FCSTD DOCUMENT  (FreeCAD 0.19R21858 (Git))
Label: printer_assembly
License: All rights reserved
LicenseURL: http://en.wikipedia.org/wiki/All_rights_reserved
objects: TechDraw::DrawViewDimension×171, Part::Feature×140, Sketcher::SketchObject×82, App::Part×58, TechDraw::DrawProjGroupItem×34, App::LinkElement×33, PartDesign::Body×30, PartDesign::Pad×29, PartDesign::Pocket×27, App::Link×26, PartDesign::Hole×16, TechDraw::DrawViewDimExtent×15, Part::FeaturePython×12, TechDraw::DrawProjGroup×12, TechDraw::DrawSVGTemplate×11, TechDraw::DrawPage×11, TechDraw::DrawViewAnnotation×10, TechDraw::DrawLeaderLine×10, TechDraw::DrawViewPart×9, App::DocumentObjectGroup×8, +10 more types
note: 449 computed .brp shape members not serialized (recipe doc carries the construction recipe); baked Part::Feature solids carry a one-line shape summary decoded from their .brp

FEATURE [Part::Feature] Part__Feature  label="KLF08"
  Placement = pos=(25.4,6e-15,50.8) rot=(0.57735,-0.57735,-0.57735;2.0944rad)
  shape: bbox 28.15 x 47.92 x 11.37 mm, 341 faces, 4 solids (baked)
FEATURE [Part::Cylinder] Cylinder  label="T8_leadscrew"
  Angle = 360
  AttacherType = Attacher::AttachEngine3D
  Height = 433
  Placement = pos=(25.4,0,43) rot=(0,0,1;0rad)
  Radius = 4
FEATURE [Sketcher::SketchObject] Sketch010
  AttachmentOffset = pos=(0,0,50.8) rot=(0,0,1;0rad)
  MapMode = 5
  Placement = pos=(0,0,50.8) rot=(0,0,1;0rad)
  Support = -> [XY_Plane010]
  expr: Constraints[9] = (2 * 31 ^ 2) ^ 0.5
  sketch-geometry (4):
    g0: Circle CenterX=25.4 CenterY=0 CenterZ=0 NormalX=0 NormalY=0 NormalZ=1 AngleXU=0 Radius=11
    g1: Circle CenterX=25.4 CenterY=21.9203 CenterZ=0 NormalX=0 NormalY=0 NormalZ=1 AngleXU=0 Radius=1.55
    g2: Circle CenterX=25.4 CenterY=-21.9203 CenterZ=0 NormalX=0 NormalY=0 NormalZ=1 AngleXU=0 Radius=1.55
    g3: LineSegment [constr] StartX=25.4 StartY=21.9203 StartZ=0 EndX=25.4 EndY=-21.9203 EndZ=0
  constraints (10):
    c: PointOnObject(g0,g-1)
    c: Coincident(g3,g1)
    c: Coincident(g3,g2)
    c: DistanceX(g-1,g0) = 25.4
    c: PointOnObject(g0,g3)
    c: Symmetric(g1,g2,g-1)
    c: Equal(g1,g2)
    c: Diameter(g1) = 3.1
    c: Diameter(g0) = 22
    c: DistanceY(g2,g1) = 43.8406
FEATURE [Sketcher::SketchObject] Sketch011
  MapMode = 5
  Placement = pos=(0,0,0) rot=(0.57735,0.57735,0.57735;2.0944rad)
  Support = -> [YZ_Plane008]
  sketch-geometry (4):
    g0: LineSegment StartX=-20 StartY=20 StartZ=0 EndX=20 EndY=20 EndZ=0
    g1: LineSegment StartX=20 StartY=20 StartZ=0 EndX=20 EndY=-5 EndZ=0
    g2: LineSegment StartX=20 StartY=-5 StartZ=0 EndX=-20 EndY=-5 EndZ=0
    g3: LineSegment StartX=-20 StartY=-5 StartZ=0 EndX=-20 EndY=20 EndZ=0
  constraints (12):
    c: Coincident(g0,g1)
    c: Coincident(g1,g2)
    c: Coincident(g2,g3)
    c: Coincident(g3,g0)
    c: Horizontal(g0)
    c: Horizontal(g2)
    c: Vertical(g1)
    c: Vertical(g3)
    c: DistanceX(g0,g0) = 40
    c: DistanceY(g1,g0) = 25
    c: DistanceY(g-1,g0) = 20
    c: DistanceX(g-1,g0) = 20
FEATURE [Sketcher::SketchObject] Sketch006
  AttachmentOffset = pos=(0,0,50.8) rot=(0,0,1;0rad)
  MapMode = 5
  Placement = pos=(50.8,-1.13e-14,1.13e-14) rot=(0.57735,0.57735,0.57735;2.0944rad)
  Support = -> [YZ_Plane011]
  sketch-geometry (8):
    g0: ArcOfCircle CenterX=-131 CenterY=25.4 CenterZ=0 NormalX=0 NormalY=0 NormalZ=1 AngleXU=0 Radius=5 StartAngle=1.5708 EndAngle=4.71239
    g1: ArcOfCircle CenterX=-95 CenterY=25.4 CenterZ=0 NormalX=0 NormalY=0 NormalZ=1 AngleXU=0 Radius=5 StartAngle=4.71239 EndAngle=7.85398
    g2: LineSegment StartX=-131 StartY=20.4 StartZ=0 EndX=-95 EndY=20.4 EndZ=0
    g3: LineSegment StartX=-131 StartY=30.4 StartZ=0 EndX=-95 EndY=30.4 EndZ=0
    g4: ArcOfCircle CenterX=95 CenterY=25.4 CenterZ=0 NormalX=0 NormalY=0 NormalZ=1 AngleXU=0 Radius=5 StartAngle=1.5708 EndAngle=4.71239
    g5: ArcOfCircle CenterX=131 CenterY=25.4 CenterZ=0 NormalX=0 NormalY=0 NormalZ=1 AngleXU=0 Radius=5 StartAngle=4.71239 EndAngle=7.85398
    g6: LineSegment StartX=95 StartY=20.4 StartZ=0 EndX=131 EndY=20.4 EndZ=0
    g7: LineSegment StartX=95 StartY=30.4 StartZ=0 EndX=131 EndY=30.4 EndZ=0
  constraints (18):
    c: Tangent(g0,g3) = 1.5708
    c: Tangent(g0,g2) = -1.5708
    c: Tangent(g2,g1) = -1.5708
    c: Tangent(g3,g1) = 1.5708
    c: Horizontal(g2)
    c: Equal(g0,g1)
    c: Tangent(g4,g7) = 1.5708
    c: Tangent(g4,g6) = -1.5708
    c: Tangent(g6,g5) = -1.5708
    c: Tangent(g7,g5) = 1.5708
    c: Horizontal(g6)
    c: Diameter(g4) = 10
    c: Equal(g4,g1)
    c: Symmetric(g4,g1,g-2)
    c: Symmetric(g0,g5,g-2)
    c: DistanceY(g-1,g4) = 25.4
    c: DistanceX(g1,g4) = 190
    c: DistanceX(g0,g5) = 262
FEATURE [Sketcher::SketchObject] Sketch012
  AttachmentOffset = pos=(0,0,50.8) rot=(0,0,1;0rad)
  MapMode = 5
  Placement = pos=(0,0,50.8) rot=(0,0,1;0rad)
  Support = -> [XY_Plane011]
  sketch-geometry (4):
    g0: Circle CenterX=25.4 CenterY=0 CenterZ=0 NormalX=0 NormalY=0 NormalZ=1 AngleXU=0 Radius=9
    g1: Circle CenterX=25.4 CenterY=18.5 CenterZ=0 NormalX=0 NormalY=0 NormalZ=1 AngleXU=0 Radius=2.25
    g2: Circle CenterX=25.4 CenterY=-18.5 CenterZ=0 NormalX=0 NormalY=0 NormalZ=1 AngleXU=0 Radius=2.25
    g3: LineSegment [constr] StartX=25.4 StartY=18.5 StartZ=0 EndX=25.4 EndY=-18.5 EndZ=0
  constraints (10):
    c: PointOnObject(g0,g-1)
    c: Coincident(g3,g1)
    c: Coincident(g3,g2)
    c: PointOnObject(g0,g3)
    c: Symmetric(g1,g2,g-1)
    c: Equal(g1,g2)
    c: DistanceY(g2,g1) = 37
    c: DistanceX(g-1,g0) = 25.4
    c: Diameter(g1) = 4.5
    c: Diameter(g0) = 18
FEATURE [Part::Cylinder] Cylinder001  label="12x500mm_shaft"
  Angle = 360
  AttacherType = Attacher::AttachEngine3D
  Height = 500
  Placement = pos=(38.74,95.03,0) rot=(0,0,1;0rad)
  Radius = 6
FEATURE [App::Link] Link  label="12x500mm_shaft001"
  LinkPlacement = pos=(38.74,-95.03,0) rot=(0,0,1;0rad)
  LinkedObject = -> Cylinder001
  Placement = pos=(38.74,-95.03,0) rot=(0,0,1;0rad)
FEATURE [App::Link] Link010  label="adj_assy001"
  LinkPlacement = pos=(-153,158,0) rot=(0,0,1;3.92699rad)
  LinkedObject = -> Part011
  Placement = pos=(-153,158,0) rot=(0,0,1;3.92699rad)
FEATURE [App::Link] Link001  label="adj_assy002"
  LinkPlacement = pos=(-153,-158,0) rot=(0,0,-1;0.785398rad)
  LinkedObject = -> Part011
  Placement = pos=(-153,-158,0) rot=(0,0,-1;0.785398rad)
FEATURE [Part::Cylinder] Cylinder002  label="0.25in_threaded_rod"
  Angle = 360
  AttacherType = Attacher::AttachEngine3D
  Height = 40
  Placement = pos=(0,0,-33.65) rot=(0,0,1;0rad)
  Radius = 3.175
FEATURE [Sketcher::SketchObject] Sketch013
  MapMode = 5
  Support = -> [XY_Plane016]
  sketch-geometry (7):
    g0: LineSegment StartX=-160 StartY=165 StartZ=0 EndX=160 EndY=165 EndZ=0
    g1: LineSegment StartX=160 StartY=165 StartZ=0 EndX=160 EndY=-165 EndZ=0
    g2: LineSegment StartX=160 StartY=-165 StartZ=0 EndX=-160 EndY=-165 EndZ=0
    g3: LineSegment StartX=-160 StartY=-165 StartZ=0 EndX=-160 EndY=165 EndZ=0
    g4: Circle CenterX=-153 CenterY=158 CenterZ=0 NormalX=0 NormalY=0 NormalZ=1 AngleXU=0 Radius=3.175
    g5: Circle CenterX=-153 CenterY=-158 CenterZ=0 NormalX=0 NormalY=0 NormalZ=1 AngleXU=0 Radius=3.175
    g6: Circle CenterX=153 CenterY=0 CenterZ=0 NormalX=0 NormalY=0 NormalZ=1 AngleXU=0 Radius=3.175
  constraints (20):
    c: Coincident(g0,g1)
    c: Coincident(g1,g2)
    c: Coincident(g2,g3)
    c: Coincident(g3,g0)
    c: Horizontal(g0)
    c: Horizontal(g2)
    c: Vertical(g1)
    c: Vertical(g3)
    c: DistanceX(g0,g0) = 320  'bed_w'
    c: DistanceY(g1,g1) = 330  'bed_d'
    c: DistanceY(g-1,g0) = 165
    c: DistanceX(g-1,g0) = 160
    c: DistanceX(g4,g-1) = 153
    c: DistanceY(g-1,g4) = 158
    c: Symmetric(g4,g5,g-1)
    c: PointOnObject(g6,g-1)
    c: DistanceX(g-1,g6) = 153
    c: Equal(g4,g5)
    c: Equal(g5,g6)
    c: Diameter(g4) = 6.35  'adj_screw_dia'
FEATURE [PartDesign::Pad] Pad006
  AllowMultiFace = false
  Length = 6.35
  Length2 = 100
  Profile = -> Sketch013
  Type = 0
FEATURE [PartDesign::Body] Body006
  Group = -> [Sketch013,Pad006]
  Origin = -> Origin016
  Tip = -> Pad006
FEATURE [App::Part] Part001  label="bed_plate"
  Group = -> [Body006]
  Origin = -> Origin013
FEATURE [Sketcher::SketchObject] Sketch014
  MapMode = 5
  Placement = pos=(0,0,0) rot=(1,0,0;1.5708rad)
  Support = -> [XZ_Plane001]
  expr: Constraints[15] = 1.25 * 25.4
  expr: Constraints[17] = 0.5 * 25.4
  expr: Constraints[14] = 0.2 * 25.4
  expr: Constraints[13] = 0.2 * 25.4
  expr: Constraints[12] = 1 / 8 * 25.4
  sketch-geometry (6):
    g0: LineSegment StartX=0 StartY=3.175 StartZ=0 EndX=10.16 EndY=3.175 EndZ=0
    g1: LineSegment StartX=10.16 StartY=3.175 StartZ=0 EndX=10.16 EndY=7.62 EndZ=0
    g2: LineSegment StartX=10.16 StartY=7.62 StartZ=0 EndX=5.08 EndY=12.7 EndZ=0
    g3: LineSegment StartX=5.08 StartY=12.7 StartZ=0 EndX=5.08 EndY=31.75 EndZ=0
    g4: LineSegment StartX=5.08 StartY=31.75 StartZ=0 EndX=0 EndY=31.75 EndZ=0
    g5: LineSegment StartX=0 StartY=31.75 StartZ=0 EndX=0 EndY=3.175 EndZ=0
  constraints (18):
    c: Coincident(g0,g1)
    c: Coincident(g1,g2)
    c: Coincident(g2,g3)
    c: Vertical(g3)
    c: Coincident(g3,g4)
    c: Horizontal(g4)
    c: Coincident(g4,g5)
    c: Coincident(g5,g0)
    c: Vertical(g5)
    c: Horizontal(g0)
    c: Vertical(g1)
    c: Angle(g2,g0) = 0.785398
    c: DistanceY(g-1,g0) = 3.175
    c: DistanceX(g4,g4) = 5.08
    c: DistanceX(g2,g1) = 5.08
    c: DistanceY(g-1,g4) = 31.75
    c: PointOnObject(g0,g-2)
    c: DistanceY(g-1,g2) = 12.7
FEATURE [PartDesign::Revolution] Revolution
  AllowMultiFace = false
  Angle = 360
  Axis = (1,0,0)
  Base = (0,0,0)
  Placement = pos=(0,0,0) rot=(1,0,0;1.5708rad)
  Profile = -> Sketch014
  ReferenceAxis = -> X_Axis001
FEATURE [PartDesign::Body] Body007
  Group = -> [Sketch014,Revolution]
  Origin = -> Origin001
  Tip = -> Revolution
FEATURE [App::Part] Part012  label="adj_knob"
  Group = -> [Body007]
  Origin = -> Origin017
  Placement = pos=(1.4e-15,0,-6.35) rot=(0,1,0;1.5708rad)
FEATURE [Sketcher::SketchObject] Sketch015
  MapMode = 5
  Placement = pos=(0,0,0) rot=(0.57735,0.57735,0.57735;2.0944rad)
  Support = -> [YZ_Plane019]
  sketch-geometry (5):
    g0: LineSegment StartX=0 StartY=0 StartZ=0 EndX=61.979 EndY=0 EndZ=0
    g1: LineSegment StartX=113.021 StartY=-30 StartZ=0 EndX=175 EndY=-30 EndZ=0
    g2: LineSegment StartX=79.9395 StartY=-7.43949 StartZ=0 EndX=95.0605 EndY=-22.5605 EndZ=0
    g3: ArcOfCircle CenterX=61.979 CenterY=-25.4 CenterZ=0 NormalX=0 NormalY=0 NormalZ=1 AngleXU=0 Radius=25.4 StartAngle=0.785398 EndAngle=1.5708
    g4: ArcOfCircle CenterX=113.021 CenterY=-4.6 CenterZ=0 NormalX=0 NormalY=0 NormalZ=1 AngleXU=0 Radius=25.4 StartAngle=3.92699 EndAngle=4.71239
  constraints (13):
    c: Coincident(g0,g-1)
    c: Horizontal(g1)
    c: Tangent(g0,g3) = 1.5708
    c: Tangent(g2,g3) = 1.5708
    c: Tangent(g2,g4) = -1.5708
    c: Tangent(g1,g4) = -1.5708
    c: Equal(g3,g4)
    c: Horizontal(g0)
    c: Equal(g0,g1)
    c: DistanceY(g1,g0) = 30
    c: DistanceX(g0,g1) = 175
    c: Radius(g3) = 25.4
    c: Angle(g0,g2) = 2.35619
FEATURE [Sketcher::SketchObject] Sketch016
  MapMode = 5
  Support = -> [XY_Plane019]
  sketch-geometry (4):
    g0: ArcOfCircle CenterX=0 CenterY=0 CenterZ=0 NormalX=0 NormalY=0 NormalZ=1 AngleXU=0 Radius=8 StartAngle=3.14159 EndAngle=6.28319
    g1: ArcOfCircle CenterX=-2e-16 CenterY=25 CenterZ=0 NormalX=0 NormalY=0 NormalZ=1 AngleXU=0 Radius=8 StartAngle=0 EndAngle=3.14159
    g2: LineSegment StartX=8 StartY=-2e-15 StartZ=0 EndX=8 EndY=25 EndZ=0
    g3: LineSegment StartX=-8 StartY=-2.6e-15 StartZ=0 EndX=-8 EndY=25 EndZ=0
  constraints (9):
    c: Tangent(g0,g3) = 1.5708
    c: Tangent(g0,g2) = -1.5708
    c: Tangent(g2,g1) = -1.5708
    c: Tangent(g3,g1) = 1.5708
    c: Vertical(g2)
    c: Equal(g0,g1)
    c: Coincident(g0,g-1)
    c: Diameter(g1) = 16
    c: DistanceY(g0,g1) = 25
FEATURE [Sketcher::SketchObject] Sketch017
  MapMode = 5
  Support = -> [XY_Plane019]
  sketch-geometry (4):
    g0: ArcOfCircle CenterX=0 CenterY=125 CenterZ=0 NormalX=0 NormalY=0 NormalZ=1 AngleXU=0 Radius=3.5 StartAngle=3.14159 EndAngle=6.28319
    g1: ArcOfCircle CenterX=-6.15e-14 CenterY=165 CenterZ=0 NormalX=0 NormalY=0 NormalZ=1 AngleXU=0 Radius=3.5 StartAngle=-3.73e-14 EndAngle=3.14159
    g2: LineSegment StartX=3.5 StartY=125 StartZ=0 EndX=3.5 EndY=165 EndZ=0
    g3: LineSegment StartX=-3.5 StartY=125 StartZ=0 EndX=-3.5 EndY=165 EndZ=0
  constraints (10):
    c: Tangent(g0,g3) = 1.5708
    c: Tangent(g0,g2) = -1.5708
    c: Tangent(g2,g1) = -1.5708
    c: Tangent(g3,g1) = 1.5708
    c: Vertical(g2)
    c: Equal(g0,g1)
    c: PointOnObject(g0,g-2)
    c: DistanceY(g-1,g0) = 125
    c: DistanceY(g-1,g1) = 165
    c: Diameter(g1) = 7
FEATURE [Sketcher::SketchObject] Sketch018
  MapMode = 5
  Support = -> [XY_Plane021]
  sketch-geometry (4):
    g0: LineSegment StartX=-63.5 StartY=177.8 StartZ=0 EndX=393.7 EndY=177.8 EndZ=0
    g1: LineSegment StartX=393.7 StartY=177.8 StartZ=0 EndX=393.7 EndY=-177.8 EndZ=0
    g2: LineSegment StartX=393.7 StartY=-177.8 StartZ=0 EndX=-63.5 EndY=-177.8 EndZ=0
    g3: LineSegment StartX=-63.5 StartY=-177.8 StartZ=0 EndX=-63.5 EndY=177.8 EndZ=0
  constraints (11):
    c: Coincident(g0,g1)
    c: Coincident(g1,g2)
    c: Coincident(g2,g3)
    c: Coincident(g3,g0)
    c: Horizontal(g0)
    c: Horizontal(g2)
    c: Vertical(g1)
    c: DistanceY(g-1,g0) = 177.8
    c: DistanceX(g0,g0) = 457.2
    c: DistanceX(g0,g-1) = 63.5
    c: Symmetric(g0,g2,g-1)
FEATURE [PartDesign::Pad] Pad008
  AllowMultiFace = false
  Length = 19.05
  Length2 = 100
  Profile = -> Sketch018
  Reversed = true
  Type = 0
FEATURE [Sketcher::SketchObject] Sketch019
  MapMode = 5
  Support = -> [XY_Plane021]
  sketch-geometry (12):
    g0: LineSegment StartX=0 StartY=-127 StartZ=0 EndX=0 EndY=-177.8 EndZ=0
    g1: LineSegment StartX=0 StartY=-177.8 StartZ=0 EndX=-12.7 EndY=-177.8 EndZ=0
    g2: LineSegment StartX=-12.7 StartY=-177.8 StartZ=0 EndX=-12.7 EndY=-136.525 EndZ=0
    g3: LineSegment StartX=-63.5 StartY=-127 StartZ=0 EndX=-63.5 EndY=-136.525 EndZ=0
    g4: LineSegment StartX=-63.5 StartY=-136.525 StartZ=0 EndX=-12.7 EndY=-136.525 EndZ=0
    g5: LineSegment StartX=-63.5 StartY=-127 StartZ=0 EndX=0 EndY=-127 EndZ=0
    g6: LineSegment StartX=-12.7 StartY=136.525 StartZ=0 EndX=-63.5 EndY=136.525 EndZ=0
    g7: LineSegment StartX=-63.5 StartY=136.525 StartZ=0 EndX=-63.5 EndY=127 EndZ=0
    g8: LineSegment StartX=-63.5 StartY=127 StartZ=0 EndX=0 EndY=127 EndZ=0
    g9: LineSegment StartX=0 StartY=127 StartZ=0 EndX=0 EndY=177.8 EndZ=0
    g10: LineSegment StartX=0 StartY=177.8 StartZ=0 EndX=-12.7 EndY=177.8 EndZ=0
    g11: LineSegment StartX=-12.7 StartY=177.8 StartZ=0 EndX=-12.7 EndY=136.525 EndZ=0
  constraints (36):
    c: Coincident(g0,g1)
    c: Coincident(g1,g2)
    c: Horizontal(g1)
    c: Vertical(g0)
    c: Vertical(g2)
    c: Coincident(g3,g4)
    c: Horizontal(g4)
    c: Vertical(g3)
    c: Coincident(g2,g4)
    c: Coincident(g5,g3)
    c: Coincident(g5,g0)
    c: Horizontal(g5)
    c: DistanceY(g0,g-1) = 177.8
    c: DistanceX(g5,g5) = 63.5
    c: DistanceY(g3,g3) = 9.525
    c: PointOnObject(g0,g-2)
    c: DistanceY(g0,g0) = 50.8
    c: DistanceX(g1,g1) = 12.7
    c: Horizontal(g6)
    c: Coincident(g6,g7)
    c: Coincident(g7,g8)
    c: Coincident(g8,g9)
    c: Coincident(g9,g10)
    c: Coincident(g10,g11)
    c: Coincident(g11,g6)
    c: Vertical(g11)
    c: Vertical(g9)
    c: Vertical(g7)
    c: Horizontal(g10)
    c: Horizontal(g8)
    c: PointOnObject(g8,g-2)
    c: DistanceX(g10,g10) = 12.7
    c: DistanceX(g8,g8) = 63.5
    c: DistanceY(g9,g9) = 50.8
    c: DistanceY(g7,g7) = 9.525
    c: DistanceY(g-1,g9) = 177.8
FEATURE [PartDesign::Pad] Pad009
  AllowMultiFace = false
  BaseFeature = -> Pad008
  Length = 127
  Length2 = 100
  Profile = -> Sketch019
  Type = 0
FEATURE [Sketcher::SketchObject] Sketch020
  MapMode = 5
  Placement = pos=(0,0,0) rot=(1,0,0;1.5708rad)
  Support = -> [XZ_Plane021]
  sketch-geometry (3):
    g0: LineSegment StartX=-63.5 StartY=0 StartZ=0 EndX=-12.7 EndY=127 EndZ=0
    g1: LineSegment StartX=-12.7 StartY=127 StartZ=0 EndX=-63.5 EndY=127 EndZ=0
    g2: LineSegment StartX=-63.5 StartY=127 StartZ=0 EndX=-63.5 EndY=0 EndZ=0
  constraints (9):
    c: Coincident(g0,g1)
    c: Horizontal(g1)
    c: Coincident(g1,g2)
    c: Coincident(g2,g0)
    c: Vertical(g2)
    c: PointOnObject(g0,g-1)
    c: DistanceY(g2,g2) = 127
    c: DistanceX(g0,g-1) = 12.7
    c: DistanceX(g0,g-1) = 63.5
FEATURE [PartDesign::Pocket] Pocket010
  AllowMultiFace = false
  BaseFeature = -> Pad009
  Length = 5
  Length2 = 100
  Midplane = true
  Profile = -> Sketch020
  Type = 1
FEATURE [Sketcher::SketchObject] Sketch021
  MapMode = 5
  Placement = pos=(0,0,0) rot=(0.57735,0.57735,0.57735;2.0944rad)
  Support = -> [YZ_Plane021]
  sketch-geometry (4):
    g0: Circle CenterX=-152.4 CenterY=101.6 CenterZ=0 NormalX=0 NormalY=0 NormalZ=1 AngleXU=0 Radius=6.35
    g1: Circle CenterX=-152.4 CenterY=25.4 CenterZ=0 NormalX=0 NormalY=0 NormalZ=1 AngleXU=0 Radius=6.35
    g2: Circle CenterX=152.4 CenterY=101.6 CenterZ=0 NormalX=0 NormalY=0 NormalZ=1 AngleXU=0 Radius=6.35
    g3: Circle CenterX=152.4 CenterY=25.4 CenterZ=0 NormalX=0 NormalY=0 NormalZ=1 AngleXU=0 Radius=6.35
  constraints (10):
    c: Symmetric(g1,g3,g-2)
    c: Symmetric(g0,g2,g-2)
    c: DistanceX(g0,g-1) = 152.4
    c: Vertical(g0,g1)
    c: Diameter(g0) = 12.7
    c: Equal(g0,g1)
    c: Equal(g1,g3)
    c: Equal(g3,g2)
    c: DistanceY(g-1,g0) = 101.6
    c: DistanceY(g-1,g1) = 25.4
FEATURE [PartDesign::Pocket] Pocket009
  AllowMultiFace = false
  BaseFeature = -> Pocket010
  Length = 5
  Length2 = 100
  Profile = -> Sketch021
  Type = 1
FEATURE [Part::Feature] Part__Feature001  label="V-Slot 20x80x500 Linear Rail"
  Placement = pos=(250,0,16.35) rot=(0,-1,0;1.5708rad)
  shape: bbox 500 x 80 x 20 mm, 204 faces (baked)
FEATURE [App::LinkElement] Link007_i0
  LinkPlacement = pos=(-95,21,8.34465e-06) rot=(1,0,0;1.5708rad)
  LinkedObject = -> Part__Feature002
  Placement = pos=(-95,21,8.34465e-06) rot=(1,0,0;1.5708rad)
FEATURE [App::LinkElement] Link007_i1
  LinkPlacement = pos=(95,-21,-1.62125e-05) rot=(1,0,0;1.5708rad)
  LinkedObject = -> Part__Feature002
  Placement = pos=(95,-21,-1.62125e-05) rot=(1,0,0;1.5708rad)
FEATURE [Part::Feature] Part__Feature002  label="SC12UU"
  Placement = pos=(-95,-21,5e-15) rot=(1,0,0;1.5708rad)
  shape: bbox 42 x 36 x 28 mm, 110 faces (baked)
FEATURE [App::LinkElement] Link007_i2
  LinkPlacement = pos=(95,21,-6.07967e-06) rot=(1,0,0;1.5708rad)
  LinkedObject = -> Part__Feature002
  Placement = pos=(95,21,-6.07967e-06) rot=(1,0,0;1.5708rad)
FEATURE [App::Link] Link007  label="SC12UU001"
  ElementCount = 3
  ElementList = -> [Link007_i0,Link007_i1,Link007_i2]
  LinkedObject = -> Part__Feature002
FEATURE [App::DocumentObjectGroup] Group002  label="SCS12UU"
  Group = -> [Part__Feature002,Link007]
FEATURE [Part::Feature] Part__Feature034  label="8mm Acme Anti Backlash Nut Block"
  Placement = pos=(-4e-15,-16.5,-28) rot=(0,0.707107,0.707107;3.14159rad)
  shape: bbox 34 x 33 x 12 mm, 45 faces (baked)
FEATURE [Part::Cylinder] Cylinder003  label="5mm_shaft"
  Angle = 360
  AttacherType = Attacher::AttachEngine3D
  Height = 22
  Placement = pos=(-1,-5.9,-11) rot=(0,0,1;0rad)
  Radius = 2.5
FEATURE [Part::Feature] Part__Feature033  label="plastic_washer"
  Placement = pos=(-1,-5.9,5) rot=(1,0,0;1.5708rad)
  shape: bbox 11 x 11 x 1.1 mm, 6 faces (baked)
FEATURE [App::Link] Link008  label="plastic_washer_2"
  LinkPlacement = pos=(-1,-5.90002,-5.99999) rot=(1,0,0;1.5708rad)
  LinkedObject = -> Part__Feature033
  Placement = pos=(-1,-5.90002,-5.99999) rot=(1,0,0;1.5708rad)
FEATURE [Sketcher::SketchObject] Sketch022
  MapMode = 5
  Placement = pos=(0,0,0) rot=(1,0,0;1.5708rad)
  Support = -> [XZ_Plane028]
  sketch-geometry (8):
    g0: ArcOfCircle CenterX=-271.33 CenterY=27.34 CenterZ=0 NormalX=0 NormalY=0 NormalZ=1 AngleXU=0 Radius=6.163 StartAngle=1.57072 EndAngle=4.71231
    g1: ArcOfCircle CenterX=267 CenterY=27.3 CenterZ=0 NormalX=0 NormalY=0 NormalZ=1 AngleXU=0 Radius=6.163 StartAngle=4.71231 EndAngle=7.85391
    g2: LineSegment StartX=-271.33 StartY=21.177 StartZ=0 EndX=267 EndY=21.137 EndZ=0
    g3: LineSegment StartX=-271.33 StartY=33.503 StartZ=0 EndX=267 EndY=33.463 EndZ=0
    g4: ArcOfCircle CenterX=-271.33 CenterY=27.34 CenterZ=0 NormalX=0 NormalY=0 NormalZ=1 AngleXU=0 Radius=7.163 StartAngle=1.57072 EndAngle=4.71231
    g5: ArcOfCircle CenterX=267 CenterY=27.3 CenterZ=0 NormalX=0 NormalY=0 NormalZ=1 AngleXU=0 Radius=7.163 StartAngle=4.71231 EndAngle=7.85391
    g6: LineSegment StartX=-271.331 StartY=20.177 StartZ=0 EndX=266.999 EndY=20.137 EndZ=0
    g7: LineSegment StartX=-271.329 StartY=34.503 StartZ=0 EndX=267.001 EndY=34.463 EndZ=0
  constraints (18):
    c: Tangent(g0,g3) = 1.5708
    c: Tangent(g0,g2) = -1.5708
    c: Tangent(g2,g1) = -1.5708
    c: Tangent(g3,g1) = 1.5708
    c: Equal(g0,g1)
    c: Tangent(g4,g7) = 1.5708
    c: Tangent(g4,g6) = -1.5708
    c: Tangent(g6,g5) = -1.5708
    c: Tangent(g7,g5) = 1.5708
    c: Equal(g4,g5)
    c: Coincident(g4,g0)
    c: Coincident(g5,g1)
    c: Distance(g5,g1) = 1
    c: DistanceX(g-1,g1) = 267
    c: DistanceY(g-1,g1) = 27.3
    c: DistanceX(g0,g-1) = 271.33
    c: DistanceY(g-1,g0) = 27.34
    c: Radius(g4) = 7.163
FEATURE [PartDesign::Pad] Pad010
  AllowMultiFace = false
  Length = 6
  Length2 = 100
  Midplane = true
  Placement = pos=(0,0,0) rot=(1,0,0;1.5708rad)
  Profile = -> Sketch022
  Type = 0
FEATURE [PartDesign::Body] Body009  label="y_belt"
  Group = -> [Sketch022,Pad010]
  Origin = -> Origin028
  Tip = -> Pad010
FEATURE [Sketcher::SketchObject] Sketch023
  MapMode = 5
  Support = -> [XY_Plane029]
  sketch-geometry (6):
    g0: LineSegment StartX=-116.25 StartY=40 StartZ=0 EndX=116.25 EndY=40 EndZ=0
    g1: LineSegment StartX=116.25 StartY=40 StartZ=0 EndX=116.25 EndY=-40 EndZ=0
    g2: LineSegment StartX=116.25 StartY=-40 StartZ=0 EndX=-116.25 EndY=-40 EndZ=0
    g3: LineSegment StartX=-116.25 StartY=-40 StartZ=0 EndX=-116.25 EndY=40 EndZ=0
    g4: LineSegment [constr] StartX=-116.25 StartY=40 StartZ=0 EndX=116.25 EndY=-40 EndZ=0
    g5: LineSegment [constr] StartX=116.25 StartY=40 StartZ=0 EndX=-116.25 EndY=-40 EndZ=0
  constraints (16):
    c: Coincident(g0,g1)
    c: Coincident(g1,g2)
    c: Coincident(g2,g3)
    c: Coincident(g3,g0)
    c: Horizontal(g0)
    c: Horizontal(g2)
    c: Vertical(g1)
    c: Vertical(g3)
    c: DistanceX(g0,g0) = 232.5  'plate_width'
    c: DistanceY(g3,g3) = 80  'plate_height'
    c: Coincident(g4,g0)
    c: Coincident(g4,g1)
    c: Coincident(g5,g0)
    c: Coincident(g5,g2)
    c: PointOnObject(g-1,g5)
    c: PointOnObject(g-1,g4)
FEATURE [PartDesign::Pad] Pad011
  AllowMultiFace = false
  Length = 6.35
  Length2 = 100
  Profile = -> Sketch023
  Type = 0
FEATURE [Sketcher::SketchObject] Sketch024
  AttachmentOffset = pos=(0,0,6.35) rot=(0,0,1;0rad)
  MapMode = 5
  Placement = pos=(0,0,6.35) rot=(0,0,1;0rad)
  Support = -> [XY_Plane029]
  sketch-geometry (55):
    g0: Circle CenterX=-110.5 CenterY=34 CenterZ=0 NormalX=0 NormalY=0 NormalZ=1 AngleXU=0 Radius=2.55
    g1: Circle CenterX=-110.5 CenterY=8 CenterZ=0 NormalX=0 NormalY=0 NormalZ=1 AngleXU=0 Radius=2.55
    g2: Circle CenterX=-80 CenterY=34 CenterZ=0 NormalX=0 NormalY=0 NormalZ=1 AngleXU=0 Radius=2.55
    g3: Circle CenterX=-80 CenterY=8 CenterZ=0 NormalX=0 NormalY=0 NormalZ=1 AngleXU=0 Radius=2.55
    g4: LineSegment [constr] StartX=-110.5 StartY=34 StartZ=0 EndX=-80 EndY=34 EndZ=0
    g5: LineSegment [constr] StartX=-80 StartY=34 StartZ=0 EndX=-80 EndY=8 EndZ=0
    g6: LineSegment [constr] StartX=-80 StartY=8 StartZ=0 EndX=-110.5 EndY=8 EndZ=0
    g7: LineSegment [constr] StartX=-110.5 StartY=8 StartZ=0 EndX=-110.5 EndY=34 EndZ=0
    g8: GeomPoint X=-95.25 Y=21 Z=0
    g9: LineSegment [constr] StartX=-110.5 StartY=34 StartZ=0 EndX=-80 EndY=8 EndZ=0
    g10: LineSegment [constr] StartX=-80 StartY=34 StartZ=0 EndX=-110.5 EndY=8 EndZ=0
    g11: Circle CenterX=80 CenterY=34 CenterZ=0 NormalX=0 NormalY=0 NormalZ=1 AngleXU=0 Radius=2.55
    g12: Circle CenterX=80 CenterY=8 CenterZ=0 NormalX=0 NormalY=0 NormalZ=1 AngleXU=0 Radius=2.55
    g13: Circle CenterX=110.5 CenterY=34 CenterZ=0 NormalX=0 NormalY=0 NormalZ=1 AngleXU=0 Radius=2.55
    g14: Circle CenterX=110.5 CenterY=8 CenterZ=0 NormalX=0 NormalY=0 NormalZ=1 AngleXU=0 Radius=2.55
    g15: LineSegment [constr] StartX=80 StartY=34 StartZ=0 EndX=110.5 EndY=34 EndZ=0
    g16: LineSegment [constr] StartX=110.5 StartY=34 StartZ=0 EndX=110.5 EndY=8 EndZ=0
    g17: LineSegment [constr] StartX=110.5 StartY=8 StartZ=0 EndX=80 EndY=8 EndZ=0
    g18: LineSegment [constr] StartX=80 StartY=8 StartZ=0 EndX=80 EndY=34 EndZ=0
    g19: GeomPoint X=95.25 Y=21 Z=0
    g20: LineSegment [constr] StartX=80 StartY=34 StartZ=0 EndX=110.5 EndY=8 EndZ=0
    g21: LineSegment [constr] StartX=110.5 StartY=34 StartZ=0 EndX=80 EndY=8 EndZ=0
    g22: LineSegment [constr] StartX=-110.5 StartY=34 StartZ=0 EndX=80 EndY=34 EndZ=0
    g23: Circle CenterX=-110.5 CenterY=-8 CenterZ=0 NormalX=0 NormalY=0 NormalZ=1 AngleXU=0 Radius=2.55
    g24: Circle CenterX=-110.5 CenterY=-34 CenterZ=0 NormalX=0 NormalY=0 NormalZ=1 AngleXU=0 Radius=2.55
    g25: Circle CenterX=-80 CenterY=-8 CenterZ=0 NormalX=0 NormalY=0 NormalZ=1 AngleXU=0 Radius=2.55
    g26: Circle CenterX=-80 CenterY=-34 CenterZ=0 NormalX=0 NormalY=0 NormalZ=1 AngleXU=0 Radius=2.55
    g27: LineSegment [constr] StartX=-110.5 StartY=-8 StartZ=0 EndX=-80 EndY=-8 EndZ=0
    g28: LineSegment [constr] StartX=-80 StartY=-8 StartZ=0 EndX=-80 EndY=-34 EndZ=0
    g29: LineSegment [constr] StartX=-80 StartY=-34 StartZ=0 EndX=-110.5 EndY=-34 EndZ=0
    g30: LineSegment [constr] StartX=-110.5 StartY=-34 StartZ=0 EndX=-110.5 EndY=-8 EndZ=0
    g31: GeomPoint X=-95.25 Y=-21 Z=0
    g32: LineSegment [constr] StartX=-110.5 StartY=-8 StartZ=0 EndX=-80 EndY=-34 EndZ=0
    g33: LineSegment [constr] StartX=-80 StartY=-8 StartZ=0 EndX=-110.5 EndY=-34 EndZ=0
    g34: LineSegment [constr] StartX=-110.5 StartY=34 StartZ=0 EndX=-110.5 EndY=-8 EndZ=0
    g35: Circle CenterX=80 CenterY=-8 CenterZ=0 NormalX=0 NormalY=0 NormalZ=1 AngleXU=0 Radius=2.55
    g36: Circle CenterX=80 CenterY=-34 CenterZ=0 NormalX=0 NormalY=0 NormalZ=1 AngleXU=0 Radius=2.55
    g37: Circle CenterX=110.5 CenterY=-8 CenterZ=0 NormalX=0 NormalY=0 NormalZ=1 AngleXU=0 Radius=2.55
    g38: Circle CenterX=110.5 CenterY=-34 CenterZ=0 NormalX=0 NormalY=0 NormalZ=1 AngleXU=0 Radius=2.55
    g39: LineSegment [constr] StartX=80 StartY=-8 StartZ=0 EndX=110.5 EndY=-8 EndZ=0
    g40: LineSegment [constr] StartX=110.5 StartY=-8 StartZ=0 EndX=110.5 EndY=-34 EndZ=0
    g41: LineSegment [constr] StartX=110.5 StartY=-34 StartZ=0 EndX=80 EndY=-34 EndZ=0
    g42: LineSegment [constr] StartX=80 StartY=-34 StartZ=0 EndX=80 EndY=-8 EndZ=0
    g43: GeomPoint X=95.25 Y=-21 Z=0
    g44: LineSegment [constr] StartX=80 StartY=-8 StartZ=0 EndX=110.5 EndY=-34 EndZ=0
    g45: LineSegment [constr] StartX=110.5 StartY=-8 StartZ=0 EndX=80 EndY=-34 EndZ=0
    g46: LineSegment [constr] StartX=-110.5 StartY=-8 StartZ=0 EndX=80 EndY=-8 EndZ=0
    g47: Circle CenterX=-10 CenterY=24 CenterZ=0 NormalX=0 NormalY=0 NormalZ=1 AngleXU=0 Radius=2.55
    g48: Circle CenterX=10 CenterY=24 CenterZ=0 NormalX=0 NormalY=0 NormalZ=1 AngleXU=0 Radius=2.55
    g49: Circle CenterX=10 CenterY=-24 CenterZ=0 NormalX=0 NormalY=0 NormalZ=1 AngleXU=0 Radius=2.55
    g50: Circle CenterX=-10 CenterY=-24 CenterZ=0 NormalX=0 NormalY=0 NormalZ=1 AngleXU=0 Radius=2.55
    g51: LineSegment [constr] StartX=-10 StartY=24 StartZ=0 EndX=10 EndY=24 EndZ=0
    g52: LineSegment [constr] StartX=10 StartY=24 StartZ=0 EndX=10 EndY=-24 EndZ=0
    g53: LineSegment [constr] StartX=10 StartY=-24 StartZ=0 EndX=-10 EndY=-24 EndZ=0
    g54: LineSegment [constr] StartX=-10 StartY=-24 StartZ=0 EndX=-10 EndY=24 EndZ=0
  constraints (130):
    c: Coincident(g4,g5)
    c: Coincident(g5,g6)
    c: Coincident(g6,g7)
    c: Coincident(g7,g4)
    c: Horizontal(g4)
    c: Horizontal(g6)
    c: Vertical(g5)
    c: Vertical(g7)
    c: Coincident(g4,g0)
    c: Coincident(g3,g5)
    c: Coincident(g2,g4)
    c: Coincident(g6,g1)
    c: Diameter(g0) = 5.1
    c: Equal(g0,g2)
    c: Equal(g2,g3)
    c: Equal(g3,g1)
    c: Coincident(g9,g0)
    c: Coincident(g9,g3)
    c: Coincident(g10,g2)
    c: Coincident(g10,g1)
    c: PointOnObject(g8,g10)
    c: PointOnObject(g8,g9)
    c: DistanceX(g6,g6) = 30.5
    c: DistanceY(g5,g5) = 26
    c: DistanceY(g-1,g8) = 21
    c: DistanceX(g8,g-1) = 95.25
    c: Coincident(g15,g16)
    c: Coincident(g16,g17)
    c: Coincident(g17,g18)
    c: Coincident(g18,g15)
    c: Horizontal(g15)
    c: Horizontal(g17)
    c: Vertical(g16)
    c: Vertical(g18)
    c: Coincident(g15,g11)
    c: Coincident(g14,g16)
    c: Coincident(g13,g15)
    c: Coincident(g17,g12)
    c: Diameter(g11) = 5.1
    c: Equal(g11,g13)
    c: Equal(g13,g14)
    c: Equal(g14,g12)
    c: Coincident(g20,g11)
    c: Coincident(g20,g14)
    c: Coincident(g21,g13)
    c: Coincident(g21,g12)
    c: PointOnObject(g19,g21)
    c: PointOnObject(g19,g20)
    c: DistanceX(g17,g17) = 30.5
    c: DistanceY(g16,g16) = 26
    c: Coincident(g0,g22)
    c: Coincident(g11,g22)
    c: Distance(g22) = 190.5
    c: Coincident(g27,g28)
    c: Coincident(g28,g29)
    c: Coincident(g29,g30)
    c: Coincident(g30,g27)
    c: Horizontal(g27)
    c: Horizontal(g29)
    c: Vertical(g28)
    c: Vertical(g30)
    c: Coincident(g27,g23)
    c: Coincident(g26,g28)
    c: Coincident(g25,g27)
    c: Coincident(g29,g24)
    c: Diameter(g23) = 5.1
    c: Equal(g23,g25)
    c: Equal(g25,g26)
    c: Equal(g26,g24)
    c: Coincident(g32,g23)
    c: Coincident(g32,g26)
    c: Coincident(g33,g25)
    c: Coincident(g33,g24)
    c: PointOnObject(g31,g33)
    c: PointOnObject(g31,g32)
    c: DistanceX(g29,g29) = 30.5
    c: DistanceY(g28,g28) = 26
    c: Coincident(g0,g34)
    c: Coincident(g23,g34)
    c: Distance(g34) = 42
    c: Perpendicular(g34,g22)
    c: Coincident(g39,g40)
    c: Coincident(g40,g41)
    c: Coincident(g41,g42)
    c: Coincident(g42,g39)
    c: Horizontal(g39)
    c: Horizontal(g41)
    c: Vertical(g40)
    c: Vertical(g42)
    c: Coincident(g39,g35)
    c: Coincident(g38,g40)
    c: Coincident(g37,g39)
    c: Coincident(g41,g36)
    c: Diameter(g35) = 5.1
    c: Equal(g35,g37)
    c: Equal(g37,g38)
    c: Equal(g38,g36)
    c: Coincident(g44,g35)
    c: Coincident(g44,g38)
    c: Coincident(g45,g37)
    c: Coincident(g45,g36)
    c: PointOnObject(g43,g45)
    c: PointOnObject(g43,g44)
    c: DistanceX(g41,g41) = 30.5
    c: DistanceY(g40,g40) = 26
    c: Coincident(g23,g46)
    c: Coincident(g35,g46)
    c: Equal(g22,g46)
    c: Parallel(g46,g22)
    c: Horizontal(g22)
    c: Coincident(g51,g52)
    c: Coincident(g52,g53)
    c: Coincident(g53,g54)
    c: Coincident(g54,g51)
    c: Horizontal(g51)
    c: Horizontal(g53)
    c: Vertical(g52)
    c: Vertical(g54)
    c: Coincident(g51,g47)
    c: Coincident(g52,g49)
    c: Diameter(g48) = 5.1
    c: Equal(g48,g47)
    c: Equal(g47,g50)
    c: Equal(g50,g49)
    c: Coincident(g48,g51)
    c: Coincident(g53,g50)
    c: DistanceX(g51,g51) = 20
    c: DistanceY(g52,g52) = 48
    c: DistanceY(g-1,g48) = 24
    c: DistanceX(g-1,g48) = 10
FEATURE [PartDesign::Hole] Hole
  AllowMultiFace = false
  BaseFeature = -> Pad011
  Depth = 25
  DepthType = 1
  Diameter = 5.1
  DrillPoint = 0
  DrillPointAngle = 118
  HoleCutCountersinkAngle = 90
  HoleCutDepth = 3
  HoleCutDiameter = 10
  HoleCutType = 1
  ModelActualThread = false
  Profile = -> Sketch024
  Tapered = false
  TaperedAngle = 90
  ThreadAngle = 0
  ThreadClass = 0
  ThreadCutOffInner = 0
  ThreadCutOffOuter = 0
  ThreadDirection = 0
  ThreadFit = 0
  ThreadPitch = 0
  ThreadSize = 0
  ThreadType = 0
  Threaded = false
FEATURE [Sketcher::SketchObject] Sketch025
  AttachmentOffset = pos=(0,0,6.35) rot=(0,0,1;0rad)
  MapMode = 5
  Placement = pos=(0,0,6.35) rot=(0,0,1;0rad)
  Support = -> [XY_Plane029]
  sketch-geometry (2):
    g0: Circle CenterX=-47 CenterY=0 CenterZ=0 NormalX=0 NormalY=0 NormalZ=1 AngleXU=0 Radius=12.5
    g1: Circle CenterX=47 CenterY=0 CenterZ=0 NormalX=0 NormalY=0 NormalZ=1 AngleXU=0 Radius=12.5
  constraints (5):
    c: Diameter(g0) = 25
    c: PointOnObject(g0,g-1)
    c: DistanceX(g0,g-1) = 47
    c: Symmetric(g0,g1,g-2)
    c: Equal(g0,g1)
FEATURE [PartDesign::Pocket] Pocket011
  AllowMultiFace = false
  BaseFeature = -> Hole
  Length = 5
  Length2 = 100
  Profile = -> Sketch025
  Type = 1
FEATURE [PartDesign::Body] Body010
  Group = -> [Sketch023,Pad011,Sketch024,Hole,Sketch025,Pocket011]
  Origin = -> Origin029
  Tip = -> Pocket011
FEATURE [App::Part] Part017  label="bearing_plate"
  Group = -> [Body010]
  Origin = -> Origin024
FEATURE [Sketcher::SketchObject] Sketch026
  MapMode = 5
  Placement = pos=(0,0,0) rot=(0.57735,0.57735,0.57735;2.0944rad)
  Support = -> [YZ_Plane030]
  sketch-geometry (10):
    g0: LineSegment StartX=-30 StartY=0 StartZ=0 EndX=-30 EndY=2 EndZ=0
    g1: LineSegment StartX=-30 StartY=2 StartZ=0 EndX=-16.5 EndY=22.4 EndZ=0
    g2: LineSegment StartX=-16.5 StartY=22.4 StartZ=0 EndX=16.5 EndY=22.4 EndZ=0
    g3: LineSegment StartX=16.5 StartY=22.4 StartZ=0 EndX=30 EndY=2 EndZ=0
    g4: LineSegment StartX=30 StartY=2 StartZ=0 EndX=30 EndY=0 EndZ=0
    g5: LineSegment StartX=30 StartY=0 StartZ=0 EndX=-30 EndY=0 EndZ=0
    g6: ArcOfCircle CenterX=-11 CenterY=11.2 CenterZ=0 NormalX=0 NormalY=0 NormalZ=1 AngleXU=0 Radius=6.5 StartAngle=1.5708 EndAngle=4.71239
    g7: ArcOfCircle CenterX=11 CenterY=11.2 CenterZ=0 NormalX=0 NormalY=0 NormalZ=1 AngleXU=0 Radius=6.5 StartAngle=4.71239 EndAngle=7.85398
    g8: LineSegment StartX=-11 StartY=4.7 StartZ=0 EndX=11 EndY=4.7 EndZ=0
    g9: LineSegment StartX=-11 StartY=17.7 StartZ=0 EndX=11 EndY=17.7 EndZ=0
  constraints (25):
    c: Coincident(g0,g5)
    c: Coincident(g0,g1)
    c: Coincident(g1,g2)
    c: Coincident(g2,g3)
    c: Coincident(g3,g4)
    c: Coincident(g4,g5)
    c: Vertical(g0)
    c: Vertical(g4)
    c: PointOnObject(g-1,g5)
    c: DistanceX(g5,g5) = 60
    c: DistanceX(g2,g2) = 33
    c: DistanceY(g0,g0) = 2
    c: Equal(g0,g4)
    c: DistanceY(g4,g2) = 22.4
    c: Symmetric(g1,g2,g-2)
    c: Symmetric(g0,g4,g-2)
    c: Tangent(g6,g9) = 1.5708
    c: Tangent(g6,g8) = -1.5708
    c: Tangent(g8,g7) = -1.5708
    c: Tangent(g9,g7) = 1.5708
    c: Horizontal(g8)
    c: Symmetric(g6,g7,g-2)
    c: Distance(g6,g6) = 13
    c: DistanceY(g-1,g6) = 11.2
    c: DistanceX(g6,g7) = 22
FEATURE [PartDesign::Pad] Pad002
  AllowMultiFace = false
  Length = 34
  Length2 = 100
  Midplane = true
  Placement = pos=(0,0,0) rot=(0.57735,0.57735,0.57735;2.0944rad)
  Profile = -> Sketch026
  Type = 0
FEATURE [Sketcher::SketchObject] Sketch027
  MapMode = 5
  Placement = pos=(0,0,0) rot=(0,1,0;3.14159rad)
  Support = -> [XY_Plane030]
  sketch-geometry (11):
    g0: Circle CenterX=-10 CenterY=24 CenterZ=0 NormalX=0 NormalY=0 NormalZ=1 AngleXU=0 Radius=2.5
    g1: Circle CenterX=-10 CenterY=-24 CenterZ=0 NormalX=0 NormalY=0 NormalZ=1 AngleXU=0 Radius=2.5
    g2: Circle CenterX=10 CenterY=-24 CenterZ=0 NormalX=0 NormalY=0 NormalZ=1 AngleXU=0 Radius=2.5
    g3: Circle CenterX=10 CenterY=24 CenterZ=0 NormalX=0 NormalY=0 NormalZ=1 AngleXU=0 Radius=2.5
    g4: LineSegment [constr] StartX=-10 StartY=24 StartZ=0 EndX=10 EndY=24 EndZ=0
    g5: LineSegment [constr] StartX=10 StartY=24 StartZ=0 EndX=10 EndY=-24 EndZ=0
    g6: LineSegment [constr] StartX=10 StartY=-24 StartZ=0 EndX=-10 EndY=-24 EndZ=0
    g7: LineSegment [constr] StartX=-10 StartY=-24 StartZ=0 EndX=-10 EndY=24 EndZ=0
    g8: LineSegment [constr] StartX=-10 StartY=24 StartZ=0 EndX=10 EndY=-24 EndZ=0
    g9: LineSegment [constr] StartX=-10 StartY=-24 StartZ=0 EndX=10 EndY=24 EndZ=0
    g10: GeomPoint X=0 Y=0 Z=0
  constraints (25):
    c: Coincident(g4,g5)
    c: Coincident(g5,g6)
    c: Coincident(g6,g7)
    c: Coincident(g7,g4)
    c: Horizontal(g4)
    c: Horizontal(g6)
    c: Vertical(g5)
    c: Vertical(g7)
    c: Coincident(g4,g0)
    c: Coincident(g5,g2)
    c: Coincident(g3,g4)
    c: Coincident(g1,g6)
    c: Diameter(g0) = 5
    c: Equal(g0,g3)
    c: Equal(g3,g1)
    c: Equal(g1,g2)
    c: Coincident(g8,g2)
    c: Coincident(g9,g1)
    c: Coincident(g9,g3)
    c: PointOnObject(g10,g8)
    c: PointOnObject(g10,g9)
    c: Coincident(g10,g-1)
    c: DistanceX(g6,g6) = 20
    c: Coincident(g8,g0)
    c: DistanceY(g5,g5) = 48
FEATURE [PartDesign::Hole] Hole002
  AllowMultiFace = false
  BaseFeature = -> Pad002
  Depth = 25
  DepthType = 1
  Diameter = 4.2
  DrillPoint = 0
  DrillPointAngle = 118
  HoleCutCountersinkAngle = 90
  HoleCutDepth = 0
  HoleCutDiameter = 5
  HoleCutType = 0
  ModelActualThread = false
  Placement = pos=(0,0,0) rot=(0.57735,0.57735,0.57735;2.0944rad)
  Profile = -> Sketch027
  Tapered = false
  TaperedAngle = 90
  ThreadAngle = 60
  ThreadClass = 0
  ThreadCutOffInner = 0.0866025
  ThreadCutOffOuter = 0.173205
  ThreadDirection = 1
  ThreadFit = 0
  ThreadPitch = 0.8
  ThreadSize = 6
  ThreadType = 1
  Threaded = true
FEATURE [Sketcher::SketchObject] Sketch028
  AttachmentOffset = pos=(0,0,22.4) rot=(0,0,1;0rad)
  MapMode = 5
  Placement = pos=(0,0,22.4) rot=(0,0,1;0rad)
  Support = -> [XY_Plane030]
  sketch-geometry (2):
    g0: Circle CenterX=-10 CenterY=6.5 CenterZ=0 NormalX=0 NormalY=0 NormalZ=1 AngleXU=0 Radius=2.5
    g1: Circle CenterX=10 CenterY=6.5 CenterZ=0 NormalX=0 NormalY=0 NormalZ=1 AngleXU=0 Radius=2.5
  constraints (5):
    c: Symmetric(g0,g1,g-2)
    c: Diameter(g0) = 5
    c: Equal(g0,g1)
    c: DistanceX(g0,g-1) = 10
    c: DistanceY(g-1,g0) = 6.5
FEATURE [PartDesign::Hole] Hole001
  AllowMultiFace = false
  BaseFeature = -> Hole002
  Depth = 5
  DepthType = 0
  Diameter = 4.2
  DrillPoint = 0
  DrillPointAngle = 118
  HoleCutCountersinkAngle = 90
  HoleCutDepth = 0
  HoleCutDiameter = 5
  HoleCutType = 0
  ModelActualThread = false
  Placement = pos=(0,0,0) rot=(0.57735,0.57735,0.57735;2.0944rad)
  Profile = -> Sketch028
  Tapered = false
  TaperedAngle = 90
  ThreadAngle = 60
  ThreadClass = 0
  ThreadCutOffInner = 0.0866025
  ThreadCutOffOuter = 0.173205
  ThreadDirection = 1
  ThreadFit = 0
  ThreadPitch = 0.8
  ThreadSize = 6
  ThreadType = 1
  Threaded = true
FEATURE [PartDesign::Body] Body011
  Group = -> [Sketch026,Pad002,Sketch027,Hole002,Sketch028,Hole001]
  Origin = -> Origin030
  Tip = -> Hole001
FEATURE [App::Part] Part018  label="nut_block_standoff"
  Group = -> [Body011]
  Origin = -> Origin025
FEATURE [Part::Feature] Part__Feature035  label="Nema 17  Stepper Motor length 60mm"
  shape: bbox 42.3 x 83.6 x 61.3 mm, 2290 faces, 53 solids (baked)
FEATURE [Part::Feature] Part__Feature003  label="GT2 Timing Pulley 20 Tooth"
  Placement = pos=(1.9e-14,83.5,0) rot=(0,0,-1;1.5708rad)
  shape: bbox 15 x 14 x 15 mm, 16 faces (baked)
FEATURE [App::Part] Part021  label="Motor with pulley"
  Group = -> [Part__Feature035,Part__Feature003]
  Origin = -> Origin031
  Placement = pos=(24,-22,63.2) rot=(-0.57735,-0.57735,0.57735;2.0944rad)
FEATURE [Sketcher::SketchObject] Sketch029
  MapMode = 5
  Placement = pos=(0,0,0) rot=(0.57735,0.57735,0.57735;2.0944rad)
  Support = -> [YZ_Plane035]
  sketch-geometry (10):
    g0: LineSegment StartX=0 StartY=4 StartZ=0 EndX=25 EndY=4 EndZ=0
    g1: LineSegment StartX=25 StartY=4 StartZ=0 EndX=25 EndY=-51 EndZ=0
    g2: LineSegment StartX=25 StartY=-51 StartZ=0 EndX=0 EndY=-51 EndZ=0
    g3: ArcOfCircle CenterX=12.5 CenterY=-5 CenterZ=0 NormalX=0 NormalY=0 NormalZ=1 AngleXU=0 Radius=2.55 StartAngle=2.224e-13 EndAngle=3.14159
    g4: ArcOfCircle CenterX=12.5 CenterY=-42 CenterZ=0 NormalX=0 NormalY=0 NormalZ=1 AngleXU=0 Radius=2.55 StartAngle=3.14159 EndAngle=6.28319
    g5: LineSegment StartX=9.95 StartY=-5 StartZ=0 EndX=9.95 EndY=-42 EndZ=0
    g6: LineSegment StartX=15.05 StartY=-5 StartZ=0 EndX=15.05 EndY=-42 EndZ=0
    g7: LineSegment StartX=0 StartY=-51 StartZ=0 EndX=-44 EndY=0 EndZ=0
    g8: LineSegment StartX=-44 StartY=0 StartZ=0 EndX=0 EndY=0 EndZ=0
    g9: LineSegment StartX=0 StartY=4 StartZ=0 EndX=0 EndY=0 EndZ=0
  constraints (27):
    c: Horizontal(g0)
    c: Horizontal(g2)
    c: Vertical(g1)
    c: Tangent(g3,g6) = 1.5708
    c: Tangent(g3,g5) = -1.5708
    c: Tangent(g5,g4) = -1.5708
    c: Tangent(g6,g4) = 1.5708
    c: Vertical(g5)
    c: Equal(g3,g4)
    c: DistanceX(g0,g4) = 12.5
    c: Diameter(g3) = 5.1
    c: DistanceY(g4,g0) = 46
    c: Coincident(g0,g1)
    c: DistanceX(g2,g2) = 25
    c: Coincident(g2,g1)
    c: PointOnObject(g0,g-2)
    c: DistanceY(g-1,g0) = 4
    c: DistanceY(g3,g-1) = 5
    c: DistanceY(g2,g-1) = 51
    c: Coincident(g7,g2)
    c: PointOnObject(g7,g-1)
    c: Coincident(g8,g7)
    c: Coincident(g8,g-1)
    c: Coincident(g9,g0)
    c: Coincident(g9,g8)
    c: DistanceX(g7,g8) = 44
    c: PointOnObject(g2,g-2)
FEATURE [PartDesign::Pad] Pad012
  AllowMultiFace = false
  Length = 4
  Length2 = 100
  Placement = pos=(0,0,0) rot=(0.57735,0.57735,0.57735;2.0944rad)
  Profile = -> Sketch029
  Type = 0
FEATURE [Sketcher::SketchObject] Sketch030
  MapMode = 5
  Placement = pos=(0,0,0) rot=(0.57735,0.57735,0.57735;2.0944rad)
  Support = -> [YZ_Plane035]
  sketch-geometry (4):
    g0: LineSegment StartX=0 StartY=0 StartZ=0 EndX=-44 EndY=0 EndZ=0
    g1: LineSegment StartX=-44 StartY=0 StartZ=0 EndX=-44 EndY=4 EndZ=0
    g2: LineSegment StartX=-44 StartY=4 StartZ=0 EndX=0 EndY=4 EndZ=0
    g3: LineSegment StartX=0 StartY=4 StartZ=0 EndX=0 EndY=0 EndZ=0
  constraints (11):
    c: Coincident(g0,g1)
    c: Coincident(g1,g2)
    c: Coincident(g2,g3)
    c: Coincident(g3,g0)
    c: Horizontal(g0)
    c: Horizontal(g2)
    c: Vertical(g1)
    c: Vertical(g3)
    c: Coincident(g0,g-1)
    c: DistanceY(g1,g1) = 4
    c: DistanceX(g0,g0) = 44
FEATURE [PartDesign::Pad] Pad013
  AllowMultiFace = false
  BaseFeature = -> Pad012
  Length = 46
  Length2 = 100
  Placement = pos=(0,0,0) rot=(0.57735,0.57735,0.57735;2.0944rad)
  Profile = -> Sketch030
  Type = 0
FEATURE [Sketcher::SketchObject] Sketch031
  MapMode = 5
  Support = -> [XY_Plane035]
  sketch-geometry (11):
    g0: Circle CenterX=8.5 CenterY=-6.5 CenterZ=0 NormalX=0 NormalY=0 NormalZ=1 AngleXU=0 Radius=1.55
    g1: Circle CenterX=39.5 CenterY=-6.5 CenterZ=0 NormalX=0 NormalY=0 NormalZ=1 AngleXU=0 Radius=1.55
    g2: Circle CenterX=39.5 CenterY=-37.5 CenterZ=0 NormalX=0 NormalY=0 NormalZ=1 AngleXU=0 Radius=1.55
    g3: Circle CenterX=8.5 CenterY=-37.5 CenterZ=0 NormalX=0 NormalY=0 NormalZ=1 AngleXU=0 Radius=1.55
    g4: Circle CenterX=24 CenterY=-22 CenterZ=0 NormalX=0 NormalY=0 NormalZ=1 AngleXU=0 Radius=11
    g5: LineSegment [constr] StartX=8.5 StartY=-6.5 StartZ=0 EndX=39.5 EndY=-6.5 EndZ=0
    g6: LineSegment [constr] StartX=39.5 StartY=-6.5 StartZ=0 EndX=39.5 EndY=-37.5 EndZ=0
    g7: LineSegment [constr] StartX=39.5 StartY=-37.5 StartZ=0 EndX=8.5 EndY=-37.5 EndZ=0
    g8: LineSegment [constr] StartX=8.5 StartY=-37.5 StartZ=0 EndX=8.5 EndY=-6.5 EndZ=0
    g9: LineSegment [constr] StartX=8.5 StartY=-6.5 StartZ=0 EndX=39.5 EndY=-37.5 EndZ=0
    g10: LineSegment [constr] StartX=39.5 StartY=-6.5 StartZ=0 EndX=8.5 EndY=-37.5 EndZ=0
  constraints (27):
    c: Coincident(g5,g6)
    c: Coincident(g6,g7)
    c: Coincident(g7,g8)
    c: Coincident(g8,g5)
    c: Horizontal(g5)
    c: Horizontal(g7)
    c: Vertical(g6)
    c: Vertical(g8)
    c: Coincident(g5,g0)
    c: Coincident(g6,g2)
    c: Coincident(g3,g7)
    c: Coincident(g1,g5)
    c: DistanceY(g6,g6) = 31
    c: DistanceX(g5,g5) = 31
    c: DistanceX(g-1,g0) = 8.5
    c: DistanceY(g0,g-1) = 6.5
    c: Coincident(g9,g0)
    c: Coincident(g9,g2)
    c: Coincident(g10,g1)
    c: Coincident(g10,g3)
    c: PointOnObject(g4,g10)
    c: PointOnObject(g4,g9)
    c: Equal(g0,g1)
    c: Equal(g1,g2)
    c: Equal(g2,g3)
    c: Diameter(g1) = 3.1
    c: Diameter(g4) = 22
FEATURE [PartDesign::Pocket] Pocket012
  AllowMultiFace = false
  BaseFeature = -> Pad013
  Length = 5
  Length2 = 100
  Placement = pos=(0,0,0) rot=(0.57735,0.57735,0.57735;2.0944rad)
  Profile = -> Sketch031
  Reversed = true
  Type = 1
FEATURE [Sketcher::SketchObject] Sketch032
  MapMode = 5
  Placement = pos=(0,0,0) rot=(-0.57735,0.57735,0.57735;4.18879rad)
  Support = -> [YZ_Plane035]
  sketch-geometry (4):
    g0: LineSegment StartX=21 StartY=4 StartZ=0 EndX=25 EndY=4 EndZ=0
    g1: LineSegment StartX=25 StartY=4 StartZ=0 EndX=25 EndY=-21 EndZ=0
    g2: LineSegment StartX=25 StartY=-21 StartZ=0 EndX=21 EndY=-21 EndZ=0
    g3: LineSegment StartX=21 StartY=-21 StartZ=0 EndX=21 EndY=4 EndZ=0
  constraints (12):
    c: Coincident(g0,g1)
    c: Coincident(g1,g2)
    c: Coincident(g2,g3)
    c: Coincident(g3,g0)
    c: Horizontal(g0)
    c: Horizontal(g2)
    c: Vertical(g1)
    c: Vertical(g3)
    c: DistanceY(g1,g1) = 25
    c: DistanceX(g0,g0) = 4
    c: DistanceY(g-1,g0) = 4
    c: DistanceX(g-1,g0) = 21
FEATURE [PartDesign::Pad] Pad003
  AllowMultiFace = false
  BaseFeature = -> Pocket012
  Length = 45
  Length2 = 100
  Placement = pos=(0,0,0) rot=(0.57735,0.57735,0.57735;2.0944rad)
  Profile = -> Sketch032
  Type = 0
FEATURE [PartDesign::Body] Body012
  Group = -> [Sketch029,Pad012,Sketch030,Pad013,Sketch031,Pocket012,Sketch032,Pad003]
  Origin = -> Origin035
  Tip = -> Pad003
FEATURE [App::Part] Part022  label="machined_bracket"
  Group = -> [Body012]
  Origin = -> Origin032
FEATURE [Sketcher::SketchObject] Sketch033
  MapMode = 5
  Support = -> [XY_Plane036]
  sketch-geometry (8):
    g0: LineSegment StartX=-3.5 StartY=7.5 StartZ=0 EndX=-3.5 EndY=6.11 EndZ=0
    g1: LineSegment StartX=-3.5 StartY=6.11 StartZ=0 EndX=3.5 EndY=6.11 EndZ=0
    g2: LineSegment StartX=3.5 StartY=6.11 StartZ=0 EndX=3.5 EndY=7.5 EndZ=0
    g3: LineSegment StartX=3.5 StartY=7.5 StartZ=0 EndX=5 EndY=7.5 EndZ=0
    g4: LineSegment StartX=5 StartY=7.5 StartZ=0 EndX=5 EndY=2.5 EndZ=0
    g5: LineSegment StartX=5 StartY=2.5 StartZ=0 EndX=-5 EndY=2.5 EndZ=0
    g6: LineSegment StartX=-5 StartY=2.5 StartZ=0 EndX=-5 EndY=7.5 EndZ=0
    g7: LineSegment StartX=-5 StartY=7.5 StartZ=0 EndX=-3.5 EndY=7.5 EndZ=0
  constraints (20):
    c: Coincident(g0,g1)
    c: Coincident(g1,g2)
    c: Coincident(g2,g3)
    c: Horizontal(g3)
    c: Coincident(g3,g4)
    c: Coincident(g4,g5)
    c: Coincident(g5,g6)
    c: Coincident(g6,g7)
    c: Coincident(g0,g7)
    c: Vertical(g6)
    c: Vertical(g0)
    c: Symmetric(g0,g1,g-2)
    c: Symmetric(g0,g2,g-2)
    c: Symmetric(g6,g3,g-2)
    c: Symmetric(g5,g4,g-2)
    c: DistanceX(g1,g1) = 7
    c: DistanceX(g5,g5) = 10
    c: DistanceY(g-1,g4) = 2.5
    c: DistanceY(g-1,g1) = 6.11
    c: DistanceY(g-1,g3) = 7.5
FEATURE [PartDesign::Revolution] Revolution001
  AllowMultiFace = false
  Angle = 360
  Axis = (1,0,0)
  Base = (0,0,0)
  Profile = -> Sketch033
  ReferenceAxis = -> X_Axis036
FEATURE [PartDesign::Body] Body013
  Group = -> [Sketch033,Revolution001]
  Origin = -> Origin036
  Tip = -> Revolution001
FEATURE [App::Part] Part023  label="e3d_2gt_idler"
  Group = -> [Body013]
  Origin = -> Origin033
  Placement = pos=(-1,-5.9,-2e-16) rot=(0,1,0;4.71239rad)
FEATURE [Part::Feature] Part__Feature005  label="gt2_belt_clamp"
  Placement = pos=(12,32,-1.3e-14) rot=(0.57735,0.57735,-0.57735;4.18879rad)
  shape: bbox 5 x 40 x 9 mm, 60 faces (baked)
FEATURE [Part::Feature] Part__Feature036  label="GT2 Timing Pulley 20 Tooth001"
  Placement = pos=(36.5,-13,-24.5) rot=(0,-1,0;1.5708rad)
  shape: bbox 15 x 15 x 14 mm, 16 faces (baked)
FEATURE [Part::Feature] Part__Feature037  label="NEMA17MotorMount"
  Placement = pos=(9.5,-13,-51) rot=(0.57735,0.57735,0.57735;4.18879rad)
  shape: bbox 50.98 x 50 x 52.98 mm, 96 faces (baked)
FEATURE [Part::Feature] Part__Feature038  label="Nema 17  Stepper Motor length 60mm001"
  Placement = pos=(36.5,-13,58.5) rot=(-1,0,0;1.5708rad)
  shape: bbox 42.3 x 61.3 x 83.6 mm, 2290 faces, 53 solids (baked)
FEATURE [App::Part] Part027  label="motor_and_mount"
  Group = -> [Part__Feature036,Part__Feature037,Part__Feature038]
  Origin = -> Origin041
  Placement = pos=(0,-10,15) rot=(0,0,1;0rad)
FEATURE [Part::FeaturePython] Screw001  label="M5x10-Screw008"  # Fasteners workbench fastener (typed FeaturePython)
  Placement = pos=(5,0,1.1e-15) rot=(0,1,0;1.5708rad)
  diameter = 3
  invert = false
  length = 1
  lengthCustom = 8
  matchOuter = false
  offset = 0
  thread = false
  type = 20
FEATURE [Part::Feature] Part__Feature039  label="washer1"
  Placement = pos=(11,-14,6.1) rot=(-1,0,0;1.5708rad)
  shape: bbox 11 x 11 x 1.1 mm, 6 faces (baked)
FEATURE [Part::Feature] Part__Feature040  label="washer2"
  Placement = pos=(11,-14,-5) rot=(-1,0,0;1.5708rad)
  shape: bbox 11 x 11 x 1.1 mm, 6 faces (baked)
FEATURE [Part::Cylinder] Cylinder004
  Angle = 360
  AttacherType = Attacher::AttachEngine3D
  Height = 20
  Placement = pos=(11,-14,-10) rot=(0,0,1;0rad)
  Radius = 2.5
FEATURE [Sketcher::SketchObject] Sketch037
  MapMode = 5
  Support = -> [XY_Plane046]
  sketch-geometry (4):
    g0: LineSegment StartX=0 StartY=50 StartZ=0 EndX=6.35 EndY=50 EndZ=0
    g1: LineSegment StartX=6.35 StartY=50 StartZ=0 EndX=6.35 EndY=-50 EndZ=0
    g2: LineSegment StartX=6.35 StartY=-50 StartZ=0 EndX=0 EndY=-50 EndZ=0
    g3: LineSegment StartX=0 StartY=-50 StartZ=0 EndX=0 EndY=50 EndZ=0
  constraints (11):
    c: Coincident(g0,g1)
    c: Coincident(g1,g2)
    c: Coincident(g2,g3)
    c: Coincident(g3,g0)
    c: Horizontal(g0)
    c: Horizontal(g2)
    c: Vertical(g1)
    c: PointOnObject(g0,g-2)
    c: Symmetric(g2,g0,g-1)
    c: DistanceY(g2,g0) = 100
    c: DistanceX(g0,g0) = 6.35
FEATURE [PartDesign::Pad] Pad016
  AllowMultiFace = false
  Length = 120
  Length2 = 100
  Midplane = true
  Profile = -> Sketch037
  Type = 0
FEATURE [Sketcher::SketchObject] Sketch038
  AttachmentOffset = pos=(0,0,6.35) rot=(0,0,1;0rad)
  MapMode = 5
  Placement = pos=(6.35,-1.4e-15,1.4e-15) rot=(0.57735,0.57735,0.57735;2.0944rad)
  Support = -> [YZ_Plane046]
  sketch-geometry (20):
    g0: LineSegment StartX=4 StartY=60 StartZ=0 EndX=4 EndY=10 EndZ=0
    g1: LineSegment StartX=4 StartY=10 StartZ=0 EndX=0 EndY=10 EndZ=0
    g2: LineSegment StartX=0 StartY=10 StartZ=0 EndX=0 EndY=4.5 EndZ=0
    g3: LineSegment StartX=0 StartY=4.5 StartZ=0 EndX=-1 EndY=3.5 EndZ=0
    g4: LineSegment StartX=-1 StartY=3.5 StartZ=0 EndX=-1 EndY=3 EndZ=0
    g5: LineSegment StartX=-1 StartY=3 StartZ=0 EndX=0 EndY=3 EndZ=0
    g6: LineSegment StartX=0 StartY=3 StartZ=0 EndX=0 EndY=-3 EndZ=0
    g7: LineSegment StartX=0 StartY=-3 StartZ=0 EndX=-1 EndY=-3 EndZ=0
    g8: LineSegment StartX=-1 StartY=-3 StartZ=0 EndX=-1 EndY=-3.5 EndZ=0
    g9: LineSegment StartX=-1 StartY=-3.5 StartZ=0 EndX=0 EndY=-4.5 EndZ=0
    g10: LineSegment StartX=0 StartY=-4.5 StartZ=0 EndX=0 EndY=-10 EndZ=0
    g11: LineSegment StartX=0 StartY=-10 StartZ=0 EndX=4 EndY=-10 EndZ=0
    g12: LineSegment StartX=4 StartY=-10 StartZ=0 EndX=4 EndY=-60 EndZ=0
    g13: LineSegment StartX=4 StartY=-60 StartZ=0 EndX=8 EndY=-60 EndZ=0
    g14: LineSegment StartX=8 StartY=-60 StartZ=0 EndX=8 EndY=-10 EndZ=0
    g15: LineSegment StartX=8 StartY=-10 StartZ=0 EndX=50 EndY=-10 EndZ=0
    g16: LineSegment StartX=50 StartY=-10 StartZ=0 EndX=50 EndY=-6 EndZ=0
    g17: LineSegment StartX=50 StartY=-6 StartZ=0 EndX=8 EndY=-6 EndZ=0
    g18: LineSegment StartX=8 StartY=-6 StartZ=0 EndX=8 EndY=60 EndZ=0
    g19: LineSegment StartX=8 StartY=60 StartZ=0 EndX=4 EndY=60 EndZ=0
  constraints (56):
    c: Vertical(g0)
    c: Coincident(g0,g1)
    c: Horizontal(g1)
    c: Coincident(g1,g2)
    c: Vertical(g2)
    c: Coincident(g2,g3)
    c: Coincident(g3,g4)
    c: Coincident(g4,g5)
    c: Horizontal(g5)
    c: Coincident(g5,g6)
    c: Coincident(g6,g7)
    c: Coincident(g7,g8)
    c: Coincident(g8,g9)
    c: Coincident(g9,g10)
    c: Vertical(g10)
    c: Coincident(g10,g11)
    c: Coincident(g11,g12)
    c: Vertical(g12)
    c: Coincident(g12,g13)
    c: Horizontal(g13)
    c: Coincident(g13,g14)
    c: Vertical(g14)
    c: Coincident(g14,g15)
    c: Horizontal(g15)
    c: Coincident(g15,g16)
    c: Coincident(g16,g17)
    c: Horizontal(g17)
    c: Coincident(g17,g18)
    c: Vertical(g18)
    c: Coincident(g18,g19)
    c: Coincident(g19,g0)
    c: Vertical(g4)
    c: Vertical(g6)
    c: Vertical(g16)
    c: Horizontal(g19)
    c: Horizontal(g7)
    c: Horizontal(g11)
    c: Vertical(g17,g14)
    c: Angle(g5,g3) = 0.785398
    c: Angle(g9,g7) = 0.785398
    c: DistanceY(g8,g8) = 0.5
    c: DistanceY(g6,g6) = 6
    c: Symmetric(g10,g1,g-1)
    c: Vertical(g9,g6)
    c: Symmetric(g7,g4,g-1)
    c: PointOnObject(g-1,g6)
    c: Symmetric(g3,g8,g-1)
    c: DistanceY(g-1,g2) = 4.5
    c: DistanceX(g1,g1) = 4
    c: Symmetric(g12,g0,g-1)
    c: DistanceY(g-1,g18) = 60
    c: DistanceX(g19,g19) = 4
    c: DistanceX(g-1,g15) = 50
    c: DistanceY(g-1,g0) = 10
    c: DistanceY(g16,g16) = 4
    c: Horizontal(g14,g11)
FEATURE [PartDesign::Pad] Pad017
  AllowMultiFace = false
  BaseFeature = -> Pad016
  Length = 120
  Length2 = 100
  Profile = -> Sketch038
  Type = 0
FEATURE [Sketcher::SketchObject] Sketch039
  MapMode = 5
  Placement = pos=(0,0,0) rot=(1,0,0;1.5708rad)
  Support = -> [XZ_Plane046]
  sketch-geometry (6):
    g0: LineSegment StartX=16.35 StartY=60 StartZ=0 EndX=126.35 EndY=10 EndZ=0
    g1: LineSegment StartX=126.35 StartY=10 StartZ=0 EndX=126.35 EndY=60 EndZ=0
    g2: LineSegment StartX=126.35 StartY=60 StartZ=0 EndX=16.35 EndY=60 EndZ=0
    g3: LineSegment StartX=16.35 StartY=-60 StartZ=0 EndX=126.35 EndY=-10 EndZ=0
    g4: LineSegment StartX=126.35 StartY=-10 StartZ=0 EndX=126.35 EndY=-60 EndZ=0
    g5: LineSegment StartX=126.35 StartY=-60 StartZ=0 EndX=16.35 EndY=-60 EndZ=0
  constraints (15):
    c: Coincident(g0,g1)
    c: Coincident(g1,g2)
    c: Coincident(g2,g0)
    c: Horizontal(g2)
    c: Coincident(g3,g4)
    c: Coincident(g4,g5)
    c: Coincident(g5,g3)
    c: Symmetric(g3,g0,g-1)
    c: Symmetric(g3,g0,g-1)
    c: Symmetric(g1,g4,g-1)
    c: Vertical(g1)
    c: DistanceY(g-1,g0) = 60
    c: DistanceX(g-1,g1) = 126.35
    c: DistanceX(g-1,g0) = 16.35
    c: DistanceY(g-1,g0) = 10
FEATURE [PartDesign::Pocket] Pocket013
  AllowMultiFace = false
  BaseFeature = -> Pad017
  Length = 5
  Length2 = 100
  Midplane = true
  Profile = -> Sketch039
  Type = 1
FEATURE [Sketcher::SketchObject] Sketch040
  MapMode = 5
  Support = -> [XY_Plane046]
  sketch-geometry (3):
    g0: LineSegment StartX=16.35 StartY=50 StartZ=0 EndX=126.35 EndY=10 EndZ=0
    g1: LineSegment StartX=126.35 StartY=50 StartZ=0 EndX=126.35 EndY=10 EndZ=0
    g2: LineSegment StartX=126.35 StartY=50 StartZ=0 EndX=16.35 EndY=50 EndZ=0
  constraints (9):
    c: Coincident(g1,g0)
    c: Vertical(g1)
    c: Coincident(g2,g1)
    c: Coincident(g2,g0)
    c: Horizontal(g2)
    c: DistanceX(g-1,g0) = 16.35
    c: DistanceY(g-1,g0) = 10
    c: DistanceY(g-1,g0) = 50
    c: DistanceX(g-1,g1) = 126.35
FEATURE [PartDesign::Pocket] Pocket014
  AllowMultiFace = false
  BaseFeature = -> Pocket013
  Length = 5
  Length2 = 100
  Midplane = true
  Profile = -> Sketch040
  Type = 1
FEATURE [PartDesign::Fillet] Fillet002
  Base = -> Pocket014 [Edge17,Edge11]
  BaseFeature = -> Pocket014
  Radius = 9.525
  SupportTransform = true
  expr: Radius = 3 / 8 * 25.4
FEATURE [Sketcher::SketchObject] Sketch041
  MapMode = 5
  Placement = pos=(0,0,0) rot=(-0.57735,0.57735,0.57735;4.18879rad)
  Support = -> [YZ_Plane046]
  expr: Constraints[12] = 3 / 8 * 25.4
  sketch-geometry (8):
    g0: LineSegment StartX=-15.2375 StartY=15 StartZ=0 EndX=5.2375 EndY=15 EndZ=0
    g1: LineSegment StartX=10 StartY=10.2375 StartZ=0 EndX=10 EndY=-10.2375 EndZ=0
    g2: LineSegment StartX=5.2375 StartY=-15 StartZ=0 EndX=-15.2375 EndY=-15 EndZ=0
    g3: LineSegment StartX=-20 StartY=-10.2375 StartZ=0 EndX=-20 EndY=10.2375 EndZ=0
    g4: ArcOfCircle CenterX=5.2375 CenterY=10.2375 CenterZ=0 NormalX=0 NormalY=0 NormalZ=1 AngleXU=0 Radius=4.7625 StartAngle=0 EndAngle=1.5708
    g5: ArcOfCircle CenterX=-15.2375 CenterY=10.2375 CenterZ=0 NormalX=0 NormalY=0 NormalZ=1 AngleXU=0 Radius=4.7625 StartAngle=1.5708 EndAngle=3.14159
    g6: ArcOfCircle CenterX=-15.2375 CenterY=-10.2375 CenterZ=0 NormalX=0 NormalY=0 NormalZ=1 AngleXU=0 Radius=4.7625 StartAngle=3.14159 EndAngle=4.71239
    g7: ArcOfCircle CenterX=5.2375 CenterY=-10.2375 CenterZ=0 NormalX=0 NormalY=0 NormalZ=1 AngleXU=0 Radius=4.7625 StartAngle=4.71239 EndAngle=6.28319
  constraints (19):
    c: Horizontal(g0)
    c: Horizontal(g2)
    c: Vertical(g1)
    c: Vertical(g3)
    c: Tangent(g0,g4) = 1.5708
    c: Tangent(g1,g4) = 1.5708
    c: Tangent(g0,g5) = 1.5708
    c: Tangent(g3,g5) = 1.5708
    c: Tangent(g3,g6) = 1.5708
    c: Tangent(g2,g6) = 1.5708
    c: Tangent(g1,g7) = 1.5708
    c: Tangent(g2,g7) = 1.5708
    c: Diameter(g4) = 9.525
    c: Equal(g6,g7)
    c: DistanceY(g-1,g0) = 15
    c: DistanceX(g-1,g1) = 10
    c: Symmetric(g0,g2,g-1)
    c: Equal(g4,g7)
    c: DistanceX(g3,g-1) = 20
FEATURE [PartDesign::Pocket] Pocket015
  AllowMultiFace = false
  BaseFeature = -> Fillet002
  Length = 19
  Length2 = 100
  Profile = -> Sketch041
  Type = 0
FEATURE [Sketcher::SketchObject] Sketch042
  AttachmentOffset = pos=(0,0,6.35) rot=(0,0,1;0rad)
  MapMode = 5
  Placement = pos=(6.35,-1.4e-15,1.4e-15) rot=(0.57735,0.57735,0.57735;2.0944rad)
  Support = -> [YZ_Plane046]
  sketch-geometry (2):
    g0: Circle CenterX=-40 CenterY=49.85 CenterZ=0 NormalX=0 NormalY=0 NormalZ=1 AngleXU=0 Radius=2.505
    g1: Circle CenterX=40 CenterY=49.85 CenterZ=0 NormalX=0 NormalY=0 NormalZ=1 AngleXU=0 Radius=2.505
  constraints (5):
    c: DistanceX(g0,g-1) = 40
    c: Equal(g0,g1)
    c: Diameter(g1) = 5.01
    c: DistanceY(g-1,g1) = 49.85
    c: Symmetric(g1,g0,g-2)
FEATURE [PartDesign::Hole] Hole004
  AllowMultiFace = false
  BaseFeature = -> Pocket015
  Depth = 25
  DepthType = 1
  Diameter = 5.02
  DrillPoint = 1
  DrillPointAngle = 118
  HoleCutCountersinkAngle = 90
  HoleCutDepth = 2.18
  HoleCutDiameter = 10.1
  HoleCutType = 1
  ModelActualThread = false
  Profile = -> Sketch042
  Tapered = false
  TaperedAngle = 90
  ThreadAngle = 0
  ThreadClass = 0
  ThreadCutOffInner = 0
  ThreadCutOffOuter = 0
  ThreadDirection = 0
  ThreadFit = 0
  ThreadPitch = 0
  ThreadSize = 0
  ThreadType = 0
  Threaded = false
FEATURE [Sketcher::SketchObject] Sketch043
  AttachmentOffset = pos=(0,0,6.35) rot=(0,0,1;0rad)
  MapMode = 5
  Placement = pos=(6.35,-1.4e-15,1.4e-15) rot=(0.57735,0.57735,0.57735;2.0944rad)
  Support = -> [YZ_Plane046]
  sketch-geometry (2):
    g0: Circle CenterX=-40 CenterY=-49.85 CenterZ=0 NormalX=0 NormalY=0 NormalZ=1 AngleXU=0 Radius=3.57
    g1: Circle CenterX=40 CenterY=-49.85 CenterZ=0 NormalX=0 NormalY=0 NormalZ=1 AngleXU=0 Radius=3.57
  constraints (5):
    c: DistanceX(g0,g-1) = 40
    c: Equal(g0,g1)
    c: Diameter(g1) = 7.14
    c: Symmetric(g1,g0,g-2)
    c: DistanceY(g0,g-1) = 49.85
FEATURE [PartDesign::Hole] Hole005
  AllowMultiFace = false
  BaseFeature = -> Hole004
  Depth = 25
  DepthType = 1
  Diameter = 7.14
  DrillPoint = 1
  DrillPointAngle = 118
  HoleCutCountersinkAngle = 90
  HoleCutDepth = 2.18
  HoleCutDiameter = 12
  HoleCutType = 1
  ModelActualThread = false
  Profile = -> Sketch043
  Tapered = false
  TaperedAngle = 90
  ThreadAngle = 0
  ThreadClass = 0
  ThreadCutOffInner = 0
  ThreadCutOffOuter = 0
  ThreadDirection = 0
  ThreadFit = 0
  ThreadPitch = 0
  ThreadSize = 0
  ThreadType = 0
  Threaded = false
FEATURE [Sketcher::SketchObject] Sketch044
  Placement = pos=(0,0,0) rot=(0,1,0;3.14159rad)
  sketch-geometry (70):
    g0: LineSegment StartX=-3.69 StartY=1.29e-14 StartZ=0 EndX=-3.9 EndY=0.21 EndZ=0
    g1: LineSegment StartX=-3.69 StartY=1.29e-14 StartZ=0 EndX=-3.9 EndY=-0.21 EndZ=0
    g2: LineSegment StartX=-3.9 StartY=-0.21 StartZ=0 EndX=-3.9 EndY=-2.83934 EndZ=0
    g3: LineSegment StartX=-3.9 StartY=-2.83934 StartZ=0 EndX=-6.56066 EndY=-5.5 EndZ=0
    g4: LineSegment StartX=-6.56066 StartY=-5.5 StartZ=0 EndX=-8.2 EndY=-5.5 EndZ=0
    g5: LineSegment StartX=-8.2 StartY=-5.5 StartZ=0 EndX=-8.2 EndY=-3.125 EndZ=0
    g6: LineSegment StartX=-8.2 StartY=-3.125 StartZ=0 EndX=-8.545 EndY=-3.125 EndZ=0
    g7: LineSegment StartX=-8.545 StartY=-3.125 StartZ=0 EndX=-10 EndY=-4.58 EndZ=0
    g8: LineSegment StartX=-10 StartY=-4.58 StartZ=0 EndX=-10 EndY=-9.5 EndZ=0
    g9: ArcOfCircle CenterX=-9.5 CenterY=-9.5 CenterZ=0 NormalX=0 NormalY=0 NormalZ=1 AngleXU=-1e-16 Radius=0.5 StartAngle=3.14159 EndAngle=4.71239
    g10: LineSegment StartX=-9.5 StartY=-10 StartZ=0 EndX=-4.58 EndY=-10 EndZ=0
    g11: LineSegment StartX=-3.125 StartY=-8.545 StartZ=0 EndX=-4.58 EndY=-10 EndZ=0
    g12: LineSegment StartX=-3.125 StartY=-8.2 StartZ=0 EndX=-3.125 EndY=-8.545 EndZ=0
    g13: LineSegment StartX=-5.5 StartY=-8.2 StartZ=0 EndX=-3.125 EndY=-8.2 EndZ=0
    g14: LineSegment StartX=-5.5 StartY=-6.56066 StartZ=0 EndX=-5.5 EndY=-8.2 EndZ=0
    g15: LineSegment StartX=-2.83934 StartY=-3.9 StartZ=0 EndX=-5.5 EndY=-6.56066 EndZ=0
    g16: LineSegment StartX=-0.21 StartY=-3.9 StartZ=0 EndX=-2.83934 EndY=-3.9 EndZ=0
    g17: LineSegment StartX=-4e-16 StartY=-3.69 StartZ=0 EndX=-0.21 EndY=-3.9 EndZ=0
    g18: LineSegment StartX=-4e-16 StartY=-3.69 StartZ=0 EndX=0.21 EndY=-3.9 EndZ=0
    g19: LineSegment StartX=0.21 StartY=-3.9 StartZ=0 EndX=2.83934 EndY=-3.9 EndZ=0
    g20: LineSegment StartX=2.83934 StartY=-3.9 StartZ=0 EndX=5.5 EndY=-6.56066 EndZ=0
    g21: LineSegment StartX=5.5 StartY=-6.56066 StartZ=0 EndX=5.5 EndY=-8.2 EndZ=0
    g22: LineSegment StartX=5.5 StartY=-8.2 StartZ=0 EndX=3.125 EndY=-8.2 EndZ=0
    g23: LineSegment StartX=3.125 StartY=-8.2 StartZ=0 EndX=3.125 EndY=-8.545 EndZ=0
    g24: LineSegment StartX=3.125 StartY=-8.545 StartZ=0 EndX=4.58 EndY=-10 EndZ=0
    g25: LineSegment StartX=4.58 StartY=-10 StartZ=0 EndX=9.5 EndY=-10 EndZ=0
    g26: ArcOfCircle CenterX=9.5 CenterY=-9.5 CenterZ=0 NormalX=0 NormalY=0 NormalZ=1 AngleXU=-1e-16 Radius=0.5 StartAngle=4.71239 EndAngle=6.28319
    g27: LineSegment StartX=10 StartY=-4.58 StartZ=0 EndX=10 EndY=-9.5 EndZ=0
    g28: LineSegment StartX=8.545 StartY=-3.125 StartZ=0 EndX=10 EndY=-4.58 EndZ=0
    g29: LineSegment StartX=8.2 StartY=-3.125 StartZ=0 EndX=8.545 EndY=-3.125 EndZ=0
    g30: LineSegment StartX=8.2 StartY=-5.5 StartZ=0 EndX=8.2 EndY=-3.125 EndZ=0
    g31: LineSegment StartX=6.56066 StartY=-5.5 StartZ=0 EndX=8.2 EndY=-5.5 EndZ=0
    g32: LineSegment StartX=3.9 StartY=-2.83934 StartZ=0 EndX=6.56066 EndY=-5.5 EndZ=0
    g33: LineSegment StartX=3.9 StartY=-0.21 StartZ=0 EndX=3.9 EndY=-2.83934 EndZ=0
    g34: LineSegment StartX=3.69 StartY=1.18e-14 StartZ=0 EndX=3.9 EndY=-0.21 EndZ=0
    g35: LineSegment StartX=3.69 StartY=1.18e-14 StartZ=0 EndX=3.9 EndY=0.21 EndZ=0
    g36: LineSegment StartX=3.9 StartY=0.21 StartZ=0 EndX=3.9 EndY=2.83934 EndZ=0
    g37: LineSegment StartX=3.9 StartY=2.83934 StartZ=0 EndX=6.56066 EndY=5.5 EndZ=0
    g38: LineSegment StartX=6.56066 StartY=5.5 StartZ=0 EndX=8.2 EndY=5.5 EndZ=0
    g39: LineSegment StartX=8.2 StartY=5.5 StartZ=0 EndX=8.2 EndY=3.125 EndZ=0
    g40: LineSegment StartX=8.2 StartY=3.125 StartZ=0 EndX=8.545 EndY=3.125 EndZ=0
    g41: LineSegment StartX=8.545 StartY=3.125 StartZ=0 EndX=10 EndY=4.58 EndZ=0
    g42: LineSegment StartX=10 StartY=9.5 StartZ=0 EndX=10 EndY=4.58 EndZ=0
    g43: ArcOfCircle CenterX=9.5 CenterY=9.5 CenterZ=0 NormalX=0 NormalY=0 NormalZ=1 AngleXU=-1e-16 Radius=0.5 StartAngle=0 EndAngle=1.5708
    g44: LineSegment StartX=4.58 StartY=10 StartZ=0 EndX=9.5 EndY=10 EndZ=0
    g45: LineSegment StartX=3.125 StartY=8.545 StartZ=0 EndX=4.58 EndY=10 EndZ=0
    g46: LineSegment StartX=3.125 StartY=8.2 StartZ=0 EndX=3.125 EndY=8.545 EndZ=0
    g47: LineSegment StartX=5.5 StartY=8.2 StartZ=0 EndX=3.125 EndY=8.2 EndZ=0
    g48: LineSegment StartX=5.5 StartY=6.56066 StartZ=0 EndX=5.5 EndY=8.2 EndZ=0
    g49: LineSegment StartX=2.83934 StartY=3.9 StartZ=0 EndX=5.5 EndY=6.56066 EndZ=0
    g50: LineSegment StartX=0.21 StartY=3.9 StartZ=0 EndX=2.83934 EndY=3.9 EndZ=0
    g51: LineSegment StartX=-2.51e-14 StartY=3.69 StartZ=0 EndX=0.21 EndY=3.9 EndZ=0
    g52: LineSegment StartX=-2.51e-14 StartY=3.69 StartZ=0 EndX=-0.21 EndY=3.9 EndZ=0
    g53: LineSegment StartX=-0.21 StartY=3.9 StartZ=0 EndX=-2.83934 EndY=3.9 EndZ=0
    g54: LineSegment StartX=-2.83934 StartY=3.9 StartZ=0 EndX=-5.5 EndY=6.56066 EndZ=0
    g55: LineSegment StartX=-5.5 StartY=6.56066 StartZ=0 EndX=-5.5 EndY=8.2 EndZ=0
    g56: LineSegment StartX=-5.5 StartY=8.2 StartZ=0 EndX=-3.125 EndY=8.2 EndZ=0
    g57: LineSegment StartX=-3.125 StartY=8.2 StartZ=0 EndX=-3.125 EndY=8.545 EndZ=0
    g58: LineSegment StartX=-3.125 StartY=8.545 StartZ=0 EndX=-4.58 EndY=10 EndZ=0
    g59: LineSegment StartX=-9.5 StartY=10 StartZ=0 EndX=-4.58 EndY=10 EndZ=0
    g60: ArcOfCircle CenterX=-9.5 CenterY=9.5 CenterZ=0 NormalX=0 NormalY=0 NormalZ=1 AngleXU=-1e-16 Radius=0.5 StartAngle=1.5708 EndAngle=3.14159
    g61: LineSegment StartX=-10 StartY=9.5 StartZ=0 EndX=-10 EndY=4.58 EndZ=0
    g62: LineSegment StartX=-8.545 StartY=3.125 StartZ=0 EndX=-10 EndY=4.58 EndZ=0
    g63: LineSegment StartX=-8.2 StartY=3.125 StartZ=0 EndX=-8.545 EndY=3.125 EndZ=0
    g64: LineSegment StartX=-8.2 StartY=5.5 StartZ=0 EndX=-8.2 EndY=3.125 EndZ=0
    g65: LineSegment StartX=-6.56066 StartY=5.5 StartZ=0 EndX=-8.2 EndY=5.5 EndZ=0
    g66: LineSegment StartX=-3.9 StartY=2.83934 StartZ=0 EndX=-6.56066 EndY=5.5 EndZ=0
    g67: LineSegment StartX=-3.9 StartY=0.21 StartZ=0 EndX=-3.9 EndY=2.83934 EndZ=0
    g68: ArcOfCircle CenterX=0 CenterY=0 CenterZ=0 NormalX=0 NormalY=0 NormalZ=1 AngleXU=-1e-16 Radius=2.1 StartAngle=3.14159 EndAngle=6.28319
    g69: ArcOfCircle CenterX=0 CenterY=0 CenterZ=0 NormalX=0 NormalY=0 NormalZ=1 AngleXU=-1e-16 Radius=2.1 StartAngle=0 EndAngle=3.14159
  constraints (149):
    c: Coincident(g0,g1)
    c: Coincident(g1,g2)
    c: Coincident(g2,g3)
    c: Coincident(g3,g4)
    c: Coincident(g4,g5)
    c: Coincident(g5,g6)
    c: Coincident(g6,g7)
    c: Coincident(g7,g8)
    c: Coincident(g8,g9)
    c: Coincident(g9,g10)
    c: Coincident(g10,g11)
    c: Coincident(g11,g12)
    c: Vertical(g12)
    c: Coincident(g12,g13)
    c: Horizontal(g13)
    c: Coincident(g13,g14)
    c: Vertical(g14)
    c: Coincident(g14,g15)
    c: Coincident(g15,g16)
    c: Coincident(g16,g17)
    c: Coincident(g17,g18)
    c: Coincident(g18,g19)
    c: Horizontal(g19)
    c: Coincident(g19,g20)
    c: Coincident(g20,g21)
    c: Vertical(g21)
    c: Coincident(g21,g22)
    c: Horizontal(g22)
    c: Coincident(g22,g23)
    c: Vertical(g23)
    c: Coincident(g23,g24)
    c: Coincident(g24,g25)
    c: Coincident(g25,g26)
    c: Coincident(g26,g27)
    c: Coincident(g27,g28)
    c: Coincident(g28,g29)
    c: Coincident(g29,g30)
    c: Coincident(g30,g31)
    c: Coincident(g31,g32)
    c: Coincident(g32,g33)
    c: Coincident(g33,g34)
    c: Coincident(g34,g35)
    c: Coincident(g35,g36)
    c: Coincident(g36,g37)
    c: Coincident(g37,g38)
    c: Coincident(g38,g39)
    c: Coincident(g39,g40)
    c: Coincident(g40,g41)
    c: Coincident(g41,g42)
    c: Coincident(g42,g43)
    c: Coincident(g43,g44)
    c: Horizontal(g44)
    c: Coincident(g44,g45)
    c: Coincident(g45,g46)
    c: Coincident(g46,g47)
    c: Coincident(g47,g48)
    c: Coincident(g48,g49)
    c: Coincident(g49,g50)
    c: Coincident(g50,g51)
    c: Coincident(g51,g52)
    c: Coincident(g52,g53)
    c: Coincident(g53,g54)
    c: Coincident(g54,g55)
    c: Coincident(g55,g56)
    c: Coincident(g56,g57)
    c: Coincident(g57,g58)
    c: Coincident(g58,g59)
    c: Horizontal(g59)
    c: Coincident(g59,g60)
    c: Coincident(g60,g61)
    c: Coincident(g61,g62)
    c: Coincident(g62,g63)
    c: Coincident(g63,g64)
    c: Coincident(g64,g65)
    c: Coincident(g65,g66)
    c: Coincident(g66,g67)
    c: Coincident(g67,g0)
    c: Coincident(g68,g69)
    c: Coincident(g69,g68)
    c: Block(g30)
    c: Block(g29)
    c: Block(g28)
    c: Block(g27)
    c: Block(g31)
    c: Block(g32)
    c: Block(g33)
    c: Block(g34)
    c: Block(g35)
    c: Block(g36)
    c: Block(g69)
    c: Block(g68)
    c: Block(g37)
    c: Block(g38)
    c: Block(g39)
    c: Block(g40)
    c: Block(g41)
    c: Block(g42)
    c: Block(g43)
    c: Block(g44)
    c: Block(g45)
    c: Block(g46)
    c: Block(g47)
    c: Block(g48)
    c: Block(g49)
    c: Block(g50)
    c: Block(g53)
    c: Block(g52)
    c: Block(g51)
    c: Block(g54)
    c: Block(g55)
    c: Block(g56)
    c: Block(g57)
    c: Block(g58)
    c: Block(g59)
    c: Block(g60)
    c: Block(g61)
    c: Block(g62)
    c: Block(g63)
    c: Block(g64)
    c: Block(g65)
    c: Block(g66)
    c: Block(g67)
    c: Block(g0)
    c: Block(g1)
    c: Block(g2)
    c: Block(g3)
    c: Block(g4)
    c: Block(g5)
    c: Block(g6)
    c: Block(g7)
    c: Block(g8)
    c: Block(g9)
    c: Block(g10)
    c: Block(g11)
    c: Block(g12)
    c: Block(g13)
    c: Block(g14)
    c: Block(g15)
    c: Block(g16)
    c: Block(g17)
    c: Block(g18)
    c: Block(g19)
    c: Block(g20)
    c: Block(g21)
    c: Block(g22)
    c: Block(g23)
    c: Block(g24)
    c: Block(g25)
    c: Block(g26)
FEATURE [PartDesign::Pad] Pad018
  AllowMultiFace = false
  Length = 380
  Length2 = 100
  Placement = pos=(0,0,0) rot=(0,1,0;3.14159rad)
  Profile = -> Sketch044
  Reversed = true
  Type = 0
FEATURE [PartDesign::Body] Body017
  Group = -> [Sketch044,Pad018]
  Origin = -> Origin047
  Tip = -> Pad018
FEATURE [App::Part] Part028  label="2020_vslot_rail"
  Group = -> [Body017]
  Origin = -> Origin042
  Placement = pos=(54,-10,1.2e-14) rot=(0,1,0;1.5708rad)
FEATURE [App::Link] Link016  label="wheel_asm_a001"
  LinkPlacement = pos=(-34.25,-15.75,41) rot=(0,0,1;0rad)
  LinkedObject = -> Part035
  Placement = pos=(-34.25,-15.75,41) rot=(0,0,1;0rad)
FEATURE [Sketcher::SketchObject] Sketch045
  MapMode = 5
  Support = -> [XY_Plane049]
  sketch-geometry (8):
    g0: ArcOfCircle CenterX=36.5 CenterY=-23 CenterZ=0 NormalX=0 NormalY=0 NormalZ=1 AngleXU=0 Radius=6.1 StartAngle=1.56847 EndAngle=4.70982
    g1: ArcOfCircle CenterX=445 CenterY=-24 CenterZ=0 NormalX=0 NormalY=0 NormalZ=1 AngleXU=0 Radius=6.15 StartAngle=4.70982 EndAngle=7.85166
    g2: ArcOfCircle CenterX=445 CenterY=-24 CenterZ=0 NormalX=0 NormalY=0 NormalZ=1 AngleXU=0 Radius=7.15 StartAngle=4.70982 EndAngle=7.85166
    g3: ArcOfCircle CenterX=36.5 CenterY=-23 CenterZ=0 NormalX=0 NormalY=0 NormalZ=1 AngleXU=0 Radius=7.1 StartAngle=1.56847 EndAngle=4.70982
    g4: LineSegment StartX=36.5165 StartY=-15.9 StartZ=0 EndX=445.017 EndY=-16.85 EndZ=0
    g5: LineSegment StartX=445.014 StartY=-17.85 StartZ=0 EndX=36.5142 EndY=-16.9 EndZ=0
    g6: LineSegment StartX=36.4843 StartY=-29.1 StartZ=0 EndX=444.984 EndY=-30.15 EndZ=0
    g7: LineSegment StartX=444.982 StartY=-31.15 StartZ=0 EndX=36.4818 EndY=-30.1 EndZ=0
  constraints (18):
    c: Diameter(g1) = 12.3
    c: Coincident(g2,g1)
    c: Diameter(g2) = 14.3
    c: Diameter(g0) = 12.2
    c: Coincident(g3,g0)
    c: Diameter(g3) = 14.2
    c: DistanceY(g0,g-1) = 23
    c: DistanceX(g-1,g0) = 36.5
    c: DistanceX(g-1,g1) = 445
    c: DistanceY(g1,g-1) = 24
    c: Tangent(g2,g7) = 1.5708
    c: Tangent(g1,g5) = -1.5708
    c: Tangent(g3,g7) = 1.5708
    c: Tangent(g3,g4) = 1.5708
    c: Tangent(g0,g6) = -1.5708
    c: Tangent(g0,g5) = -1.5708
    c: Tangent(g4,g2) = 1.5708
    c: Tangent(g1,g6) = -1.5708
FEATURE [PartDesign::Pad] Pad019
  AllowMultiFace = false
  Length = 6
  Length2 = 100
  Midplane = true
  Profile = -> Sketch045
  Type = 0
FEATURE [PartDesign::Body] Body018
  Group = -> [Sketch045,Pad019]
  Origin = -> Origin049
  Tip = -> Pad019
FEATURE [App::Part] Part029  label="belt"
  Group = -> [Body018]
  Origin = -> Origin043
FEATURE [Part::Feature] Part__Feature043  label="Volcano_Heater_Block"
  Placement = pos=(7,-15.5,2.25) rot=(0.57735,0.57735,-0.57735;4.18879rad)
  shape: bbox 11.5 x 24 x 20 mm, 69 faces (baked)
FEATURE [Part::Feature] Part__Feature044  label="Nozzle_(1)"
  Placement = pos=(-2e-15,3e-14,8.495) rot=(1,0,0;3.14159rad)
  shape: bbox 7.783 x 8.006 x 21 mm, 44 faces (baked)
FEATURE [Part::Feature] Part__Feature045  label="Heat_Break_(1)"
  Placement = pos=(-4e-15,-50,-12.5) rot=(1,0,0;3.14159rad)
  shape: bbox 6 x 6 x 26.1 mm, 21 faces (baked)
FEATURE [Part::Feature] Part__Feature004  label="M3_Button_Head_Screw_(1)"
  Placement = pos=(264.5,-231.851,240.44) rot=(0.707107,0.707107,0;3.14159rad)
  shape: bbox 11.5 x 6.17 x 6.17 mm, 14 faces (baked)
FEATURE [Part::Feature] Part__Feature046  label="M3_Button_Head_Screw_(1)001"
  Placement = pos=(264.5,-231.851,249.94) rot=(0.707107,0.707107,0;3.14159rad)
  shape: bbox 11.5 x 6.17 x 6.17 mm, 14 faces (baked)
FEATURE [Part::Feature] Part__Feature047  label="M3_Grub_Screw_(1)"
  Placement = pos=(9.5,18.4229,3.45) rot=(0.57735,0.57735,0.57735;2.0944rad)
  shape: bbox 4 x 2.6 x 2.6 mm, 12 faces (baked)
FEATURE [Part::Feature] Part__Feature009  label="eccentric_spacer"
  Placement = pos=(15.9,0.78,6e-15) rot=(0,-1,0;1.5708rad)
  shape: bbox 8.5 x 9.721 x 10.02 mm, 22 faces (baked)
FEATURE [Part::Feature] Part__Feature010  label="M5-Nut002"
  Placement = pos=(0,0,0) rot=(0,-1,0;1.5708rad)
  shape: bbox 5 x 8.9 x 8.9 mm, 23 faces (baked)
FEATURE [Part::Feature] Part__Feature016  label="precision_spacer"
  Placement = pos=(8.9,0,2e-15) rot=(0,1,0;1.5708rad)
  shape: bbox 1 x 8 x 8 mm, 4 faces (baked)
FEATURE [Part::Feature] Part__Feature017  label="lp_screw"
  Placement = pos=(20.2,0,4e-15) rot=(0,1,0;1.5708rad)
  shape: bbox 26.5 x 9 x 9 mm, 21 faces (baked)
FEATURE [Part::Feature] Part__Feature018  label="Chamfer004"
  Placement = pos=(-1,0,2e-16) rot=(0,-1,0;1.5708rad)
  shape: bbox 6 x 10 x 10 mm, 8 faces (baked)
FEATURE [Part::Feature] Part__Feature019  label="Pad020"
  Placement = pos=(0,0,0) rot=(0,-1,0;1.5708rad)
  shape: bbox 1 x 8 x 8 mm, 4 faces (baked)
FEATURE [Part::FeaturePython] Screw002  label="M5x20-Screw"  # Fasteners workbench fastener (typed FeaturePython)
  Placement = pos=(8.95,0,2e-15) rot=(0,1,0;1.5708rad)
  diameter = 3
  invert = false
  length = 5
  lengthCustom = 8
  matchOuter = false
  offset = 0
  thread = true
  type = 20
FEATURE [Sketcher::SketchObject] Sketch047
  MapMode = 5
  Support = -> [XY_Plane060]
  sketch-geometry (6):
    g0: ArcOfCircle CenterX=11 CenterY=-14 CenterZ=0 NormalX=0 NormalY=0 NormalZ=1 AngleXU=0 Radius=6.5 StartAngle=3.57338 EndAngle=6.89834
    g1: LineSegment StartX=0 StartY=-10 StartZ=0 EndX=0 EndY=10 EndZ=0
    g2: LineSegment StartX=0 StartY=10 StartZ=0 EndX=2 EndY=10 EndZ=0
    g3: LineSegment StartX=2 StartY=10 StartZ=0 EndX=16.3084 EndY=-10.2489 EndZ=0
    g4: LineSegment StartX=0 StartY=-10 StartZ=0 EndX=2 EndY=-10 EndZ=0
    g5: LineSegment StartX=2 StartY=-10 StartZ=0 EndX=5.09658 EndY=-16.7202 EndZ=0
  constraints (18):
    c: Vertical(g1)
    c: Coincident(g1,g2)
    c: Horizontal(g2)
    c: Coincident(g2,g3)
    c: Diameter(g0) = 13
    c: PointOnObject(g-1,g1)
    c: DistanceY(g-1,g1) = 10
    c: DistanceY(g1,g-1) = 10
    c: DistanceX(g2,g2) = 2
    c: DistanceX(g-1,g0) = 11
    c: DistanceY(g0,g-1) = 14
    c: Coincident(g1,g4)
    c: Coincident(g4,g5)
    c: Tangent(g5,g0)
    c: DistanceX(g4,g4) = 2
    c: Coincident(g5,g0)
    c: Horizontal(g4)
    c: Tangent(g3,g0) = 1.5708
FEATURE [PartDesign::Pad] Pad020  label="Pad021"
  AllowMultiFace = false
  Length = 20
  Length2 = 100
  Midplane = true
  Profile = -> Sketch047
  Type = 0
FEATURE [Sketcher::SketchObject] Sketch048
  MapMode = 5
  Placement = pos=(0,0,0) rot=(0.57735,0.57735,0.57735;2.0944rad)
  Support = -> [YZ_Plane060]
  sketch-geometry (5):
    g0: LineSegment StartX=-24 StartY=6.1 StartZ=0 EndX=-4 EndY=6.1 EndZ=0
    g1: LineSegment StartX=-4 StartY=6.1 StartZ=0 EndX=-4 EndY=-6.1 EndZ=0
    g2: LineSegment StartX=-4 StartY=-6.1 StartZ=0 EndX=-24 EndY=-6.1 EndZ=0
    g3: LineSegment StartX=-24 StartY=-6.1 StartZ=0 EndX=-24 EndY=6.1 EndZ=0
    g4: Circle CenterX=0 CenterY=0 CenterZ=0 NormalX=0 NormalY=0 NormalZ=1 AngleXU=0 Radius=2.55
  constraints (12):
    c: Coincident(g0,g1)
    c: Coincident(g1,g2)
    c: Coincident(g2,g3)
    c: Coincident(g3,g0)
    c: Horizontal(g0)
    c: Symmetric(g2,g0,g-1)
    c: Symmetric(g0,g1,g-1)
    c: DistanceX(g0,g0) = 20
    c: DistanceY(g3,g3) = 12.2
    c: Coincident(g4,g-1)
    c: Diameter(g4) = 5.1
    c: DistanceX(g0,g4) = 4
FEATURE [Sketcher::SketchObject] Sketch049
  AttachmentOffset = pos=(0,0,4) rot=(0,0,1;0rad)
  MapMode = 5
  Placement = pos=(4,-9e-16,9e-16) rot=(0.57735,0.57735,0.57735;2.0944rad)
  Support = -> [YZ_Plane060]
  sketch-geometry (4):
    g0: LineSegment StartX=-25 StartY=6.1 StartZ=0 EndX=25 EndY=6.1 EndZ=0
    g1: LineSegment StartX=25 StartY=6.1 StartZ=0 EndX=25 EndY=-6.1 EndZ=0
    g2: LineSegment StartX=25 StartY=-6.1 StartZ=0 EndX=-25 EndY=-6.1 EndZ=0
    g3: LineSegment StartX=-25 StartY=-6.1 StartZ=0 EndX=-25 EndY=6.1 EndZ=0
  constraints (12):
    c: Coincident(g0,g1)
    c: Coincident(g1,g2)
    c: Coincident(g2,g3)
    c: Coincident(g3,g0)
    c: Horizontal(g0)
    c: Horizontal(g2)
    c: Vertical(g1)
    c: Vertical(g3)
    c: DistanceX(g0,g0) = 50
    c: DistanceX(g-1,g0) = 25
    c: DistanceY(g-1,g0) = 6.1
    c: DistanceY(g1,g1) = 12.2
FEATURE [PartDesign::Pocket] Pocket016
  AllowMultiFace = false
  BaseFeature = -> Pad020
  Length = 5
  Length2 = 100
  Midplane = true
  Profile = -> Sketch048
  Type = 1
FEATURE [PartDesign::Pocket] Pocket017
  AllowMultiFace = false
  BaseFeature = -> Pocket016
  Length = 5
  Length2 = 100
  Profile = -> Sketch049
  Reversed = true
  Type = 1
FEATURE [Sketcher::SketchObject] Sketch050
  MapMode = 5
  Support = -> [XY_Plane060]
  sketch-geometry (1):
    g0: Circle CenterX=11 CenterY=-14 CenterZ=0 NormalX=0 NormalY=0 NormalZ=1 AngleXU=0 Radius=2.5
  constraints (3):
    c: DistanceY(g0,g-1) = 14
    c: DistanceX(g-1,g0) = 11
    c: Diameter(g0) = 5
FEATURE [PartDesign::Pocket] Pocket018
  AllowMultiFace = false
  BaseFeature = -> Pocket017
  Length = 5
  Length2 = 100
  Midplane = true
  Profile = -> Sketch050
  Type = 1
FEATURE [PartDesign::Body] Body020
  Group = -> [Sketch047,Pad020,Sketch048,Sketch049,Pocket016,Pocket017,Sketch050,Pocket018]
  Origin = -> Origin060
  Tip = -> Pocket018
FEATURE [Sketcher::SketchObject] Sketch051
  MapMode = 5
  Placement = pos=(0,0,0) rot=(1,0,0;1.5708rad)
  Support = -> [XZ_Plane061]
  sketch-geometry (10):
    g0: LineSegment StartX=18 StartY=0 StartZ=0 EndX=18 EndY=11 EndZ=0
    g1: LineSegment StartX=18 StartY=11 StartZ=0 EndX=-12 EndY=11 EndZ=0
    g2: LineSegment StartX=-18.35 StartY=0 StartZ=0 EndX=-18.35 EndY=50 EndZ=0
    g3: LineSegment StartX=-18.35 StartY=50 StartZ=0 EndX=-12 EndY=50 EndZ=0
    g4: LineSegment StartX=-12 StartY=50 StartZ=0 EndX=-12 EndY=28.75 EndZ=0
    g5: LineSegment StartX=-18.35 StartY=0 StartZ=0 EndX=18 EndY=0 EndZ=0
    g6: LineSegment StartX=-12 StartY=28.75 StartZ=0 EndX=-14 EndY=28.75 EndZ=0
    g7: LineSegment StartX=-14 StartY=28.75 StartZ=0 EndX=-14 EndY=21.25 EndZ=0
    g8: LineSegment StartX=-14 StartY=21.25 StartZ=0 EndX=-12 EndY=21.25 EndZ=0
    g9: LineSegment StartX=-12 StartY=21.25 StartZ=0 EndX=-12 EndY=11 EndZ=0
  constraints (29):
    c: Coincident(g0,g1)
    c: Horizontal(g1)
    c: Vertical(g0)
    c: Coincident(g2,g3)
    c: Coincident(g3,g4)
    c: Horizontal(g3)
    c: Vertical(g2)
    c: Vertical(g4)
    c: DistanceX(g3,g3) = 6.35
    c: DistanceX(g1,g-1) = 12
    c: Coincident(g1,g9)
    c: DistanceY(g0,g0) = 11
    c: DistanceY(g2,g2) = 50
    c: DistanceX(g-1,g0) = 18
    c: Coincident(g5,g2)
    c: Coincident(g5,g0)
    c: Horizontal(g5)
    c: PointOnObject(g-1,g5)
    c: Horizontal(g6)
    c: Coincident(g7,g6)
    c: Vertical(g7)
    c: Coincident(g8,g7)
    c: Horizontal(g8)
    c: Coincident(g4,g6)
    c: Coincident(g9,g8)
    c: Tangent(g4,g9)
    c: DistanceY(g7,g7) = 7.5
    c: DistanceY(g-1,g8) = 21.25
    c: DistanceX(g6,g6) = 2
FEATURE [PartDesign::Pad] Pad021  label="Pad022"
  AllowMultiFace = false
  Length = 50
  Length2 = 100
  Midplane = true
  Placement = pos=(0,0,0) rot=(1,0,0;1.5708rad)
  Profile = -> Sketch051
  Type = 0
FEATURE [Sketcher::SketchObject] Sketch052
  AttachmentOffset = pos=(0,0,12) rot=(0,0,1;0rad)
  MapMode = 5
  Placement = pos=(0,12,2.7e-15) rot=(0,0.707107,0.707107;3.14159rad)
  Support = -> [XZ_Plane061]
  sketch-geometry (3):
    g0: Circle CenterX=-6.35 CenterY=5.5 CenterZ=0 NormalX=0 NormalY=0 NormalZ=1 AngleXU=0 Radius=3.175
    g1: Circle CenterX=6.35 CenterY=5.5 CenterZ=0 NormalX=0 NormalY=0 NormalZ=1 AngleXU=0 Radius=3.175
    g2: LineSegment [constr] StartX=-6.35 StartY=5.5 StartZ=0 EndX=6.35 EndY=5.5 EndZ=0
  constraints (8):
    c: Diameter(g0) = 6.35
    c: Diameter(g1) = 6.35
    c: DistanceY(g-1,g0) = 5.5
    c: Coincident(g2,g0)
    c: Coincident(g2,g1)
    c: Horizontal(g2)
    c: DistanceX(g2,g2) = 12.7
    c: DistanceX(g0,g-1) = 6.35
FEATURE [Sketcher::SketchObject] Sketch053
  AttachmentOffset = pos=(0,0,18.35) rot=(0,0,1;0rad)
  MapMode = 5
  Placement = pos=(-18.35,4.1e-15,-4.1e-15) rot=(-0.57735,0.57735,0.57735;4.18879rad)
  Support = -> [YZ_Plane061]
  sketch-geometry (1):
    g0: Circle CenterX=16 CenterY=5.5 CenterZ=0 NormalX=0 NormalY=0 NormalZ=1 AngleXU=0 Radius=2.5
  constraints (3):
    c: Diameter(g0) = 5
    c: DistanceY(g-1,g0) = 5.5
    c: DistanceX(g-1,g0) = 16
FEATURE [PartDesign::Hole] Hole006
  AllowMultiFace = false
  BaseFeature = -> Pad021
  Depth = 27
  DepthType = 0
  Diameter = 4.763
  DrillPoint = 1
  DrillPointAngle = 118
  HoleCutCountersinkAngle = 90
  HoleCutDepth = 11
  HoleCutDiameter = 6
  HoleCutType = 1
  ModelActualThread = false
  Placement = pos=(0,0,0) rot=(1,0,0;1.5708rad)
  Profile = -> Sketch053
  Tapered = false
  TaperedAngle = 90
  ThreadAngle = 0
  ThreadClass = 0
  ThreadCutOffInner = 0
  ThreadCutOffOuter = 0
  ThreadDirection = 0
  ThreadFit = 0
  ThreadPitch = 0
  ThreadSize = 0
  ThreadType = 0
  Threaded = false
FEATURE [Sketcher::SketchObject] Sketch054
  MapMode = 5
  Placement = pos=(0,0,0) rot=(0,1,0;3.14159rad)
  Support = -> [XY_Plane061]
  sketch-geometry (1):
    g0: Circle CenterX=0 CenterY=-6 CenterZ=0 NormalX=0 NormalY=0 NormalZ=1 AngleXU=0 Radius=2
  constraints (3):
    c: Diameter(g0) = 4
    c: PointOnObject(g0,g-2)
    c: DistanceY(g0,g-1) = 6
FEATURE [PartDesign::Hole] Hole007
  AllowMultiFace = false
  BaseFeature = -> Hole006
  Depth = 25
  DepthType = 1
  Diameter = 4
  DrillPoint = 1
  DrillPointAngle = 118
  HoleCutCountersinkAngle = 90
  HoleCutDepth = 0
  HoleCutDiameter = 0
  HoleCutType = 0
  ModelActualThread = false
  Placement = pos=(0,0,0) rot=(1,0,0;1.5708rad)
  Profile = -> Sketch054
  Tapered = false
  TaperedAngle = 90
  ThreadAngle = 0
  ThreadClass = 0
  ThreadCutOffInner = 0
  ThreadCutOffOuter = 0
  ThreadDirection = 0
  ThreadFit = 0
  ThreadPitch = 0
  ThreadSize = 0
  ThreadType = 0
  Threaded = false
FEATURE [Sketcher::SketchObject] Sketch055
  AttachmentOffset = pos=(0,0,-12) rot=(0,0,1;0rad)
  MapMode = 5
  Placement = pos=(-12,2.7e-15,-2.7e-15) rot=(0.57735,0.57735,0.57735;2.0944rad)
  Support = -> [YZ_Plane061]
  expr: Constraints[3] = 25 + 31.9 / 2
  sketch-geometry (2):
    g0: Circle CenterX=-15 CenterY=40.95 CenterZ=0 NormalX=0 NormalY=0 NormalZ=1 AngleXU=0 Radius=2.55
    g1: Circle CenterX=15 CenterY=40.95 CenterZ=0 NormalX=0 NormalY=0 NormalZ=1 AngleXU=0 Radius=2.55
  constraints (5):
    c: Diameter(g1) = 5.1
    c: Equal(g1,g0)
    c: DistanceX(g0,g1) = 30
    c: DistanceY(g-1,g0) = 40.95
    c: Symmetric(g0,g1,g-2)
FEATURE [PartDesign::Hole] Hole008
  AllowMultiFace = false
  BaseFeature = -> Hole007
  Depth = 25
  DepthType = 1
  Diameter = 7.14
  DrillPoint = 1
  DrillPointAngle = 118
  HoleCutCountersinkAngle = 90
  HoleCutDepth = 2.17
  HoleCutDiameter = 12
  HoleCutType = 1
  ModelActualThread = false
  Placement = pos=(0,0,0) rot=(1,0,0;1.5708rad)
  Profile = -> Sketch055
  Tapered = false
  TaperedAngle = 90
  ThreadAngle = 0
  ThreadClass = 0
  ThreadCutOffInner = 0
  ThreadCutOffOuter = 0
  ThreadDirection = 0
  ThreadFit = 0
  ThreadPitch = 0
  ThreadSize = 0
  ThreadType = 0
  Threaded = false
  expr: HoleCutDepth = 6.35 - 4.18
FEATURE [Sketcher::SketchObject] Sketch056
  AttachmentOffset = pos=(0,0,18.35) rot=(0,0,1;0rad)
  MapMode = 5
  Placement = pos=(-18.35,4.1e-15,-4.1e-15) rot=(-0.57735,0.57735,0.57735;4.18879rad)
  Support = -> [YZ_Plane061]
  expr: Constraints[2] = 25 - 31.9 / 2
  sketch-geometry (1):
    g0: Circle CenterX=0 CenterY=9.05 CenterZ=0 NormalX=0 NormalY=0 NormalZ=1 AngleXU=0 Radius=2.5
  constraints (3):
    c: PointOnObject(g0,g-2)
    c: Diameter(g0) = 5
    c: DistanceY(g-1,g0) = 9.05
FEATURE [Sketcher::SketchObject] Sketch057
  AttachmentOffset = pos=(0,0,11) rot=(0,0,1;0rad)
  MapMode = 5
  Placement = pos=(0,0,11) rot=(0,0,1;0rad)
  Support = -> [XY_Plane061]
  sketch-geometry (4):
    g0: LineSegment StartX=23 StartY=32 StartZ=0 EndX=-12 EndY=32 EndZ=0
    g1: LineSegment StartX=-12 StartY=32 StartZ=0 EndX=-12 EndY=12 EndZ=0
    g2: LineSegment StartX=-12 StartY=12 StartZ=0 EndX=23 EndY=12 EndZ=0
    g3: LineSegment StartX=23 StartY=12 StartZ=0 EndX=23 EndY=32 EndZ=0
  constraints (12):
    c: Coincident(g0,g1)
    c: Coincident(g1,g2)
    c: Coincident(g2,g3)
    c: Coincident(g3,g0)
    c: Horizontal(g0)
    c: Horizontal(g2)
    c: Vertical(g1)
    c: Vertical(g3)
    c: DistanceX(g1,g-1) = 12
    c: DistanceX(g2,g2) = 35
    c: DistanceY(g3,g3) = 20
    c: DistanceY(g-1,g2) = 12
FEATURE [PartDesign::Pocket] Pocket019
  AllowMultiFace = false
  BaseFeature = -> Hole008
  Length = 5
  Length2 = 100
  Placement = pos=(0,0,0) rot=(1,0,0;1.5708rad)
  Profile = -> Sketch057
  Type = 1
FEATURE [PartDesign::Hole] Hole009
  AllowMultiFace = false
  BaseFeature = -> Pocket019
  Depth = 32
  DepthType = 0
  Diameter = 4.7625
  DrillPoint = 1
  DrillPointAngle = 118
  HoleCutCountersinkAngle = 90
  HoleCutDepth = 7.3
  HoleCutDiameter = 6
  HoleCutType = 1
  ModelActualThread = false
  Placement = pos=(0,0,0) rot=(1,0,0;1.5708rad)
  Profile = -> Sketch052
  Tapered = false
  TaperedAngle = 90
  ThreadAngle = 0
  ThreadClass = 0
  ThreadCutOffInner = 0
  ThreadCutOffOuter = 0
  ThreadDirection = 0
  ThreadFit = 0
  ThreadPitch = 0
  ThreadSize = 0
  ThreadType = 0
  Threaded = false
  expr: Diameter = 3 / 16 * 25.4
FEATURE [Sketcher::SketchObject] Sketch058
  AttachmentOffset = pos=(0,0,11) rot=(0,0,1;0rad)
  MapMode = 5
  Placement = pos=(0,0,11) rot=(0,0,1;0rad)
  Support = -> [XY_Plane061]
  sketch-geometry (12):
    g0: LineSegment StartX=13 StartY=-14.75 StartZ=0 EndX=13 EndY=3.25 EndZ=0
    g1: LineSegment StartX=10.75 StartY=5.5 StartZ=0 EndX=-3.75 EndY=5.5 EndZ=0
    g2: LineSegment StartX=-6 StartY=3.25 StartZ=0 EndX=-6 EndY=-14.75 EndZ=0
    g3: LineSegment StartX=-3.75 StartY=-17 StartZ=0 EndX=10.75 EndY=-17 EndZ=0
    g4: LineSegment StartX=18 StartY=-25 StartZ=0 EndX=-12 EndY=-25 EndZ=0
    g5: LineSegment StartX=-12 StartY=-25 StartZ=0 EndX=-12 EndY=12 EndZ=0
    g6: LineSegment StartX=-12 StartY=12 StartZ=0 EndX=18 EndY=12 EndZ=0
    g7: LineSegment StartX=18 StartY=12 StartZ=0 EndX=18 EndY=-25 EndZ=0
    g8: ArcOfCircle CenterX=10.75 CenterY=3.25 CenterZ=0 NormalX=0 NormalY=0 NormalZ=1 AngleXU=0 Radius=2.25 StartAngle=3.758e-13 EndAngle=1.5708
    g9: ArcOfCircle CenterX=-3.75 CenterY=3.25 CenterZ=0 NormalX=0 NormalY=0 NormalZ=1 AngleXU=0 Radius=2.25 StartAngle=1.5708 EndAngle=3.14159
    g10: ArcOfCircle CenterX=-3.75 CenterY=-14.75 CenterZ=0 NormalX=0 NormalY=0 NormalZ=1 AngleXU=0 Radius=2.25 StartAngle=3.14159 EndAngle=4.71239
    g11: ArcOfCircle CenterX=10.75 CenterY=-14.75 CenterZ=0 NormalX=0 NormalY=0 NormalZ=1 AngleXU=0 Radius=2.25 StartAngle=4.71239 EndAngle=6.28319
  constraints (32):
    c: Vertical(g0)
    c: Horizontal(g1)
    c: Vertical(g2)
    c: Horizontal(g3)
    c: Horizontal(g4)
    c: Coincident(g4,g5)
    c: Vertical(g5)
    c: Coincident(g5,g6)
    c: Horizontal(g6)
    c: Coincident(g6,g7)
    c: Vertical(g7)
    c: Tangent(g1,g8) = -1.5708
    c: Tangent(g0,g8) = -1.5708
    c: Tangent(g1,g9) = -1.5708
    c: Tangent(g2,g9) = -1.5708
    c: Tangent(g3,g10) = -1.5708
    c: Tangent(g2,g10) = -1.5708
    c: DistanceY(g-1,g6) = 12
    c: DistanceY(g4,g-1) = 25
    c: DistanceY(g-1,g1) = 5.5
    c: DistanceX(g2,g-1) = 6
    c: DistanceX(g-1,g0) = 13
    c: DistanceX(g-1,g6) = 18
    c: Equal(g9,g8)
    c: Diameter(g10) = 4.5
    c: DistanceX(g5,g-1) = 12
    c: Coincident(g7,g4)
    c: Tangent(g0,g11) = -1.5708
    c: Tangent(g3,g11) = -1.5708
    c: Equal(g10,g11)
    c: DistanceY(g3,g-1) = 17
    c: Equal(g10,g9)
FEATURE [PartDesign::Pad] Pad022  label="Pad023"
  AllowMultiFace = false
  BaseFeature = -> Hole009
  Length = 4
  Length2 = 100
  Placement = pos=(0,0,0) rot=(1,0,0;1.5708rad)
  Profile = -> Sketch058
  Type = 0
FEATURE [Sketcher::SketchObject] Sketch059
  AttachmentOffset = pos=(0,0,15) rot=(0,0,1;0rad)
  MapMode = 5
  Placement = pos=(0,0,15) rot=(0,0,1;0rad)
  Support = -> [XY_Plane061]
  sketch-geometry (3):
    g0: Circle CenterX=15.5 CenterY=-3.95 CenterZ=0 NormalX=0 NormalY=0 NormalZ=1 AngleXU=0 Radius=1.5
    g1: Circle CenterX=5.25 CenterY=7.85 CenterZ=0 NormalX=0 NormalY=0 NormalZ=1 AngleXU=0 Radius=1.5
    g2: Circle CenterX=-4.75 CenterY=-20.25 CenterZ=0 NormalX=0 NormalY=0 NormalZ=1 AngleXU=0 Radius=1.5
  constraints (9):
    c: DistanceY(g2,g-1) = 20.25
    c: DistanceX(g2,g-1) = 4.75
    c: DistanceX(g-1,g0) = 15.5
    c: DistanceX(g-1,g1) = 5.25
    c: DistanceY(g-1,g1) = 7.85
    c: DistanceY(g0,g-1) = 3.95
    c: Equal(g1,g0)
    c: Equal(g0,g2)
    c: Diameter(g1) = 3
FEATURE [PartDesign::Hole] Hole010
  AllowMultiFace = false
  BaseFeature = -> Pad022
  Depth = 6
  DepthType = 0
  Diameter = 2.75
  DrillPoint = 1
  DrillPointAngle = 118
  HoleCutCountersinkAngle = 90
  HoleCutDepth = 0
  HoleCutDiameter = 2.5
  HoleCutType = 0
  ModelActualThread = false
  Placement = pos=(0,0,0) rot=(1,0,0;1.5708rad)
  Profile = -> Sketch059
  Tapered = false
  TaperedAngle = 90
  ThreadAngle = 0
  ThreadClass = 0
  ThreadCutOffInner = 0
  ThreadCutOffOuter = 0
  ThreadDirection = 0
  ThreadFit = 0
  ThreadPitch = 0
  ThreadSize = 2
  ThreadType = 1
  Threaded = false
FEATURE [PartDesign::Hole] Hole011
  AllowMultiFace = false
  BaseFeature = -> Hole010
  Depth = 10
  DepthType = 0
  Diameter = 4.2
  DrillPoint = 1
  DrillPointAngle = 118
  HoleCutCountersinkAngle = 90
  HoleCutDepth = 0
  HoleCutDiameter = 5
  HoleCutType = 0
  ModelActualThread = false
  Placement = pos=(0,0,0) rot=(1,0,0;1.5708rad)
  Profile = -> Sketch056
  Tapered = false
  TaperedAngle = 90
  ThreadAngle = 60
  ThreadClass = 0
  ThreadCutOffInner = 0.0866025
  ThreadCutOffOuter = 0.173205
  ThreadDirection = 1
  ThreadFit = 0
  ThreadPitch = 0.8
  ThreadSize = 6
  ThreadType = 1
  Threaded = true
FEATURE [Sketcher::SketchObject] Sketch060
  MapMode = 5
  Placement = pos=(0,0,0) rot=(0.57735,0.57735,0.57735;2.0944rad)
  Support = -> [YZ_Plane061]
  sketch-geometry (1):
    g0: Circle CenterX=0 CenterY=25 CenterZ=0 NormalX=0 NormalY=0 NormalZ=1 AngleXU=0 Radius=1.5
  constraints (3):
    c: PointOnObject(g0,g-2)
    c: DistanceY(g-1,g0) = 25
    c: Diameter(g0) = 3
FEATURE [PartDesign::Hole] Hole012
  AllowMultiFace = false
  BaseFeature = -> Hole011
  Depth = 25
  DepthType = 1
  Diameter = 3.3
  DrillPoint = 1
  DrillPointAngle = 118
  HoleCutCountersinkAngle = 90
  HoleCutDepth = 0
  HoleCutDiameter = 3
  HoleCutType = 0
  ModelActualThread = false
  Placement = pos=(0,0,0) rot=(1,0,0;1.5708rad)
  Profile = -> Sketch060
  Tapered = false
  TaperedAngle = 90
  ThreadAngle = 0
  ThreadClass = 0
  ThreadCutOffInner = 0
  ThreadCutOffOuter = 0
  ThreadDirection = 0
  ThreadFit = 0
  ThreadPitch = 0
  ThreadSize = 3
  ThreadType = 1
  Threaded = false
FEATURE [PartDesign::Fillet] Fillet004
  Base = -> Hole012 [Edge9,Edge31,Edge57,Edge23,Edge19,Edge51,Edge1]
  BaseFeature = -> Hole012
  Placement = pos=(0,0,0) rot=(1,0,0;1.5708rad)
  Radius = 6.35
  SupportTransform = true
FEATURE [Part::Feature] Part__Feature062  label="Body023"
  shape: bbox 8.8 x 15.22 x 15.22 mm, 12 faces (baked)
FEATURE [App::Part] delrin_wheel
  Group = -> [Part__Feature062]
  Origin = -> Origin065
FEATURE [Part::Feature] Part__Feature063  label="Body024"
  shape: bbox 4 x 10 x 10 mm, 12 faces (baked)
FEATURE [App::Part] _05zz_ball_bearing  label="105zz_ball_bearing"
  Group = -> [Part__Feature063]
  Origin = -> Origin066
  Placement = pos=(4.9,0,0) rot=(0,0,1;0rad)
FEATURE [Part::Feature] Part__Feature064  label="Body025"
  shape: bbox 4 x 10 x 10 mm, 12 faces (baked)
FEATURE [App::Part] _05zz_ball_bearing001  label="105zz_ball_bearing001"
  Group = -> [Part__Feature064]
  Origin = -> Origin067
  Placement = pos=(-0.1,0,0) rot=(0,0,1;0rad)
FEATURE [App::Part] mini_v_wheel
  Group = -> [delrin_wheel,_05zz_ball_bearing,_05zz_ball_bearing001]
  Origin = -> Origin062
FEATURE [App::Part] Part035  label="wheel_asm_a"
  Group = -> [Part__Feature009,Part__Feature010,mini_v_wheel,Part__Feature016,Part__Feature017]
  Origin = -> Origin055
  Placement = pos=(-34.25,14.2,40.95) rot=(0,0,1;0rad)
FEATURE [Part::Feature] Part__Feature065  label="Body026"
  shape: bbox 8.8 x 15.22 x 15.22 mm, 12 faces (baked)
FEATURE [App::Part] delrin_wheel001
  Group = -> [Part__Feature065]
  Origin = -> Origin068
FEATURE [Part::Feature] Part__Feature066  label="Body027"
  shape: bbox 4 x 10 x 10 mm, 12 faces (baked)
FEATURE [App::Part] _05zz_ball_bearing002  label="105zz_ball_bearing002"
  Group = -> [Part__Feature066]
  Origin = -> Origin069
  Placement = pos=(4.9,0,0) rot=(0,0,1;0rad)
FEATURE [Part::Feature] Part__Feature067  label="Body028"
  shape: bbox 4 x 10 x 10 mm, 12 faces (baked)
FEATURE [App::Part] _05zz_ball_bearing003  label="105zz_ball_bearing003"
  Group = -> [Part__Feature067]
  Origin = -> Origin070
  Placement = pos=(-0.1,0,0) rot=(0,0,1;0rad)
FEATURE [App::Part] mini_v_wheel001
  Group = -> [delrin_wheel001,_05zz_ball_bearing002,_05zz_ball_bearing003]
  Origin = -> Origin063
FEATURE [App::Part] Part036  label="wheel_asm_b"
  Group = -> [Part__Feature018,Part__Feature019,mini_v_wheel001,Screw002]
  Origin = -> Origin056
  Placement = pos=(-25.2,0,9) rot=(0,1,0;3.14159rad)
FEATURE [Part::Feature] Part__Feature068  label="G5_BASE"
  Placement = pos=(120,0,0) rot=(0,0,1;0rad)
  shape: bbox 27.36 x 33.62 x 16.3 mm, 130 faces (baked)
FEATURE [Part::Feature] Part__Feature069  label="G5_CAP"
  Placement = pos=(120,0,0) rot=(0,0,1;0rad)
  shape: bbox 24.76 x 33.81 x 19.29 mm, 50 faces (baked)
FEATURE [Part::Feature] Part__Feature071  label="G5_TOP"
  Placement = pos=(120,0,0) rot=(0,0,1;0rad)
  shape: bbox 27.48 x 34.44 x 12.54 mm, 87 faces (baked)
FEATURE [Part::Feature] Part__Feature072  label="G5_TENSIONER"
  Placement = pos=(12,-34.3,61.7) rot=(0.57735,0.57735,-0.57735;4.18879rad)
  shape: bbox 6 x 15.47 x 20.39 mm, 31 faces (baked)
FEATURE [Part::FeaturePython] Screw004  label="M2.5x30-Screw"  # Fasteners workbench fastener (typed FeaturePython)
  Placement = pos=(15.51,2.07,25.9) rot=(0,0,1;0rad)
  diameter = 3
  invert = false
  length = 10
  lengthCustom = 30
  matchOuter = false
  offset = 0
  thread = false
  type = 16
FEATURE [App::Link] Link017  label="M2.5x30-Screw001"
  LinkPlacement = pos=(-4.75,-14.25,25.9) rot=(0,0,1;0rad)
  LinkedObject = -> Screw004
  Placement = pos=(-4.75,-14.25,25.9) rot=(0,0,1;0rad)
FEATURE [App::Link] Link018  label="M2.5x30-Screw002"
  LinkPlacement = pos=(5.25,13.85,25.9) rot=(0,0,1;0rad)
  LinkedObject = -> Screw004
  Placement = pos=(5.25,13.85,25.9) rot=(0,0,1;0rad)
FEATURE [App::Part] Part038  label="G5_EXTRUDER"
  Group = -> [Part__Feature072,Part__Feature068,Part__Feature069,Part__Feature071,Screw004,Link017,Link018]
  Origin = -> Origin071
  Placement = pos=(0,-6,15) rot=(0,0,1;0rad)
FEATURE [Part::Feature] Part__Feature073  label="Nema 17  Stepper Motor length 60mm002"
  Placement = pos=(25.4,3e-15,565.85) rot=(0,-0.707107,0.707107;3.14159rad)
  shape: bbox 42.3 x 61.3 x 83.6 mm, 2290 faces, 53 solids (baked)
  expr: .Placement.Base.z = 559.5mm + 6.35mm
FEATURE [TechDraw::DrawRichAnno] RichTextAnnotation
  AnnoText = <!DOCTYPE HTML PUBLIC "-//W3C//DTD HTML 4.0//EN" "http://www.w3.org/TR/REC-html40/strict.dtd">\n<html><head><meta name="qrichtext" content="1" /><style type="text/css">\np, li { white-space: pre-wrap; }\n</style></head><body style=" font-family:'Sans Serif'; font-size:9pt; font-weight:400; font-style:normal;">\n<p style=" margin-top:0px; margin-bottom:0px; margin-left:0px; margin-right:0px; -qt-block-indent:0; text-indent:0px;"><span style=" font-size:6pt;">Notes:</span></p>\n<p style=" margin-top:0px; margin-bottom:0px; margin-left:0px; margin-right:0px; -qt-block-indent:0; text-indent:0px;"><span style=" font-size:6pt;">Material:3/16x1-1/2&quot; CRS Flat-Bar</span></p>\n<p style=" margin-top:0px; margin-bottom:0px; margin-left:0px; margin-right:0px; -qt-block-indent:0; text-indent:0px;"><span style=" font-size:6pt;">Match bent profile to printed drawing</span></p>\n<p style=" margin-top:0px; margin-bottom:0px; margin-left:0px; margin-right:0px; -qt-block-indent:0; text-indent:0px;"><span style=" font-size:6pt;">All linear dimensions ± 1mm unless otherwise specified</span></p>\n<p style=" margin-top:0px; margin-bottom:0px; margin-left:0px; margin-right:0px; -qt-block-indent:0; text-indent:0px;"><span style=" font-size:6pt;">All dimensions in mm unless otherwise specified</span></p>\n<p style=" margin-top:0px; margin-bottom:0px; margin-left:0px; margin-right:0px; -qt-block-indent:0; text-indent:0px;"><span style=" font-size:6pt;">All angular dimensions ± 1° unless otherwise specified</span></p>\n<p style=" margin-top:0px; margin-bottom:0px; margin-left:0px; margin-right:0px; -qt-block-indent:0; text-indent:0px;"><img src="data:image/638422090.;base64," width="0" height="0" /></p></body></html>
  LockPosition = true
  MaxWidth = -1
  Rotation = 0
  ScaleType = 0
  ShowFrame = false
  X = 57.2613
  Y = 29.6332
FEATURE [TechDraw::DrawViewPart] View
  CoarseView = false
  Direction = (0.577,-0.577,0.577)
  Focus = 100
  HardHidden = false
  IsoCount = 0
  IsoHidden = false
  IsoVisible = false
  LockPosition = true
  Perspective = false
  Rotation = 0
  Scale = 0.5
  ScaleType = 0
  SeamHidden = false
  SeamVisible = true
  SmoothHidden = false
  SmoothVisible = true
  X = 52.1571
  XDirection = (0.707,0.707,0)
  Y = 183.642
FEATURE [TechDraw::DrawProjGroupItem] ProjItem  label="Front"
  CoarseView = false
  Direction = (2e-16,0,1)
  Focus = 100
  HardHidden = false
  IsoCount = 0
  IsoHidden = false
  IsoVisible = false
  LockPosition = true
  Perspective = false
  Rotation = 0
  RotationVector = (1,0,0)
  ScaleType = 2
  SeamHidden = false
  SeamVisible = true
  SmoothHidden = false
  SmoothVisible = true
  Type = 0
  X = 0
  XDirection = (-1e-16,-1,0)
  Y = 0
FEATURE [TechDraw::DrawViewDimension] Dimension007
  Arbitrary = false
  FormatSpec = %.0f
  Inverted = false
  LockPosition = false
  MeasureType = 1
  OverTolerance = 0
  References2D = -> [ProjItem]
  Rotation = 0
  ScaleType = 0
  TheoreticalExact = false
  Type = 4
  UnderTolerance = 0
  X = -95.9346
  Y = -23.1442
FEATURE [TechDraw::DrawViewDimension] Dimension008
  Arbitrary = false
  FormatSpec = %.1f
  Inverted = false
  LockPosition = false
  MeasureType = 1
  OverTolerance = 0
  References2D = -> [ProjItem]
  Rotation = 0
  ScaleType = 0
  TheoreticalExact = false
  Type = 5
  UnderTolerance = 0
  X = -43.5309
  Y = 13.2034
FEATURE [TechDraw::DrawViewDimension] Dimension009
  Arbitrary = false
  FormatSpec = %.0f
  Inverted = false
  LockPosition = false
  MeasureType = 1
  OverTolerance = 0
  References2D = -> [ProjItem]
  Rotation = 0
  ScaleType = 0
  TheoreticalExact = false
  Type = 1
  UnderTolerance = 0
  X = 75.1356
  Y = -23.7605
FEATURE [TechDraw::DrawViewDimension] Dimension001
  Arbitrary = false
  FormatSpec = %.0f
  Inverted = false
  LockPosition = false
  MeasureType = 1
  OverTolerance = 0
  References2D = -> [ProjItem]
  Rotation = 0
  ScaleType = 0
  TheoreticalExact = false
  Type = 1
  UnderTolerance = 0
  X = -58.5266
  Y = -8.63314
FEATURE [TechDraw::DrawViewDimension] Dimension005
  Arbitrary = false
  FormatSpec = %.0f
  Inverted = false
  LockPosition = false
  MeasureType = 1
  OverTolerance = 0
  References2D = -> [ProjItem]
  Rotation = 0
  ScaleType = 0
  TheoreticalExact = false
  Type = 2
  UnderTolerance = 0
  X = 39.6648
  Y = 2.1477
FEATURE [TechDraw::DrawSVGTemplate] Template001
  EditableTexts = Author=Alex Neufeld; DWG_num=2020-101; Date=20/04/2020; Revision=1; Scale=1:1; Subtitle=3X Required; Title=Heated Bed Support Bracket
  Height = 215.9
  Orientation = 1
  Width = 279.4
FEATURE [TechDraw::DrawViewDimension] Dimension002
  Arbitrary = false
  FormatSpec = %.0f
  Inverted = false
  LockPosition = false
  MeasureType = 1
  OverTolerance = 0
  References2D = -> [ProjItem]
  Rotation = 0
  ScaleType = 0
  TheoreticalExact = false
  Type = 1
  UnderTolerance = 0
  X = -92.4136
  Y = 11.2022
FEATURE [TechDraw::DrawProjGroupItem] ProjItem002  label="Bottom"
  CoarseView = false
  Direction = (-1,1e-16,2e-16)
  Focus = 100
  HardHidden = false
  IsoCount = 0
  IsoHidden = false
  IsoVisible = false
  LockPosition = true
  Perspective = false
  Rotation = 0
  RotationVector = (1,0,0)
  ScaleType = 2
  SeamHidden = false
  SeamVisible = true
  SmoothHidden = false
  SmoothVisible = true
  Type = 5
  X = 0
  XDirection = (-1e-16,-1,0)
  Y = 57.1654
FEATURE [TechDraw::DrawViewDimension] Dimension
  Arbitrary = false
  FormatSpec = %.0f
  Inverted = false
  LockPosition = false
  MeasureType = 1
  OverTolerance = 0
  References2D = -> [ProjItem002]
  Rotation = 0
  ScaleType = 0
  TheoreticalExact = false
  Type = 1
  UnderTolerance = 0
  X = -2.67351
  Y = -30.7205
FEATURE [TechDraw::DrawViewDimension] Dimension004
  Arbitrary = false
  FormatSpec = %.0f
  Inverted = false
  LockPosition = false
  MeasureType = 1
  OverTolerance = 0
  References2D = -> [ProjItem002]
  Rotation = 0
  ScaleType = 0
  TheoreticalExact = false
  Type = 4
  UnderTolerance = 0
  X = 27.4125
  Y = -0.702885
FEATURE [TechDraw::DrawViewDimension] Dimension003
  Arbitrary = false
  FormatSpec = %.0f
  Inverted = false
  LockPosition = false
  MeasureType = 1
  OverTolerance = 0
  References2D = -> [ProjItem002]
  Rotation = 0
  ScaleType = 0
  TheoreticalExact = false
  Type = 2
  UnderTolerance = 0
  X = -18.9779
  Y = 0
FEATURE [TechDraw::DrawProjGroupItem] ProjItem003  label="Right"
  CoarseView = false
  Direction = (-1e-16,-1,1e-16)
  Focus = 100
  HardHidden = false
  IsoCount = 0
  IsoHidden = false
  IsoVisible = false
  LockPosition = true
  Perspective = false
  Rotation = 0
  RotationVector = (1,0,0)
  ScaleType = 2
  SeamHidden = false
  SeamVisible = true
  SmoothHidden = false
  SmoothVisible = true
  Type = 2
  X = -121.983
  XDirection = (-2e-16,-1e-16,-1)
  Y = 0
FEATURE [TechDraw::DrawProjGroup] ProjGroup
  Anchor = -> ProjItem
  AutoDistribute = true
  LockPosition = true
  ProjectionType = 0
  Rotation = 0
  ScaleType = 0
  Views = -> [ProjItem,ProjItem002,ProjItem003]
  X = 167.689
  Y = 93.6987
  spacingX = 15
  spacingY = 15
FEATURE [TechDraw::DrawViewDimension] Dimension006
  Arbitrary = false
  FormatSpec = %.0f
  Inverted = false
  LockPosition = false
  MeasureType = 1
  OverTolerance = 0
  References2D = -> [ProjItem003]
  Rotation = 0
  ScaleType = 0
  TheoreticalExact = false
  Type = 2
  UnderTolerance = 0
  X = 0.377489
  Y = 0.412579
FEATURE [TechDraw::DrawViewDimension] Dimension010
  Arbitrary = false
  FormatSpec = %.0f
  Inverted = false
  LockPosition = false
  MeasureType = 1
  OverTolerance = 0
  References2D = -> [ProjItem003]
  Rotation = 0
  ScaleType = 0
  TheoreticalExact = false
  Type = 6
  UnderTolerance = 0
  X = -31.0721
  Y = 0.225979
FEATURE [TechDraw::DrawPage] Page001  label="support_bracket_dwg"
  KeepUpdated = true
  NextBalloonIndex = 1
  ProjectionType = 0
  Template = -> Template001
  Views = -> [ProjGroup,View,Dimension,Dimension001,Dimension002,Dimension003,Dimension004,Dimension005,Dimension006,Dimension007,Dimension008,Dimension009,Dimension010,RichTextAnnotation]
FEATURE [Part::Feature] Part__Feature074  label="Nylon Insert Lock Nut M006"
  Placement = pos=(0,-5.5,0) rot=(-0.627621,0,0.778519;3.14159rad)
  shape: bbox 9.239 x 5.001 x 9.239 mm, 32 faces (baked)
FEATURE [Part::Feature] Part__Feature075  label="Ball Bearing 5 x 16 x 008"
  Placement = pos=(0,3,0) rot=(0.649651,0.649651,-0.39485;3.89371rad)
  shape: bbox 16 x 5 x 16 mm, 18 faces (baked)
FEATURE [Part::Feature] Part__Feature076  label="Low Profile Screw M5_M5 x 012"
  Placement = pos=(2.2e-15,-10,0) rot=(0,0,-1;1.5708rad)
  shape: bbox 9.743 x 26.75 x 9.743 mm, 18 faces (baked)
FEATURE [Part::Feature] Part__Feature077  label="Solid V Wheel"
  Placement = pos=(0,0,0) rot=(0,0,-1;1.5708rad)
  shape: bbox 23.9 x 10.2 x 23.9 mm, 16 faces (baked)
FEATURE [Part::Feature] Part__Feature078  label="Ball Bearing 5 x 16 x 007"
  Placement = pos=(0,-3,0) rot=(-0.548771,0.548771,-0.630634;2.01631rad)
  shape: bbox 16 x 5 x 16 mm, 18 faces (baked)
FEATURE [Part::Feature] Part__Feature079  label="Precision Shim 10 x 5 x 1"
  Placement = pos=(0,-0.5,0) rot=(0,1,0;0.214596rad)
  shape: bbox 10 x 1 x 10 mm, 6 faces (baked)
FEATURE [Part::Feature] Part__Feature080  label="Precision Shim 10 x 5 x 002"
  Placement = pos=(0,5.5,0) rot=(0,1,0;0.885313rad)
  shape: bbox 10 x 1 x 10 mm, 6 faces (baked)
FEATURE [Part::Feature] Part__Feature081  label="Aluminum Spacer 6mm002"
  Placement = pos=(0,12.5,0) rot=(-0.287209,0.677315,-0.677315;3.70095rad)
  shape: bbox 10 x 6 x 10 mm, 14 faces (baked)
FEATURE [App::Part] Solid_V_Wheel_Straight  label="Solid V Wheel_Straight"
  Group = -> [Part__Feature077,Part__Feature078,Part__Feature075,Part__Feature079,Part__Feature080,Part__Feature074,Part__Feature081,Part__Feature076]
  Origin = -> Origin076
  Placement = pos=(-12.5,40,49.88) rot=(0,0,1;4.71239rad)
FEATURE [App::Link] Link020  label="Solid V Wheel_Straight001"
  LinkPlacement = pos=(-12.5,-40,49.88) rot=(0,0,-1;1.5708rad)
  LinkedObject = -> Solid_V_Wheel_Straight
  Placement = pos=(-12.5,-40,49.88) rot=(0,0,-1;1.5708rad)
FEATURE [Part::Feature] Part__Feature082  label="Eccentric Spacer 6mm"
  Placement = pos=(-0.79,12.5,0) rot=(0.707107,0,0.707107;3.14159rad)
  shape: bbox 11.16 x 8.501 x 11.55 mm, 28 faces (baked)
FEATURE [Part::Feature] Part__Feature083  label="Low Profile Screw M5_M5 x 015"
  Placement = pos=(2.2e-15,-10,0) rot=(0,0,-1;1.5708rad)
  shape: bbox 9.743 x 26.75 x 9.743 mm, 18 faces (baked)
FEATURE [Part::Feature] Part__Feature084  label="Solid V Wheel002"
  Placement = pos=(0,0,0) rot=(0,0,-1;1.5708rad)
  shape: bbox 23.9 x 10.2 x 23.9 mm, 16 faces (baked)
FEATURE [Part::Feature] Part__Feature085  label="Nylon Insert Lock Nut M008"
  Placement = pos=(0,-5.5,0) rot=(-0.627621,0,0.778519;3.14159rad)
  shape: bbox 9.239 x 5.001 x 9.239 mm, 32 faces (baked)
FEATURE [Part::Feature] Part__Feature086  label="Precision Shim 10 x 5 x 005"
  Placement = pos=(0,-0.5,0) rot=(0,1,0;0.214596rad)
  shape: bbox 10 x 1 x 10 mm, 6 faces (baked)
FEATURE [Part::Feature] Part__Feature087  label="Ball Bearing 5 x 16 x 011"
  Placement = pos=(0,-3,0) rot=(-0.548771,0.548771,-0.630634;2.01631rad)
  shape: bbox 16 x 5 x 16 mm, 18 faces (baked)
FEATURE [Part::Feature] Part__Feature088  label="Ball Bearing 5 x 16 x 012"
  Placement = pos=(0,3,0) rot=(0.649651,0.649651,-0.39485;3.89371rad)
  shape: bbox 16 x 5 x 16 mm, 18 faces (baked)
FEATURE [Part::Feature] Part__Feature089  label="Precision Shim 10 x 5 x 006"
  Placement = pos=(0,5.5,0) rot=(0,1,0;0.885313rad)
  shape: bbox 10 x 1 x 10 mm, 6 faces (baked)
FEATURE [App::Part] Solid_V_Wheel_Eccentric  label="Solid V Wheel_Eccentric"
  Group = -> [Part__Feature084,Part__Feature087,Part__Feature088,Part__Feature086,Part__Feature089,Part__Feature085,Part__Feature082,Part__Feature083]
  Origin = -> Origin077
  Placement = pos=(-12.5,40.01,-49.06) rot=(0.57735,0.57735,0.57735;4.18879rad)
FEATURE [App::Link] Link021  label="Solid V Wheel_Eccentric001"
  LinkPlacement = pos=(-12.5,-40.01,-49.06) rot=(0,0,-1;1.5708rad)
  LinkedObject = -> Solid_V_Wheel_Eccentric
  Placement = pos=(-12.5,-40.01,-49.06) rot=(0,0,-1;1.5708rad)
FEATURE [App::DocumentObjectGroup] Group003  label="v-wheels"
  Group = -> [Solid_V_Wheel_Straight,Link020,Solid_V_Wheel_Eccentric,Link021]
FEATURE [TechDraw::DrawSVGTemplate] Template
  EditableTexts = Author=Alex Neufeld; DWG_num=2020-102; Date=27/04/2020; Revision=1; Scale=2:1; Subtitle=For use with 20T 2GT pulley; Title=X-Axis Idler Bracket
  Height = 215.9
  Orientation = 1
  Width = 279.4
FEATURE [TechDraw::DrawProjGroupItem] ProjItem004  label="Front001"
  CoarseView = false
  Direction = (1,0,0)
  Focus = 100
  HardHidden = false
  IsoCount = 0
  IsoHidden = false
  IsoVisible = false
  LockPosition = true
  Perspective = false
  Rotation = 0
  RotationVector = (0,-1,0)
  Scale = 2
  ScaleType = 2
  SeamHidden = false
  SeamVisible = true
  SmoothHidden = false
  SmoothVisible = true
  Source = -> [Pocket018]
  Type = 0
  X = 0
  XDirection = (0,-1,0)
  Y = 0
FEATURE [TechDraw::DrawProjGroupItem] ProjItem005  label="Bottom001"
  CoarseView = false
  Direction = (0,0,1)
  Focus = 100
  HardHidden = false
  IsoCount = 0
  IsoHidden = false
  IsoVisible = false
  LockPosition = false
  Perspective = false
  Rotation = 0
  RotationVector = (1,0,0)
  Scale = 2
  ScaleType = 2
  SeamHidden = false
  SeamVisible = true
  SmoothHidden = false
  SmoothVisible = true
  Source = -> [Pocket018]
  Type = 5
  X = 0
  XDirection = (0,-1,0)
  Y = 55
FEATURE [TechDraw::DrawProjGroupItem] ProjItem006  label="Left"
  CoarseView = false
  Direction = (1e-16,1,0)
  Focus = 100
  HardHidden = false
  IsoCount = 0
  IsoHidden = false
  IsoVisible = false
  LockPosition = false
  Perspective = false
  Rotation = 0
  RotationVector = (1,0,0)
  Scale = 2
  ScaleType = 2
  SeamHidden = false
  SeamVisible = true
  SmoothHidden = false
  SmoothVisible = true
  Source = -> [Pocket018]
  Type = 1
  X = 76
  XDirection = (1,-1e-16,0)
  Y = 0
FEATURE [TechDraw::DrawProjGroup] ProjGroup001
  Anchor = -> ProjItem004
  AutoDistribute = true
  LockPosition = false
  ProjectionType = 0
  Rotation = 0
  Scale = 2
  ScaleType = 2
  Source = -> [Pocket018]
  Views = -> [ProjItem004,ProjItem005,ProjItem006]
  X = 115.856
  Y = 93.9676
  spacingX = 15
  spacingY = 15
FEATURE [TechDraw::DrawViewDimension] Dimension011
  Arbitrary = false
  FormatSpec = %.2f
  Inverted = false
  LockPosition = false
  MeasureType = 1
  OverTolerance = 0
  References2D = -> [ProjItem005]
  Rotation = 0
  ScaleType = 0
  TheoreticalExact = false
  Type = 2
  UnderTolerance = 0
  X = -1.22864
  Y = -5.61509
FEATURE [TechDraw::DrawViewDimension] Dimension012
  Arbitrary = false
  FormatSpec = %.2f
  Inverted = false
  LockPosition = false
  MeasureType = 1
  OverTolerance = 0
  References2D = -> [ProjItem005]
  Rotation = 0
  ScaleType = 0
  TheoreticalExact = false
  Type = 1
  UnderTolerance = 0
  X = -9.62757
  Y = 32.5088
FEATURE [TechDraw::DrawViewDimension] Dimension013
  Arbitrary = false
  FormatSpec = %.2f
  Inverted = false
  LockPosition = false
  MeasureType = 1
  OverTolerance = 0
  References2D = -> [ProjItem005]
  Rotation = 0
  ScaleType = 0
  TheoreticalExact = false
  Type = 5
  UnderTolerance = 0
  X = 36.6543
  Y = -10.6594
FEATURE [TechDraw::DrawViewDimension] Dimension014
  Arbitrary = false
  FormatSpec = R%.2f
  Inverted = false
  LockPosition = false
  MeasureType = 1
  OverTolerance = 0
  References2D = -> [ProjItem005]
  Rotation = 0
  ScaleType = 0
  TheoreticalExact = false
  Type = 4
  UnderTolerance = 0
  X = 36.5861
  Y = 24.2841
FEATURE [TechDraw::DrawViewDimension] Dimension015
  Arbitrary = false
  FormatSpec = %.2f
  Inverted = false
  LockPosition = false
  MeasureType = 1
  OverTolerance = 0
  References2D = -> [ProjItem004]
  Rotation = 0
  ScaleType = 0
  TheoreticalExact = false
  Type = 1
  UnderTolerance = 0
  X = -1.23796
  Y = -30.11
FEATURE [TechDraw::DrawViewDimension] Dimension016
  Arbitrary = false
  FormatSpec = %.2f
  Inverted = false
  LockPosition = false
  MeasureType = 1
  OverTolerance = 0
  References2D = -> [ProjItem004]
  Rotation = 0
  ScaleType = 0
  TheoreticalExact = false
  Type = 2
  UnderTolerance = 0
  X = -39.1657
  Y = 1.44429
FEATURE [TechDraw::DrawViewDimension] Dimension017
  Arbitrary = false
  FormatSpec = %.2f
  Inverted = false
  LockPosition = false
  MeasureType = 1
  OverTolerance = 0
  References2D = -> [ProjItem004]
  Rotation = 0
  ScaleType = 0
  TheoreticalExact = false
  Type = 1
  UnderTolerance = 0
  X = 14.4127
  Y = 1.51531
FEATURE [TechDraw::DrawViewDimension] Dimension019
  Arbitrary = false
  FormatSpec = %.2f
  Inverted = false
  LockPosition = false
  MeasureType = 1
  OverTolerance = 0
  References2D = -> [ProjItem006]
  Rotation = 0
  ScaleType = 0
  TheoreticalExact = false
  Type = 1
  UnderTolerance = 0
  X = -14.3253
  Y = 30.6682
FEATURE [TechDraw::DrawViewDimension] Dimension020
  Arbitrary = false
  FormatSpec = %.2f
  Inverted = false
  LockPosition = false
  MeasureType = 1
  OverTolerance = 0
  References2D = -> [ProjItem005]
  Rotation = 0
  ScaleType = 0
  TheoreticalExact = false
  Type = 2
  UnderTolerance = 0
  X = -44.8152
  Y = -15.9643
FEATURE [TechDraw::DrawViewDimension] Dimension021
  Arbitrary = false
  FormatSpec = %.2f
  Inverted = false
  LockPosition = false
  MeasureType = 1
  OverTolerance = 0
  References2D = -> [ProjItem006]
  Rotation = 0
  ScaleType = 0
  TheoreticalExact = false
  Type = 2
  UnderTolerance = 0
  X = 26.4675
  Y = -1.52638
FEATURE [TechDraw::DrawViewDimension] Dimension022
  Arbitrary = false
  FormatSpec = %.2f
  Inverted = false
  LockPosition = false
  MeasureType = 1
  OverTolerance = 0
  References2D = -> [ProjItem006]
  Rotation = 0
  ScaleType = 0
  TheoreticalExact = false
  Type = 2
  UnderTolerance = 0
  X = 20.103
  Y = 30.7348
FEATURE [TechDraw::DrawViewDimension] Dimension023
  Arbitrary = false
  FormatSpec = ⌀%.2f
  Inverted = false
  LockPosition = false
  MeasureType = 1
  OverTolerance = 0
  References2D = -> [ProjItem004]
  Rotation = 0
  ScaleType = 0
  TheoreticalExact = false
  Type = 5
  UnderTolerance = 0
  X = -42.9114
  Y = -28.9505
FEATURE [TechDraw::DrawViewPart] View001
  CoarseView = false
  Direction = (0.577,-0.577,0.577)
  Focus = 100
  HardHidden = false
  IsoCount = 0
  IsoHidden = false
  IsoVisible = false
  LockPosition = false
  Perspective = false
  Rotation = 0
  ScaleType = 0
  SeamHidden = false
  SeamVisible = true
  SmoothHidden = false
  SmoothVisible = true
  Source = -> [Pocket018]
  X = 30.3213
  XDirection = (0.707,0.707,0)
  Y = 184.536
FEATURE [TechDraw::DrawPage] Page  label="x_idler_bracket_dwg"
  KeepUpdated = true
  NextBalloonIndex = 1
  ProjectionType = 0
  Template = -> Template
  Views = -> [ProjGroup001,Dimension011,Dimension012,Dimension013,Dimension014,Dimension015,Dimension016,Dimension017,Dimension019,Dimension020,Dimension021,Dimension022,Dimension023,View001]
FEATURE [App::Part] Part033  label="machined_idler_bracket"
  Group = -> [Body020,Page]
  Origin = -> Origin051
FEATURE [Sketcher::SketchObject] Sketch069
  MapMode = 5
  Support = -> [XY_Plane079]
  sketch-geometry (8):
    g0: LineSegment StartX=-3.5 StartY=7.5 StartZ=0 EndX=-3.5 EndY=6.11 EndZ=0
    g1: LineSegment StartX=-3.5 StartY=6.11 StartZ=0 EndX=3.5 EndY=6.11 EndZ=0
    g2: LineSegment StartX=3.5 StartY=6.11 StartZ=0 EndX=3.5 EndY=7.5 EndZ=0
    g3: LineSegment StartX=3.5 StartY=7.5 StartZ=0 EndX=5 EndY=7.5 EndZ=0
    g4: LineSegment StartX=5 StartY=7.5 StartZ=0 EndX=5 EndY=2.5 EndZ=0
    g5: LineSegment StartX=5 StartY=2.5 StartZ=0 EndX=-5 EndY=2.5 EndZ=0
    g6: LineSegment StartX=-5 StartY=2.5 StartZ=0 EndX=-5 EndY=7.5 EndZ=0
    g7: LineSegment StartX=-5 StartY=7.5 StartZ=0 EndX=-3.5 EndY=7.5 EndZ=0
  constraints (20):
    c: Coincident(g0,g1)
    c: Coincident(g1,g2)
    c: Coincident(g2,g3)
    c: Horizontal(g3)
    c: Coincident(g3,g4)
    c: Coincident(g4,g5)
    c: Coincident(g5,g6)
    c: Coincident(g6,g7)
    c: Coincident(g0,g7)
    c: Vertical(g6)
    c: Vertical(g0)
    c: Symmetric(g0,g1,g-2)
    c: Symmetric(g0,g2,g-2)
    c: Symmetric(g6,g3,g-2)
    c: Symmetric(g5,g4,g-2)
    c: DistanceX(g1,g1) = 7
    c: DistanceX(g5,g5) = 10
    c: DistanceY(g-1,g4) = 2.5
    c: DistanceY(g-1,g1) = 6.11
    c: DistanceY(g-1,g3) = 7.5
FEATURE [PartDesign::Revolution] Revolution002
  AllowMultiFace = false
  Angle = 360
  Axis = (1,0,0)
  Base = (0,0,0)
  Profile = -> Sketch069
  ReferenceAxis = -> X_Axis079
FEATURE [PartDesign::Body] Body025  label="Body029"
  Group = -> [Sketch069,Revolution002]
  Origin = -> Origin079
  Tip = -> Revolution002
FEATURE [App::Part] Part042  label="e3d_2gt_idler001"
  Group = -> [Body025]
  Origin = -> Origin078
  Placement = pos=(11,-14,2.5e-15) rot=(0,1,0;4.71239rad)
FEATURE [App::Part] Part030  label="x_idler_assy"
  Group = -> [Screw001,Part033,Part__Feature039,Part__Feature040,Cylinder004,Part042]
  Origin = -> Origin044
  Placement = pos=(434,-10,0) rot=(0,0,1;0rad)
FEATURE [Part::Feature] Part__Feature090  label="DIN SIN_WEIDMULLER_(500mm)"
  shape: bbox 500 x 7.5 x 35 mm, 78 faces (baked)
FEATURE [Part::Box] Box  label="Cube"
  AttacherType = Attacher::AttachEngine3D
  Height = 100
  Length = 200
  Placement = pos=(380,-50,-50) rot=(0,0,1;0rad)
  Width = 100
FEATURE [Part::Cut] Cut
  Base = -> Part__Feature090
  Tool = -> Box
FEATURE [App::Part] Part043  label="15"_DIN_rail"
  Group = -> [Box,Part__Feature090,Cut]
  Origin = -> Origin080
  Placement = pos=(538,-228,465) rot=(0,0,1;3.14159rad)
FEATURE [Part::Feature] Part__Feature1347  label="Smoothieboard_X5"
  Placement = pos=(230,-238,468) rot=(0,0,1;3.14159rad)
  shape: bbox 135.9 x 20.1 x 111.2 mm, 1256 faces, 13 solids (baked)
FEATURE [Part::Feature] Part__Feature1348  label="PCB, RPi4ModelB"
  shape: bbox 85 x 1.6 x 56 mm, 136 faces (baked)
FEATURE [Part::Feature] Part__Feature1349  label="Broadcom BCM2711B0 CPU, RPi4ModelB"
  Placement = pos=(-13.25,0.8,-4.5) rot=(0,0,1;0rad)
  shape: bbox 15 x 2.3 x 15 mm, 29 faces, 2 solids (baked)
FEATURE [Part::Feature] Part__Feature1350  label="2.54 mm DUPONT MALE PIN HEADER, POE, 2X2, RPi4ModelB"
  Placement = pos=(19,0.8,-18.36) rot=(0,0,1;0rad)
  shape: bbox 5.08 x 11.3 x 5.08 mm, 102 faces, 5 solids (baked)
FEATURE [Part::Feature] Part__Feature1351  label="2.54 mm DUPONT MALE PIN HEADER, IO, 2X20, RPi4ModelB"
  Placement = pos=(-10,0.8,-24.5) rot=(0,0,1;0rad)
  shape: bbox 50.8 x 11.3 x 5.08 mm, 858 faces, 41 solids (baked)
FEATURE [Part::Feature] Part__Feature1352  label="Camera Connector, RPi4ModelB"
  Placement = pos=(4,0.8,16.5) rot=(0,1,0;1.5708rad)
  shape: bbox 5.072 x 5.68 x 22.4 mm, 995 faces, 17 solids (baked)
FEATURE [Part::Feature] Part__Feature1353  label="Microphone Plug, RPi4ModelB"
  Placement = pos=(11.5,0.8,21.65) rot=(0,0,1;0rad)
  shape: bbox 7.229 x 7.798 x 15 mm, 323 faces, 5 solids (baked)
FEATURE [Part::Feature] Part__Feature1354  label="Display Connector, RPi4ModelB"
  Placement = pos=(-38.5,0.8,0) rot=(0,-1,0;1.5708rad)
  shape: bbox 5.072 x 5.68 x 22.4 mm, 995 faces, 17 solids (baked)
FEATURE [Part::Feature] Part__Feature1355  label="Gigabit Ethernet Port, RPi4ModelB"
  Placement = pos=(45.5,7.55,-17.75) rot=(0,1,0;1.5708rad)
  shape: bbox 21.6 x 17.23 x 16.33 mm, 403 faces (baked)
FEATURE [Part::Feature] Part__Feature1356  label="Female Micro HDMI Connector, RPi4ModelB"
  Placement = pos=(-3,0.8,27.3875) rot=(0,0,1;0rad)
  shape: bbox 6.501 x 3.516 x 7.501 mm, 1058 faces (baked)
FEATURE [Part::Feature] Part__Feature1357  label="Female Micro HDMI Connector, RPi4ModelB001"
  Placement = pos=(-16.5,0.8,27.3875) rot=(0,0,1;0rad)
  shape: bbox 6.501 x 3.516 x 7.501 mm, 1058 faces (baked)
FEATURE [Part::Feature] Part__Feature1358  label="Female USB Type C Connector, RPi4ModelB"
  Placement = pos=(-31.3,0.8,26.5419) rot=(0,0,1;0rad)
  shape: bbox 8.94 x 3.96 x 7.9 mm, 403 faces (baked)
FEATURE [Part::Feature] Part__Feature1359  label="2X USB3.0 PORTS, RPi4ModelB"
  Placement = pos=(37.07,0.8,1) rot=(0,0,1;0rad)
  shape: bbox 17.47 x 19.41 x 15.83 mm, 1044 faces (baked)
FEATURE [Part::Feature] Part__Feature1360  label="91D77 D9WHV 778K, 4 GB LPDDR4 SDRAM, RPi4ModelB"
  Placement = pos=(2.25,0.8,-4.5) rot=(0,0,1;0rad)
  shape: bbox 10 x 0.8 x 14.5 mm, 180 faces (baked)
FEATURE [Part::Feature] Part__Feature1361  label="Cypress CYW43455 Wireless Module Cover, RPi4ModelB"
  Placement = pos=(-30.5,0.8,-14.5) rot=(0,0,1;0rad)
  shape: bbox 11 x 1.6 x 13 mm, 70 faces (baked)
FEATURE [Part::Feature] Part__Feature1362  label="SD Card Slot, RPi4ModelB"
  Placement = pos=(-35.3,-0.8,-1e-14) rot=(0.707107,0,-0.707107;3.14159rad)
  shape: bbox 11.4 x 1.45 x 11.95 mm, 479 faces, 10 solids (baked)
FEATURE [Part::Feature] Part__Feature1363  label="VIA VL805 PCIe USB 3.0 controller, RPi4ModelB"
  Placement = pos=(17.5,0.8,4) rot=(0,0,1;0rad)
  shape: bbox 8.8 x 0.8 x 8.8 mm, 398 faces (baked)
FEATURE [Part::Feature] Part__Feature1364  label="2X USB2.0 PORTS, RPi4ModelB"
  Placement = pos=(37.065,0.65,19) rot=(0,0,1;0rad)
  shape: bbox 17.86 x 19.16 x 15.45 mm, 1086 faces (baked)
FEATURE [Part::Feature] Part__Feature1365  label="Broadcom BCM54213PE Gigabit Ethernet Transceiver, RPi4ModelB"
  Placement = pos=(16.5,0.8,-10) rot=(0,0,1;0rad)
  shape: bbox 6.802 x 1.002 x 6.802 mm, 559 faces (baked)
FEATURE [Part::Feature] Part__Feature1366  label="MxL7704 Universal PMIC, RPi4ModelB"
  Placement = pos=(-32.5,0.8,16) rot=(0,0,1;0rad)
  shape: bbox 5.4 x 0.8 x 5.4 mm, 311 faces (baked)
FEATURE [App::Part] Raspberry_Pi_4_Model_B  label="Raspberry Pi 4 Model B"
  Group = -> [Part__Feature1348,Part__Feature1349,Part__Feature1350,Part__Feature1351,Part__Feature1352,Part__Feature1353,Part__Feature1354,Part__Feature1355,Part__Feature1356,Part__Feature1357,Part__Feature1358,Part__Feature1359,Part__Feature1360,Part__Feature1361,Part__Feature1362,Part__Feature1363,Part__Feature1364,Part__Feature1365,Part__Feature1366]
  Origin = -> Origin081
  Placement = pos=(405,-239,465) rot=(0,0,1;3.14159rad)
FEATURE [Sketcher::SketchObject] Sketch072
  MapMode = 5
  Support = -> [XY_Plane084]
  sketch-geometry (14):
    g0: LineSegment [constr] StartX=0 StartY=0 StartZ=0 EndX=0 EndY=-9.5892e-11 EndZ=0
    g1: LineSegment [constr] StartX=0 StartY=0 StartZ=0 EndX=-18 EndY=0 EndZ=0
    g2: LineSegment [constr] StartX=-18 StartY=0 StartZ=0 EndX=-18 EndY=20 EndZ=0
    g3: LineSegment [constr] StartX=-18 StartY=20 StartZ=0 EndX=0 EndY=20 EndZ=0
    g4: Circle [constr] CenterX=-12 CenterY=14 CenterZ=0 NormalX=0 NormalY=0 NormalZ=1 AngleXU=0 Radius=6
    g5: LineSegment StartX=7 StartY=12 StartZ=0 EndX=-5.51472 EndY=12 EndZ=0
    g6: LineSegment StartX=-5.51472 StartY=12 StartZ=0 EndX=-10 EndY=7.51472 EndZ=0
    g7: LineSegment StartX=-10 StartY=7.51472 StartZ=0 EndX=-10 EndY=-3.8 EndZ=0
    g8: LineSegment StartX=-10 StartY=-3.8 StartZ=0 EndX=2 EndY=-3.8 EndZ=0
    g9: LineSegment StartX=2 StartY=-3.8 StartZ=0 EndX=2 EndY=-20 EndZ=0
    g10: LineSegment StartX=2 StartY=-20 StartZ=0 EndX=0 EndY=-20 EndZ=0
    g11: LineSegment StartX=0 StartY=-20 StartZ=0 EndX=0 EndY=-40 EndZ=0
    g12: LineSegment StartX=0 StartY=-40 StartZ=0 EndX=7 EndY=-40 EndZ=0
    g13: LineSegment StartX=7 StartY=-40 StartZ=0 EndX=7 EndY=12 EndZ=0
  constraints (41):
    c: Coincident(g0,g-1)
    c: Coincident(g1,g-1)
    c: PointOnObject(g1,g-1)
    c: Coincident(g2,g1)
    c: Vertical(g2)
    c: Coincident(g3,g2)
    c: PointOnObject(g3,g-2)
    c: Horizontal(g3)
    c: Tangent(g4,g3)
    c: Tangent(g4,g2)
    c: Diameter(g4) = 12
    c: DistanceX(g3,g3) = 18
    c: DistanceY(g2,g2) = 20
    c: Horizontal(g5)
    c: Coincident(g5,g6)
    c: Tangent(g6,g4)
    c: Coincident(g6,g7)
    c: Vertical(g7)
    c: Coincident(g7,g8)
    c: Horizontal(g8)
    c: Coincident(g8,g9)
    c: Vertical(g9)
    c: Coincident(g9,g10)
    c: Horizontal(g10)
    c: Coincident(g10,g11)
    c: Coincident(g11,g12)
    c: Horizontal(g12)
    c: Coincident(g12,g13)
    c: Coincident(g13,g5)
    c: Vertical(g13)
    c: Angle(g8,g6) = 0.785398
    c: DistanceY(g-1,g5) = 12
    c: DistanceX(g10,g10) = 2
    c: DistanceX(g12,g12) = 7
    c: DistanceY(g9,g9) = 16.2
    c: DistanceY(g11,g11) = 20
    c: Coincident(g0,g-1)
    c: Vertical(g11)
    c: PointOnObject(g10,g-2)
    c: DistanceX(g7,g-1) = 10
    c: DistanceY(g7,g2) = 23.8
FEATURE [PartDesign::Pad] Pad026  label="Pad027"
  Length = 100
  Length2 = 100
  Midplane = true
  Profile = -> Sketch072
  Type = 0
FEATURE [Sketcher::SketchObject] Sketch070
  MapMode = 5
  Placement = pos=(0,0,0) rot=(0.57735,0.57735,0.57735;2.0944rad)
  Support = -> [YZ_Plane083]
  sketch-geometry (13):
    g0: LineSegment StartX=12 StartY=18.65 StartZ=0 EndX=12 EndY=-18.65 EndZ=0
    g1: LineSegment StartX=5.65 StartY=-25 StartZ=0 EndX=-12 EndY=-25 EndZ=0
    g2: LineSegment StartX=-16.4901 StartY=-23.1401 StartZ=0 EndX=-24.092 EndY=-15.5382 EndZ=0
    g3: LineSegment StartX=-24.092 StartY=15.5382 StartZ=0 EndX=-16.4901 EndY=23.1401 EndZ=0
    g4: LineSegment StartX=-12 StartY=25 StartZ=0 EndX=5.65 EndY=25 EndZ=0
    g5: ArcOfCircle CenterX=5.65 CenterY=18.65 CenterZ=0 NormalX=0 NormalY=0 NormalZ=1 AngleXU=0 Radius=6.35 StartAngle=0 EndAngle=1.5708
    g6: ArcOfCircle CenterX=-12 CenterY=18.65 CenterZ=0 NormalX=0 NormalY=0 NormalZ=1 AngleXU=0 Radius=6.35 StartAngle=1.5708 EndAngle=2.35619
    g7: ArcOfCircle CenterX=-12 CenterY=-18.65 CenterZ=0 NormalX=0 NormalY=0 NormalZ=1 AngleXU=0 Radius=6.35 StartAngle=3.92699 EndAngle=4.71239
    g8: ArcOfCircle CenterX=5.65 CenterY=-18.65 CenterZ=0 NormalX=0 NormalY=0 NormalZ=1 AngleXU=0 Radius=6.35 StartAngle=4.71239 EndAngle=6.28319
    g9: Circle CenterX=-12 CenterY=0 CenterZ=0 NormalX=0 NormalY=0 NormalZ=1 AngleXU=0 Radius=4.125
    g10: LineSegment StartX=-25 StartY=13.3462 StartZ=0 EndX=-25 EndY=-13.3462 EndZ=0
    g11: ArcOfCircle CenterX=-21.9 CenterY=13.3462 CenterZ=0 NormalX=0 NormalY=0 NormalZ=1 AngleXU=0 Radius=3.1 StartAngle=2.35619 EndAngle=3.14159
    g12: ArcOfCircle CenterX=-21.9 CenterY=-13.3462 CenterZ=0 NormalX=0 NormalY=0 NormalZ=1 AngleXU=0 Radius=3.1 StartAngle=3.14159 EndAngle=3.92699
  constraints (30):
    c: Vertical(g0)
    c: Horizontal(g1)
    c: Tangent(g4,g5) = 1.5708
    c: Tangent(g0,g5) = 1.5708
    c: Tangent(g4,g6) = 1.5708
    c: Tangent(g3,g6) = 1.5708
    c: Tangent(g2,g7) = 1.5708
    c: Tangent(g1,g7) = 1.5708
    c: Tangent(g0,g8) = 1.5708
    c: Tangent(g1,g8) = 1.5708
    c: Horizontal(g4)
    c: Equal(g7,g8)
    c: Symmetric(g4,g1,g-1)
    c: Symmetric(g6,g7,g-1)
    c: PointOnObject(g9,g-1)
    c: DistanceY(g1,g4) = 50
    c: Radius(g5) = 6.35
    c: Diameter(g9) = 8.25
    c: DistanceX(g-1,g0) = 12
    c: Angle(g2,g3) = 1.5708
    c: Vertical(g10)
    c: Tangent(g3,g11) = 1.5708
    c: Tangent(g10,g11) = -1.5708
    c: Tangent(g10,g12) = -1.5708
    c: Tangent(g2,g12) = 1.5708
    c: Radius(g11) = 3.1
    c: Symmetric(g11,g12,g-1)
    c: DistanceX(g10,g-1) = 25
    c: Vertical(g7,g9)
    c: DistanceX(g9,g-1) = 12
FEATURE [PartDesign::Pad] Pad025  label="Pad026"
  Length = 50
  Length2 = 100
  Midplane = true
  Placement = pos=(0,0,0) rot=(0.57735,0.57735,0.57735;2.0944rad)
  Profile = -> Sketch070
  Type = 0
FEATURE [PartDesign::Body] Body026  label="Body030"
  Group = -> [Sketch070,Pad025]
  Origin = -> Origin083
  Tip = -> Pad025
FEATURE [PartDesign::Boolean] Boolean001
  BaseFeature = -> Pad026
  Group = -> [Body026]
  Type = 2
FEATURE [PartDesign::Chamfer] Chamfer001
  Angle = 45
  Base = -> Boolean001 [Edge14]
  BaseFeature = -> Boolean001
  ChamferType = 0
  FlipDirection = false
  Size = 1
  Size2 = 1
  SupportTransform = true
FEATURE [PartDesign::Body] Body027  label="Body031"
  Group = -> [Sketch072,Pad026,Boolean001,Chamfer001]
  Origin = -> Origin084
  Tip = -> Chamfer001
FEATURE [Part::FeaturePython] Screw005  label="M8x20-Screw"  # Fasteners workbench fastener (typed FeaturePython)
  Placement = pos=(7,-12,2e-15) rot=(0,1,0;1.5708rad)
  diameter = 8
  invert = false
  length = 4
  lengthCustom = 20
  matchOuter = false
  offset = 0
  thread = false
  type = 16
FEATURE [Part::Feature] Part__Feature1367  label="Coupler_B"
  Placement = pos=(0,30,0) rot=(0.707107,0,0.707107;3.14159rad)
  shape: bbox 24.99 x 19.8 x 25 mm, 127 faces (baked)
FEATURE [Part::Feature] Part__Feature1368  label="Coupler_A001"
  shape: bbox 27.06 x 19.8 x 27.04 mm, 105 faces (baked)
FEATURE [Part::Feature] Part__Feature1369  label="Dampener001"
  Placement = pos=(2.8e-14,15,2.8e-14) rot=(0,1,0;0.785398rad)
  shape: bbox 23.57 x 11.4 x 23.57 mm, 123 faces (baked)
FEATURE [Part::Feature] Part__Feature1370  label="M3x12_Screw002"
  Placement = pos=(8,26,-6.75) rot=(0.187521,-0.694563,0.694563;3.51233rad)
  shape: bbox 5.756 x 5.756 x 15.2 mm, 67 faces (baked)
FEATURE [Part::Feature] Part__Feature1371  label="M3x12_Screw003"
  Placement = pos=(-6.75,4,8) rot=(-0.640748,0.640748,-0.422947;3.94185rad)
  shape: bbox 15.2 x 5.526 x 5.526 mm, 67 faces (baked)
FEATURE [App::Part] CouplerASM
  Group = -> [Part__Feature1367,Part__Feature1368,Part__Feature1369,Part__Feature1370,Part__Feature1371]
  Origin = -> Origin085
  Placement = pos=(25.4,1.086e-13,489) rot=(1,0,0;4.71239rad)
FEATURE [Part::Feature] Part__Feature1372  label="LC-0640-M6"
  Placement = pos=(6.5,8,5.5) rot=(-1,0,0;1.5708rad)
  shape: bbox 9.24 x 14 x 9.24 mm, 41 faces (baked)
FEATURE [App::Link] Link022  label="LC-0640-M007"
  LinkPlacement = pos=(-6.49998,8.00002,5.5) rot=(-1,0,0;1.5708rad)
  LinkedObject = -> Part__Feature1372
  Placement = pos=(-6.49998,8.00002,5.5) rot=(-1,0,0;1.5708rad)
FEATURE [Part::Feature] Part__Feature1373  label="_MSWZ6"
  Placement = pos=(-14.5,-16,5.5) rot=(0,0,1;0rad)
  shape: bbox 8 x 9 x 9 mm, 21 faces (baked)
FEATURE [PartDesign::Chamfer] Chamfer002
  Angle = 45
  Base = -> Fillet004 [Edge25]
  BaseFeature = -> Fillet004
  ChamferType = 0
  FlipDirection = false
  Placement = pos=(0,0,0) rot=(1,0,0;1.5708rad)
  Size = 1.7
  Size2 = 1
  SupportTransform = true
FEATURE [Sketcher::SketchObject] Sketch073
  AttachmentOffset = pos=(0,0,18) rot=(0,0,1;0rad)
  MapMode = 5
  Placement = pos=(18,-4e-15,4e-15) rot=(0.57735,0.57735,0.57735;2.0944rad)
  Support = -> [YZ_Plane061]
  sketch-geometry (2):
    g0: Circle CenterX=-0.5 CenterY=7 CenterZ=0 NormalX=0 NormalY=0 NormalZ=1 AngleXU=0 Radius=1.5
    g1: Circle CenterX=-12.5 CenterY=7 CenterZ=0 NormalX=0 NormalY=0 NormalZ=1 AngleXU=0 Radius=1.5
  constraints (6):
    c: Horizontal(g1,g0)
    c: Equal(g1,g0)
    c: Diameter(g0) = 3
    c: DistanceY(g-1,g0) = 7
    c: DistanceX(g1,g0) = 12
    c: DistanceX(g0,g-1) = 0.5
FEATURE [PartDesign::Hole] Hole014
  BaseFeature = -> Chamfer002
  Depth = 7
  DepthType = 0
  Diameter = 3.3
  DrillPoint = 1
  DrillPointAngle = 118
  HoleCutCountersinkAngle = 90
  HoleCutDepth = 0
  HoleCutDiameter = 3
  HoleCutType = 0
  ModelActualThread = false
  Placement = pos=(0,0,0) rot=(1,0,0;1.5708rad)
  Profile = -> Sketch073
  Tapered = false
  TaperedAngle = 90
  ThreadAngle = 0
  ThreadClass = 0
  ThreadCutOffInner = 0
  ThreadCutOffOuter = 0
  ThreadDirection = 0
  ThreadFit = 0
  ThreadPitch = 0
  ThreadSize = 3
  ThreadType = 1
  Threaded = false
FEATURE [PartDesign::Body] Body021  label="block"
  Group = -> [Sketch051,Pad021,Sketch052,Sketch053,Hole006,Sketch054,Hole007,Sketch055,Hole008,Sketch056,Sketch057,Pocket019,Hole009,Sketch058,Pad022,Sketch059,Hole010,Hole011,Sketch060,Hole012,Fillet004,Chamfer002,Sketch073,Hole014]
  Origin = -> Origin061
  Tip = -> Hole014
FEATURE [TechDraw::DrawSVGTemplate] Template002
  EditableTexts = Author=Alex Neufeld; DWG_num=2020-105; Date=09/05/2020; Revision=1; Scale=NTS; Subtitle=For 20mm V-Slot Rail; Title=Watercooled Print Head
  Height = 215.9
  Orientation = 1
  Width = 279.4
FEATURE [TechDraw::DrawViewPart] View002
  CoarseView = false
  Direction = (0.577,-0.577,0.577)
  Focus = 100
  HardHidden = false
  IsoCount = 0
  IsoHidden = false
  IsoVisible = false
  LockPosition = false
  Perspective = false
  Rotation = 0
  Scale = 0.5
  ScaleType = 0
  SeamHidden = false
  SeamVisible = true
  SmoothHidden = false
  SmoothVisible = true
  X = 30.583
  XDirection = (0.707,0.707,0)
  Y = 183.107
FEATURE [TechDraw::DrawProjGroupItem] ProjItem007  label="Front002"
  CoarseView = false
  Direction = (1,-1e-16,0)
  Focus = 100
  HardHidden = false
  IsoCount = 0
  IsoHidden = false
  IsoVisible = false
  LockPosition = true
  Perspective = false
  Rotation = 0
  RotationVector = (1,0,0)
  ScaleType = 2
  SeamHidden = false
  SeamVisible = true
  SmoothHidden = false
  SmoothVisible = true
  Type = 0
  X = 0
  XDirection = (1e-16,1,0)
  Y = 0
FEATURE [TechDraw::DrawProjGroupItem] ProjItem008  label="Left001"
  CoarseView = false
  Direction = (0,-1,0)
  Focus = 100
  HardHidden = false
  IsoCount = 0
  IsoHidden = false
  IsoVisible = false
  LockPosition = true
  Perspective = false
  Rotation = 0
  RotationVector = (1,0,0)
  ScaleType = 2
  SeamHidden = false
  SeamVisible = true
  SmoothHidden = false
  SmoothVisible = true
  Type = 1
  X = 65
  XDirection = (1,0,0)
  Y = 0
FEATURE [TechDraw::DrawProjGroupItem] ProjItem009  label="Rear"
  CoarseView = false
  Direction = (-1,1e-16,0)
  Focus = 100
  HardHidden = false
  IsoCount = 0
  IsoHidden = false
  IsoVisible = false
  LockPosition = true
  Perspective = false
  Rotation = 0
  RotationVector = (1,0,0)
  ScaleType = 2
  SeamHidden = false
  SeamVisible = true
  SmoothHidden = false
  SmoothVisible = true
  Type = 3
  X = 130
  XDirection = (-1e-16,-1,0)
  Y = 0
FEATURE [TechDraw::DrawProjGroupItem] ProjItem010  label="Right001"
  CoarseView = false
  Direction = (2e-16,1,0)
  Focus = 100
  HardHidden = false
  IsoCount = 0
  IsoHidden = false
  IsoVisible = false
  LockPosition = true
  Perspective = false
  Rotation = 0
  RotationVector = (1,0,0)
  ScaleType = 2
  SeamHidden = false
  SeamVisible = true
  SmoothHidden = false
  SmoothVisible = true
  Type = 2
  X = -65
  XDirection = (-1,2e-16,0)
  Y = 0
FEATURE [TechDraw::DrawProjGroupItem] ProjItem012  label="Top"
  CoarseView = false
  Direction = (0,0,1)
  Focus = 100
  HardHidden = false
  IsoCount = 0
  IsoHidden = false
  IsoVisible = false
  LockPosition = true
  Perspective = false
  Rotation = 0
  RotationVector = (1,0,0)
  ScaleType = 2
  SeamHidden = false
  SeamVisible = true
  SmoothHidden = false
  SmoothVisible = true
  Type = 4
  X = 0
  XDirection = (1e-16,1,0)
  Y = -70.3637
FEATURE [TechDraw::DrawProjGroupItem] ProjItem013  label="Bottom002"
  CoarseView = false
  Direction = (0,0,-1)
  Focus = 100
  HardHidden = false
  IsoCount = 0
  IsoHidden = false
  IsoVisible = false
  LockPosition = false
  Perspective = false
  Rotation = 0
  RotationVector = (1,0,0)
  ScaleType = 2
  SeamHidden = false
  SeamVisible = true
  SmoothHidden = false
  SmoothVisible = true
  Type = 5
  X = 0
  XDirection = (1e-16,1,0)
  Y = 15
FEATURE [TechDraw::DrawProjGroup] ProjGroup002
  Anchor = -> ProjItem007
  AutoDistribute = true
  LockPosition = false
  ProjectionType = 0
  Rotation = 0
  ScaleType = 0
  Views = -> [ProjItem007,ProjItem008,ProjItem009,ProjItem010,ProjItem012,ProjItem013]
  X = 103.639
  Y = 118.803
  spacingX = 15
  spacingY = 15
FEATURE [TechDraw::DrawViewDimension] Dimension024
  Arbitrary = false
  FormatSpec = R%.2f
  Inverted = false
  LockPosition = false
  MeasureType = 1
  OverTolerance = 0
  References2D = -> [ProjItem013]
  Rotation = 0
  ScaleType = 0
  TheoreticalExact = false
  Type = 4
  UnderTolerance = 0
  X = 19.1509
  Y = 14.0701
FEATURE [TechDraw::DrawViewDimension] Dimension025
  Arbitrary = false
  FormatSpec = %.2f
  Inverted = false
  LockPosition = false
  MeasureType = 1
  OverTolerance = 0
  References2D = -> [ProjItem013]
  Rotation = 0
  ScaleType = 0
  TheoreticalExact = false
  Type = 2
  UnderTolerance = 0
  X = -34.234
  Y = -0.195417
FEATURE [TechDraw::DrawViewDimension] Dimension026
  Arbitrary = false
  FormatSpec = %.2f
  Inverted = false
  LockPosition = false
  MeasureType = 1
  OverTolerance = 0
  References2D = -> [ProjItem013]
  Rotation = 0
  ScaleType = 0
  TheoreticalExact = false
  Type = 1
  UnderTolerance = 0
  X = -0.586252
  Y = -21.9856
FEATURE [TechDraw::DrawViewDimension] Dimension028
  Arbitrary = false
  FormatSpec = %.2f
  Inverted = false
  LockPosition = false
  MeasureType = 1
  OverTolerance = 0
  References2D = -> [ProjItem013]
  Rotation = 0
  ScaleType = 0
  TheoreticalExact = false
  Type = 1
  UnderTolerance = 0
  X = -16.2817
  Y = 7.29445
FEATURE [TechDraw::DrawViewDimension] Dimension029
  Arbitrary = false
  FormatSpec = %.2f
  Inverted = false
  LockPosition = false
  MeasureType = 1
  OverTolerance = 0
  References2D = -> [ProjItem013]
  Rotation = 0
  ScaleType = 0
  TheoreticalExact = false
  Type = 2
  UnderTolerance = 0
  X = 28.5566
  Y = -6.20621
FEATURE [TechDraw::DrawViewDimension] Dimension030
  Arbitrary = false
  FormatSpec = %.2f
  Inverted = false
  LockPosition = false
  MeasureType = 1
  OverTolerance = 0
  References2D = -> [ProjItem013]
  Rotation = 0
  ScaleType = 0
  TheoreticalExact = false
  Type = 1
  UnderTolerance = 0
  X = 37.3578
  Y = 3.61298
FEATURE [TechDraw::DrawViewDimension] Dimension031
  Arbitrary = false
  FormatSpec = %.2f
  Inverted = false
  LockPosition = false
  MeasureType = 1
  OverTolerance = 0
  References2D = -> [ProjItem008]
  Rotation = 0
  ScaleType = 0
  TheoreticalExact = false
  Type = 1
  UnderTolerance = 0
  X = -5.76623
  Y = 0.287702
FEATURE [TechDraw::DrawViewDimension] Dimension032
  Arbitrary = false
  FormatSpec = %.2f
  Inverted = false
  LockPosition = false
  MeasureType = 1
  OverTolerance = 0
  References2D = -> [ProjItem008]
  Rotation = 0
  ScaleType = 0
  TheoreticalExact = false
  Type = 2
  UnderTolerance = 0
  X = -0.901396
  Y = 15.1348
FEATURE [TechDraw::DrawViewDimension] Dimension033
  Arbitrary = false
  FormatSpec = %.2f
  Inverted = false
  LockPosition = false
  MeasureType = 1
  OverTolerance = 0
  References2D = -> [ProjItem008]
  Rotation = 0
  ScaleType = 0
  TheoreticalExact = false
  Type = 2
  UnderTolerance = 0
  X = 21.8895
  Y = -17.5
FEATURE [TechDraw::DrawViewDimension] Dimension035
  Arbitrary = false
  FormatSpec = %.2f
  Inverted = false
  LockPosition = false
  MeasureType = 1
  OverTolerance = 0
  References2D = -> [ProjItem009]
  Rotation = 0
  ScaleType = 0
  TheoreticalExact = false
  Type = 2
  UnderTolerance = 0
  X = 28.1125
  Y = -31.9901
FEATURE [TechDraw::DrawViewDimension] Dimension036
  Arbitrary = false
  FormatSpec = %.2f
  Inverted = false
  LockPosition = false
  MeasureType = 1
  OverTolerance = 0
  References2D = -> [ProjItem009]
  Rotation = 0
  ScaleType = 0
  TheoreticalExact = false
  Type = 1
  UnderTolerance = 0
  X = 12.1513
  Y = -8.7684
FEATURE [TechDraw::DrawViewDimension] Dimension037
  Arbitrary = false
  FormatSpec = %.2f
  Inverted = false
  LockPosition = false
  MeasureType = 1
  OverTolerance = 0
  References2D = -> [ProjItem009]
  Rotation = 0
  ScaleType = 0
  TheoreticalExact = false
  Type = 2
  UnderTolerance = 0
  X = 1.14094
  Y = -29.3403
FEATURE [TechDraw::DrawViewDimension] Dimension038
  Arbitrary = false
  FormatSpec = %.2f
  Inverted = false
  LockPosition = false
  MeasureType = 1
  OverTolerance = 0
  References2D = -> [ProjItem009]
  Rotation = 0
  ScaleType = 0
  TheoreticalExact = false
  Type = 2
  UnderTolerance = 0
  X = -34.6499
  Y = -0.866784
FEATURE [TechDraw::DrawViewDimension] Dimension039
  Arbitrary = false
  FormatSpec = %.2f
  Inverted = false
  LockPosition = false
  MeasureType = 1
  OverTolerance = 0
  References2D = -> [ProjItem009]
  Rotation = 0
  ScaleType = 0
  TheoreticalExact = false
  Type = 1
  UnderTolerance = 0
  X = 18.4523
  Y = 34.8435
FEATURE [TechDraw::DrawViewDimension] Dimension040
  Arbitrary = false
  FormatSpec = %.2f
  Inverted = false
  LockPosition = false
  MeasureType = 1
  OverTolerance = 0
  References2D = -> [ProjItem009]
  Rotation = 0
  ScaleType = 0
  TheoreticalExact = false
  Type = 1
  UnderTolerance = 0
  X = -5.41184
  Y = 32.4516
FEATURE [TechDraw::DrawViewDimension] Dimension042
  Arbitrary = false
  FormatSpec = %.2f
  Inverted = false
  LockPosition = false
  MeasureType = 1
  OverTolerance = 0
  References2D = -> [ProjItem012]
  Rotation = 0
  ScaleType = 0
  TheoreticalExact = false
  Type = 2
  UnderTolerance = 0
  X = -29.4955
  Y = 11.4157
FEATURE [TechDraw::DrawViewDimension] Dimension043
  Arbitrary = false
  FormatSpec = %.2f
  Inverted = false
  LockPosition = false
  MeasureType = 1
  OverTolerance = 0
  References2D = -> [ProjItem012]
  Rotation = 0
  ScaleType = 0
  TheoreticalExact = false
  Type = 2
  UnderTolerance = 0
  X = -36.1103
  Y = 7.53454
FEATURE [TechDraw::DrawViewDimension] Dimension044
  Arbitrary = false
  FormatSpec = %.2f
  Inverted = false
  LockPosition = false
  MeasureType = 1
  OverTolerance = 0
  References2D = -> [ProjItem012]
  Rotation = 0
  ScaleType = 0
  TheoreticalExact = false
  Type = 2
  UnderTolerance = 0
  X = -42.6347
  Y = 2.67713
FEATURE [TechDraw::DrawViewDimension] Dimension045
  Arbitrary = false
  FormatSpec = %.2f
  Inverted = false
  LockPosition = false
  MeasureType = 1
  OverTolerance = 0
  References2D = -> [ProjItem012]
  Rotation = 0
  ScaleType = 0
  TheoreticalExact = false
  Type = 1
  UnderTolerance = 0
  X = -14.7458
  Y = 24.3035
FEATURE [TechDraw::DrawViewDimension] Dimension046
  Arbitrary = false
  FormatSpec = %.2f
  Inverted = false
  LockPosition = false
  MeasureType = 1
  OverTolerance = 0
  References2D = -> [ProjItem012]
  Rotation = 0
  ScaleType = 0
  TheoreticalExact = false
  Type = 1
  UnderTolerance = 0
  X = -15.4599
  Y = -23.8107
FEATURE [TechDraw::DrawViewDimension] Dimension047
  Arbitrary = false
  FormatSpec = %.2f
  Inverted = false
  LockPosition = false
  MeasureType = 1
  OverTolerance = 0
  References2D = -> [ProjItem012]
  Rotation = 0
  ScaleType = 0
  TheoreticalExact = false
  Type = 1
  UnderTolerance = 0
  X = -8.2936
  Y = -30.4726
FEATURE [TechDraw::DrawViewDimension] Dimension048
  Arbitrary = false
  FormatSpec = %.2f
  Inverted = false
  LockPosition = false
  MeasureType = 1
  OverTolerance = 0
  References2D = -> [ProjItem007]
  Rotation = 0
  ScaleType = 0
  TheoreticalExact = false
  Type = 2
  UnderTolerance = 0
  X = -34.5365
  Y = -11.6191
FEATURE [TechDraw::DrawViewDimension] Dimension049
  Arbitrary = false
  FormatSpec = %.2f
  Inverted = false
  LockPosition = false
  MeasureType = 1
  OverTolerance = 0
  References2D = -> [ProjItem008]
  Rotation = 0
  ScaleType = 0
  TheoreticalExact = false
  Type = 2
  UnderTolerance = 0
  X = -24.7797
  Y = -13.3181
FEATURE [TechDraw::DrawViewDimension] Dimension050
  Arbitrary = false
  FormatSpec = %.2f
  Inverted = false
  LockPosition = false
  MeasureType = 1
  OverTolerance = 0
  References2D = -> [ProjItem007]
  Rotation = 0
  ScaleType = 0
  TheoreticalExact = false
  Type = 2
  UnderTolerance = 0
  X = -41.5171
  Y = -22.3563
FEATURE [TechDraw::DrawViewDimension] Dimension051
  Arbitrary = false
  FormatSpec = %.2f
  Inverted = false
  LockPosition = false
  MeasureType = 1
  OverTolerance = 0
  References2D = -> [ProjItem007]
  Rotation = 0
  ScaleType = 0
  TheoreticalExact = false
  Type = 1
  UnderTolerance = 0
  X = 6.60144
  Y = -35.5375
FEATURE [TechDraw::DrawViewDimension] Dimension052
  Arbitrary = false
  FormatSpec = %.2f
  Inverted = false
  LockPosition = false
  MeasureType = 1
  OverTolerance = 0
  References2D = -> [ProjItem007]
  Rotation = 0
  ScaleType = 0
  TheoreticalExact = false
  Type = 1
  UnderTolerance = 0
  X = 6.19512
  Y = -28.64
FEATURE [TechDraw::DrawViewAnnotation] Annotation
  Font = Sans Serif
  LineSpace = 80
  LockPosition = false
  MaxWidth = -1
  Rotation = 0
  ScaleType = 0
  Text = Drill 3/16" - Depth 27.0 mm | Drill 5mm - Depth 11.0 mm | Tap M6x1.0 | Countersink to match M6 plug
  TextSize = 2.5
  TextStyle = 0
  X = 243.063
  Y = 71.5534
FEATURE [TechDraw::DrawViewDimension] Dimension053
  Arbitrary = false
  FormatSpec = %.2f
  Inverted = false
  LockPosition = false
  MeasureType = 1
  OverTolerance = 0
  References2D = -> [ProjItem010]
  Rotation = 0
  ScaleType = 0
  TheoreticalExact = false
  Type = 2
  UnderTolerance = 0
  X = -25.1679
  Y = -21.1101
FEATURE [TechDraw::DrawViewDimension] Dimension054
  Arbitrary = false
  FormatSpec = %.2f
  Inverted = false
  LockPosition = false
  MeasureType = 1
  OverTolerance = 0
  References2D = -> [ProjItem010]
  Rotation = 0
  ScaleType = 0
  TheoreticalExact = false
  Type = 1
  UnderTolerance = 0
  X = 2.56697
  Y = -35.7193
FEATURE [TechDraw::DrawViewDimension] Dimension055
  Arbitrary = false
  FormatSpec = %.2f
  Inverted = false
  LockPosition = false
  MeasureType = 1
  OverTolerance = 0
  References2D = -> [ProjItem010]
  Rotation = 0
  ScaleType = 0
  TheoreticalExact = false
  Type = 1
  UnderTolerance = 0
  X = -15.1824
  Y = -41.0119
FEATURE [TechDraw::DrawViewAnnotation] Annotation001
  Font = Sans Serif
  LineSpace = 80
  LockPosition = false
  MaxWidth = -1
  Rotation = 0
  ScaleType = 0
  Text = Drill 3/16" - Depth 32.0mm | Drill 5.0mm - Depth 7.3mm | Tap M6x1.0
  TextSize = 2.5
  TextStyle = 0
  X = 31.0661
  Y = 115.642
FEATURE [TechDraw::DrawViewAnnotation] Annotation002
  Font = Sans Serif
  LineSpace = 80
  LockPosition = false
  MaxWidth = -1
  Rotation = 0
  ScaleType = 0
  Text = Through Drill 1/8" & tap M4x0.7
  TextSize = 2.5
  TextStyle = 0
  X = 153.114
  Y = 56.3806
FEATURE [TechDraw::DrawViewAnnotation] Annotation003
  Font = Sans Serif
  LineSpace = 80
  LockPosition = false
  MaxWidth = -1
  Rotation = 0
  ScaleType = 0
  Text = Drill 5/64" - Depth 6.0mm | Tap M2.5x0.45
  TextSize = 2.5
  TextStyle = 0
  X = 151.717
  Y = 30.2802
FEATURE [TechDraw::DrawViewAnnotation] Annotation004
  Font = Sans Serif
  LineSpace = 80
  LockPosition = false
  MaxWidth = -1
  Rotation = 0
  ScaleType = 0
  Text = Drill 7.20mm | Counterbore 12.0mm | Depth 2.18mm
  TextSize = 2.5
  TextStyle = 0
  X = 106.454
  Y = 149.635
FEATURE [TechDraw::DrawViewDimension] Dimension056
  Arbitrary = false
  FormatSpec = %.2f
  Inverted = false
  LockPosition = false
  MeasureType = 1
  OverTolerance = 0
  References2D = -> [ProjItem007]
  Rotation = 0
  ScaleType = 0
  TheoreticalExact = false
  Type = 2
  UnderTolerance = 0
  X = 28.3752
  Y = 1.21565
FEATURE [TechDraw::DrawViewAnnotation] Annotation005
  Font = Sans Serif
  LineSpace = 80
  LockPosition = false
  MaxWidth = -1
  Rotation = 0
  ScaleType = 0
  Text = Through-drill 3/32" & tap M3x0.5
  TextSize = 2.5
  TextStyle = 0
  X = 236.033
  Y = 126.03
FEATURE [TechDraw::DrawViewAnnotation] Annotation006
  Font = Sans Serif
  LineSpace = 80
  LockPosition = false
  MaxWidth = -1
  Rotation = 0
  ScaleType = 0
  Text = Drill 5/32" - Depth 10.0mm | Tap M5x0.8
  TextSize = 2.5
  TextStyle = 0
  X = 204.142
  Y = 82.1491
FEATURE [TechDraw::DrawViewDimension] Dimension057
  Arbitrary = false
  FormatSpec = %.2f
  Inverted = false
  LockPosition = false
  MeasureType = 1
  OverTolerance = 0
  References2D = -> [ProjItem007]
  Rotation = 0
  ScaleType = 0
  TheoreticalExact = false
  Type = 1
  UnderTolerance = 0
  X = -14.2126
  Y = 0.579442
FEATURE [TechDraw::DrawViewDimension] Dimension058
  Arbitrary = false
  FormatSpec = %.2f
  Inverted = false
  LockPosition = false
  MeasureType = 1
  OverTolerance = 0
  References2D = -> [ProjItem007]
  Rotation = 0
  ScaleType = 0
  TheoreticalExact = false
  Type = 2
  UnderTolerance = 0
  X = 16.8932
  Y = -8.86083
FEATURE [TechDraw::DrawViewDimension] Dimension059
  Arbitrary = false
  FormatSpec = %.2f
  Inverted = false
  LockPosition = false
  MeasureType = 1
  OverTolerance = 0
  References2D = -> [ProjItem009]
  Rotation = 0
  ScaleType = 0
  TheoreticalExact = false
  Type = 1
  UnderTolerance = 0
  X = 12.9638
  Y = -1.97335
FEATURE [TechDraw::DrawLeaderLine] LeaderLine
  AutoHorizontal = true
  EndSymbol = 7
  LeaderParent = -> ProjItem009
  LockPosition = true
  Rotation = 0
  Scalable = false
  ScaleType = 0
  StartSymbol = 0
  WayPoints = (3) [(0,0,0),(-224.773,-77.6001,0),(-166.796,-77.6001,0)]
  X = -1.79941
  Y = 0.349869
FEATURE [TechDraw::DrawLeaderLine] LeaderLine001
  AutoHorizontal = true
  EndSymbol = 7
  LeaderParent = -> ProjItem009
  LockPosition = true
  Rotation = 0
  Scalable = false
  ScaleType = 0
  StartSymbol = 0
  WayPoints = (3) [(0,0,0),(-68.577,183.451,0),(-97.1196,183.451,0)]
  X = -2.70674
  Y = -16.5506
FEATURE [TechDraw::DrawLeaderLine] LeaderLine002
  AutoHorizontal = true
  EndSymbol = 7
  LeaderParent = -> ProjItem009
  LockPosition = true
  Rotation = 0
  Scalable = false
  ScaleType = 0
  StartSymbol = 0
  WayPoints = (3) [(0,0,0),(80.2759,208.717,0),(72.2586,208.717,0)]
  X = 18.4429
  Y = -22.4083
FEATURE [TechDraw::DrawLeaderLine] LeaderLine003
  AutoHorizontal = true
  EndSymbol = 7
  LeaderParent = -> ProjItem007
  LockPosition = true
  Rotation = 0
  Scalable = false
  ScaleType = 0
  StartSymbol = 0
  WayPoints = (3) [(0,0,0),(130.582,-100.612,0),(28.8993,-100.612,0)]
  X = 15.0953
  Y = 21.8222
FEATURE [TechDraw::DrawLeaderLine] LeaderLine004
  AutoHorizontal = true
  EndSymbol = 7
  LeaderParent = -> ProjItem010
  LockPosition = true
  Rotation = 0
  Scalable = false
  ScaleType = 0
  StartSymbol = 0
  WayPoints = (3) [(0,0,0),(160.242,-169.036,0),(48.8544,-169.036,0)]
  X = 6.30669
  Y = -17.0626
FEATURE [TechDraw::DrawLeaderLine] LeaderLine005
  AutoHorizontal = true
  EndSymbol = 7
  LeaderParent = -> ProjItem012
  LockPosition = true
  Rotation = 0
  Scalable = false
  ScaleType = 0
  StartSymbol = 0
  WayPoints = (3) [(0,0,0),(55.2298,-68.074,0),(346.792,-68.074,0)]
  X = -5.81726
  Y = 1.79244
FEATURE [TechDraw::DrawLeaderLine] LeaderLine006
  AutoHorizontal = true
  EndSymbol = 7
  LeaderParent = -> ProjItem012
  LockPosition = true
  Rotation = 0
  Scalable = false
  ScaleType = 0
  StartSymbol = 0
  WayPoints = (3) [(0,0,0),(83.487,113.029,0),(211.928,113.029,0)]
  X = 9.21039
  Y = -5.91405
FEATURE [TechDraw::DrawViewDimension] Dimension060
  Arbitrary = false
  FormatSpec = %.2f
  Inverted = false
  LockPosition = false
  MeasureType = 1
  OverTolerance = 0
  References2D = -> [ProjItem013]
  Rotation = 0
  ScaleType = 0
  TheoreticalExact = false
  Type = 2
  UnderTolerance = 0
  X = -15.7965
  Y = -8.8593
FEATURE [TechDraw::DrawLeaderLine] LeaderLine007
  AutoHorizontal = true
  EndSymbol = 7
  LeaderParent = -> ProjItem012
  LockPosition = true
  Rotation = 0
  Scalable = false
  ScaleType = 0
  StartSymbol = 0
  WayPoints = (3) [(0,0,0),(-136.48,122.41,0),(-289.843,122.41,0)]
  X = -16.9452
  Y = -11.0576
FEATURE [TechDraw::DrawViewAnnotation] Annotation007
  Font = Sans Serif
  LineSpace = 80
  LockPosition = false
  MaxWidth = -1
  Rotation = 0
  ScaleType = 0
  Text = Pocket to provide clearance |  for Hemera Heatbreak | Depth 4.0mm
  TextSize = 2.5
  TextStyle = 0
  X = 45.3136
  Y = 24.4432
FEATURE [TechDraw::DrawViewDimension] Dimension061
  Arbitrary = false
  FormatSpec = %.2f
  Inverted = false
  LockPosition = false
  MeasureType = 1
  OverTolerance = 0
  References2D = -> [ProjItem012]
  Rotation = 0
  ScaleType = 0
  TheoreticalExact = false
  Type = 2
  UnderTolerance = 0
  X = 24.7033
  Y = 25.7597
FEATURE [TechDraw::DrawViewDimension] Dimension062
  Arbitrary = false
  FormatSpec = %.2f
  Inverted = false
  LockPosition = false
  MeasureType = 1
  OverTolerance = 0
  References2D = -> [ProjItem012]
  Rotation = 0
  ScaleType = 0
  TheoreticalExact = false
  Type = 2
  UnderTolerance = 0
  X = 18.2398
  Y = 26.1674
FEATURE [TechDraw::DrawViewDimension] Dimension063
  Arbitrary = false
  FormatSpec = %.2f
  Inverted = false
  LockPosition = false
  MeasureType = 1
  OverTolerance = 0
  References2D = -> [ProjItem012]
  Rotation = 0
  ScaleType = 0
  TheoreticalExact = false
  Type = 1
  UnderTolerance = 0
  X = -21.2141
  Y = -1.32694
FEATURE [TechDraw::DrawViewDimension] Dimension064
  Arbitrary = false
  FormatSpec = %.2f
  Inverted = false
  LockPosition = false
  MeasureType = 1
  OverTolerance = 0
  References2D = -> [ProjItem012]
  Rotation = 0
  ScaleType = 0
  TheoreticalExact = false
  Type = 1
  UnderTolerance = 0
  X = -8.89372
  Y = -7.61363
FEATURE [TechDraw::DrawLeaderLine] LeaderLine008
  AutoHorizontal = true
  EndSymbol = 7
  LeaderParent = -> ProjItem007
  LockPosition = true
  Rotation = 0
  Scalable = false
  ScaleType = 0
  StartSymbol = 0
  WayPoints = (3) [(0,0,0),(299.692,157.585,0),(353.158,157.585,0)]
  X = 1.42174
  Y = -17.8935
FEATURE [TechDraw::DrawViewAnnotation] Annotation008
  Font = Sans Serif
  LineSpace = 80
  LockPosition = false
  MaxWidth = -1
  Rotation = 0
  ScaleType = 0
  Text = Drill 3/32" - Depth 7.0mm | Tap M3x0.5
  TextSize = 2.5
  TextStyle = 0
  X = 156.865
  Y = 84.0309
FEATURE [TechDraw::DrawPage] Page002  label="watercooled_printhead_dwg"
  KeepUpdated = true
  NextBalloonIndex = 1
  ProjectionType = 0
  Template = -> Template002
  Views = -> [View002,ProjGroup002,Dimension024,Dimension025,Dimension026,Dimension028,Dimension029,Dimension030,Dimension031,Dimension032,Dimension033,Dimension035,Dimension036,Dimension037,Dimension038,Dimension039,Dimension040,Dimension042,Dimension043,Dimension044,Dimension045,Dimension046,Dimension047,Dimension048,Dimension049,Dimension050,Dimension051,Dimension052,Annotation,Dimension053,Dimension054,+27 more]
FEATURE [Part::Feature] Part__Feature1374  label="Bloc 03"
  Placement = pos=(-2e-15,245.1,0.01) rot=(0,0,1;3.14159rad)
  shape: bbox 27.84 x 39.9 x 15.31 mm, 44 faces (baked)
FEATURE [Part::Feature] Part__Feature1375  label="Bloc 01"
  Placement = pos=(0,224.675,15.31) rot=(1,0,0;3.14159rad)
  shape: bbox 29.27 x 37.82 x 15.31 mm, 48 faces (baked)
FEATURE [Part::Feature] Part__Feature1376  label="Bloc 004"
  Placement = pos=(0,204.25,15.31) rot=(1,0,0;3.14159rad)
  shape: bbox 29.27 x 37.82 x 15.31 mm, 48 faces (baked)
FEATURE [Part::Feature] Part__Feature1377  label="Bloc 005"
  Placement = pos=(0,183.825,15.31) rot=(1,0,0;3.14159rad)
  shape: bbox 29.27 x 37.82 x 15.31 mm, 48 faces (baked)
FEATURE [Part::Feature] Part__Feature1378  label="Bloc 006"
  Placement = pos=(0,163.4,15.31) rot=(1,0,0;3.14159rad)
  shape: bbox 29.27 x 37.82 x 15.31 mm, 48 faces (baked)
FEATURE [Part::Feature] Part__Feature1379  label="Bloc 007"
  Placement = pos=(0,142.975,15.31) rot=(1,0,0;3.14159rad)
  shape: bbox 29.27 x 37.82 x 15.31 mm, 48 faces (baked)
FEATURE [Part::Feature] Part__Feature1380  label="Bloc 008"
  Placement = pos=(0,122.55,15.31) rot=(1,0,0;3.14159rad)
  shape: bbox 29.27 x 37.82 x 15.31 mm, 48 faces (baked)
FEATURE [Part::Feature] Part__Feature1381  label="Bloc 009"
  Placement = pos=(0,102.125,15.31) rot=(1,0,0;3.14159rad)
  shape: bbox 29.27 x 37.82 x 15.31 mm, 48 faces (baked)
FEATURE [Part::Feature] Part__Feature1382  label="Bloc 010"
  Placement = pos=(0,81.7,15.31) rot=(1,0,0;3.14159rad)
  shape: bbox 29.27 x 37.82 x 15.31 mm, 48 faces (baked)
FEATURE [Part::Feature] Part__Feature1383  label="Bloc 011"
  Placement = pos=(0,61.275,15.31) rot=(1,0,0;3.14159rad)
  shape: bbox 29.27 x 37.82 x 15.31 mm, 48 faces (baked)
FEATURE [Part::Feature] Part__Feature1384  label="Bloc 012"
  Placement = pos=(0,40.85,15.31) rot=(1,0,0;3.14159rad)
  shape: bbox 29.27 x 37.82 x 15.31 mm, 48 faces (baked)
FEATURE [Part::Feature] Part__Feature1385  label="Bloc 013"
  Placement = pos=(0,20.425,15.31) rot=(1,0,0;3.14159rad)
  shape: bbox 29.27 x 37.82 x 15.31 mm, 48 faces (baked)
FEATURE [Part::Feature] Part__Feature1386  label="Bloc 014"
  Placement = pos=(0,0,76.2271) rot=(0,0,1;0rad)
  shape: bbox 29.27 x 37.82 x 15.31 mm, 48 faces (baked)
FEATURE [Part::Feature] Part__Feature1387  label="Bloc 02"
  Placement = pos=(1e-15,20.425,91.5271) rot=(0,1,0;3.14159rad)
  shape: bbox 29.27 x 37.82 x 15.31 mm, 30 faces (baked)
FEATURE [Part::Feature] Part__Feature1388  label="Bloc 015"
  Placement = pos=(0,-26.3779,60.9979) rot=(1,0,0;1.0472rad)
  shape: bbox 29.27 x 30.48 x 38.61 mm, 48 faces (baked)
FEATURE [Part::Feature] Part__Feature1389  label="Bloc 016"
  Placement = pos=(0,-26.3779,30.5393) rot=(1,0,0;2.0944rad)
  shape: bbox 29.27 x 31.13 x 39.43 mm, 48 faces (baked)
FEATURE [Part::Feature] Part__Feature1390  label="Bloc 017"
  Placement = pos=(0,-30.4586,45.7686) rot=(1,0,0;1.5708rad)
  shape: bbox 29.27 x 15.31 x 37.82 mm, 48 faces (baked)
FEATURE [Part::Feature] Part__Feature1391  label="Bloc 018"
  Placement = pos=(0,-15.2293,72.1465) rot=(1,0,0;0.523599rad)
  shape: bbox 29.27 x 39.43 x 31.13 mm, 48 faces (baked)
FEATURE [Part::Feature] Part__Feature1392  label="Bloc 019"
  Placement = pos=(0,-15.2293,19.3907) rot=(1,0,0;2.61799rad)
  shape: bbox 29.27 x 38.61 x 30.48 mm, 48 faces (baked)
FEATURE [Part::Feature] Part__Feature1393  label="Bloc 020"
  Placement = pos=(0,-9.2e-14,15.31) rot=(1,0,0;3.14159rad)
  shape: bbox 29.27 x 37.82 x 15.31 mm, 48 faces (baked)
FEATURE [Part::Feature] Part__Feature1394  label="COMPOUND"
  shape: bbox 1.85 x 7.655 x 15.31 mm, 0 faces, 0 solids (baked)
FEATURE [App::Part] Part045  label="rounded_part"
  Group = -> [Part__Feature1394,Part__Feature1392,Part__Feature1391,Part__Feature1390,Part__Feature1389,Part__Feature1388,Part__Feature1387,Part__Feature1386]
  Origin = -> Origin087
  Placement = pos=(0,-61.2,0) rot=(0,0,1;0rad)
FEATURE [Part::Feature] Part__Feature1395  label="Bloc 021"
  Placement = pos=(0,-20.4,15.31) rot=(1,0,0;3.14159rad)
  shape: bbox 29.27 x 37.82 x 15.31 mm, 48 faces (baked)
FEATURE [Part::Feature] Part__Feature1396  label="Bloc 022"
  Placement = pos=(0,-40.8,15.31) rot=(1,0,0;3.14159rad)
  shape: bbox 29.27 x 37.82 x 15.31 mm, 48 faces (baked)
FEATURE [Part::Feature] Part__Feature1397  label="Bloc 023"
  Placement = pos=(0,-61.2,15.31) rot=(1,0,0;3.14159rad)
  shape: bbox 29.27 x 37.82 x 15.31 mm, 48 faces (baked)
FEATURE [App::Part] Document  label="z_cable_chain"
  Group = -> [Part__Feature1374,Part__Feature1375,Part__Feature1376,Part__Feature1377,Part__Feature1378,Part__Feature1379,Part__Feature1380,Part__Feature1381,Part__Feature1382,Part__Feature1383,Part__Feature1384,Part__Feature1385,Part__Feature1393,Part045,Part__Feature1395,Part__Feature1396,Part__Feature1397]
  Origin = -> Origin086
  Placement = pos=(25,-179,167) rot=(1,0,0;1.5708rad)
FEATURE [Part::Feature] Part__Feature1398  label="Bloc 024"
  Placement = pos=(0,355.162,83.0043) rot=(1,0,0;0.05236rad)
  shape: bbox 27.84 x 40.03 x 17.27 mm, 44 faces (baked)
FEATURE [Part::Feature] Part__Feature1399  label="Bloc 025"
  Placement = pos=(0,224.675,15.31) rot=(1,0,0;3.14159rad)
  shape: bbox 29.27 x 37.82 x 15.31 mm, 48 faces (baked)
FEATURE [Part::Feature] Part__Feature1400  label="Bloc 026"
  Placement = pos=(0,204.25,15.31) rot=(1,0,0;3.14159rad)
  shape: bbox 29.27 x 37.82 x 15.31 mm, 48 faces (baked)
FEATURE [Part::Feature] Part__Feature1401  label="Bloc 027"
  Placement = pos=(0,183.825,15.31) rot=(1,0,0;3.14159rad)
  shape: bbox 29.27 x 37.82 x 15.31 mm, 48 faces (baked)
FEATURE [Part::Feature] Part__Feature1402  label="Bloc 028"
  Placement = pos=(0,163.4,15.31) rot=(1,0,0;3.14159rad)
  shape: bbox 29.27 x 37.82 x 15.31 mm, 48 faces (baked)
FEATURE [Part::Feature] Part__Feature1403  label="Bloc 029"
  Placement = pos=(0,142.975,15.31) rot=(1,0,0;3.14159rad)
  shape: bbox 29.27 x 37.82 x 15.31 mm, 48 faces (baked)
FEATURE [Part::Feature] Part__Feature1404  label="Bloc 030"
  Placement = pos=(0,122.55,15.31) rot=(1,0,0;3.14159rad)
  shape: bbox 29.27 x 37.82 x 15.31 mm, 48 faces (baked)
FEATURE [Part::Feature] Part__Feature1405  label="Bloc 031"
  Placement = pos=(0,102.125,15.31) rot=(1,0,0;3.14159rad)
  shape: bbox 29.27 x 37.82 x 15.31 mm, 48 faces (baked)
FEATURE [Part::Feature] Part__Feature1406  label="Bloc 032"
  Placement = pos=(0,81.7,15.31) rot=(1,0,0;3.14159rad)
  shape: bbox 29.27 x 37.82 x 15.31 mm, 48 faces (baked)
FEATURE [Part::Feature] Part__Feature1407  label="Bloc 033"
  Placement = pos=(0,61.275,15.31) rot=(1,0,0;3.14159rad)
  shape: bbox 29.27 x 37.82 x 15.31 mm, 48 faces (baked)
FEATURE [Part::Feature] Part__Feature1408  label="Bloc 034"
  Placement = pos=(0,40.85,15.31) rot=(1,0,0;3.14159rad)
  shape: bbox 29.27 x 37.82 x 15.31 mm, 48 faces (baked)
FEATURE [Part::Feature] Part__Feature1409  label="Bloc 035"
  Placement = pos=(0,20.425,15.31) rot=(1,0,0;3.14159rad)
  shape: bbox 29.27 x 37.82 x 15.31 mm, 48 faces (baked)
FEATURE [Part::Feature] Part__Feature1411  label="Bloc 037"
  Placement = pos=(0,-71.3722,30.4377) rot=(1,0,0;2.42601rad)
  shape: bbox 29.27 x 32.23 x 36.36 mm, 30 faces (baked)
FEATURE [Part::Feature] Part__Feature1413  label="Bloc 039"
  Placement = pos=(0,-67.1486,30.5562) rot=(1,0,0;2.0944rad)
  shape: bbox 29.27 x 31.13 x 39.43 mm, 48 faces (baked)
FEATURE [Part::Feature] Part__Feature1416  label="Bloc 042"
  Placement = pos=(0,-56,19.3738) rot=(1,0,0;2.61799rad)
  shape: bbox 29.27 x 38.61 x 30.48 mm, 48 faces (baked)
FEATURE [Part::Feature] Part__Feature1417  label="Bloc 043"
  Placement = pos=(0,-9.2e-14,15.31) rot=(1,0,0;3.14159rad)
  shape: bbox 29.27 x 37.82 x 15.31 mm, 48 faces (baked)
FEATURE [Part::Feature] Part__Feature1418  label="Bloc 044"
  Placement = pos=(0,245.075,15.31) rot=(1,0,0;3.14159rad)
  shape: bbox 29.27 x 37.82 x 15.31 mm, 48 faces (baked)
FEATURE [Part::Feature] Part__Feature1419  label="Bloc 045"
  Placement = pos=(0,265.575,15.31) rot=(1,0,0;3.14159rad)
  shape: bbox 29.27 x 37.82 x 15.31 mm, 48 faces (baked)
FEATURE [Part::Feature] Part__Feature1420  label="Bloc 046"
  Placement = pos=(0,285.975,15.31) rot=(1,0,0;3.14159rad)
  shape: bbox 29.27 x 37.82 x 15.31 mm, 48 faces (baked)
FEATURE [Part::Feature] Part__Feature1421  label="Bloc 047"
  Placement = pos=(0,306.375,15.31) rot=(1,0,0;3.14159rad)
  shape: bbox 29.27 x 37.82 x 15.31 mm, 48 faces (baked)
FEATURE [Sketcher::SketchObject] Sketch
  MapMode = 5
  Placement = pos=(0,0,0) rot=(1,0,0;1.5708rad)
  Support = -> [XZ_Plane011]
  sketch-geometry (16):
    g0: LineSegment StartX=10 StartY=0 StartZ=0 EndX=40.8 EndY=0 EndZ=0
    g1: LineSegment StartX=50.8 StartY=10 StartZ=0 EndX=50.8 EndY=40.8 EndZ=0
    g2: LineSegment StartX=40.8 StartY=50.8 StartZ=0 EndX=10 EndY=50.8 EndZ=0
    g3: LineSegment StartX=0 StartY=40.8 StartZ=0 EndX=0 EndY=10 EndZ=0
    g4: ArcOfCircle CenterX=10 CenterY=40.8 CenterZ=0 NormalX=0 NormalY=0 NormalZ=1 AngleXU=0 Radius=10 StartAngle=1.5708 EndAngle=3.14159
    g5: ArcOfCircle CenterX=10 CenterY=10 CenterZ=0 NormalX=0 NormalY=0 NormalZ=1 AngleXU=0 Radius=10 StartAngle=3.14159 EndAngle=4.71239
    g6: ArcOfCircle CenterX=40.8 CenterY=10 CenterZ=0 NormalX=0 NormalY=0 NormalZ=1 AngleXU=0 Radius=10 StartAngle=4.71239 EndAngle=6.28319
    g7: ArcOfCircle CenterX=40.8 CenterY=40.8 CenterZ=0 NormalX=0 NormalY=0 NormalZ=1 AngleXU=0 Radius=10 StartAngle=3e-16 EndAngle=1.5708
    g8: LineSegment StartX=10 StartY=46.0375 StartZ=0 EndX=40.8 EndY=46.0375 EndZ=0
    g9: LineSegment StartX=46.0375 StartY=40.8 StartZ=0 EndX=46.0375 EndY=10 EndZ=0
    g10: LineSegment StartX=40.8 StartY=4.7625 StartZ=0 EndX=10 EndY=4.7625 EndZ=0
    g11: LineSegment StartX=4.7625 StartY=10 StartZ=0 EndX=4.7625 EndY=40.8 EndZ=0
    g12: ArcOfCircle CenterX=10 CenterY=40.8 CenterZ=0 NormalX=0 NormalY=0 NormalZ=1 AngleXU=0 Radius=5.2375 StartAngle=1.5708 EndAngle=3.14159
    g13: ArcOfCircle CenterX=10 CenterY=10 CenterZ=0 NormalX=0 NormalY=0 NormalZ=1 AngleXU=0 Radius=5.2375 StartAngle=3.14159 EndAngle=4.71239
    g14: ArcOfCircle CenterX=40.8 CenterY=10 CenterZ=0 NormalX=0 NormalY=0 NormalZ=1 AngleXU=0 Radius=5.2375 StartAngle=4.71239 EndAngle=6.28319
    g15: ArcOfCircle CenterX=40.8 CenterY=40.8 CenterZ=0 NormalX=0 NormalY=0 NormalZ=1 AngleXU=0 Radius=5.2375 StartAngle=0 EndAngle=1.5708
  constraints (36):
    c: Horizontal(g0)
    c: Horizontal(g2)
    c: Vertical(g1)
    c: Vertical(g3)
    c: Tangent(g2,g4) = -1.5708
    c: Tangent(g3,g4) = -1.5708
    c: Tangent(g3,g5) = -1.5708
    c: Tangent(g0,g5) = -1.5708
    c: Tangent(g0,g6) = -1.5708
    c: Tangent(g1,g6) = -1.5708
    c: Tangent(g2,g7) = -1.5708
    c: Tangent(g1,g7) = -1.5708
    c: Horizontal(g8)
    c: Horizontal(g10)
    c: Vertical(g9)
    c: Tangent(g8,g12) = 1.5708
    c: Tangent(g11,g12) = 1.5708
    c: Tangent(g11,g13) = 1.5708
    c: Tangent(g10,g13) = 1.5708
    c: Tangent(g9,g14) = 1.5708
    c: Tangent(g10,g14) = 1.5708
    c: Tangent(g8,g15) = 1.5708
    c: Tangent(g9,g15) = 1.5708
    c: PointOnObject(g3,g-2)
    c: PointOnObject(g0,g-1)
    c: DistanceX(g3,g1) = 50.8
    c: DistanceY(g0,g2) = 50.8
    c: Coincident(g13,g5)
    c: Coincident(g12,g4)
    c: Coincident(g7,g15)
    c: Coincident(g14,g6)
    c: Equal(g5,g4)
    c: Equal(g4,g7)
    c: Equal(g7,g6)
    c: DistanceX(g3,g11) = 4.7625
    c: DistanceX(g3,g0) = 10
FEATURE [PartDesign::Pad] Pad
  AllowMultiFace = false
  Length = 355.6
  Length2 = 100
  Midplane = true
  Placement = pos=(0,0,0) rot=(1,0,0;1.5708rad)
  Profile = -> Sketch
  Type = 0
FEATURE [Sketcher::SketchObject] Sketch001
  MapMode = 5
  sketch-geometry (16):
    g0: LineSegment StartX=10 StartY=0 StartZ=0 EndX=40.8 EndY=0 EndZ=0
    g1: LineSegment StartX=50.8 StartY=10 StartZ=0 EndX=50.8 EndY=40.8 EndZ=0
    g2: LineSegment StartX=40.8 StartY=50.8 StartZ=0 EndX=10 EndY=50.8 EndZ=0
    g3: LineSegment StartX=0 StartY=40.8 StartZ=0 EndX=0 EndY=10 EndZ=0
    g4: ArcOfCircle CenterX=10 CenterY=40.8 CenterZ=0 NormalX=0 NormalY=0 NormalZ=1 AngleXU=0 Radius=10 StartAngle=1.5708 EndAngle=3.14159
    g5: ArcOfCircle CenterX=10 CenterY=10 CenterZ=0 NormalX=0 NormalY=0 NormalZ=1 AngleXU=0 Radius=10 StartAngle=3.14159 EndAngle=4.71239
    g6: ArcOfCircle CenterX=40.8 CenterY=10 CenterZ=0 NormalX=0 NormalY=0 NormalZ=1 AngleXU=0 Radius=10 StartAngle=4.71239 EndAngle=6.28319
    g7: ArcOfCircle CenterX=40.8 CenterY=40.8 CenterZ=0 NormalX=0 NormalY=0 NormalZ=1 AngleXU=0 Radius=10 StartAngle=0 EndAngle=1.5708
    g8: LineSegment StartX=10 StartY=46.0375 StartZ=0 EndX=40.8 EndY=46.0375 EndZ=0
    g9: LineSegment StartX=46.0375 StartY=40.8 StartZ=0 EndX=46.0375 EndY=10 EndZ=0
    g10: LineSegment StartX=40.8 StartY=4.7625 StartZ=0 EndX=10 EndY=4.7625 EndZ=0
    g11: LineSegment StartX=4.7625 StartY=10 StartZ=0 EndX=4.7625 EndY=40.8 EndZ=0
    g12: ArcOfCircle CenterX=10 CenterY=40.8 CenterZ=0 NormalX=0 NormalY=0 NormalZ=1 AngleXU=0 Radius=5.2375 StartAngle=1.5708 EndAngle=3.14159
    g13: ArcOfCircle CenterX=10 CenterY=10 CenterZ=0 NormalX=0 NormalY=0 NormalZ=1 AngleXU=0 Radius=5.2375 StartAngle=3.14159 EndAngle=4.71239
    g14: ArcOfCircle CenterX=40.8 CenterY=10 CenterZ=0 NormalX=0 NormalY=0 NormalZ=1 AngleXU=0 Radius=5.2375 StartAngle=4.71239 EndAngle=6.28319
    g15: ArcOfCircle CenterX=40.8 CenterY=40.8 CenterZ=0 NormalX=0 NormalY=0 NormalZ=1 AngleXU=0 Radius=5.2375 StartAngle=4e-16 EndAngle=1.5708
  constraints (36):
    c: Horizontal(g0)
    c: Horizontal(g2)
    c: Vertical(g1)
    c: Vertical(g3)
    c: Tangent(g2,g4) = -1.5708
    c: Tangent(g3,g4) = -1.5708
    c: Tangent(g3,g5) = -1.5708
    c: Tangent(g0,g5) = -1.5708
    c: Tangent(g0,g6) = -1.5708
    c: Tangent(g1,g6) = -1.5708
    c: Tangent(g2,g7) = -1.5708
    c: Tangent(g1,g7) = -1.5708
    c: Horizontal(g8)
    c: Horizontal(g10)
    c: Vertical(g9)
    c: Tangent(g8,g12) = 1.5708
    c: Tangent(g11,g12) = 1.5708
    c: Tangent(g11,g13) = 1.5708
    c: Tangent(g10,g13) = 1.5708
    c: Tangent(g9,g14) = 1.5708
    c: Tangent(g10,g14) = 1.5708
    c: Tangent(g8,g15) = 1.5708
    c: Tangent(g9,g15) = 1.5708
    c: PointOnObject(g3,g-2)
    c: PointOnObject(g0,g-1)
    c: DistanceX(g3,g1) = 50.8
    c: DistanceY(g0,g2) = 50.8
    c: Coincident(g13,g5)
    c: Coincident(g12,g4)
    c: Coincident(g7,g15)
    c: Coincident(g14,g6)
    c: Equal(g5,g4)
    c: Equal(g4,g7)
    c: Equal(g7,g6)
    c: DistanceX(g3,g0) = 10
    c: DistanceX(g9,g1) = 4.7625
FEATURE [PartDesign::Pad] Pad001
  AllowMultiFace = false
  Length = 398.4
  Length2 = 100
  Profile = -> Sketch001
  Type = 0
FEATURE [PartDesign::Body] Body001
  Group = -> [Sketch001,Pad001]
  Tip = -> Pad001
FEATURE [App::Part] Part005  label="right_member"
  Group = -> [Body001]
  Origin = -> Origin006
  Placement = pos=(0,127,50.8) rot=(0,0,1;0rad)
FEATURE [Sketcher::SketchObject] Sketch002
  MapMode = 5
  Support = -> [XY_Plane005]
  sketch-geometry (4):
    g0: LineSegment StartX=-150 StartY=150 StartZ=0 EndX=150 EndY=150 EndZ=0
    g1: LineSegment StartX=150 StartY=150 StartZ=0 EndX=150 EndY=-150 EndZ=0
    g2: LineSegment StartX=150 StartY=-150 StartZ=0 EndX=-150 EndY=-150 EndZ=0
    g3: LineSegment StartX=-150 StartY=-150 StartZ=0 EndX=-150 EndY=150 EndZ=0
  constraints (12):
    c: Coincident(g0,g1)
    c: Coincident(g1,g2)
    c: Coincident(g2,g3)
    c: Coincident(g3,g0)
    c: Horizontal(g0)
    c: Horizontal(g2)
    c: Vertical(g1)
    c: Vertical(g3)
    c: DistanceX(g0,g0) = 300
    c: DistanceY(g3,g3) = 300
    c: DistanceY(g-1,g0) = 150
    c: DistanceX(g-1,g0) = 150
FEATURE [PartDesign::Pad] Pad007
  AllowMultiFace = false
  Length = 3
  Length2 = 100
  Profile = -> Sketch002
  Type = 0
  expr: Length = 3mm
FEATURE [PartDesign::Body] Body002
  Group = -> [Sketch002,Pad007]
  Origin = -> Origin005
  Tip = -> Pad007
FEATURE [App::Part] Part010  label="mirror_plate"
  Group = -> [Body002]
  Origin = -> Origin014
  Placement = pos=(0,0,6.35) rot=(0,0,1;0rad)
FEATURE [Sketcher::SketchObject] Sketch003
  MapMode = 5
  Placement = pos=(0,0,0) rot=(1,0,0;1.5708rad)
  Support = -> [XZ_Plane019]
  sketch-geometry (4):
    g0: LineSegment StartX=-19.05 StartY=0 StartZ=0 EndX=19.05 EndY=0 EndZ=0
    g1: LineSegment StartX=19.05 StartY=0 StartZ=0 EndX=19.05 EndY=-4.7625 EndZ=0
    g2: LineSegment StartX=19.05 StartY=-4.7625 StartZ=0 EndX=-19.05 EndY=-4.7625 EndZ=0
    g3: LineSegment StartX=-19.05 StartY=-4.7625 StartZ=0 EndX=-19.05 EndY=0 EndZ=0
  constraints (12):
    c: Coincident(g0,g1)
    c: Coincident(g1,g2)
    c: Coincident(g2,g3)
    c: Coincident(g3,g0)
    c: Horizontal(g0)
    c: Horizontal(g2)
    c: Vertical(g1)
    c: Vertical(g3)
    c: PointOnObject(g0,g-1)
    c: DistanceX(g0,g0) = 38.1
    c: DistanceX(g-1,g0) = 19.05
    c: DistanceY(g1,g1) = 4.7625
FEATURE [PartDesign::AdditivePipe] AdditivePipe
  AllowMultiFace = false
  AuxilleryCurvelinear = true
  AuxillerySpineTangent = false
  Binormal = (0,0,0)
  Mode = 2
  Placement = pos=(0,0,0) rot=(1,0,0;1.5708rad)
  Profile = -> Sketch003
  Spine = -> Sketch015 [Edge1,Edge2,Edge3,Edge4,Edge5]
  SpineTangent = false
  Transformation = 0
  Transition = 0
FEATURE [PartDesign::Pocket] Pocket007
  AllowMultiFace = false
  BaseFeature = -> AdditivePipe
  Length = 5
  Length2 = 100
  Placement = pos=(0,0,0) rot=(1,0,0;1.5708rad)
  Profile = -> Sketch016
  Type = 1
FEATURE [PartDesign::Chamfer] Chamfer
  Angle = 45
  Base = -> Pocket007 [Edge14,Edge20,Edge19]
  BaseFeature = -> Pocket007
  ChamferType = 0
  FlipDirection = false
  Placement = pos=(0,0,0) rot=(1,0,0;1.5708rad)
  Size = 4.1
  Size2 = 1
  SupportTransform = true
FEATURE [PartDesign::Pocket] Pocket008
  BaseFeature = -> Chamfer
  Length = 5
  Length2 = 100
  Placement = pos=(0,0,0) rot=(1,0,0;1.5708rad)
  Profile = -> Sketch017
  Type = 1
FEATURE [PartDesign::Fillet] Fillet
  Base = -> Pocket008 [Edge5,Edge27,Edge70,Edge71]
  BaseFeature = -> Pocket008
  Placement = pos=(0,0,0) rot=(1,0,0;1.5708rad)
  Radius = 4
  SupportTransform = true
FEATURE [PartDesign::Body] Body003
  Group = -> [Sketch003,Sketch015,AdditivePipe,Sketch016,Pocket007,Chamfer,Sketch017,Pocket008,Fillet]
  Origin = -> Origin019
  Tip = -> Fillet
FEATURE [App::Part] Part013  label="bed_holder_bracket"
  Group = -> [Body003]
  Origin = -> Origin018
  Placement = pos=(0,-17,-12) rot=(0,0,1;0rad)
FEATURE [App::Part] Part011  label="adj_assy"
  Group = -> [Part012,Cylinder002,Part013]
  Origin = -> Origin015
  Placement = pos=(153,0,0) rot=(0,0,1;1.5708rad)
FEATURE [Sketcher::SketchObject] Sketch004
  MapMode = 5
  sketch-geometry (16):
    g0: LineSegment StartX=10 StartY=0 StartZ=0 EndX=40.8 EndY=0 EndZ=0
    g1: LineSegment StartX=50.8 StartY=10 StartZ=0 EndX=50.8 EndY=40.8 EndZ=0
    g2: LineSegment StartX=40.8 StartY=50.8 StartZ=0 EndX=10 EndY=50.8 EndZ=0
    g3: LineSegment StartX=0 StartY=40.8 StartZ=0 EndX=0 EndY=10 EndZ=0
    g4: ArcOfCircle CenterX=10 CenterY=40.8 CenterZ=0 NormalX=0 NormalY=0 NormalZ=1 AngleXU=0 Radius=10 StartAngle=1.5708 EndAngle=3.14159
    g5: ArcOfCircle CenterX=10 CenterY=10 CenterZ=0 NormalX=0 NormalY=0 NormalZ=1 AngleXU=0 Radius=10 StartAngle=3.14159 EndAngle=4.71239
    g6: ArcOfCircle CenterX=40.8 CenterY=10 CenterZ=0 NormalX=0 NormalY=0 NormalZ=1 AngleXU=0 Radius=10 StartAngle=4.71239 EndAngle=6.28319
    g7: ArcOfCircle CenterX=40.8 CenterY=40.8 CenterZ=0 NormalX=0 NormalY=0 NormalZ=1 AngleXU=0 Radius=10 StartAngle=0 EndAngle=1.5708
    g8: LineSegment StartX=10 StartY=46.0375 StartZ=0 EndX=40.8 EndY=46.0375 EndZ=0
    g9: LineSegment StartX=46.0375 StartY=40.8 StartZ=0 EndX=46.0375 EndY=10 EndZ=0
    g10: LineSegment StartX=40.8 StartY=4.7625 StartZ=0 EndX=10 EndY=4.7625 EndZ=0
    g11: LineSegment StartX=4.7625 StartY=10 StartZ=0 EndX=4.7625 EndY=40.8 EndZ=0
    g12: ArcOfCircle CenterX=10 CenterY=40.8 CenterZ=0 NormalX=0 NormalY=0 NormalZ=1 AngleXU=0 Radius=5.2375 StartAngle=1.5708 EndAngle=3.14159
    g13: ArcOfCircle CenterX=10 CenterY=10 CenterZ=0 NormalX=0 NormalY=0 NormalZ=1 AngleXU=0 Radius=5.2375 StartAngle=3.14159 EndAngle=4.71239
    g14: ArcOfCircle CenterX=40.8 CenterY=10 CenterZ=0 NormalX=0 NormalY=0 NormalZ=1 AngleXU=0 Radius=5.2375 StartAngle=4.71239 EndAngle=6.28319
    g15: ArcOfCircle CenterX=40.8 CenterY=40.8 CenterZ=0 NormalX=0 NormalY=0 NormalZ=1 AngleXU=0 Radius=5.2375 StartAngle=4e-16 EndAngle=1.5708
  constraints (36):
    c: Horizontal(g0)
    c: Horizontal(g2)
    c: Vertical(g1)
    c: Vertical(g3)
    c: Tangent(g2,g4) = -1.5708
    c: Tangent(g3,g4) = -1.5708
    c: Tangent(g3,g5) = -1.5708
    c: Tangent(g0,g5) = -1.5708
    c: Tangent(g0,g6) = -1.5708
    c: Tangent(g1,g6) = -1.5708
    c: Tangent(g2,g7) = -1.5708
    c: Tangent(g1,g7) = -1.5708
    c: Horizontal(g8)
    c: Horizontal(g10)
    c: Vertical(g9)
    c: Tangent(g8,g12) = 1.5708
    c: Tangent(g11,g12) = 1.5708
    c: Tangent(g11,g13) = 1.5708
    c: Tangent(g10,g13) = 1.5708
    c: Tangent(g9,g14) = 1.5708
    c: Tangent(g10,g14) = 1.5708
    c: Tangent(g8,g15) = 1.5708
    c: Tangent(g9,g15) = 1.5708
    c: PointOnObject(g3,g-2)
    c: PointOnObject(g0,g-1)
    c: DistanceX(g3,g1) = 50.8
    c: DistanceY(g0,g2) = 50.8
    c: Coincident(g13,g5)
    c: Coincident(g12,g4)
    c: Coincident(g7,g15)
    c: Coincident(g14,g6)
    c: Equal(g5,g4)
    c: Equal(g4,g7)
    c: Equal(g7,g6)
    c: DistanceX(g3,g0) = 10
    c: DistanceX(g9,g1) = 4.7625
FEATURE [PartDesign::Pad] Pad004
  AllowMultiFace = false
  Length = 398.4
  Length2 = 100
  Profile = -> Sketch004
  Type = 0
FEATURE [PartDesign::Body] Body004
  Group = -> [Sketch004,Pad004]
  Tip = -> Pad004
FEATURE [App::Part] Part006  label="left_member"
  Group = -> [Body004]
  Origin = -> Origin007
  Placement = pos=(0,-177.8,50.8) rot=(0,0,1;0rad)
FEATURE [App::DocumentObjectGroup] Group  label="vertical_members"
  Group = -> [Part005,Part006]
FEATURE [Sketcher::SketchObject] Sketch005
  AttachmentOffset = pos=(0,0,50.8) rot=(0,0,1;0rad)
  MapMode = 5
  Placement = pos=(0,0,50.8) rot=(0,0,1;0rad)
  Support = -> [XY_Plane011]
  sketch-geometry (8):
    g0: LineSegment StartX=32.8 StartY=89.25 StartZ=0 EndX=57.8 EndY=89.25 EndZ=0
    g1: LineSegment StartX=57.8 StartY=89.25 StartZ=0 EndX=57.8 EndY=109.25 EndZ=0
    g2: LineSegment StartX=57.8 StartY=109.25 StartZ=0 EndX=32.8 EndY=109.25 EndZ=0
    g3: LineSegment StartX=32.8 StartY=109.25 StartZ=0 EndX=32.8 EndY=89.25 EndZ=0
    g4: LineSegment StartX=32.8 StartY=-89.25 StartZ=0 EndX=57.8 EndY=-89.25 EndZ=0
    g5: LineSegment StartX=57.8 StartY=-89.25 StartZ=0 EndX=57.8 EndY=-109.25 EndZ=0
    g6: LineSegment StartX=57.8 StartY=-109.25 StartZ=0 EndX=32.8 EndY=-109.25 EndZ=0
    g7: LineSegment StartX=32.8 StartY=-109.25 StartZ=0 EndX=32.8 EndY=-89.25 EndZ=0
  constraints (22):
    c: Coincident(g0,g1)
    c: Coincident(g1,g2)
    c: Coincident(g2,g3)
    c: Coincident(g3,g0)
    c: Horizontal(g0)
    c: Horizontal(g2)
    c: Vertical(g1)
    c: Vertical(g3)
    c: Coincident(g4,g5)
    c: Coincident(g5,g6)
    c: Coincident(g6,g7)
    c: Coincident(g7,g4)
    c: Horizontal(g4)
    c: Horizontal(g6)
    c: Vertical(g5)
    c: Vertical(g7)
    c: Symmetric(g0,g4,g-1)
    c: Symmetric(g1,g5,g-1)
    c: DistanceY(g1,g1) = 20
    c: DistanceX(g-1,g0) = 32.8
    c: DistanceX(g0,g0) = 25
    c: DistanceY(g4,g0) = 178.5
FEATURE [PartDesign::Pocket] Pocket
  AllowMultiFace = false
  BaseFeature = -> Pad
  Length = 5
  Length2 = 100
  Placement = pos=(0,0,0) rot=(1,0,0;1.5708rad)
  Profile = -> Sketch005
  Type = 1
FEATURE [PartDesign::Pocket] Pocket001
  AllowMultiFace = false
  BaseFeature = -> Pocket
  Length = 5
  Length2 = 100
  Placement = pos=(0,0,0) rot=(1,0,0;1.5708rad)
  Profile = -> Sketch006
  Type = 2
FEATURE [PartDesign::Pocket] Pocket006
  AllowMultiFace = false
  BaseFeature = -> Pocket001
  Length = 5
  Length2 = 100
  Placement = pos=(0,0,0) rot=(1,0,0;1.5708rad)
  Profile = -> Sketch012
  Type = 0
FEATURE [PartDesign::Body] Body
  Group = -> [Sketch,Pad,Sketch005,Pocket,Sketch006,Pocket001,Sketch012,Pocket006]
  Origin = -> Origin011
  Tip = -> Pocket006
FEATURE [App::Part] Part008  label="bottom_member"
  Group = -> [Body]
  Origin = -> Origin009
FEATURE [Sketcher::SketchObject] Sketch007
  AttachmentOffset = pos=(0,0,50.8) rot=(0,0,1;0rad)
  MapMode = 5
  Placement = pos=(0,0,50.8) rot=(0,0,1;0rad)
  Support = -> [XY_Plane010]
  sketch-geometry (8):
    g0: LineSegment StartX=32.8 StartY=89.25 StartZ=0 EndX=57.8 EndY=89.25 EndZ=0
    g1: LineSegment StartX=57.8 StartY=89.25 StartZ=0 EndX=57.8 EndY=113.05 EndZ=0
    g2: LineSegment StartX=57.8 StartY=113.05 StartZ=0 EndX=32.8 EndY=113.05 EndZ=0
    g3: LineSegment StartX=32.8 StartY=113.05 StartZ=0 EndX=32.8 EndY=89.25 EndZ=0
    g4: LineSegment StartX=32.8 StartY=-89.25 StartZ=0 EndX=57.8 EndY=-89.25 EndZ=0
    g5: LineSegment StartX=57.8 StartY=-89.25 StartZ=0 EndX=57.8 EndY=-113.05 EndZ=0
    g6: LineSegment StartX=57.8 StartY=-113.05 StartZ=0 EndX=32.8 EndY=-113.05 EndZ=0
    g7: LineSegment StartX=32.8 StartY=-113.05 StartZ=0 EndX=32.8 EndY=-89.25 EndZ=0
  constraints (22):
    c: Coincident(g0,g1)
    c: Coincident(g1,g2)
    c: Coincident(g2,g3)
    c: Coincident(g3,g0)
    c: Horizontal(g0)
    c: Horizontal(g2)
    c: Vertical(g1)
    c: Vertical(g3)
    c: Coincident(g4,g5)
    c: Coincident(g5,g6)
    c: Coincident(g6,g7)
    c: Coincident(g7,g4)
    c: Horizontal(g4)
    c: Horizontal(g6)
    c: Vertical(g5)
    c: Vertical(g7)
    c: Symmetric(g0,g4,g-1)
    c: Symmetric(g1,g5,g-1)
    c: DistanceY(g1,g1) = 23.8
    c: DistanceX(g-1,g0) = 32.8
    c: DistanceX(g0,g0) = 25
    c: DistanceY(g4,g0) = 178.5
FEATURE [Sketcher::SketchObject] Sketch008
  MapMode = 5
  Placement = pos=(0,0,0) rot=(1,0,0;1.5708rad)
  Support = -> [XZ_Plane008]
  sketch-geometry (16):
    g0: LineSegment StartX=10 StartY=1.8e-15 StartZ=0 EndX=40.8 EndY=1.8e-15 EndZ=0
    g1: LineSegment StartX=50.8 StartY=10 StartZ=0 EndX=50.8 EndY=40.8 EndZ=0
    g2: LineSegment StartX=40.8 StartY=50.8 StartZ=0 EndX=10 EndY=50.8 EndZ=0
    g3: LineSegment StartX=0 StartY=40.8 StartZ=0 EndX=0 EndY=10 EndZ=0
    g4: ArcOfCircle CenterX=10 CenterY=40.8 CenterZ=0 NormalX=0 NormalY=0 NormalZ=1 AngleXU=0 Radius=10 StartAngle=1.5708 EndAngle=3.14159
    g5: ArcOfCircle CenterX=10 CenterY=10 CenterZ=0 NormalX=0 NormalY=0 NormalZ=1 AngleXU=0 Radius=10 StartAngle=3.14159 EndAngle=4.71239
    g6: ArcOfCircle CenterX=40.8 CenterY=10 CenterZ=0 NormalX=0 NormalY=0 NormalZ=1 AngleXU=0 Radius=10 StartAngle=4.71239 EndAngle=6.28319
    g7: ArcOfCircle CenterX=40.8 CenterY=40.8 CenterZ=0 NormalX=0 NormalY=0 NormalZ=1 AngleXU=0 Radius=10 StartAngle=3e-16 EndAngle=1.5708
    g8: LineSegment StartX=10 StartY=46.0375 StartZ=0 EndX=40.8 EndY=46.0375 EndZ=0
    g9: LineSegment StartX=46.0375 StartY=40.8 StartZ=0 EndX=46.0375 EndY=10 EndZ=0
    g10: LineSegment StartX=40.8 StartY=4.7625 StartZ=0 EndX=10 EndY=4.7625 EndZ=0
    g11: LineSegment StartX=4.7625 StartY=10 StartZ=0 EndX=4.7625 EndY=40.8 EndZ=0
    g12: ArcOfCircle CenterX=10 CenterY=40.8 CenterZ=0 NormalX=0 NormalY=0 NormalZ=1 AngleXU=0 Radius=5.2375 StartAngle=1.5708 EndAngle=3.14159
    g13: ArcOfCircle CenterX=10 CenterY=10 CenterZ=0 NormalX=0 NormalY=0 NormalZ=1 AngleXU=0 Radius=5.2375 StartAngle=3.14159 EndAngle=4.71239
    g14: ArcOfCircle CenterX=40.8 CenterY=10 CenterZ=0 NormalX=0 NormalY=0 NormalZ=1 AngleXU=0 Radius=5.2375 StartAngle=4.71239 EndAngle=6.28319
    g15: ArcOfCircle CenterX=40.8 CenterY=40.8 CenterZ=0 NormalX=0 NormalY=0 NormalZ=1 AngleXU=0 Radius=5.2375 StartAngle=0 EndAngle=1.5708
  constraints (36):
    c: Horizontal(g0)
    c: Horizontal(g2)
    c: Vertical(g1)
    c: Vertical(g3)
    c: Tangent(g2,g4) = -1.5708
    c: Tangent(g3,g4) = -1.5708
    c: Tangent(g3,g5) = -1.5708
    c: Tangent(g0,g5) = -1.5708
    c: Tangent(g0,g6) = -1.5708
    c: Tangent(g1,g6) = -1.5708
    c: Tangent(g2,g7) = -1.5708
    c: Tangent(g1,g7) = -1.5708
    c: Horizontal(g8)
    c: Horizontal(g10)
    c: Vertical(g9)
    c: Tangent(g8,g12) = 1.5708
    c: Tangent(g11,g12) = 1.5708
    c: Tangent(g11,g13) = 1.5708
    c: Tangent(g10,g13) = 1.5708
    c: Tangent(g9,g14) = 1.5708
    c: Tangent(g10,g14) = 1.5708
    c: Tangent(g8,g15) = 1.5708
    c: Tangent(g9,g15) = 1.5708
    c: PointOnObject(g3,g-2)
    c: PointOnObject(g0,g-1)
    c: DistanceX(g3,g1) = 50.8
    c: DistanceY(g0,g2) = 50.8
    c: Coincident(g13,g5)
    c: Coincident(g12,g4)
    c: Coincident(g7,g15)
    c: Coincident(g14,g6)
    c: Equal(g5,g4)
    c: Equal(g4,g7)
    c: Equal(g7,g6)
    c: DistanceX(g3,g11) = 4.7625
    c: DistanceX(g3,g0) = 10
FEATURE [PartDesign::Pad] Pad005
  AllowMultiFace = false
  Length = 355.6
  Length2 = 100
  Midplane = true
  Placement = pos=(0,0,0) rot=(1,0,0;1.5708rad)
  Profile = -> Sketch008
  Type = 0
FEATURE [PartDesign::Pocket] Pocket002
  AllowMultiFace = false
  BaseFeature = -> Pad005
  Length = 5
  Length2 = 100
  Placement = pos=(0,0,0) rot=(1,0,0;1.5708rad)
  Profile = -> Sketch007
  Type = 1
FEATURE [Sketcher::SketchObject] Sketch009
  AttachmentOffset = pos=(0,0,50.8) rot=(0,0,1;0rad)
  MapMode = 5
  Placement = pos=(50.8,-1.13e-14,1.13e-14) rot=(0.57735,0.57735,0.57735;2.0944rad)
  Support = -> [YZ_Plane008]
  sketch-geometry (8):
    g0: ArcOfCircle CenterX=-131 CenterY=25.4 CenterZ=0 NormalX=0 NormalY=0 NormalZ=1 AngleXU=0 Radius=5 StartAngle=1.5708 EndAngle=4.71239
    g1: ArcOfCircle CenterX=-95 CenterY=25.4 CenterZ=0 NormalX=0 NormalY=0 NormalZ=1 AngleXU=0 Radius=5 StartAngle=4.71239 EndAngle=7.85398
    g2: LineSegment StartX=-131 StartY=20.4 StartZ=0 EndX=-95 EndY=20.4 EndZ=0
    g3: LineSegment StartX=-131 StartY=30.4 StartZ=0 EndX=-95 EndY=30.4 EndZ=0
    g4: ArcOfCircle CenterX=95 CenterY=25.4 CenterZ=0 NormalX=0 NormalY=0 NormalZ=1 AngleXU=0 Radius=5 StartAngle=1.5708 EndAngle=4.71239
    g5: ArcOfCircle CenterX=131 CenterY=25.4 CenterZ=0 NormalX=0 NormalY=0 NormalZ=1 AngleXU=0 Radius=5 StartAngle=4.71239 EndAngle=7.85398
    g6: LineSegment StartX=95 StartY=20.4 StartZ=0 EndX=131 EndY=20.4 EndZ=0
    g7: LineSegment StartX=95 StartY=30.4 StartZ=0 EndX=131 EndY=30.4 EndZ=0
  constraints (18):
    c: Tangent(g0,g3) = 1.5708
    c: Tangent(g0,g2) = -1.5708
    c: Tangent(g2,g1) = -1.5708
    c: Tangent(g3,g1) = 1.5708
    c: Horizontal(g2)
    c: Equal(g0,g1)
    c: Tangent(g4,g7) = 1.5708
    c: Tangent(g4,g6) = -1.5708
    c: Tangent(g6,g5) = -1.5708
    c: Tangent(g7,g5) = 1.5708
    c: Horizontal(g6)
    c: Symmetric(g4,g1,g-2)
    c: Equal(g4,g1)
    c: Symmetric(g5,g0,g-2)
    c: Diameter(g1) = 10
    c: DistanceY(g-1,g4) = 25.4
    c: DistanceX(g0,g5) = 262
    c: DistanceX(g1,g4) = 190
FEATURE [PartDesign::Pocket] Pocket003
  AllowMultiFace = false
  BaseFeature = -> Pocket002
  Length = 5
  Length2 = 100
  Placement = pos=(0,0,0) rot=(1,0,0;1.5708rad)
  Profile = -> Sketch009
  Type = 2
FEATURE [PartDesign::Pocket] Pocket004
  AllowMultiFace = false
  BaseFeature = -> Pocket003
  Length = 5
  Length2 = 100
  Placement = pos=(0,0,0) rot=(1,0,0;1.5708rad)
  Profile = -> Sketch010
  Type = 2
FEATURE [PartDesign::Pocket] Pocket005
  AllowMultiFace = false
  BaseFeature = -> Pocket004
  Length = 35
  Length2 = 100
  Placement = pos=(0,0,0) rot=(1,0,0;1.5708rad)
  Profile = -> Sketch011
  Reversed = true
  Type = 0
FEATURE [PartDesign::Body] Body005
  Group = -> [Sketch008,Pad005,Sketch007,Pocket002,Sketch009,Pocket003,Sketch010,Pocket004,Sketch011,Pocket005]
  Origin = -> Origin010
  Tip = -> Pocket005
FEATURE [App::Part] Part007  label="top_member"
  Group = -> [Body005]
  Origin = -> Origin008
  Placement = pos=(0,0,449.2) rot=(0,0,1;0rad)
FEATURE [App::DocumentObjectGroup] Group001  label="horizontal_members"
  Group = -> [Part007,Part008]
FEATURE [App::Part] Part004  label="fabricated_tubular_frame"
  Group = -> [Group,Part005,Part006,Group001,Part007,Part008]
  Origin = -> Origin004
FEATURE [Part::Feature] Part__Feature1422  label="PCB Geometry"
  shape: bbox 22.38 x 4.47 x 1 mm, 24 faces, 4 solids (baked)
FEATURE [Part::Feature] Part__Feature1423  label="PCB^Endstop"
  Placement = pos=(0,0,0) rot=(1,0,0;3.14159rad)
  shape: bbox 39.5 x 16 x 1 mm, 14 faces (baked)
FEATURE [App::Part] PCB
  Group = -> [Part__Feature1422,Part__Feature1423]
  Origin = -> Origin089
FEATURE [Part::Feature] Part__Feature1424  label="Microswitch_1A_125vAC(seul)"
  Placement = pos=(-5.94334,8,-4) rot=(0.707107,0.707107,0;3.14159rad)
  shape: bbox 16.44 x 11.12 x 8 mm, 100 faces, 5 solids (baked)
FEATURE [Part::Feature] Part__Feature1425  label="JST 4Pin"
  Placement = pos=(10.68,0.36,-3.97) rot=(0.707107,0.707107,0;3.14159rad)
  shape: bbox 8.748 x 12.4 x 6.1 mm, 158 faces, 5 solids (baked)
FEATURE [App::Part] Endstop
  Group = -> [PCB,Part__Feature1424,Part__Feature1425]
  Origin = -> Origin090
FEATURE [App::Part] Endstop2  label="makerbot_endstop"
  Group = -> [Endstop]
  Origin = -> Origin091
  Placement = pos=(-215,24.8,28) rot=(-0.707107,-0.707107,0;3.14159rad)
FEATURE [App::Link] Link023  label="makerbot_endstop001"
  LinkPlacement = pos=(226.2,-27.7,28.9) rot=(-0.707107,0.707107,0;3.14159rad)
  LinkedObject = -> Endstop2
  Placement = pos=(226.2,-27.7,28.9) rot=(-0.707107,0.707107,0;3.14159rad)
FEATURE [Part::Feature] Part__Feature1426  label="Bloc 048"
  Placement = pos=(0,325.958,21.7429) rot=(1,0,0;3.1765rad)
  shape: bbox 29.27 x 38.26 x 16.55 mm, 48 faces (baked)
FEATURE [Part::Feature] Part__Feature1427  label="Bloc 049"
  Placement = pos=(0,345.753,23.104) rot=(1,0,0;3.24631rad)
  shape: bbox 29.27 x 39 x 18.96 mm, 48 faces (baked)
FEATURE [Part::Feature] Part__Feature1428  label="Bloc 050"
  Placement = pos=(0,363.478,27.336) rot=(1,0,0;3.50811rad)
  shape: bbox 29.27 x 40.09 x 27.1 mm, 48 faces (baked)
FEATURE [Part::Feature] Part__Feature1429  label="Bloc 051"
  Placement = pos=(0,375.716,36.5883) rot=(1,0,0;4.06662rad)
  shape: bbox 29.27 x 33.43 x 37.76 mm, 48 faces (baked)
FEATURE [Part::Feature] Part__Feature1430  label="Bloc 052"
  Placement = pos=(0,381.03,50.8811) rot=(-1,0,0;1.64061rad)
  shape: bbox 29.27 x 17.3 x 38.14 mm, 48 faces (baked)
FEATURE [Part::Feature] Part__Feature1431  label="Bloc 053"
  Placement = pos=(0,378.423,67.1087) rot=(-1,0,0;1.18682rad)
  shape: bbox 29.27 x 27.58 x 40.07 mm, 48 faces (baked)
FEATURE [Part::Feature] Part__Feature1432  label="Bloc 054"
  Placement = pos=(0,368.979,79.0772) rot=(-1,0,0;0.610865rad)
  shape: bbox 29.27 x 38.06 x 32.63 mm, 48 faces (baked)
FEATURE [App::Link] Link024  label="makerbot_endstop002"
  LinkPlacement = pos=(26.9,180.4,64) rot=(1,0,0;1.5708rad)
  LinkedObject = -> Endstop2
  Placement = pos=(26.9,180.4,64) rot=(1,0,0;1.5708rad)
FEATURE [App::Link] Link025  label="makerbot_endstop003"
  LinkPlacement = pos=(27.9,179.3,432.9) rot=(0,0.707107,-0.707107;3.14159rad)
  LinkedObject = -> Endstop2
  Placement = pos=(27.9,179.3,432.9) rot=(0,0.707107,-0.707107;3.14159rad)
FEATURE [Part::Feature] Part__Feature1433  label="Bloc 055"
  Placement = pos=(0,-20.4,15.31) rot=(1,0,0;3.14159rad)
  shape: bbox 29.27 x 37.82 x 15.31 mm, 48 faces (baked)
FEATURE [Part::Feature] Part__Feature1434  label="Bloc 056"
  Placement = pos=(0,-40.8,15.31) rot=(1,0,0;3.14159rad)
  shape: bbox 29.27 x 37.82 x 15.31 mm, 48 faces (baked)
FEATURE [Part::Feature] M5x25_Screw_Copy
  Placement = pos=(10,11,10) rot=(1,0,0;1.5708rad)
  shape: bbox 10 x 39.25 x 10 mm, 25 faces (baked)
FEATURE [App::Link] Link026  label="M5x25_Screw_Copy001"
  LinkPlacement = pos=(9.99999,11,-10) rot=(1,0,0;1.5708rad)
  LinkedObject = -> M5x25_Screw_Copy
  Placement = pos=(9.99999,11,-10) rot=(1,0,0;1.5708rad)
FEATURE [Part::FeaturePython] Screw  label="M5x10-Screw"  # Fasteners workbench fastener (typed FeaturePython)
  Placement = pos=(10,24,3.4) rot=(0,0,1;0rad)
  diameter = 3
  invert = false
  length = 1
  lengthCustom = 10
  matchOuter = false
  offset = 0
  thread = false
  type = 22
FEATURE [App::LinkElement] Link028_i0
  LinkPlacement = pos=(-10,24,3.4) rot=(0,0,1;0rad)
  LinkedObject = -> Screw
  Placement = pos=(-10,24,3.4) rot=(0,0,1;0rad)
FEATURE [App::LinkElement] Link028_i1
  LinkPlacement = pos=(-10,-24,3.4) rot=(0,0,1;0rad)
  LinkedObject = -> Screw
  Placement = pos=(-10,-24,3.4) rot=(0,0,1;0rad)
FEATURE [App::LinkElement] Link028_i2
  LinkPlacement = pos=(10,-24,3.4) rot=(0,0,1;0rad)
  LinkedObject = -> Screw
  Placement = pos=(10,-24,3.4) rot=(0,0,1;0rad)
FEATURE [App::LinkElement] Link028_i3
  LinkPlacement = pos=(110.5,34,3.4) rot=(0,0,1;0rad)
  LinkedObject = -> Screw
  Placement = pos=(110.5,34,3.4) rot=(0,0,1;0rad)
FEATURE [App::LinkElement] Link028_i4
  LinkPlacement = pos=(110.5,7.99995,3.4) rot=(0,0,1;0rad)
  LinkedObject = -> Screw
  Placement = pos=(110.5,7.99995,3.4) rot=(0,0,1;0rad)
FEATURE [App::LinkElement] Link028_i5
  LinkPlacement = pos=(110.5,-8,3.4) rot=(0,0,1;0rad)
  LinkedObject = -> Screw
  Placement = pos=(110.5,-8,3.4) rot=(0,0,1;0rad)
FEATURE [App::LinkElement] Link028_i6
  LinkPlacement = pos=(110.5,-34,3.4) rot=(0,0,1;0rad)
  LinkedObject = -> Screw
  Placement = pos=(110.5,-34,3.4) rot=(0,0,1;0rad)
FEATURE [App::LinkElement] Link028_i7
  LinkPlacement = pos=(80,34,3.4) rot=(0,0,1;0rad)
  LinkedObject = -> Screw
  Placement = pos=(80,34,3.4) rot=(0,0,1;0rad)
FEATURE [App::LinkElement] Link028_i8
  LinkPlacement = pos=(80,7.99995,3.4) rot=(0,0,1;0rad)
  LinkedObject = -> Screw
  Placement = pos=(80,7.99995,3.4) rot=(0,0,1;0rad)
FEATURE [App::LinkElement] Link028_i9
  LinkPlacement = pos=(80,-7.99999,3.4) rot=(0,0,1;0rad)
  LinkedObject = -> Screw
  Placement = pos=(80,-7.99999,3.4) rot=(0,0,1;0rad)
FEATURE [App::LinkElement] Link028_i10
  LinkPlacement = pos=(80,-34,3.4) rot=(0,0,1;0rad)
  LinkedObject = -> Screw
  Placement = pos=(80,-34,3.4) rot=(0,0,1;0rad)
FEATURE [App::LinkElement] Link028_i11
  LinkPlacement = pos=(-80,34,3.4) rot=(0,0,1;0rad)
  LinkedObject = -> Screw
  Placement = pos=(-80,34,3.4) rot=(0,0,1;0rad)
FEATURE [App::LinkElement] Link028_i12
  LinkPlacement = pos=(-80,7.99997,3.4) rot=(0,0,1;0rad)
  LinkedObject = -> Screw
  Placement = pos=(-80,7.99997,3.4) rot=(0,0,1;0rad)
FEATURE [App::LinkElement] Link028_i13
  LinkPlacement = pos=(-80,-7.99995,3.4) rot=(0,0,1;0rad)
  LinkedObject = -> Screw
  Placement = pos=(-80,-7.99995,3.4) rot=(0,0,1;0rad)
FEATURE [App::LinkElement] Link028_i14
  LinkPlacement = pos=(-80,-34,3.4) rot=(0,0,1;0rad)
  LinkedObject = -> Screw
  Placement = pos=(-80,-34,3.4) rot=(0,0,1;0rad)
FEATURE [App::LinkElement] Link028_i15
  LinkPlacement = pos=(-110.5,34,3.4) rot=(0,0,1;0rad)
  LinkedObject = -> Screw
  Placement = pos=(-110.5,34,3.4) rot=(0,0,1;0rad)
FEATURE [App::LinkElement] Link028_i16
  LinkPlacement = pos=(-110.5,8,3.4) rot=(0,0,1;0rad)
  LinkedObject = -> Screw
  Placement = pos=(-110.5,8,3.4) rot=(0,0,1;0rad)
FEATURE [App::LinkElement] Link028_i17
  LinkPlacement = pos=(-110.5,-7.99996,3.4) rot=(0,0,1;0rad)
  LinkedObject = -> Screw
  Placement = pos=(-110.5,-7.99996,3.4) rot=(0,0,1;0rad)
FEATURE [App::LinkElement] Link028_i18
  LinkPlacement = pos=(-110.5,-34,3.4) rot=(0,0,1;0rad)
  LinkedObject = -> Screw
  Placement = pos=(-110.5,-34,3.4) rot=(0,0,1;0rad)
FEATURE [App::Link] Link028  label="M5x10-Screw003"
  ElementCount = 19
  ElementList = -> [Link028_i0,Link028_i1,Link028_i2,Link028_i3,Link028_i4,Link028_i5,Link028_i6,Link028_i7,Link028_i8,Link028_i9,Link028_i10,Link028_i11,Link028_i12,Link028_i13,Link028_i14,Link028_i15,Link028_i16,Link028_i17,Link028_i18]
  LinkedObject = -> Screw
FEATURE [App::DocumentObjectGroup] Group006  label="carriage_fasteners"
  Group = -> [Screw,Link028]
FEATURE [Sketcher::SketchObject] Sketch075
  MapMode = 5
  Placement = pos=(0,0,0) rot=(1,0,0;1.5708rad)
  Support = -> [XZ_Plane094]
  sketch-geometry (8):
    g0: LineSegment StartX=-4.9 StartY=-3 StartZ=0 EndX=-4.9 EndY=0 EndZ=0
    g1: LineSegment StartX=-4.9 StartY=0 StartZ=0 EndX=4.9 EndY=0 EndZ=0
    g2: LineSegment StartX=4.9 StartY=0 StartZ=0 EndX=4.9 EndY=-3 EndZ=0
    g3: LineSegment StartX=4.9 StartY=-3 StartZ=0 EndX=8.5 EndY=-3 EndZ=0
    g4: LineSegment StartX=8.5 StartY=-3 StartZ=0 EndX=2.5 EndY=-9 EndZ=0
    g5: LineSegment StartX=2.5 StartY=-9 StartZ=0 EndX=-2.5 EndY=-9 EndZ=0
    g6: LineSegment StartX=-2.5 StartY=-9 StartZ=0 EndX=-8.5 EndY=-3 EndZ=0
    g7: LineSegment StartX=-8.5 StartY=-3 StartZ=0 EndX=-4.9 EndY=-3 EndZ=0
  constraints (20):
    c: Coincident(g0,g1)
    c: Coincident(g1,g2)
    c: Vertical(g2)
    c: Coincident(g2,g3)
    c: Coincident(g4,g5)
    c: Coincident(g5,g6)
    c: Symmetric(g0,g2,g-2)
    c: Coincident(g7,g0)
    c: Symmetric(g0,g1,g-2)
    c: PointOnObject(g-1,g1)
    c: Symmetric(g5,g4,g-2)
    c: Horizontal(g3)
    c: Symmetric(g7,g3,g-2)
    c: Perpendicular(g6,g4)
    c: DistanceY(g4,g1) = 9
    c: DistanceX(g1,g1) = 9.8
    c: DistanceY(g2,g2) = 3
    c: Coincident(g6,g7)
    c: Coincident(g4,g3)
    c: DistanceX(g6,g3) = 17
FEATURE [PartDesign::Pad] Pad027  label="Pad028"
  Length = 17
  Length2 = 100
  Midplane = true
  Placement = pos=(0,0,0) rot=(1,0,0;1.5708rad)
  Profile = -> Sketch075
  Type = 0
FEATURE [Sketcher::SketchObject] Sketch076
  MapMode = 5
  Support = -> [XY_Plane094]
  sketch-geometry (1):
    g0: Circle CenterX=0 CenterY=0 CenterZ=0 NormalX=0 NormalY=0 NormalZ=1 AngleXU=0 Radius=4
  constraints (2):
    c: Coincident(g0,g-1)
    c: Diameter(g0) = 8
FEATURE [PartDesign::Hole] Hole015
  BaseFeature = -> Pad027
  Depth = 25
  DepthType = 1
  Diameter = 6.75
  DrillPoint = 1
  DrillPointAngle = 118
  HoleCutCountersinkAngle = 90
  HoleCutDepth = 0
  HoleCutDiameter = 8
  HoleCutType = 0
  ModelActualThread = false
  Placement = pos=(0,0,0) rot=(1,0,0;1.5708rad)
  Profile = -> Sketch076
  Tapered = false
  TaperedAngle = 90
  ThreadAngle = 60
  ThreadClass = 0
  ThreadCutOffInner = 0.135316
  ThreadCutOffOuter = 0.270633
  ThreadDirection = 0
  ThreadFit = 0
  ThreadPitch = 1.25
  ThreadSize = 8
  ThreadType = 1
  Threaded = true
FEATURE [PartDesign::Fillet] Fillet005
  Base = -> Hole015 [Edge31,Edge5]
  BaseFeature = -> Hole015
  Placement = pos=(0,0,0) rot=(1,0,0;1.5708rad)
  Radius = 0.25
  SupportTransform = true
FEATURE [PartDesign::Body] Body029  label="t-nut_m8"
  Group = -> [Sketch075,Pad027,Sketch076,Hole015,Fillet005]
  Origin = -> Origin094
  Placement = pos=(-2,-12,0) rot=(0,1,0;1.5708rad)
  Tip = -> Fillet005
FEATURE [App::Part] Part044  label="rail_clamp"
  Group = -> [Body027,Screw005,Body029]
  Origin = -> Origin082
  Placement = pos=(51,-106,25.4) rot=(0,0,1;0rad)
FEATURE [App::LinkElement] Link029_i0
  LinkPlacement = pos=(51,106,25.4) rot=(1,0,0;3.14159rad)
  LinkedObject = -> Part044
  Placement = pos=(51,106,25.4) rot=(1,0,0;3.14159rad)
FEATURE [App::LinkElement] Link029_i1
  LinkPlacement = pos=(51,106,474.6) rot=(1,0,0;3.14159rad)
  LinkedObject = -> Part044
  Placement = pos=(51,106,474.6) rot=(1,0,0;3.14159rad)
FEATURE [App::LinkElement] Link029_i2
  LinkPlacement = pos=(51,-109,474.6) rot=(0,0,1;0rad)
  LinkedObject = -> Part044
  Placement = pos=(51,-109,474.6) rot=(0,0,1;0rad)
FEATURE [App::Link] Link029  label="rail_clamp001"
  ElementCount = 3
  ElementList = -> [Link029_i0,Link029_i1,Link029_i2]
  LinkedObject = -> Part044
FEATURE [App::Part] Part009  label="heated _bed_assy"
  Group = -> [Part001,Part010,Part011,Link010,Link001,Page001,Link029,Link029_i1,Link029_i2,Link029_i0]
  Origin = -> Origin012
  Placement = pos=(309,-24,47) rot=(0,0,1;0rad)
FEATURE [Part::FeaturePython] Screw006  label="M12x20-Screw"  # Fasteners workbench fastener (typed FeaturePython)
  Placement = pos=(-12.7,152.4,25.4) rot=(0,-1,0;1.5708rad)
  diameter = 10
  invert = false
  length = 0
  lengthCustom = 20
  matchOuter = false
  offset = 0
  thread = false
  type = 16
FEATURE [App::LinkElement] Link030_i0
  LinkPlacement = pos=(-12.7,-152.4,25.4) rot=(0,-1,0;1.5708rad)
  LinkedObject = -> Screw006
  Placement = pos=(-12.7,-152.4,25.4) rot=(0,-1,0;1.5708rad)
FEATURE [App::LinkElement] Link030_i1
  LinkPlacement = pos=(-12.7,152.4,101.6) rot=(0,-1,0;1.5708rad)
  LinkedObject = -> Screw006
  Placement = pos=(-12.7,152.4,101.6) rot=(0,-1,0;1.5708rad)
FEATURE [App::LinkElement] Link030_i2
  LinkPlacement = pos=(-12.7,-152.4,101.6) rot=(0,-1,0;1.5708rad)
  LinkedObject = -> Screw006
  Placement = pos=(-12.7,-152.4,101.6) rot=(0,-1,0;1.5708rad)
FEATURE [App::Link] Link030  label="M12x20-Screw001"
  ElementCount = 3
  ElementList = -> [Link030_i0,Link030_i1,Link030_i2]
  LinkedObject = -> Screw006
FEATURE [App::DocumentObjectGroup] Group007  label="frame_fasteners"
  Group = -> [Screw006,Link030]
FEATURE [Sketcher::SketchObject] Sketch077
  MapMode = 5
  Placement = pos=(0,0,0) rot=(0.57735,0.57735,0.57735;2.0944rad)
  Support = -> [YZ_Plane096]
  sketch-geometry (8):
    g0: LineSegment StartX=0 StartY=0 StartZ=0 EndX=0 EndY=6.35 EndZ=0
    g1: LineSegment StartX=0 StartY=6.35 StartZ=0 EndX=23.65 EndY=6.35 EndZ=0
    g2: LineSegment StartX=23.65 StartY=6.35 StartZ=0 EndX=23.65 EndY=25 EndZ=0
    g3: LineSegment StartX=23.65 StartY=25 StartZ=0 EndX=4.29667 EndY=44.3533 EndZ=0
    g4: LineSegment StartX=4.29667 StartY=44.3533 StartZ=0 EndX=8.7868 EndY=48.8435 EndZ=0
    g5: LineSegment StartX=8.7868 StartY=48.8435 StartZ=0 EndX=30 EndY=27.6303 EndZ=0
    g6: LineSegment StartX=30 StartY=27.6303 StartZ=0 EndX=30 EndY=0 EndZ=0
    g7: LineSegment StartX=30 StartY=0 StartZ=0 EndX=0 EndY=0 EndZ=0
  constraints (23):
    c: Coincident(g-1,g0)
    c: Vertical(g0)
    c: Coincident(g0,g1)
    c: Horizontal(g1)
    c: Coincident(g1,g2)
    c: Vertical(g2)
    c: Coincident(g2,g3)
    c: Coincident(g3,g4)
    c: Coincident(g4,g5)
    c: Coincident(g5,g6)
    c: PointOnObject(g6,g-1)
    c: Vertical(g6)
    c: Coincident(g6,g7)
    c: DistanceY(g0,g0) = 6.35
    c: DistanceX(g1,g6) = 6.35
    c: Parallel(g5,g3)
    c: Perpendicular(g3,g4)
    c: Angle(g3,g2) = 2.35619
    c: Distance(g4) = 6.35
    c: Distance(g7) = 30
    c: Coincident(g7,g0)
    c: DistanceY(g0,g2) = 25
    c: Distance(g5) = 30
FEATURE [PartDesign::Pad] Pad028  label="Pad029"
  Length = 57
  Length2 = 100
  Placement = pos=(0,0,0) rot=(0.57735,0.57735,0.57735;2.0944rad)
  Profile = -> Sketch077
  Reversed = true
  Type = 0
FEATURE [Sketcher::SketchObject] Sketch078
  MapMode = 5
  Placement = pos=(0,0,0) rot=(1,0,0;1.5708rad)
  Support = -> [XZ_Plane096]
  sketch-geometry (4):
    g0: LineSegment StartX=-70 StartY=0 StartZ=0 EndX=-20 EndY=0 EndZ=0
    g1: LineSegment StartX=-20 StartY=0 StartZ=0 EndX=-20 EndY=25 EndZ=0
    g2: LineSegment StartX=-20 StartY=25 StartZ=0 EndX=-70 EndY=25 EndZ=0
    g3: LineSegment StartX=-70 StartY=25 StartZ=0 EndX=-70 EndY=0 EndZ=0
  constraints (12):
    c: Coincident(g0,g1)
    c: Coincident(g1,g2)
    c: Coincident(g2,g3)
    c: Coincident(g3,g0)
    c: Horizontal(g0)
    c: Horizontal(g2)
    c: Vertical(g1)
    c: Vertical(g3)
    c: DistanceY(g3,g3) = 25
    c: Distance(g2) = 50
    c: PointOnObject(g0,g-1)
    c: DistanceX(g0,g-1) = 20
FEATURE [PartDesign::Pocket] Pocket021
  BaseFeature = -> Pad028
  Length = 5
  Length2 = 100
  Midplane = true
  Placement = pos=(0,0,0) rot=(0.57735,0.57735,0.57735;2.0944rad)
  Profile = -> Sketch078
  Type = 1
FEATURE [PartDesign::Chamfer] Chamfer003
  Angle = 45
  Base = -> Pocket021 [Edge8]
  BaseFeature = -> Pocket021
  ChamferType = 0
  FlipDirection = false
  Placement = pos=(0,0,0) rot=(0.57735,0.57735,0.57735;2.0944rad)
  Size = 27
  Size2 = 1
  SupportTransform = true
FEATURE [Sketcher::SketchObject] Sketch079
  AttachmentOffset = pos=(0,0,6.35) rot=(0,0,1;0rad)
  MapMode = 5
  Placement = pos=(0,0,6.35) rot=(0,0,1;0rad)
  Support = -> [XY_Plane096]
  sketch-geometry (1):
    g0: Circle CenterX=-10 CenterY=10 CenterZ=0 NormalX=0 NormalY=0 NormalZ=1 AngleXU=0 Radius=2.5
  constraints (3):
    c: Diameter(g0) = 5
    c: DistanceY(g-1,g0) = 10
    c: DistanceX(g0,g-1) = 10
FEATURE [PartDesign::Hole] Hole016
  BaseFeature = -> Chamfer003
  Depth = 25
  DepthType = 1
  Diameter = 5.1
  DrillPoint = 1
  DrillPointAngle = 118
  HoleCutCountersinkAngle = 90
  HoleCutDepth = 50
  HoleCutDiameter = 10
  HoleCutType = 0
  ModelActualThread = false
  Placement = pos=(0,0,0) rot=(0.57735,0.57735,0.57735;2.0944rad)
  Profile = -> Sketch079
  Tapered = false
  TaperedAngle = 90
  ThreadAngle = 0
  ThreadClass = 0
  ThreadCutOffInner = 0
  ThreadCutOffOuter = 0
  ThreadDirection = 0
  ThreadFit = 0
  ThreadPitch = 0
  ThreadSize = 0
  ThreadType = 0
  Threaded = false
FEATURE [PartDesign::Body] Body030  label="Body033"
  Group = -> [Sketch077,Pad028,Sketch078,Pocket021,Chamfer003,Sketch079,Hole016]
  Origin = -> Origin096
  Tip = -> Hole016
FEATURE [Part::FeaturePython] Screw007  label="M5x10-Screw009"  # Fasteners workbench fastener (typed FeaturePython)
  Placement = pos=(-9.95,9.9,6.35) rot=(0,0,1;0rad)
  diameter = 3
  invert = false
  length = 1
  lengthCustom = 10
  matchOuter = false
  offset = 0
  thread = false
  type = 22
FEATURE [Sketcher::SketchObject] Sketch080
  MapMode = 5
  Support = -> [XY_Plane097]
  sketch-geometry (1):
    g0: Circle CenterX=0 CenterY=0 CenterZ=0 NormalX=0 NormalY=0 NormalZ=1 AngleXU=0 Radius=4
  constraints (2):
    c: Coincident(g0,g-1)
    c: Diameter(g0) = 8
FEATURE [Sketcher::SketchObject] Sketch081
  MapMode = 5
  Placement = pos=(0,0,0) rot=(1,0,0;1.5708rad)
  Support = -> [XZ_Plane097]
  sketch-geometry (8):
    g0: LineSegment StartX=-3 StartY=-1 StartZ=0 EndX=-3 EndY=0 EndZ=0
    g1: LineSegment StartX=-3 StartY=0 StartZ=0 EndX=3 EndY=0 EndZ=0
    g2: LineSegment StartX=3 StartY=0 StartZ=0 EndX=3 EndY=-1 EndZ=0
    g3: LineSegment StartX=3 StartY=-1 StartZ=0 EndX=5 EndY=-1 EndZ=0
    g4: LineSegment StartX=5 StartY=-1 StartZ=0 EndX=2 EndY=-4 EndZ=0
    g5: LineSegment StartX=2 StartY=-4 StartZ=0 EndX=-2 EndY=-4 EndZ=0
    g6: LineSegment StartX=-2 StartY=-4 StartZ=0 EndX=-5 EndY=-1 EndZ=0
    g7: LineSegment StartX=-5 StartY=-1 StartZ=0 EndX=-3 EndY=-1 EndZ=0
  constraints (20):
    c: Coincident(g0,g1)
    c: Coincident(g1,g2)
    c: Vertical(g2)
    c: Coincident(g2,g3)
    c: Coincident(g4,g5)
    c: Coincident(g5,g6)
    c: Symmetric(g0,g2,g-2)
    c: Coincident(g7,g0)
    c: Symmetric(g0,g1,g-2)
    c: PointOnObject(g-1,g1)
    c: Symmetric(g5,g4,g-2)
    c: Horizontal(g3)
    c: Symmetric(g7,g3,g-2)
    c: Perpendicular(g6,g4)
    c: DistanceY(g4,g1) = 4
    c: DistanceX(g1,g1) = 6
    c: DistanceY(g2,g2) = 1
    c: Coincident(g6,g7)
    c: Coincident(g4,g3)
    c: DistanceX(g6,g3) = 10
FEATURE [PartDesign::Pad] Pad029  label="Pad030"
  Length = 10
  Length2 = 100
  Midplane = true
  Placement = pos=(0,0,0) rot=(1,0,0;1.5708rad)
  Profile = -> Sketch081
  Type = 0
FEATURE [PartDesign::Hole] Hole017
  BaseFeature = -> Pad029
  Depth = 25
  DepthType = 1
  Diameter = 4.2
  DrillPoint = 1
  DrillPointAngle = 118
  HoleCutCountersinkAngle = 90
  HoleCutDepth = 0
  HoleCutDiameter = 5
  HoleCutType = 0
  ModelActualThread = false
  Placement = pos=(0,0,0) rot=(1,0,0;1.5708rad)
  Profile = -> Sketch080
  Tapered = false
  TaperedAngle = 90
  ThreadAngle = 60
  ThreadClass = 0
  ThreadCutOffInner = 0.0866025
  ThreadCutOffOuter = 0.173205
  ThreadDirection = 0
  ThreadFit = 0
  ThreadPitch = 0.8
  ThreadSize = 6
  ThreadType = 1
  Threaded = true
FEATURE [PartDesign::Fillet] Fillet006
  Base = -> Hole017 [Edge5,Edge31]
  BaseFeature = -> Hole017
  Placement = pos=(0,0,0) rot=(1,0,0;1.5708rad)
  Radius = 0.2
  SupportTransform = true
FEATURE [PartDesign::Body] Body031  label="t-nut_m5"
  Group = -> [Sketch081,Pad029,Sketch080,Hole017,Fillet006]
  Origin = -> Origin097
  Placement = pos=(-9.95,9.9,-0.85) rot=(0,0,1;0rad)
  Tip = -> Fillet006
FEATURE [App::Part] Part047  label="cable_chain_mount_1"
  Group = -> [Body030,Screw007,Body031]
  Origin = -> Origin095
  Placement = pos=(-211.7,40,6.4) rot=(0.57735,-0.57735,-0.57735;4.18879rad)
FEATURE [App::Part] Part048  label="curved_part_for_drag_chain"
  Group = -> [Part__Feature1426,Part__Feature1427,Part__Feature1428,Part__Feature1429,Part__Feature1430,Part__Feature1431,Part__Feature1432,Part__Feature1398]
  Origin = -> Origin098
  Placement = pos=(0,0.6,-6.1) rot=(0,0,1;0rad)
FEATURE [App::Part] Document001  label="carriage_cable_chain"
  Group = -> [Part__Feature1399,Part__Feature1400,Part__Feature1401,Part__Feature1402,Part__Feature1403,Part__Feature1404,Part__Feature1405,Part__Feature1406,Part__Feature1407,Part__Feature1408,Part__Feature1409,Part__Feature1411,Part__Feature1413,Part__Feature1416,Part__Feature1417,Part__Feature1418,Part__Feature1419,Part__Feature1420,Part__Feature1421,Part__Feature1433,Part__Feature1434,Part048]
  Origin = -> Origin088
  Placement = pos=(-158.735,117.319,49.3) rot=(0.567007,0.5975,-0.567007;2.06443rad)
FEATURE [App::Link] Link031  label="15"_DIN_rail001"
  LinkPlacement = pos=(538,-228,315) rot=(0,0,1;3.14159rad)
  LinkedObject = -> Part043
  Placement = pos=(538,-228,315) rot=(0,0,1;3.14159rad)
FEATURE [Part::Feature] Part__Feature1435  label="Meanwell S-400-48 Power Supply v23"
  Placement = pos=(531,-238,375) rot=(0,0.707107,-0.707107;3.14159rad)
  shape: bbox 215 x 50 x 115 mm, 331 faces (baked)
FEATURE [App::DocumentObjectGroup] Group005  label="electronics"
  Group = -> [Part043,Part__Feature1347,Raspberry_Pi_4_Model_B,Link031,Part__Feature1435,Part__Feature034]
FEATURE [Part::FeaturePython] Screw008  label="M3x8-Screw"  # Fasteners workbench fastener (typed FeaturePython)
  Placement = pos=(8.5,-6.5,1e-15) rot=(1,0,0;3.14159rad)
  diameter = 1
  invert = false
  length = 1
  lengthCustom = 8
  matchOuter = false
  offset = 0
  thread = false
  type = 22
FEATURE [App::LinkElement] Link032_i0
  LinkPlacement = pos=(39.5,-6.49997,-1.5974e-05) rot=(1,0,0;3.14159rad)
  LinkedObject = -> Screw008
  Placement = pos=(39.5,-6.49997,-1.5974e-05) rot=(1,0,0;3.14159rad)
FEATURE [App::LinkElement] Link032_i1
  LinkPlacement = pos=(8.49998,-37.5001,-1.52588e-05) rot=(1,0,0;3.14159rad)
  LinkedObject = -> Screw008
  Placement = pos=(8.49998,-37.5001,-1.52588e-05) rot=(1,0,0;3.14159rad)
FEATURE [App::LinkElement] Link032_i2
  LinkPlacement = pos=(39.5,-37.5002,2.21175e-05) rot=(1,0,0;3.14159rad)
  LinkedObject = -> Screw008
  Placement = pos=(39.5,-37.5002,2.21175e-05) rot=(1,0,0;3.14159rad)
FEATURE [App::Link] Link032  label="M3x8-Screw001"
  ElementCount = 3
  ElementList = -> [Link032_i0,Link032_i1,Link032_i2]
  LinkedObject = -> Screw008
FEATURE [Part::FeaturePython] Screw009  label="M5x10-Screw007"  # Fasteners workbench fastener (typed FeaturePython)
  Placement = pos=(-1.1,12.5,-21) rot=(0,-1,0;1.5708rad)
  diameter = 3
  invert = false
  length = 1
  lengthCustom = 10
  matchOuter = false
  offset = 0
  thread = false
  type = 22
FEATURE [App::LinkElement] Link033_i0
  LinkPlacement = pos=(4.70004,12.5,-21.0001) rot=(0,-1,0;1.5708rad)
  LinkedObject = -> Body031
  Placement = pos=(4.70004,12.5,-21.0001) rot=(0,-1,0;1.5708rad)
FEATURE [App::LinkElement] Link033_i1
  LinkPlacement = pos=(4.7,12.4999,-41.0001) rot=(0,-1,0;1.5708rad)
  LinkedObject = -> Body031
  Placement = pos=(4.7,12.4999,-41.0001) rot=(0,-1,0;1.5708rad)
FEATURE [App::Link] Link033  label="t-nut_m5_001"
  ElementCount = 2
  ElementList = -> [Link033_i0,Link033_i1]
  LinkedObject = -> Body031
FEATURE [App::Link] Link034  label="M5x10-Screw006"
  LinkPlacement = pos=(-1.09997,12.5,-41.0001) rot=(0,-1,0;1.5708rad)
  LinkedObject = -> Screw009
  Placement = pos=(-1.09997,12.5,-41.0001) rot=(0,-1,0;1.5708rad)
FEATURE [Part::FeaturePython] Washer  label="M5-Washer"  # Fasteners workbench fastener (typed FeaturePython)
  Placement = pos=(5e-15,12.5,-21) rot=(0,-1,0;1.5708rad)
  diameter = 6
  invert = false
  matchOuter = false
  offset = 0
  type = 0
FEATURE [App::Link] Link035  label="M5-Washer001"
  LinkPlacement = pos=(-1.80006e-05,12.4999,-41) rot=(0,-1,0;1.5708rad)
  LinkedObject = -> Washer
  Placement = pos=(-1.80006e-05,12.4999,-41) rot=(0,-1,0;1.5708rad)
FEATURE [App::Part] Part019  label="y_motor_bracket"
  Group = -> [Part021,Part022,Screw008,Link032_i0,Link032_i1,Link032_i2,Link032,Screw009,Link033,Link034,Washer,Link035]
  Origin = -> Origin026
  Placement = pos=(-249.5,11,2.5) rot=(-0.57735,-0.57735,-0.57735;2.0944rad)
FEATURE [TechDraw::DrawSVGTemplate] Template003
  EditableTexts = Author=Alex Neufeld; DWG_num=2020-102; Date=15/05/2020; Revision=2; Scale=NTS; Subtitle=4 Req.; Title=12mm Shaft Clamp
  Height = 215.9
  Orientation = 1
  Width = 279.4
FEATURE [TechDraw::DrawViewPart] View003
  CoarseView = false
  Direction = (0.577,-0.577,0.577)
  Focus = 100
  HardHidden = false
  IsoCount = 0
  IsoHidden = false
  IsoVisible = false
  LockPosition = false
  Perspective = false
  Rotation = 0
  Scale = 0.5
  ScaleType = 0
  SeamHidden = false
  SeamVisible = true
  SmoothHidden = false
  SmoothVisible = true
  Source = -> [Body027]
  X = 33.5005
  XDirection = (0.707,0.707,0)
  Y = 183.223
FEATURE [TechDraw::DrawProjGroupItem] ProjItem014  label="Front003"
  CoarseView = false
  Direction = (1,0,0)
  Focus = 100
  HardHidden = false
  IsoCount = 0
  IsoHidden = false
  IsoVisible = false
  LockPosition = true
  Perspective = false
  Rotation = 0
  RotationVector = (0,1,0)
  ScaleType = 2
  SeamHidden = false
  SeamVisible = true
  SmoothHidden = false
  SmoothVisible = true
  Source = -> [Body027]
  Type = 0
  X = 0
  XDirection = (0,1,0)
  Y = 0
FEATURE [TechDraw::DrawProjGroupItem] ProjItem015  label="Bottom003"
  CoarseView = false
  Direction = (0,0,-1)
  Focus = 100
  HardHidden = false
  IsoCount = 0
  IsoHidden = false
  IsoVisible = false
  LockPosition = false
  Perspective = false
  Rotation = 0
  RotationVector = (1,0,0)
  ScaleType = 2
  SeamHidden = false
  SeamVisible = true
  SmoothHidden = false
  SmoothVisible = true
  Source = -> [Body027]
  Type = 5
  X = 0
  XDirection = (0,1,0)
  Y = 65
FEATURE [TechDraw::DrawProjGroupItem] ProjItem016  label="Left002"
  CoarseView = false
  Direction = (1e-16,-1,0)
  Focus = 100
  HardHidden = false
  IsoCount = 0
  IsoHidden = false
  IsoVisible = false
  LockPosition = false
  Perspective = false
  Rotation = 0
  RotationVector = (1,0,0)
  ScaleType = 2
  SeamHidden = false
  SeamVisible = true
  SmoothHidden = false
  SmoothVisible = true
  Source = -> [Body027]
  Type = 1
  X = 52
  XDirection = (1,1e-16,0)
  Y = 0
FEATURE [TechDraw::DrawProjGroup] ProjGroup003
  Anchor = -> ProjItem014
  AutoDistribute = true
  LockPosition = false
  ProjectionType = 0
  Rotation = 0
  ScaleType = 0
  Source = -> [Body027]
  Views = -> [ProjItem014,ProjItem015,ProjItem016]
  X = 116.598
  Y = 88.1517
  spacingX = 15
  spacingY = 15
FEATURE [TechDraw::DrawViewDimension] Dimension065
  Arbitrary = false
  FormatSpec = %.2f
  Inverted = false
  LockPosition = false
  MeasureType = 1
  OverTolerance = 0
  References2D = -> [ProjItem014]
  Rotation = 0
  ScaleType = 0
  TheoreticalExact = false
  Type = 2
  UnderTolerance = 0
  X = -37.8717
  Y = 1.13496
FEATURE [TechDraw::DrawViewDimension] Dimension066
  Arbitrary = false
  FormatSpec = %.2f
  Inverted = false
  LockPosition = false
  MeasureType = 1
  OverTolerance = 0
  References2D = -> [ProjItem014]
  Rotation = 0
  ScaleType = 0
  TheoreticalExact = false
  Type = 1
  UnderTolerance = 0
  X = 0.243131
  Y = 37.6367
FEATURE [TechDraw::DrawViewDimension] Dimension067
  Arbitrary = false
  FormatSpec = %.2f
  Inverted = false
  LockPosition = false
  MeasureType = 1
  OverTolerance = 0
  References2D = -> [ProjItem016]
  Rotation = 0
  ScaleType = 0
  TheoreticalExact = false
  Type = 1
  UnderTolerance = 0
  X = 0
  Y = 39.0878
FEATURE [TechDraw::DrawViewDimension] Dimension071
  Arbitrary = false
  FormatSpec = R%.2f
  Inverted = false
  LockPosition = false
  MeasureType = 1
  OverTolerance = 0
  References2D = -> [ProjItem014]
  Rotation = 0
  ScaleType = 0
  TheoreticalExact = false
  Type = 4
  UnderTolerance = 0
  X = 26.3188
  Y = -26.8506
FEATURE [TechDraw::DrawViewDimension] Dimension072
  Arbitrary = false
  FormatSpec = %.2f
  Inverted = false
  LockPosition = false
  MeasureType = 1
  OverTolerance = 0
  References2D = -> [ProjItem014]
  Rotation = 0
  ScaleType = 0
  TheoreticalExact = false
  Type = 2
  UnderTolerance = 0
  X = -29.7505
  Y = 14.0649
FEATURE [TechDraw::DrawViewDimension] Dimension073
  Arbitrary = false
  FormatSpec = %.2f
  Inverted = false
  LockPosition = false
  MeasureType = 1
  OverTolerance = 0
  References2D = -> [ProjItem014]
  Rotation = 0
  ScaleType = 0
  TheoreticalExact = false
  Type = 1
  UnderTolerance = 0
  X = 6.85175
  Y = 30.4524
FEATURE [TechDraw::DrawViewDimension] Dimension074
  Arbitrary = false
  FormatSpec = %.2f
  Inverted = false
  LockPosition = false
  MeasureType = 1
  OverTolerance = 0
  References2D = -> [ProjItem015]
  Rotation = 0
  ScaleType = 0
  TheoreticalExact = false
  Type = 2
  UnderTolerance = 0
  X = 30.2019
  Y = 19.9033
FEATURE [TechDraw::DrawViewDimension] Dimension075
  Arbitrary = false
  FormatSpec = %.2f
  Inverted = false
  LockPosition = false
  MeasureType = 1
  OverTolerance = 0
  References2D = -> [ProjItem016]
  Rotation = 0
  ScaleType = 0
  TheoreticalExact = false
  Type = 1
  UnderTolerance = 0
  X = 21.6334
  Y = -26.5519
FEATURE [TechDraw::DrawViewDimension] Dimension076
  Arbitrary = false
  FormatSpec = %.2f
  Inverted = false
  LockPosition = false
  MeasureType = 1
  OverTolerance = 0
  References2D = -> [ProjItem016]
  Rotation = 0
  ScaleType = 0
  TheoreticalExact = false
  Type = 1
  UnderTolerance = 0
  X = 21.8059
  Y = -36.276
FEATURE [TechDraw::DrawViewDimension] Dimension077
  Arbitrary = false
  FormatSpec = %.2f
  Inverted = false
  LockPosition = false
  MeasureType = 1
  OverTolerance = 0
  References2D = -> [ProjItem015]
  Rotation = 0
  ScaleType = 0
  TheoreticalExact = false
  Type = 1
  UnderTolerance = 0
  X = -3.60183
  Y = 32.5074
FEATURE [TechDraw::DrawViewDimension] Dimension078
  Arbitrary = false
  FormatSpec = %.2f
  Inverted = false
  LockPosition = false
  MeasureType = 1
  OverTolerance = 0
  References2D = -> [ProjItem015]
  Rotation = 0
  ScaleType = 0
  TheoreticalExact = false
  Type = 1
  UnderTolerance = 0
  X = -2.87816
  Y = 24.8554
FEATURE [TechDraw::DrawViewDimension] Dimension079
  Arbitrary = false
  FormatSpec = %.2f
  Inverted = false
  LockPosition = false
  MeasureType = 1
  OverTolerance = 0
  References2D = -> [ProjItem015]
  Rotation = 0
  ScaleType = 0
  TheoreticalExact = false
  Type = 1
  UnderTolerance = 0
  X = -2.68862
  Y = 15.912
FEATURE [TechDraw::DrawViewDimension] Dimension080
  Arbitrary = false
  FormatSpec = ⌀%.2f
  Inverted = false
  LockPosition = false
  MeasureType = 1
  OverTolerance = 0
  References2D = -> [ProjItem014]
  Rotation = 0
  ScaleType = 0
  TheoreticalExact = false
  Type = 5
  UnderTolerance = 0
  X = 1.86435
  Y = 11.9851
FEATURE [TechDraw::DrawViewDimension] Dimension081
  Arbitrary = false
  FormatSpec = %.2f
  Inverted = false
  LockPosition = false
  MeasureType = 1
  OverTolerance = 0
  References2D = -> [ProjItem016]
  Rotation = 0
  ScaleType = 0
  TheoreticalExact = false
  Type = 1
  UnderTolerance = 0
  X = 22.9956
  Y = 31.5567
FEATURE [TechDraw::DrawPage] Page003  label="shaft_clamp_dwg"
  KeepUpdated = true
  NextBalloonIndex = 1
  ProjectionType = 0
  Template = -> Template003
  Views = -> [View003,ProjGroup003,Dimension065,Dimension066,Dimension067,Dimension071,Dimension072,Dimension073,Dimension074,Dimension075,Dimension076,Dimension077,Dimension078,Dimension079,Dimension080,Dimension081]
FEATURE [TechDraw::DrawSVGTemplate] Template004
  EditableTexts = Author=Alex Neufeld; DWG_num=2020-103; Date=15/05/2020; Revision=2; Scale=NTS; Subtitle=For use with 20T 2GT pulley; Title=X-Axis Idler Bracket
  Height = 215.9
  Orientation = 1
  Width = 279.4
FEATURE [TechDraw::DrawViewPart] View004
  CoarseView = false
  Direction = (0.577,-0.577,0.577)
  Focus = 100
  HardHidden = false
  IsoCount = 0
  IsoHidden = false
  IsoVisible = false
  LockPosition = true
  Perspective = false
  Rotation = 0
  ScaleType = 0
  SeamHidden = false
  SeamVisible = true
  SmoothHidden = false
  SmoothVisible = true
  Source = -> [Part033]
  X = 36.0346
  XDirection = (0.707,0.707,0)
  Y = 180.306
FEATURE [TechDraw::DrawProjGroupItem] ProjItem017  label="Front004"
  CoarseView = false
  Direction = (1,0,0)
  Focus = 100
  HardHidden = false
  IsoCount = 0
  IsoHidden = false
  IsoVisible = false
  LockPosition = true
  Perspective = false
  Rotation = 0
  RotationVector = (0,1,0)
  Scale = 2
  ScaleType = 2
  SeamHidden = false
  SeamVisible = true
  SmoothHidden = false
  SmoothVisible = true
  Source = -> [View004,Part033]
  Type = 0
  X = 0
  XDirection = (0,-1,1e-16)
  Y = 0
FEATURE [TechDraw::DrawProjGroupItem] ProjItem018  label="Bottom004"
  CoarseView = false
  Direction = (0,1e-16,1)
  Focus = 100
  HardHidden = false
  IsoCount = 0
  IsoHidden = false
  IsoVisible = false
  LockPosition = true
  Perspective = false
  Rotation = 0
  RotationVector = (1,0,0)
  Scale = 2
  ScaleType = 2
  SeamHidden = false
  SeamVisible = true
  SmoothHidden = false
  SmoothVisible = true
  Source = -> [View004,Part033]
  Type = 5
  X = 0
  XDirection = (0,-1,1e-16)
  Y = 64.4821
FEATURE [TechDraw::DrawProjGroupItem] ProjItem019  label="Left003"
  CoarseView = false
  Direction = (1e-16,1,-1e-16)
  Focus = 100
  HardHidden = false
  IsoCount = 0
  IsoHidden = false
  IsoVisible = false
  LockPosition = true
  Perspective = false
  Rotation = 0
  RotationVector = (1,0,0)
  Scale = 2
  ScaleType = 2
  SeamHidden = false
  SeamVisible = true
  SmoothHidden = false
  SmoothVisible = true
  Source = -> [View004,Part033]
  Type = 1
  X = 76
  XDirection = (1,-1e-16,0)
  Y = 0
FEATURE [TechDraw::DrawProjGroup] ProjGroup004
  Anchor = -> ProjItem017
  AutoDistribute = true
  LockPosition = false
  ProjectionType = 0
  Rotation = 0
  Scale = 2
  ScaleType = 2
  Source = -> [View004,Part033]
  Views = -> [ProjItem017,ProjItem018,ProjItem019]
  X = 118.879
  Y = 93.5714
  spacingX = 15
  spacingY = 15
FEATURE [TechDraw::DrawViewDimension] Dimension082
  Arbitrary = false
  FormatSpec = %.2f
  Inverted = false
  LockPosition = false
  MeasureType = 1
  OverTolerance = 0
  References2D = -> [ProjItem018]
  Rotation = 0
  ScaleType = 0
  TheoreticalExact = false
  Type = 2
  UnderTolerance = 0
  X = -38.4355
  Y = -15.5
FEATURE [TechDraw::DrawViewDimension] Dimension083
  Arbitrary = false
  FormatSpec = %.2f
  Inverted = false
  LockPosition = false
  MeasureType = 1
  OverTolerance = 0
  References2D = -> [ProjItem018]
  Rotation = 0
  ScaleType = 0
  TheoreticalExact = false
  Type = 2
  UnderTolerance = 0
  X = 37.4428
  Y = -7.00652
FEATURE [TechDraw::DrawViewDimension] Dimension084
  Arbitrary = false
  FormatSpec = %.2f
  Inverted = false
  LockPosition = false
  MeasureType = 1
  OverTolerance = 0
  References2D = -> [ProjItem018]
  Rotation = 0
  ScaleType = 0
  TheoreticalExact = false
  Type = 1
  UnderTolerance = 0
  X = -8.18841
  Y = 28.9239
FEATURE [TechDraw::DrawViewDimension] Dimension085
  Arbitrary = false
  FormatSpec = R%.2f
  Inverted = false
  LockPosition = false
  MeasureType = 1
  OverTolerance = 0
  References2D = -> [ProjItem018]
  Rotation = 0
  ScaleType = 0
  TheoreticalExact = false
  Type = 4
  UnderTolerance = 0
  X = 38.8334
  Y = 18.066
FEATURE [TechDraw::DrawViewDimension] Dimension086
  Arbitrary = false
  FormatSpec = ⌀%.2f
  Inverted = false
  LockPosition = false
  MeasureType = 1
  OverTolerance = 0
  References2D = -> [ProjItem018]
  Rotation = 0
  ScaleType = 0
  TheoreticalExact = false
  Type = 5
  UnderTolerance = 0
  X = 6.07827
  Y = -4.13322
FEATURE [TechDraw::DrawViewDimension] Dimension087
  Arbitrary = false
  FormatSpec = %.2f
  Inverted = false
  LockPosition = false
  MeasureType = 1
  OverTolerance = 0
  References2D = -> [ProjItem018]
  Rotation = 0
  ScaleType = 0
  TheoreticalExact = false
  Type = 1
  UnderTolerance = 0
  X = -10.1623
  Y = -23.4094
FEATURE [TechDraw::DrawViewDimension] Dimension088
  Arbitrary = false
  FormatSpec = %.2f
  Inverted = false
  LockPosition = false
  MeasureType = 1
  OverTolerance = 0
  References2D = -> [ProjItem018]
  Rotation = 0
  ScaleType = 0
  TheoreticalExact = false
  Type = 6
  UnderTolerance = 0
  X = -8.44204
  Y = -7.93551
FEATURE [TechDraw::DrawViewDimension] Dimension089
  Arbitrary = false
  FormatSpec = %.2f
  Inverted = false
  LockPosition = false
  MeasureType = 1
  OverTolerance = 0
  References2D = -> [ProjItem017]
  Rotation = 0
  ScaleType = 0
  TheoreticalExact = false
  Type = 1
  UnderTolerance = 0
  X = -20.2974
  Y = 25.9805
FEATURE [TechDraw::DrawViewDimension] Dimension090
  Arbitrary = false
  FormatSpec = %.2f
  Inverted = false
  LockPosition = false
  MeasureType = 1
  OverTolerance = 0
  References2D = -> [ProjItem017]
  Rotation = 0
  ScaleType = 0
  TheoreticalExact = false
  Type = 2
  UnderTolerance = 0
  X = -45.5396
  Y = -8.78435
FEATURE [TechDraw::DrawViewDimension] Dimension091
  Arbitrary = false
  FormatSpec = %.2f
  Inverted = false
  LockPosition = false
  MeasureType = 1
  OverTolerance = 0
  References2D = -> [ProjItem017]
  Rotation = 0
  ScaleType = 0
  TheoreticalExact = false
  Type = 1
  UnderTolerance = 0
  X = 1.01304
  Y = -29.1174
FEATURE [TechDraw::DrawViewDimension] Dimension092
  Arbitrary = false
  FormatSpec = %.2f
  Inverted = false
  LockPosition = false
  MeasureType = 1
  OverTolerance = 0
  References2D = -> [ProjItem017]
  Rotation = 0
  ScaleType = 0
  TheoreticalExact = false
  Type = 2
  UnderTolerance = 0
  X = -52.8948
  Y = -0.11725
FEATURE [TechDraw::DrawViewDimension] Dimension093
  Arbitrary = false
  FormatSpec = %.2f
  Inverted = false
  LockPosition = false
  MeasureType = 1
  OverTolerance = 0
  References2D = -> [ProjItem019]
  Rotation = 0
  ScaleType = 0
  TheoreticalExact = false
  Type = 1
  UnderTolerance = 0
  X = -0.330424
  Y = -36.192
FEATURE [TechDraw::DrawViewDimension] Dimension094
  Arbitrary = false
  FormatSpec = %.2f
  Inverted = false
  LockPosition = false
  MeasureType = 1
  OverTolerance = 0
  References2D = -> [ProjItem019]
  Rotation = 0
  ScaleType = 0
  TheoreticalExact = false
  Type = 1
  UnderTolerance = 0
  X = -1.85725
  Y = 28.1044
FEATURE [TechDraw::DrawViewDimension] Dimension095
  Arbitrary = false
  FormatSpec = %.2f
  Inverted = false
  LockPosition = false
  MeasureType = 1
  OverTolerance = 0
  References2D = -> [ProjItem019]
  Rotation = 0
  ScaleType = 0
  TheoreticalExact = false
  Type = 2
  UnderTolerance = 0
  X = 23.4094
  Y = 0.506522
FEATURE [TechDraw::DrawViewDimension] Dimension096
  Arbitrary = false
  FormatSpec = %.2f
  Inverted = false
  LockPosition = false
  MeasureType = 1
  OverTolerance = 0
  References2D = -> [ProjItem017]
  Rotation = 0
  ScaleType = 0
  TheoreticalExact = false
  Type = 1
  UnderTolerance = 0
  X = 13.6623
  Y = -1.05651
FEATURE [TechDraw::DrawViewDimension] Dimension097
  Arbitrary = false
  FormatSpec = ⌀%.2f
  Inverted = false
  LockPosition = false
  MeasureType = 1
  OverTolerance = 0
  References2D = -> [ProjItem017]
  Rotation = 0
  ScaleType = 0
  TheoreticalExact = false
  Type = 5
  UnderTolerance = 0
  X = 4.37635
  Y = 6.07827
FEATURE [TechDraw::DrawPage] Page004  label="x_idler_bracket_dwg001"
  KeepUpdated = true
  NextBalloonIndex = 1
  ProjectionType = 0
  Template = -> Template004
  Views = -> [View004,ProjGroup004,Dimension082,Dimension083,Dimension084,Dimension085,Dimension086,Dimension087,Dimension088,Dimension089,Dimension090,Dimension091,Dimension092,Dimension093,Dimension094,Dimension095,Dimension096,Dimension097]
FEATURE [TechDraw::DrawSVGTemplate] Template005
  EditableTexts = Author=Alex Neufeld; DWG_num=2020-104; Date=15/05/2020; Revision=1; Scale=NTS; Subtitle=For use with 20T 2GT pulley; Title=Y-Axis Idler Bracket
  Height = 215.9
  Orientation = 1
  Width = 279.4
FEATURE [TechDraw::DrawViewPart] View006
  CoarseView = false
  Direction = (0.577,-0.577,0.577)
  Focus = 100
  HardHidden = false
  IsoCount = 0
  IsoHidden = false
  IsoVisible = false
  LockPosition = true
  Perspective = false
  Rotation = 0
  ScaleType = 0
  SeamHidden = false
  SeamVisible = true
  SmoothHidden = false
  SmoothVisible = true
  X = 33.2088
  XDirection = (0.707,0.707,0)
  Y = 180.014
FEATURE [TechDraw::DrawProjGroupItem] ProjItem020  label="Front005"
  CoarseView = false
  Direction = (0,1,0)
  Focus = 100
  HardHidden = false
  IsoCount = 0
  IsoHidden = false
  IsoVisible = false
  LockPosition = true
  Perspective = false
  Rotation = 0
  RotationVector = (-1,0,0)
  Scale = 2
  ScaleType = 2
  SeamHidden = false
  SeamVisible = true
  SmoothHidden = false
  SmoothVisible = true
  Type = 0
  X = 0
  XDirection = (-1e-16,0,1)
  Y = 0
FEATURE [TechDraw::DrawProjGroupItem] ProjItem022  label="Left004"
  CoarseView = false
  Direction = (1e-16,1e-16,-1)
  Focus = 100
  HardHidden = false
  IsoCount = 0
  IsoHidden = false
  IsoVisible = false
  LockPosition = true
  Perspective = false
  Rotation = 0
  RotationVector = (1,0,0)
  Scale = 2
  ScaleType = 2
  SeamHidden = false
  SeamVisible = true
  SmoothHidden = false
  SmoothVisible = true
  Type = 1
  X = 81.9849
  XDirection = (0,1,1e-16)
  Y = 0
FEATURE [TechDraw::DrawProjGroup] ProjGroup005
  Anchor = -> ProjItem020
  AutoDistribute = true
  LockPosition = false
  ProjectionType = 0
  Rotation = 0
  Scale = 2
  ScaleType = 2
  Views = -> [ProjItem020,ProjItem022]
  X = 114.455
  Y = 110.851
  spacingX = 15
  spacingY = 15
FEATURE [TechDraw::DrawViewDimension] Dimension098
  Arbitrary = false
  FormatSpec = %.2f
  Inverted = false
  LockPosition = false
  MeasureType = 1
  OverTolerance = 0
  References2D = -> [ProjItem022]
  Rotation = 0
  ScaleType = 0
  TheoreticalExact = false
  Type = 1
  UnderTolerance = 0
  X = 10.0751
  Y = 36.3832
FEATURE [TechDraw::DrawViewDimension] Dimension099
  Arbitrary = false
  FormatSpec = %.2f
  Inverted = false
  LockPosition = false
  MeasureType = 1
  OverTolerance = 0
  References2D = -> [ProjItem020]
  Rotation = 0
  ScaleType = 0
  TheoreticalExact = false
  Type = 1
  UnderTolerance = 0
  X = 0
  Y = -28.9542
FEATURE [TechDraw::DrawViewDimension] Dimension100
  Arbitrary = false
  FormatSpec = %.2f
  Inverted = false
  LockPosition = false
  MeasureType = 1
  OverTolerance = 0
  References2D = -> [ProjItem020]
  Rotation = 0
  ScaleType = 0
  TheoreticalExact = false
  Type = 1
  UnderTolerance = 0
  X = 0.337681
  Y = -35.8767
FEATURE [TechDraw::DrawViewDimension] Dimension101
  Arbitrary = false
  FormatSpec = ⌀%.2f
  Inverted = false
  LockPosition = false
  MeasureType = 1
  OverTolerance = 0
  References2D = -> [ProjItem020]
  Rotation = 0
  ScaleType = 0
  TheoreticalExact = false
  Type = 5
  UnderTolerance = 0
  X = 41.1971
  Y = 1.18189
FEATURE [TechDraw::DrawViewDimension] Dimension102
  Arbitrary = false
  FormatSpec = ⌀%.2f
  Inverted = false
  LockPosition = false
  MeasureType = 1
  OverTolerance = 0
  References2D = -> [ProjItem022]
  Rotation = 0
  ScaleType = 0
  TheoreticalExact = false
  Type = 5
  UnderTolerance = 0
  X = 21.2739
  Y = -25.8326
FEATURE [TechDraw::DrawViewDimension] Dimension103
  Arbitrary = false
  FormatSpec = %.1f
  Inverted = false
  LockPosition = false
  MeasureType = 1
  OverTolerance = 0
  References2D = -> [ProjItem022]
  Rotation = 0
  ScaleType = 0
  TheoreticalExact = false
  Type = 6
  UnderTolerance = 0
  X = 6.92247
  Y = 9.9616
FEATURE [TechDraw::DrawViewDimension] Dimension104
  Arbitrary = false
  FormatSpec = R%.2f
  Inverted = false
  LockPosition = false
  MeasureType = 1
  OverTolerance = 0
  References2D = -> [ProjItem022]
  Rotation = 0
  ScaleType = 0
  TheoreticalExact = false
  Type = 4
  UnderTolerance = 0
  X = -23.1312
  Y = -26.8457
FEATURE [TechDraw::DrawViewDimension] Dimension105
  Arbitrary = false
  FormatSpec = %.2f
  Inverted = false
  LockPosition = false
  MeasureType = 1
  OverTolerance = 0
  References2D = -> [ProjItem020]
  Rotation = 0
  ScaleType = 0
  TheoreticalExact = false
  Type = 2
  UnderTolerance = 0
  X = -7.47427
  Y = -8.57738
FEATURE [TechDraw::DrawViewDimension] Dimension106
  Arbitrary = false
  FormatSpec = R%.2f
  Inverted = false
  LockPosition = false
  MeasureType = 1
  OverTolerance = 0
  References2D = -> [ProjItem020]
  Rotation = 0
  ScaleType = 0
  TheoreticalExact = false
  Type = 4
  UnderTolerance = 0
  X = 33.5993
  Y = 35.7942
FEATURE [TechDraw::DrawViewDimension] Dimension107
  Arbitrary = false
  FormatSpec = %.2f
  Inverted = false
  LockPosition = false
  MeasureType = 1
  OverTolerance = 0
  References2D = -> [ProjItem020]
  Rotation = 0
  ScaleType = 0
  TheoreticalExact = false
  Type = 2
  UnderTolerance = 0
  X = -51.7529
  Y = 20.1819
FEATURE [TechDraw::DrawViewDimension] Dimension108
  Arbitrary = false
  FormatSpec = %.2f
  Inverted = false
  LockPosition = false
  MeasureType = 1
  OverTolerance = 0
  References2D = -> [ProjItem020]
  Rotation = 0
  ScaleType = 0
  TheoreticalExact = false
  Type = 1
  UnderTolerance = 0
  X = 0.168841
  Y = 43.8487
FEATURE [TechDraw::DrawViewDimension] Dimension110
  Arbitrary = false
  FormatSpec = %.2f
  Inverted = false
  LockPosition = false
  MeasureType = 1
  OverTolerance = 0
  References2D = -> [ProjItem022]
  Rotation = 0
  ScaleType = 0
  TheoreticalExact = false
  Type = 1
  UnderTolerance = 0
  X = -1.35073
  Y = -42.1637
FEATURE [TechDraw::DrawViewDimension] Dimension112
  Arbitrary = false
  FormatSpec = R%.2f
  Inverted = false
  LockPosition = false
  MeasureType = 1
  OverTolerance = 0
  References2D = -> [ProjItem020]
  Rotation = 0
  ScaleType = 0
  TheoreticalExact = false
  Type = 4
  UnderTolerance = 0
  X = 33.937
  Y = -6.41595
FEATURE [TechDraw::DrawViewDimExtent] DimExtent
  Arbitrary = false
  CosmeticTags = 8700fea6-8002-462c-89df-1a145c2024fa | 8a1e8108-24cb-4a43-9cbc-b7cbf44119af
  DirExtent = 0
  FormatSpec = %.2f
  Inverted = false
  LockPosition = false
  MeasureType = 1
  OverTolerance = 0
  References2D = -> [ProjItem020]
  Rotation = 0
  ScaleType = 0
  Source = -> [ProjItem020]
  TheoreticalExact = false
  Type = 1
  UnderTolerance = 0
  X = 6.24711
  Y = 54.5356
FEATURE [TechDraw::DrawViewDimExtent] DimExtent001
  Arbitrary = false
  CosmeticTags = df12bcd5-bdd0-4ef3-8951-a326d0454793 | df686dcc-2ee4-43d9-a88d-5e767d662336
  DirExtent = 1
  FormatSpec = %.2f
  Inverted = false
  LockPosition = false
  MeasureType = 1
  OverTolerance = 0
  References2D = -> [ProjItem020]
  Rotation = 0
  ScaleType = 0
  Source = -> [ProjItem020]
  TheoreticalExact = false
  Type = 2
  UnderTolerance = 0
  X = -61.9645
  Y = 1.51957
FEATURE [TechDraw::DrawPage] Page005  label="y_idler_bracket_dwg"
  KeepUpdated = true
  NextBalloonIndex = 1
  ProjectionType = 0
  Template = -> Template005
  Views = -> [View006,ProjGroup005,Dimension098,Dimension099,Dimension100,Dimension101,Dimension102,Dimension103,Dimension104,Dimension105,Dimension106,Dimension107,Dimension108,Dimension110,Dimension112,DimExtent,DimExtent001]
FEATURE [TechDraw::DrawSVGTemplate] Template006
  EditableTexts = Author=Alex Neufeld; DWG_num=2020-101; Date=15/05/2020; Revision=2; Scale=NTS; Subtitle=3 Req.; Title=Heated Bed Support Bracket
  Height = 215.9
  Orientation = 1
  Width = 279.4
FEATURE [TechDraw::DrawViewPart] View007
  CoarseView = false
  Direction = (0.577,-0.577,0.577)
  Focus = 100
  HardHidden = false
  IsoCount = 0
  IsoHidden = false
  IsoVisible = false
  LockPosition = true
  Perspective = false
  Rotation = 0
  Scale = 0.5
  ScaleType = 2
  SeamHidden = false
  SeamVisible = true
  SmoothHidden = false
  SmoothVisible = true
  Source = -> [Body003]
  X = 49.5472
  XDirection = (0.707,0.707,0)
  Y = 186.724
FEATURE [TechDraw::DrawProjGroupItem] ProjItem023  label="Front006"
  CoarseView = false
  Direction = (0,0,1)
  Focus = 100
  HardHidden = false
  IsoCount = 0
  IsoHidden = false
  IsoVisible = false
  LockPosition = true
  Perspective = false
  Rotation = 0
  RotationVector = (1,0,0)
  ScaleType = 2
  SeamHidden = false
  SeamVisible = true
  SmoothHidden = false
  SmoothVisible = true
  Source = -> [Body003]
  Type = 0
  X = 0
  XDirection = (1e-16,-1,0)
  Y = 0
FEATURE [TechDraw::DrawProjGroupItem] ProjItem024  label="Bottom005"
  CoarseView = false
  Direction = (-1,-1e-16,0)
  Focus = 100
  HardHidden = false
  IsoCount = 0
  IsoHidden = false
  IsoVisible = false
  LockPosition = true
  Perspective = false
  Rotation = 0
  RotationVector = (1,0,0)
  ScaleType = 2
  SeamHidden = false
  SeamVisible = true
  SmoothHidden = false
  SmoothVisible = true
  Source = -> [Body003]
  Type = 5
  X = 0
  XDirection = (1e-16,-1,0)
  Y = 53.1
FEATURE [TechDraw::DrawProjGroupItem] ProjItem025  label="Right002"
  CoarseView = false
  Direction = (1e-16,-1,1e-16)
  Focus = 100
  HardHidden = false
  IsoCount = 0
  IsoHidden = false
  IsoVisible = false
  LockPosition = true
  Perspective = false
  Rotation = 0
  RotationVector = (1,0,0)
  ScaleType = 2
  SeamHidden = false
  SeamVisible = true
  SmoothHidden = false
  SmoothVisible = true
  Source = -> [Body003]
  Type = 2
  X = -122.429
  XDirection = (0,-1e-16,-1)
  Y = 0
FEATURE [TechDraw::DrawProjGroup] ProjGroup006
  Anchor = -> ProjItem023
  AutoDistribute = true
  LockPosition = false
  ProjectionType = 0
  Rotation = 0
  ScaleType = 0
  Source = -> [Body003]
  Views = -> [ProjItem023,ProjItem024,ProjItem025]
  X = 163.157
  Y = 88.6941
  spacingX = 15
  spacingY = 15
FEATURE [TechDraw::DrawViewDimExtent] DimExtent002
  Arbitrary = false
  CosmeticTags = 40a776e2-5fee-4af6-bf52-77ef4ba42de3 | 3502933f-edae-4da0-bb0d-b59fe228f185
  DirExtent = 1
  FormatSpec = %.1f
  Inverted = false
  LockPosition = false
  MeasureType = 1
  OverTolerance = 0
  References2D = -> [ProjItem024]
  Rotation = 0
  ScaleType = 0
  Source = -> [ProjItem024]
  TheoreticalExact = false
  Type = 2
  UnderTolerance = 0
  X = 93.829
  Y = -3.15097
FEATURE [TechDraw::DrawViewDimExtent] DimExtent003
  Arbitrary = false
  CosmeticTags = 56a5d33d-48c1-42c5-9a55-81271bc0a9cf | 7367f88c-4bb7-4e22-a4a2-363c2dde8282
  DirExtent = 0
  FormatSpec = %.1f
  Inverted = false
  LockPosition = false
  MeasureType = 1
  OverTolerance = 0
  References2D = -> [ProjItem024]
  Rotation = 0
  ScaleType = 0
  Source = -> [ProjItem024]
  TheoreticalExact = false
  Type = 1
  UnderTolerance = 0
  X = 4.5514
  Y = 26.6082
FEATURE [TechDraw::DrawViewDimension] Dimension114
  Arbitrary = false
  FormatSpec = %.1f
  Inverted = false
  LockPosition = false
  MeasureType = 1
  OverTolerance = 0
  References2D = -> [ProjItem023]
  Rotation = 0
  ScaleType = 0
  TheoreticalExact = false
  Type = 1
  UnderTolerance = 0
  X = 75
  Y = -8
FEATURE [TechDraw::DrawViewDimension] Dimension115
  Arbitrary = false
  FormatSpec = %.1f
  Inverted = false
  LockPosition = false
  MeasureType = 1
  OverTolerance = 0
  References2D = -> [ProjItem023]
  Rotation = 0
  ScaleType = 0
  TheoreticalExact = false
  Type = 2
  UnderTolerance = 0
  X = 40.6182
  Y = 0.972523
FEATURE [TechDraw::DrawViewDimension] Dimension116
  Arbitrary = false
  FormatSpec = %.1f
  Inverted = false
  LockPosition = false
  MeasureType = 1
  OverTolerance = 0
  References2D = -> [ProjItem025]
  Rotation = 0
  ScaleType = 0
  TheoreticalExact = false
  Type = 2
  UnderTolerance = 0
  X = -0.307206
  Y = 0.729392
FEATURE [TechDraw::DrawViewDimExtent] DimExtent004
  Arbitrary = false
  CosmeticTags = 63ff5876-13bd-4040-85b2-fb7422d9c357 | 3d9a6e47-d91b-4086-bc29-d26c843bf4b5
  DirExtent = 1
  FormatSpec = %.1f
  Inverted = false
  LockPosition = false
  MeasureType = 1
  OverTolerance = 0
  References2D = -> [ProjItem025]
  Rotation = 0
  ScaleType = 0
  Source = -> [ProjItem025]
  TheoreticalExact = false
  Type = 2
  UnderTolerance = 0
  X = 23.3405
  Y = -0.729392
FEATURE [TechDraw::DrawViewDimension] Dimension117
  Arbitrary = false
  FormatSpec = R%.1f
  Inverted = false
  LockPosition = false
  MeasureType = 1
  OverTolerance = 0
  References2D = -> [ProjItem024]
  Rotation = 0
  ScaleType = 0
  TheoreticalExact = false
  Type = 4
  UnderTolerance = 0
  X = -23.8268
  Y = 4.86261
FEATURE [TechDraw::DrawViewDimension] Dimension118
  Arbitrary = false
  FormatSpec = R%.1f
  Inverted = false
  LockPosition = false
  MeasureType = 1
  OverTolerance = 0
  References2D = -> [ProjItem023]
  Rotation = 0
  ScaleType = 0
  TheoreticalExact = false
  Type = 4
  UnderTolerance = 0
  X = -92.1465
  Y = -26.015
FEATURE [TechDraw::DrawViewDimension] Dimension119
  Arbitrary = false
  FormatSpec = %.1f
  Inverted = false
  LockPosition = false
  MeasureType = 1
  OverTolerance = 0
  References2D = -> [ProjItem023]
  Rotation = 0
  ScaleType = 0
  TheoreticalExact = false
  Type = 1
  UnderTolerance = 0
  X = -57.2569
  Y = -7.05079
FEATURE [TechDraw::DrawViewDimension] Dimension120
  Arbitrary = false
  FormatSpec = %.1f
  Inverted = false
  LockPosition = false
  MeasureType = 1
  OverTolerance = 0
  References2D = -> [ProjItem023]
  Rotation = 0
  ScaleType = 0
  TheoreticalExact = false
  Type = 1
  UnderTolerance = 0
  X = -76.713
  Y = 9.9804
FEATURE [TechDraw::DrawViewDimension] Dimension121
  Arbitrary = false
  FormatSpec = %.1f
  Inverted = false
  LockPosition = false
  MeasureType = 1
  OverTolerance = 0
  References2D = -> [ProjItem025]
  Rotation = 0
  ScaleType = 0
  TheoreticalExact = false
  Type = 6
  UnderTolerance = 0
  X = -23.9191
  Y = 0.11725
FEATURE [TechDraw::DrawPage] Page006  label="heated_bed_bracket_dwg"
  KeepUpdated = true
  NextBalloonIndex = 1
  ProjectionType = 0
  Template = -> Template006
  Views = -> [View007,ProjGroup006,DimExtent002,DimExtent003,Dimension114,Dimension115,Dimension116,DimExtent004,Dimension117,Dimension118,Dimension119,Dimension120,Dimension121]
FEATURE [TechDraw::DrawSVGTemplate] Template007
  EditableTexts = Author=Alex Neufeld; DWG_num=2020-106; Date=15/05/2020; Revision=1; Scale=NTS; Subtitle=For NEMA-17 motor; Title=Y-Axis Motor Bracket
  Height = 215.9
  Orientation = 1
  Width = 279.4
FEATURE [TechDraw::DrawViewPart] View008
  CoarseView = false
  Direction = (0.577,-0.577,0.577)
  Focus = 100
  HardHidden = false
  IsoCount = 0
  IsoHidden = false
  IsoVisible = false
  LockPosition = false
  Perspective = false
  Rotation = 0
  Scale = 0.5
  ScaleType = 0
  SeamHidden = false
  SeamVisible = true
  SmoothHidden = false
  SmoothVisible = true
  Source = -> [Body012]
  X = 242.69
  XDirection = (0.707,0.707,0)
  Y = 184.39
FEATURE [TechDraw::DrawProjGroupItem] ProjItem026  label="Front007"
  CoarseView = false
  Direction = (0,0,1)
  Focus = 100
  HardHidden = false
  IsoCount = 0
  IsoHidden = false
  IsoVisible = false
  LockPosition = true
  Perspective = false
  Rotation = 0
  RotationVector = (1,0,0)
  ScaleType = 2
  SeamHidden = false
  SeamVisible = true
  SmoothHidden = false
  SmoothVisible = true
  Source = -> [Body012]
  Type = 0
  X = 0
  XDirection = (-4e-16,-1,0)
  Y = 0
FEATURE [TechDraw::DrawProjGroupItem] ProjItem027  label="Right003"
  CoarseView = false
  Direction = (-4e-16,-1,1e-16)
  Focus = 100
  HardHidden = false
  IsoCount = 0
  IsoHidden = false
  IsoVisible = false
  LockPosition = false
  Perspective = false
  Rotation = 0
  RotationVector = (1,0,0)
  ScaleType = 2
  SeamHidden = false
  SeamVisible = true
  SmoothHidden = false
  SmoothVisible = true
  Source = -> [Body012]
  Type = 2
  X = -84
  XDirection = (0,-1e-16,-1)
  Y = 0
FEATURE [TechDraw::DrawProjGroupItem] ProjItem028  label="Top001"
  CoarseView = false
  Direction = (1,-4e-16,0)
  Focus = 100
  HardHidden = false
  IsoCount = 0
  IsoHidden = false
  IsoVisible = false
  LockPosition = false
  Perspective = false
  Rotation = 0
  RotationVector = (1,0,0)
  ScaleType = 2
  SeamHidden = false
  SeamVisible = true
  SmoothHidden = false
  SmoothVisible = true
  Source = -> [Body012]
  Type = 4
  X = 0
  XDirection = (-4e-16,-1,0)
  Y = -106
FEATURE [TechDraw::DrawProjGroup] ProjGroup007
  Anchor = -> ProjItem026
  AutoDistribute = true
  LockPosition = false
  ProjectionType = 0
  Rotation = 0
  ScaleType = 2
  Source = -> [Body012]
  Views = -> [ProjItem026,ProjItem027,ProjItem028]
  X = 145.185
  Y = 150.021
  spacingX = 15
  spacingY = 15
FEATURE [TechDraw::DrawSVGTemplate] Template008
  EditableTexts = Author=Alex Neufeld; DWG_num=2020-111; Date=25/05/2020; Revision=1; Scale=1:2; Subtitle=Machined from billet; Title=Carriage Block
  Height = 215.9
  Orientation = 1
  Width = 279.4
FEATURE [TechDraw::DrawViewDimExtent] DimExtent008
  Arbitrary = false
  CosmeticTags = 8c33582d-95ed-4aa9-a2d0-ead233a98ca5 | 017e66d9-6c33-44d2-9c4c-f5bcee75400a
  DirExtent = 0
  FormatSpec = %.3f
  Inverted = false
  LockPosition = false
  MeasureType = 1
  OverTolerance = 0
  References2D = -> [ProjItem026]
  Rotation = 0
  ScaleType = 0
  Source = -> [ProjItem026]
  TheoreticalExact = false
  Type = 1
  UnderTolerance = 0
  X = 4.51809
  Y = -59.3806
FEATURE [TechDraw::DrawViewDimExtent] DimExtent009
  Arbitrary = false
  CosmeticTags = 33c358d7-0935-451d-a329-d3cfb5a12dd9 | f2e4e8c7-4ce3-48db-91cc-559cde566c3c
  DirExtent = 1
  FormatSpec = %.3f
  Inverted = false
  LockPosition = false
  MeasureType = 1
  OverTolerance = 0
  References2D = -> [ProjItem026]
  Rotation = 0
  ScaleType = 0
  Source = -> [ProjItem026]
  TheoreticalExact = false
  Type = 2
  UnderTolerance = 0
  X = -124.57
  Y = -1.6136
FEATURE [TechDraw::DrawViewDimExtent] DimExtent010
  Arbitrary = false
  CosmeticTags = ca1011e4-35cd-4d74-8ad4-dd8f4e74e332 | 5ad15638-3d5c-41ac-8512-d2ffb9962dc3
  DirExtent = 1
  FormatSpec = %.3f
  Inverted = false
  LockPosition = false
  MeasureType = 1
  OverTolerance = 0
  References2D = -> [ProjItem028]
  Rotation = 0
  ScaleType = 0
  Source = -> [ProjItem028]
  TheoreticalExact = false
  Type = 2
  UnderTolerance = 0
  X = -56.7988
  Y = 1.29088
FEATURE [TechDraw::DrawPage] Page007  label="y_motor_mount_dwg"
  KeepUpdated = true
  NextBalloonIndex = 1
  ProjectionType = 0
  Template = -> Template007
  Views = -> [View008,ProjGroup007,DimExtent008,DimExtent009,DimExtent010]
FEATURE [Sketcher::SketchObject] Sketch082
  AttachmentOffset = pos=(0,0,6.35) rot=(0,0,1;0rad)
  MapMode = 5
  Placement = pos=(6.35,-1.4e-15,1.4e-15) rot=(0.57735,0.57735,0.57735;2.0944rad)
  Support = -> [YZ_Plane046]
  sketch-geometry (7):
    g0: Circle CenterX=-38 CenterY=40 CenterZ=0 NormalX=0 NormalY=0 NormalZ=1 AngleXU=0 Radius=1.5
    g1: Circle CenterX=-38 CenterY=24 CenterZ=0 NormalX=0 NormalY=0 NormalZ=1 AngleXU=0 Radius=1.5
    g2: Circle CenterX=-8 CenterY=40 CenterZ=0 NormalX=0 NormalY=0 NormalZ=1 AngleXU=0 Radius=1.5
    g3: Circle CenterX=-8 CenterY=24 CenterZ=0 NormalX=0 NormalY=0 NormalZ=1 AngleXU=0 Radius=1.5
    g4: Circle CenterX=35 CenterY=0 CenterZ=0 NormalX=0 NormalY=0 NormalZ=1 AngleXU=0 Radius=1.5
    g5: Circle CenterX=25 CenterY=52 CenterZ=0 NormalX=0 NormalY=0 NormalZ=1 AngleXU=0 Radius=2.5
    g6: Circle CenterX=-35 CenterY=0 CenterZ=0 NormalX=0 NormalY=0 NormalZ=1 AngleXU=0 Radius=1.5
  constraints (21):
    c: Vertical(g2,g3)
    c: Vertical(g0,g1)
    c: Horizontal(g0,g2)
    c: Horizontal(g1,g3)
    c: Equal(g0,g1)
    c: Equal(g1,g3)
    c: Equal(g3,g2)
    c: Diameter(g2) = 3
    c: DistanceX(g3,g-1) = 8
    c: DistanceY(g-1,g3) = 24
    c: DistanceY(g3,g2) = 16
    c: DistanceX(g1,g3) = 30
    c: PointOnObject(g4,g-1)
    c: Diameter(g4) = 3
    c: DistanceX(g-1,g4) = 35
    c: Diameter(g5) = 5
    c: DistanceY(g-1,g5) = 52
    c: DistanceX(g-1,g5) = 25
    c: PointOnObject(g6,g-1)
    c: Equal(g6,g4)
    c: DistanceX(g6,g-1) = 35
FEATURE [PartDesign::Pocket] Pocket022
  BaseFeature = -> Hole005
  Length = 5
  Length2 = 100
  Profile = -> Sketch082
  Type = 1
FEATURE [Sketcher::SketchObject] Sketch083
  MapMode = 5
  Placement = pos=(0,0,0) rot=(1,0,0;1.5708rad)
  Support = -> [XZ_Plane046]
  sketch-geometry (3):
    g0: Circle CenterX=70 CenterY=0 CenterZ=0 NormalX=0 NormalY=0 NormalZ=1 AngleXU=0 Radius=2.55
    g1: Circle CenterX=120 CenterY=0 CenterZ=0 NormalX=0 NormalY=0 NormalZ=1 AngleXU=0 Radius=2.55
    g2: Circle CenterX=95 CenterY=0 CenterZ=0 NormalX=0 NormalY=0 NormalZ=1 AngleXU=0 Radius=2.55
  constraints (9):
    c: PointOnObject(g0,g-1)
    c: PointOnObject(g1,g-1)
    c: PointOnObject(g2,g-1)
    c: Equal(g0,g2)
    c: Equal(g2,g1)
    c: Diameter(g1) = 5.1
    c: DistanceX(g2,g1) = 25
    c: DistanceX(g0,g2) = 25
    c: DistanceX(g-1,g0) = 70
FEATURE [PartDesign::Pocket] Pocket023
  BaseFeature = -> Pocket022
  Length = 5
  Length2 = 100
  Profile = -> Sketch083
  Type = 1
FEATURE [PartDesign::Fillet] Fillet007
  Base = -> Pocket023 [Edge82,Edge17,Edge24,Edge13]
  BaseFeature = -> Pocket023
  Radius = 6.35
  SupportTransform = true
FEATURE [Sketcher::SketchObject] Sketch084
  MapMode = 5
  Support = -> [XY_Plane046]
  sketch-geometry (4):
    g0: LineSegment StartX=10 StartY=4 StartZ=0 EndX=54 EndY=4 EndZ=0
    g1: LineSegment StartX=54 StartY=4 StartZ=0 EndX=54 EndY=-21 EndZ=0
    g2: LineSegment StartX=54 StartY=-21 StartZ=0 EndX=10 EndY=-21 EndZ=0
    g3: LineSegment StartX=10 StartY=-21 StartZ=0 EndX=10 EndY=4 EndZ=0
  constraints (12):
    c: Coincident(g0,g1)
    c: Coincident(g1,g2)
    c: Coincident(g2,g3)
    c: Coincident(g3,g0)
    c: Horizontal(g0)
    c: Horizontal(g2)
    c: Vertical(g1)
    c: Vertical(g3)
    c: DistanceX(g-1,g0) = 10
    c: DistanceX(g2,g2) = 44
    c: DistanceY(g3,g3) = 25
    c: DistanceY(g-1,g0) = 4
FEATURE [PartDesign::Pocket] Pocket024
  BaseFeature = -> Fillet007
  Length = 20
  Length2 = 100
  Midplane = true
  Profile = -> Sketch084
  Type = 0
FEATURE [PartDesign::Body] Body016
  Group = -> [Sketch037,Pad016,Sketch038,Pad017,Sketch039,Pocket013,Sketch040,Pocket014,Fillet002,Sketch041,Pocket015,Sketch042,Hole004,Sketch043,Hole005,Sketch082,Pocket022,Sketch083,Pocket023,Fillet007,Sketch084,Pocket024]
  Origin = -> Origin046
  Tip = -> Pocket024
FEATURE [App::Part] Part026  label="machined_carriage"
  Group = -> [Body016]
  Origin = -> Origin040
FEATURE [TechDraw::DrawViewPart] View009
  CoarseView = false
  Direction = (0.577,-0.577,0.577)
  Focus = 100
  HardHidden = false
  IsoCount = 0
  IsoHidden = false
  IsoVisible = false
  LockPosition = false
  Perspective = false
  Rotation = 0
  Scale = 0.33
  ScaleType = 0
  SeamHidden = false
  SeamVisible = true
  SmoothHidden = false
  SmoothVisible = true
  Source = -> [Part026]
  X = 34.7513
  XDirection = (0.707,0.707,0)
  Y = 180.756
FEATURE [TechDraw::DrawProjGroupItem] ProjItem029  label="Front008"
  CoarseView = false
  Direction = (0,-1,0)
  Focus = 100
  HardHidden = false
  IsoCount = 0
  IsoHidden = false
  IsoVisible = false
  LockPosition = true
  Perspective = false
  Rotation = 0
  RotationVector = (1,0,0)
  Scale = 0.5
  ScaleType = 2
  SeamHidden = false
  SeamVisible = true
  SmoothHidden = false
  SmoothVisible = true
  Source = -> [Part026]
  Type = 0
  X = 0
  XDirection = (1,0,0)
  Y = 0
FEATURE [TechDraw::DrawProjGroupItem] ProjItem030  label="Bottom006"
  CoarseView = false
  Direction = (0,0,-1)
  Focus = 100
  HardHidden = false
  IsoCount = 0
  IsoHidden = false
  IsoVisible = false
  LockPosition = true
  Perspective = false
  Rotation = 0
  RotationVector = (1,0,0)
  ScaleType = 2
  SeamHidden = false
  SeamVisible = true
  SmoothHidden = false
  SmoothVisible = true
  Source = -> [Part026]
  Type = 5
  X = 0
  XDirection = (1,0,0)
  Y = 75
FEATURE [TechDraw::DrawProjGroupItem] ProjItem031  label="Right004"
  CoarseView = false
  Direction = (1,-1e-16,0)
  Focus = 100
  HardHidden = false
  IsoCount = 0
  IsoHidden = false
  IsoVisible = false
  LockPosition = true
  Perspective = false
  Rotation = 0
  RotationVector = (1,0,0)
  ScaleType = 2
  SeamHidden = false
  SeamVisible = true
  SmoothHidden = false
  SmoothVisible = true
  Source = -> [Part026]
  Type = 2
  X = -78.175
  XDirection = (1e-16,1,0)
  Y = 0
FEATURE [TechDraw::DrawProjGroup] ProjGroup008
  Anchor = -> ProjItem029
  AutoDistribute = true
  LockPosition = true
  ProjectionType = 0
  Rotation = 0
  Scale = 0.5
  ScaleType = 2
  Source = -> [Part026]
  Views = -> [ProjItem029,ProjItem030,ProjItem031]
  X = 151.564
  Y = 83.8481
  spacingX = 15
  spacingY = 15
FEATURE [TechDraw::DrawViewDimExtent] DimExtent005
  Arbitrary = false
  CosmeticTags = 0b52134a-8e6d-49b5-af52-e823de50e186 | 81887f05-93b7-4f57-9f60-22745010a6d3
  DirExtent = 0
  FormatSpec = %.2f
  Inverted = false
  LockPosition = false
  MeasureType = 1
  OverTolerance = 0
  References2D = -> [ProjItem031]
  Rotation = 0
  ScaleType = 0
  Source = -> [ProjItem031]
  TheoreticalExact = false
  Type = 1
  UnderTolerance = 0
  X = 0.546024
  Y = -36.8813
FEATURE [TechDraw::DrawViewDimExtent] DimExtent006
  Arbitrary = false
  CosmeticTags = 3ffed1fc-5ad0-4ec7-b127-2a2c0d19fe92 | 0dd20677-cea0-4880-986b-66a6b66657e0
  DirExtent = 1
  FormatSpec = %.2f
  Inverted = false
  LockPosition = false
  MeasureType = 1
  OverTolerance = 0
  References2D = -> [ProjItem031]
  Rotation = 0
  ScaleType = 0
  Source = -> [ProjItem031]
  TheoreticalExact = false
  Type = 2
  UnderTolerance = 0
  X = -38.9861
  Y = 1.54868
FEATURE [TechDraw::DrawViewDimExtent] DimExtent007
  Arbitrary = false
  CosmeticTags = cf14e2b6-0178-4381-bba3-44740000f48a | 09ec5796-2379-4229-aecd-7de02c0fdcc3
  DirExtent = 0
  FormatSpec = %.2f
  Inverted = false
  LockPosition = false
  MeasureType = 1
  OverTolerance = 0
  References2D = -> [ProjItem029]
  Rotation = 0
  ScaleType = 0
  Source = -> [ProjItem029]
  TheoreticalExact = false
  Type = 1
  UnderTolerance = 0
  X = -2.12632
  Y = -52.8642
FEATURE [TechDraw::DrawViewDetail] Detail
  AnchorPoint = (0.6,0.3,0)
  BaseView = -> ProjItem031
  CoarseView = false
  Direction = (1,-1e-16,0)
  Focus = 100
  HardHidden = false
  IsoCount = 0
  IsoHidden = false
  IsoVisible = false
  LockPosition = false
  Perspective = false
  Radius = 15
  Reference = 1
  Rotation = 0
  ScaleType = 0
  SeamHidden = false
  SeamVisible = true
  SmoothHidden = false
  SmoothVisible = true
  Source = -> [Part026]
  X = 239.468
  XDirection = (1e-16,1,0)
  Y = 166.543
FEATURE [TechDraw::DrawViewDimension] Dimension122
  Arbitrary = false
  FormatSpec = %.2f
  Inverted = false
  LockPosition = false
  MeasureType = 1
  OverTolerance = 0
  References2D = -> [ProjItem031]
  Rotation = 0
  ScaleType = 0
  TheoreticalExact = false
  Type = 1
  UnderTolerance = 0
  X = -35.1344
  Y = 43.6728
FEATURE [TechDraw::DrawViewDimension] Dimension123
  Arbitrary = false
  FormatSpec = %.2f
  Inverted = false
  LockPosition = false
  MeasureType = 1
  OverTolerance = 0
  References2D = -> [ProjItem031]
  Rotation = 0
  ScaleType = 0
  TheoreticalExact = false
  Type = 1
  UnderTolerance = 0
  X = -1.81485
  Y = 52.077
FEATURE [TechDraw::DrawViewDimension] Dimension124
  Arbitrary = false
  FormatSpec = %.2f
  Inverted = false
  LockPosition = false
  MeasureType = 1
  OverTolerance = 0
  References2D = -> [ProjItem031]
  Rotation = 0
  ScaleType = 0
  TheoreticalExact = false
  Type = 1
  UnderTolerance = 0
  X = -5.76535
  Y = 36.2849
FEATURE [TechDraw::DrawViewDimension] Dimension125
  Arbitrary = false
  FormatSpec = %.2f
  Inverted = false
  LockPosition = false
  MeasureType = 1
  OverTolerance = 0
  References2D = -> [ProjItem031]
  Rotation = 0
  ScaleType = 0
  TheoreticalExact = false
  Type = 1
  UnderTolerance = 0
  X = -22
  Y = 17.732
FEATURE [TechDraw::DrawViewDimension] Dimension126
  Arbitrary = false
  FormatSpec = %.2f
  Inverted = false
  LockPosition = false
  MeasureType = 1
  OverTolerance = 0
  References2D = -> [ProjItem031]
  Rotation = 0
  ScaleType = 0
  TheoreticalExact = false
  Type = 1
  UnderTolerance = 0
  X = -10.718
  Y = 24.2808
FEATURE [TechDraw::DrawViewDimension] Dimension127
  Arbitrary = false
  FormatSpec = %.2f
  Inverted = false
  LockPosition = false
  MeasureType = 1
  OverTolerance = 0
  References2D = -> [ProjItem031]
  Rotation = 0
  ScaleType = 0
  TheoreticalExact = false
  Type = 1
  UnderTolerance = 0
  X = -11.5378
  Y = -9.88744
FEATURE [TechDraw::DrawViewDimension] Dimension128
  Arbitrary = false
  FormatSpec = %.2f
  Inverted = false
  LockPosition = false
  MeasureType = 1
  OverTolerance = 0
  References2D = -> [ProjItem031]
  Rotation = 0
  ScaleType = 0
  TheoreticalExact = false
  Type = 1
  UnderTolerance = 0
  X = -12.013
  Y = 5.78028
FEATURE [TechDraw::DrawViewDimension] Dimension129
  Arbitrary = false
  FormatSpec = %.2f
  Inverted = false
  LockPosition = false
  MeasureType = 1
  OverTolerance = 0
  References2D = -> [ProjItem031]
  Rotation = 0
  ScaleType = 0
  TheoreticalExact = false
  Type = 2
  UnderTolerance = 0
  X = -50.7316
  Y = 30.446
FEATURE [TechDraw::DrawViewDimension] Dimension130
  Arbitrary = false
  FormatSpec = %.2f
  Inverted = false
  LockPosition = false
  MeasureType = 1
  OverTolerance = 0
  References2D = -> [ProjItem031]
  Rotation = 0
  ScaleType = 0
  TheoreticalExact = false
  Type = 2
  UnderTolerance = 0
  X = 12.4007
  Y = 42.2097
FEATURE [TechDraw::DrawViewDimension] Dimension131
  Arbitrary = false
  FormatSpec = %.2f
  Inverted = false
  LockPosition = false
  MeasureType = 1
  OverTolerance = 0
  References2D = -> [ProjItem031]
  Rotation = 0
  ScaleType = 0
  TheoreticalExact = false
  Type = 2
  UnderTolerance = 0
  X = -47.4173
  Y = 1.82714
FEATURE [TechDraw::DrawViewDimension] Dimension132
  Arbitrary = false
  FormatSpec = %.2f
  Inverted = false
  LockPosition = false
  MeasureType = 1
  OverTolerance = 0
  References2D = -> [ProjItem029]
  Rotation = 0
  ScaleType = 0
  TheoreticalExact = false
  Type = 1
  UnderTolerance = 0
  X = -17.705
  Y = 21.9071
FEATURE [TechDraw::DrawViewDimension] Dimension133
  Arbitrary = false
  FormatSpec = %.2f
  Inverted = false
  LockPosition = false
  MeasureType = 1
  OverTolerance = 0
  References2D = -> [ProjItem029]
  Rotation = 0
  ScaleType = 0
  TheoreticalExact = false
  Type = 1
  UnderTolerance = 0
  X = -5.86702
  Y = 36.381
FEATURE [TechDraw::DrawViewDimension] Dimension134
  Arbitrary = false
  FormatSpec = %.2f
  Inverted = false
  LockPosition = false
  MeasureType = 1
  OverTolerance = 0
  References2D = -> [ProjItem029]
  Rotation = 0
  ScaleType = 0
  TheoreticalExact = false
  Type = 1
  UnderTolerance = 0
  X = -13.2974
  Y = -12.9991
FEATURE [TechDraw::DrawViewDimension] Dimension135
  Arbitrary = false
  FormatSpec = %.2f
  Inverted = false
  LockPosition = false
  MeasureType = 1
  OverTolerance = 0
  References2D = -> [ProjItem029]
  Rotation = 0
  ScaleType = 0
  TheoreticalExact = false
  Type = 1
  UnderTolerance = 0
  X = -17.2834
  Y = -20.9932
FEATURE [TechDraw::DrawViewDimension] Dimension137
  Arbitrary = false
  FormatSpec = %.2f
  Inverted = false
  LockPosition = false
  MeasureType = 1
  OverTolerance = 0
  References2D = -> [ProjItem029]
  Rotation = 0
  ScaleType = 0
  TheoreticalExact = false
  Type = 2
  UnderTolerance = 0
  X = -6.65506
  Y = 19.3725
FEATURE [TechDraw::DrawViewDimension] Dimension138
  Arbitrary = false
  FormatSpec = %.2f
  Inverted = false
  LockPosition = false
  MeasureType = 1
  OverTolerance = 0
  References2D = -> [ProjItem029]
  Rotation = 0
  ScaleType = 0
  TheoreticalExact = false
  Type = 2
  UnderTolerance = 0
  X = -41.3114
  Y = 6.58101
FEATURE [TechDraw::DrawViewDimension] Dimension139
  Arbitrary = false
  FormatSpec = %.2f
  Inverted = false
  LockPosition = false
  MeasureType = 1
  OverTolerance = 0
  References2D = -> [ProjItem031]
  Rotation = 0
  ScaleType = 0
  TheoreticalExact = false
  Type = 2
  UnderTolerance = 0
  X = -32.0512
  Y = 1.80996
FEATURE [TechDraw::DrawViewDimension] Dimension140
  Arbitrary = false
  FormatSpec = %.2f
  Inverted = false
  LockPosition = false
  MeasureType = 1
  OverTolerance = 0
  References2D = -> [Detail]
  Rotation = 0
  ScaleType = 0
  TheoreticalExact = false
  Type = 2
  UnderTolerance = 0
  X = -21.7884
  Y = -0.002626
FEATURE [TechDraw::DrawViewDimension] Dimension141
  Arbitrary = false
  FormatSpec = %.2f
  Inverted = false
  LockPosition = false
  MeasureType = 1
  OverTolerance = 0
  References2D = -> [Detail]
  Rotation = 0
  ScaleType = 0
  TheoreticalExact = false
  Type = 1
  UnderTolerance = 0
  X = -21.7021
  Y = 21.1806
FEATURE [TechDraw::DrawViewDimension] Dimension142
  Arbitrary = false
  FormatSpec = %.2f
  Inverted = false
  LockPosition = false
  MeasureType = 1
  OverTolerance = 0
  References2D = -> [Detail]
  Rotation = 0
  ScaleType = 0
  TheoreticalExact = false
  Type = 2
  UnderTolerance = 0
  X = 20.1901
  Y = 0.000218
FEATURE [TechDraw::DrawViewDimension] Dimension143
  Arbitrary = false
  FormatSpec = %.2f
  Inverted = false
  LockPosition = false
  MeasureType = 1
  OverTolerance = 0
  References2D = -> [ProjItem029]
  Rotation = 0
  ScaleType = 0
  TheoreticalExact = false
  Type = 2
  UnderTolerance = 0
  X = 47.1537
  Y = 13.8966
FEATURE [TechDraw::DrawViewDimension] Dimension144
  Arbitrary = false
  FormatSpec = %.2f
  Inverted = false
  LockPosition = false
  MeasureType = 1
  OverTolerance = 0
  References2D = -> [ProjItem029]
  Rotation = 0
  ScaleType = 0
  TheoreticalExact = false
  Type = 1
  UnderTolerance = 0
  X = -14.2172
  Y = -32.7571
FEATURE [TechDraw::DrawViewDimension] Dimension145
  Arbitrary = false
  FormatSpec = %.2f
  Inverted = false
  LockPosition = false
  MeasureType = 1
  OverTolerance = 0
  References2D = -> [ProjItem029]
  Rotation = 0
  ScaleType = 0
  TheoreticalExact = false
  Type = 1
  UnderTolerance = 0
  X = -6.15148
  Y = -38.2043
FEATURE [TechDraw::DrawViewDimension] Dimension146
  Arbitrary = false
  FormatSpec = %.2f
  Inverted = false
  LockPosition = false
  MeasureType = 1
  OverTolerance = 0
  References2D = -> [ProjItem029]
  Rotation = 0
  ScaleType = 0
  TheoreticalExact = false
  Type = 1
  UnderTolerance = 0
  X = 1.21389
  Y = -44.8965
FEATURE [TechDraw::DrawViewDimension] Dimension147
  Arbitrary = false
  FormatSpec = %.2f
  Inverted = false
  LockPosition = false
  MeasureType = 1
  OverTolerance = 0
  References2D = -> [ProjItem030]
  Rotation = 0
  ScaleType = 0
  TheoreticalExact = false
  Type = 1
  UnderTolerance = 0
  X = -5.8931
  Y = -28.1572
FEATURE [TechDraw::DrawViewDimension] Dimension151
  Arbitrary = false
  FormatSpec = %.2f
  Inverted = false
  LockPosition = false
  MeasureType = 1
  OverTolerance = 0
  References2D = -> [ProjItem031]
  Rotation = 0
  ScaleType = 0
  TheoreticalExact = false
  Type = 2
  UnderTolerance = 0
  X = 20.9262
  Y = 15.2759
FEATURE [TechDraw::DrawViewDimension] Dimension152
  Arbitrary = false
  FormatSpec = %.2f
  Inverted = false
  LockPosition = false
  MeasureType = 1
  OverTolerance = 0
  References2D = -> [ProjItem031]
  Rotation = 0
  ScaleType = 0
  TheoreticalExact = false
  Type = 2
  UnderTolerance = 0
  X = 28.2581
  Y = 12.2954
FEATURE [TechDraw::DrawViewDimension] Dimension153
  Arbitrary = false
  FormatSpec = %.2f
  Inverted = false
  LockPosition = false
  MeasureType = 1
  OverTolerance = 0
  References2D = -> [ProjItem030]
  Rotation = 0
  ScaleType = 0
  TheoreticalExact = false
  Type = 2
  UnderTolerance = 0
  X = 30.8298
  Y = 12.7841
FEATURE [TechDraw::DrawViewDimension] Dimension154
  Arbitrary = false
  FormatSpec = %.2f
  Inverted = false
  LockPosition = false
  MeasureType = 1
  OverTolerance = 0
  References2D = -> [ProjItem030]
  Rotation = 0
  ScaleType = 0
  TheoreticalExact = false
  Type = 2
  UnderTolerance = 0
  X = 36.2533
  Y = 10.6476
FEATURE [TechDraw::DrawViewDimension] Dimension155
  Arbitrary = false
  FormatSpec = %.2f
  Inverted = false
  LockPosition = false
  MeasureType = 1
  OverTolerance = 0
  References2D = -> [ProjItem030]
  Rotation = 0
  ScaleType = 0
  TheoreticalExact = false
  Type = 2
  UnderTolerance = 0
  X = 41.3679
  Y = 8.79513
FEATURE [TechDraw::DrawViewDimension] Dimension156
  Arbitrary = false
  FormatSpec = %.2f
  Inverted = false
  LockPosition = false
  MeasureType = 1
  OverTolerance = 0
  References2D = -> [ProjItem030]
  Rotation = 0
  ScaleType = 0
  TheoreticalExact = false
  Type = 2
  UnderTolerance = 0
  X = 46.9087
  Y = 7.44269
FEATURE [TechDraw::DrawViewDimension] Dimension157
  Arbitrary = false
  FormatSpec = %.2f
  Inverted = false
  LockPosition = false
  MeasureType = 1
  OverTolerance = 0
  References2D = -> [ProjItem031]
  Rotation = 0
  ScaleType = 0
  TheoreticalExact = false
  Type = 1
  UnderTolerance = 0
  X = -15
  Y = -15.9719
FEATURE [TechDraw::DrawViewDimension] Dimension158
  Arbitrary = false
  FormatSpec = %.2f
  Inverted = false
  LockPosition = false
  MeasureType = 1
  OverTolerance = 0
  References2D = -> [ProjItem031]
  Rotation = 0
  ScaleType = 0
  TheoreticalExact = false
  Type = 1
  UnderTolerance = 0
  X = 13.5722
  Y = 12.1156
FEATURE [TechDraw::DrawViewDimension] Dimension159
  Arbitrary = false
  FormatSpec = %.2f
  Inverted = false
  LockPosition = false
  MeasureType = 1
  OverTolerance = 0
  References2D = -> [ProjItem029]
  Rotation = 0
  ScaleType = 0
  TheoreticalExact = false
  Type = 2
  UnderTolerance = 0
  X = 37.5072
  Y = 15.9656
FEATURE [TechDraw::DrawViewDimension] Dimension160
  Arbitrary = false
  FormatSpec = %.2f
  Inverted = false
  LockPosition = false
  MeasureType = 1
  OverTolerance = 0
  References2D = -> [ProjItem029]
  Rotation = 0
  ScaleType = 0
  TheoreticalExact = false
  Type = 2
  UnderTolerance = 0
  X = 56.4313
  Y = 11.1361
FEATURE [TechDraw::DrawViewDimension] Dimension161
  Arbitrary = false
  FormatSpec = R%.2f
  Inverted = false
  LockPosition = false
  MeasureType = 1
  OverTolerance = 0
  References2D = -> [ProjItem031]
  Rotation = 0
  ScaleType = 0
  TheoreticalExact = false
  Type = 4
  UnderTolerance = 0
  X = 32.4588
  Y = -32.0479
FEATURE [TechDraw::DrawViewDimension] Dimension162
  Arbitrary = false
  FormatSpec = ⌀%.2f
  Inverted = false
  LockPosition = false
  MeasureType = 1
  OverTolerance = 0
  References2D = -> [ProjItem031]
  Rotation = 0
  ScaleType = 0
  TheoreticalExact = false
  Type = 5
  UnderTolerance = 0
  X = 32.272
  Y = -21.9629
FEATURE [TechDraw::DrawViewDimension] Dimension163
  Arbitrary = false
  FormatSpec = ⌀%.2f
  Inverted = false
  LockPosition = false
  MeasureType = 1
  OverTolerance = 0
  References2D = -> [ProjItem031]
  Rotation = 0
  ScaleType = 0
  TheoreticalExact = false
  Type = 5
  UnderTolerance = 0
  X = 29.8068
  Y = -11.8779
FEATURE [TechDraw::DrawViewDimension] Dimension164
  Arbitrary = false
  FormatSpec = ⌀%.2f
  Inverted = false
  LockPosition = false
  MeasureType = 1
  OverTolerance = 0
  References2D = -> [ProjItem029]
  Rotation = 0
  ScaleType = 0
  TheoreticalExact = false
  Type = 5
  UnderTolerance = 0
  X = 41.0827
  Y = -11.6026
FEATURE [TechDraw::DrawViewDimension] Dimension165
  Arbitrary = false
  FormatSpec = M%.0fx0.8
  Inverted = false
  LockPosition = false
  MeasureType = 1
  OverTolerance = 0
  References2D = -> [ProjItem031]
  Rotation = 0
  ScaleType = 0
  TheoreticalExact = false
  Type = 5
  UnderTolerance = 0
  X = 25.7777
  Y = 38.4619
FEATURE [TechDraw::DrawViewDimension] Dimension166
  Arbitrary = false
  FormatSpec = M%.0fx0.5
  Inverted = false
  LockPosition = false
  MeasureType = 1
  OverTolerance = 0
  References2D = -> [ProjItem031]
  Rotation = 0
  ScaleType = 0
  TheoreticalExact = false
  Type = 5
  UnderTolerance = 0
  X = 14.7301
  Y = -11.8659
FEATURE [TechDraw::DrawViewAnnotation] Annotation009
  Font = Sans Serif
  LineSpace = 80
  LockPosition = false
  MaxWidth = -1
  Rotation = 0
  ScaleType = 0
  Text = Counterbore depth 2.18mm
  TextSize = 2.5
  TextStyle = 0
  X = 41.3094
  Y = 48.5238
FEATURE [TechDraw::DrawLeaderLine] LeaderLine009
  AutoHorizontal = true
  EndSymbol = 7
  LeaderParent = -> ProjItem031
  LockPosition = true
  Rotation = 0
  Scalable = false
  ScaleType = 0
  StartSymbol = 0
  WayPoints = (3) [(0,0,0),(-378.275,62.2952,0),(-303.302,62.2952,0)]
  X = -40.0313
  Y = -56.1373
FEATURE [TechDraw::DrawPage] Page008  label="carriage_dwg"
  KeepUpdated = true
  NextBalloonIndex = 1
  ProjectionType = 0
  Template = -> Template008
  Views = -> [View009,ProjGroup008,DimExtent005,DimExtent006,DimExtent007,Detail,Dimension122,Dimension123,Dimension124,Dimension125,Dimension126,Dimension127,Dimension128,Dimension129,Dimension130,Dimension131,Dimension132,Dimension133,Dimension134,Dimension135,Dimension137,Dimension138,Dimension139,Dimension140,Dimension141,Dimension142,Dimension143,Dimension144,Dimension145,Dimension146,Dimension147,+18 more]
FEATURE [Sketcher::SketchObject] Sketch085
  MapMode = 5
  Placement = pos=(0,0,0) rot=(0.57735,0.57735,0.57735;2.0944rad)
  Support = -> [YZ_Plane099]
  sketch-geometry (4):
    g0: LineSegment StartX=0 StartY=0 StartZ=0 EndX=8.08004 EndY=0 EndZ=0
    g1: ArcOfCircle CenterX=8.08004 CenterY=7.47139 CenterZ=0 NormalX=0 NormalY=0 NormalZ=1 AngleXU=0 Radius=7.47139 StartAngle=4.71239 EndAngle=7.5108
    g2: ArcOfCircle CenterX=16.5072 CenterY=31.0557 CenterZ=0 NormalX=0 NormalY=0 NormalZ=1 AngleXU=0 Radius=17.5733 StartAngle=3.14159 EndAngle=4.36921
    g3: LineSegment StartX=-1.06608 StartY=31.0557 StartZ=0 EndX=-1.06608 EndY=57.8085 EndZ=0
  constraints (6):
    c: Coincident(g0,g-1)
    c: Horizontal(g0)
    c: Tangent(g3,g2) = 1.5708
    c: Tangent(g2,g1) = 1.5708
    c: Tangent(g1,g0) = -1.5708
    c: Vertical(g3)
FEATURE [Sketcher::SketchObject] Sketch086
  MapMode = 5
  Placement = pos=(0,0,0) rot=(1,0,0;1.5708rad)
  Support = -> [XZ_Plane099]
  sketch-geometry (2):
    g0: Circle CenterX=0 CenterY=0 CenterZ=0 NormalX=0 NormalY=0 NormalZ=1 AngleXU=0 Radius=2
    g1: Circle CenterX=0 CenterY=0 CenterZ=0 NormalX=0 NormalY=0 NormalZ=1 AngleXU=0 Radius=3
  constraints (4):
    c: Coincident(g0,g-1)
    c: Coincident(g1,g0)
    c: Diameter(g1) = 6
    c: Diameter(g0) = 4
FEATURE [PartDesign::AdditivePipe] AdditivePipe002
  AuxilleryCurvelinear = true
  AuxillerySpineTangent = false
  Binormal = (0,0,0)
  Mode = 2
  Placement = pos=(0,0,0) rot=(1,0,0;1.5708rad)
  Profile = -> Sketch086
  Spine = -> Sketch085
  SpineTangent = false
  Transformation = 0
  Transition = 0
FEATURE [PartDesign::Body] Body032  label="silicone_tube"
  Group = -> [Sketch085,Sketch086,AdditivePipe002]
  Origin = -> Origin099
  Placement = pos=(6.5,15,5.5) rot=(0,0,1;0rad)
  Tip = -> AdditivePipe002
FEATURE [App::Link] Link036  label="silicone_tube001"
  LinkPlacement = pos=(-6.50001,14.9999,5.49998) rot=(0,0,1;0rad)
  LinkedObject = -> Body032
  Placement = pos=(-6.50001,14.9999,5.49998) rot=(0,0,1;0rad)
FEATURE [Part::Cylinder] Cylinder005  label="Cylinder"
  Angle = 360
  AttacherType = Attacher::AttachEngine3D
  Height = 20
  Placement = pos=(0,0,-20) rot=(0,0,1;0rad)
  Radius = 3
FEATURE [Sketcher::SketchObject] Sketch087
  MapMode = 5
  Placement = pos=(0,0,0) rot=(1,0,0;1.5708rad)
  Support = -> [XZ_Plane101]
  sketch-geometry (5):
    g0: ArcOfCircle CenterX=1.32205 CenterY=0 CenterZ=0 NormalX=0 NormalY=0 NormalZ=1 AngleXU=0 Radius=1.32205 StartAngle=1.5708 EndAngle=3.14159
    g1: LineSegment StartX=1.32205 StartY=1.32205 StartZ=0 EndX=16.6441 EndY=1.32205 EndZ=0
    g2: ArcOfCircle CenterX=16.6441 CenterY=12.6746 CenterZ=0 NormalX=0 NormalY=0 NormalZ=1 AngleXU=0 Radius=11.3525 StartAngle=4.71239 EndAngle=7.33941
    g3: ArcOfCircle CenterX=31.8557 CenterY=39.5797 CenterZ=0 NormalX=0 NormalY=0 NormalZ=1 AngleXU=0 Radius=19.555 StartAngle=3.14159 EndAngle=4.19782
    g4: LineSegment StartX=12.3007 StartY=39.5797 StartZ=0 EndX=12.3007 EndY=66.5454 EndZ=0
  constraints (8):
    c: PointOnObject(g0,g-1)
    c: Coincident(g0,g-1)
    c: Horizontal(g1)
    c: Vertical(g4)
    c: Tangent(g3,g2) = 1.5708
    c: Tangent(g2,g1) = -1.5708
    c: Tangent(g1,g0) = 1.5708
    c: Tangent(g4,g3) = 1.5708
FEATURE [Sketcher::SketchObject] Sketch088
  MapMode = 5
  Support = -> [XY_Plane101]
  sketch-geometry (1):
    g0: Circle CenterX=0 CenterY=0 CenterZ=0 NormalX=0 NormalY=0 NormalZ=1 AngleXU=0 Radius=1
  constraints (2):
    c: Coincident(g0,g-1)
    c: Diameter(g0) = 2
FEATURE [PartDesign::AdditivePipe] AdditivePipe003
  AuxilleryCurvelinear = true
  AuxillerySpineTangent = false
  Binormal = (0,0,0)
  Mode = 2
  Profile = -> Sketch088
  Spine = -> Sketch087
  SpineTangent = false
  Transformation = 0
  Transition = 0
FEATURE [PartDesign::Body] Body033  label="Body034"
  Group = -> [Sketch087,Sketch088,AdditivePipe003]
  Origin = -> Origin101
  Placement = pos=(0,1,0) rot=(0,0,1;0rad)
  Tip = -> AdditivePipe003
FEATURE [App::Link] Link037  label="Body035"
  LinkPlacement = pos=(0,-1,0) rot=(0,0,1;0rad)
  LinkedObject = -> Body033
  Placement = pos=(0,-1,0) rot=(0,0,1;0rad)
FEATURE [App::Part] Part049  label="heater_cartridge"
  Group = -> [Cylinder005,Body033,Link037]
  Origin = -> Origin100
  Placement = pos=(-0.5,-7.5,-17.55) rot=(-0.707107,0.707107,0;3.14159rad)
FEATURE [App::Part] E3D_Volcano_Hotend_Assembly
  Group = -> [Part__Feature043,Part__Feature044,Part__Feature045,Part__Feature004,Part__Feature046,Part__Feature047,Part049]
  Origin = -> Origin053
  Placement = pos=(0,-6,-20.25) rot=(1,0,0;3.14159rad)
FEATURE [Part::Feature] Part__Feature1437  label="6541K34"
  Placement = pos=(-6.5,18.5,5.5) rot=(-1,0,0;1.5708rad)
  shape: bbox 8.422 x 5.953 x 9.675 mm, 36 faces (baked)
FEATURE [App::Link] Link038  label="6541K035"
  LinkPlacement = pos=(6.50004,18.4999,5.49997) rot=(1,0,0;1.5708rad)
  LinkedObject = -> Part__Feature1437
  Placement = pos=(6.50004,18.4999,5.49997) rot=(1,0,0;1.5708rad)
FEATURE [Part::FeaturePython] Screw010  label="M2.5x10-Screw"  # Fasteners workbench fastener (typed FeaturePython)
  Placement = pos=(13.5,-4.35,52.9) rot=(0,1,0;1.5708rad)
  diameter = 3
  invert = false
  length = 4
  lengthCustom = 10
  matchOuter = false
  offset = 0
  thread = false
  type = 20
FEATURE [Part::FeaturePython] Nut  label="M2.5-Nut"  # Fasteners workbench fastener (typed FeaturePython)
  Placement = pos=(4.5,-4.35,52.95) rot=(0,1,0;1.5708rad)
  diameter = 3
  invert = false
  matchOuter = false
  offset = 0
  thread = false
  type = 4
FEATURE [Sketcher::SketchObject] Sketch089
  MapMode = 5
  Support = -> [XY_Plane102]
  sketch-geometry (2):
    g0: Circle CenterX=0 CenterY=0 CenterZ=0 NormalX=0 NormalY=0 NormalZ=1 AngleXU=0 Radius=2
    g1: Circle CenterX=0 CenterY=0 CenterZ=0 NormalX=0 NormalY=0 NormalZ=1 AngleXU=0 Radius=1
  constraints (4):
    c: Coincident(g0,g-1)
    c: Coincident(g1,g0)
    c: Diameter(g0) = 4
    c: Diameter(g1) = 2
FEATURE [PartDesign::Pad] Pad030  label="Pad031"
  Length = 50
  Length2 = 100
  Profile = -> Sketch089
  Type = 0
FEATURE [Sketcher::SketchObject] Sketch090
  MapMode = 5
  Placement = pos=(0,0,0) rot=(0.57735,0.57735,0.57735;2.0944rad)
  Support = -> [YZ_Plane102]
  sketch-geometry (5):
    g0: LineSegment StartX=0 StartY=-0.5 StartZ=0 EndX=4 EndY=3.5 EndZ=0
    g1: LineSegment StartX=4 StartY=3.5 StartZ=0 EndX=4 EndY=-3.5 EndZ=0
    g2: LineSegment StartX=4 StartY=-3.5 StartZ=0 EndX=-4 EndY=-3.5 EndZ=0
    g3: LineSegment StartX=-4 StartY=-3.5 StartZ=0 EndX=-4 EndY=3.5 EndZ=0
    g4: LineSegment StartX=-4 StartY=3.5 StartZ=0 EndX=0 EndY=-0.5 EndZ=0
  constraints (13):
    c: PointOnObject(g0,g-2)
    c: Coincident(g0,g1)
    c: Coincident(g1,g2)
    c: Coincident(g2,g3)
    c: Coincident(g3,g4)
    c: Coincident(g4,g0)
    c: Symmetric(g0,g3,g-2)
    c: Symmetric(g2,g1,g-2)
    c: Vertical(g1)
    c: DistanceY(g0,g-1) = 0.5
    c: Angle(g0,g-1) = 2.35619
    c: DistanceX(g2,g2) = 8
    c: DistanceY(g1,g1) = 7
FEATURE [PartDesign::Pocket] Pocket025
  BaseFeature = -> Pad030
  Length = 5
  Length2 = 100
  Midplane = true
  Profile = -> Sketch090
  Type = 1
FEATURE [PartDesign::Body] Body034  label="bowden_tube"
  Group = -> [Sketch089,Pad030,Sketch090,Pocket025]
  Origin = -> Origin102
  Placement = pos=(0,-6,34) rot=(0,0,1;0rad)
  Tip = -> Pocket025
FEATURE [App::Part] Part032  label="watercooled_printhead"
  Group = -> [E3D_Volcano_Hotend_Assembly,Part035,Link016,Part036,Part038,Part__Feature1372,Part__Feature1373,Body021,Body032,Link036,Part__Feature1437,Link022,Screw010,Nut,Body034]
  Origin = -> Origin048
  Placement = pos=(85,-40,-25) rot=(0,0,1;4.71239rad)
FEATURE [App::Part] Part025  label="y_carriage"
  Group = -> [Part026,Part027,Part__Feature005,Part028,Group003,Part029,Part030,Part032,Solid_V_Wheel_Straight,Link020,Solid_V_Wheel_Eccentric,Link021]
  Origin = -> Origin039
  Placement = pos=(166.2,6.65e-14,29) rot=(-0.57735,-0.57735,-0.57735;2.0944rad)
FEATURE [Sketcher::SketchObject] Sketch091
  MapMode = 5
  Placement = pos=(0,0,0) rot=(1,0,0;1.5708rad)
  Support = -> [XZ_Plane104]
  sketch-geometry (22):
    g0: LineSegment StartX=-2.65 StartY=15 StartZ=0 EndX=9.65 EndY=15 EndZ=0
    g1: LineSegment StartX=16 StartY=8.65 StartZ=0 EndX=16 EndY=-8.65 EndZ=0
    g2: LineSegment StartX=9.65 StartY=-15 StartZ=0 EndX=-2.65 EndY=-15 EndZ=0
    g3: LineSegment StartX=-9 StartY=-8.65 StartZ=0 EndX=-9 EndY=-6 EndZ=0
    g4: ArcOfCircle CenterX=9.65 CenterY=8.65 CenterZ=0 NormalX=0 NormalY=0 NormalZ=1 AngleXU=0 Radius=6.35 StartAngle=0 EndAngle=1.5708
    g5: ArcOfCircle CenterX=-2.65 CenterY=8.65 CenterZ=0 NormalX=0 NormalY=0 NormalZ=1 AngleXU=0 Radius=6.35 StartAngle=1.5708 EndAngle=3.14159
    g6: ArcOfCircle CenterX=-2.65 CenterY=-8.65 CenterZ=0 NormalX=0 NormalY=0 NormalZ=1 AngleXU=0 Radius=6.35 StartAngle=3.14159 EndAngle=4.71239
    g7: ArcOfCircle CenterX=9.65 CenterY=-8.65 CenterZ=0 NormalX=0 NormalY=0 NormalZ=1 AngleXU=0 Radius=6.35 StartAngle=4.71239 EndAngle=6.28319
    g8: Circle CenterX=10 CenterY=10 CenterZ=0 NormalX=0 NormalY=0 NormalZ=1 AngleXU=0 Radius=3
    g9: ArcOfCircle CenterX=10 CenterY=-9.5 CenterZ=0 NormalX=0 NormalY=0 NormalZ=1 AngleXU=0 Radius=3 StartAngle=2e-16 EndAngle=3.14159
    g10: ArcOfCircle CenterX=10 CenterY=-10.5 CenterZ=0 NormalX=0 NormalY=0 NormalZ=1 AngleXU=0 Radius=3 StartAngle=3.14159 EndAngle=6.28319
    g11: LineSegment StartX=7 StartY=-9.5 StartZ=0 EndX=7 EndY=-10.5 EndZ=0
    g12: LineSegment StartX=13 StartY=-9.5 StartZ=0 EndX=13 EndY=-10.5 EndZ=0
    g13: GeomPoint X=10 Y=-10 Z=0
    g14: LineSegment [constr] StartX=10 StartY=-9.5 StartZ=0 EndX=10 EndY=-10 EndZ=0
    g15: LineSegment [constr] StartX=10 StartY=-10 StartZ=0 EndX=10 EndY=-10.5 EndZ=0
    g16: LineSegment StartX=-9 StartY=6 StartZ=0 EndX=-9 EndY=8.65 EndZ=0
    g17: LineSegment StartX=-9 StartY=6 StartZ=0 EndX=5 EndY=6 EndZ=0
    g18: LineSegment StartX=8 StartY=3 StartZ=0 EndX=8 EndY=-3 EndZ=0
    g19: LineSegment StartX=5 StartY=-6 StartZ=0 EndX=-9 EndY=-6 EndZ=0
    g20: ArcOfCircle CenterX=5 CenterY=3 CenterZ=0 NormalX=0 NormalY=0 NormalZ=1 AngleXU=0 Radius=3 StartAngle=0 EndAngle=1.5708
    g21: ArcOfCircle CenterX=5 CenterY=-3 CenterZ=0 NormalX=0 NormalY=0 NormalZ=1 AngleXU=0 Radius=3 StartAngle=4.71239 EndAngle=6.28319
  constraints (51):
    c: Horizontal(g0)
    c: Horizontal(g2)
    c: Vertical(g1)
    c: Tangent(g0,g4) = 1.5708
    c: Tangent(g1,g4) = 1.5708
    c: Tangent(g0,g5) = 1.5708
    c: Tangent(g2,g6) = 1.5708
    c: Tangent(g3,g6) = 1.5708
    c: Tangent(g1,g7) = 1.5708
    c: Tangent(g2,g7) = 1.5708
    c: Equal(g4,g5)
    c: Equal(g5,g6)
    c: Symmetric(g2,g0,g-1)
    c: DistanceY(g2,g0) = 30
    c: DistanceX(g-1,g1) = 16
    c: Radius(g4) = 6.35
    c: DistanceX(g16,g-1) = 9
    c: Tangent(g9,g12)
    c: Tangent(g9,g11)
    c: Tangent(g11,g10)
    c: Tangent(g12,g10)
    c: Vertical(g11)
    c: Equal(g9,g10)
    c: Equal(g9,g8)
    c: Diameter(g8) = 6
    c: DistanceY(g12,g12) = 1
    c: Vertical(g9,g8)
    c: DistanceX(g-1,g8) = 10
    c: Coincident(g14,g9)
    c: Coincident(g14,g13)
    c: Coincident(g15,g13)
    c: Coincident(g15,g10)
    c: Equal(g15,g14)
    c: Symmetric(g13,g8,g-1)
    c: DistanceY(g-1,g8) = 10
    c: Tangent(g3,g16)
    c: Coincident(g16,g17)
    c: Horizontal(g17)
    c: Coincident(g19,g3)
    c: Horizontal(g19)
    c: Tangent(g17,g20) = 1.5708
    c: Tangent(g18,g20) = 1.5708
    c: Tangent(g18,g21) = 1.5708
    c: Tangent(g19,g21) = 1.5708
    c: Equal(g21,g20)
    c: Radius(g20) = 3
    c: Vertical(g18)
    c: Symmetric(g3,g16,g-1)
    c: DistanceX(g-1,g18) = 8
    c: DistanceY(g3,g16) = 12
    c: Tangent(g16,g5) = 1.5708
FEATURE [PartDesign::Pad] Pad031  label="Pad032"
  Length = 10
  Length2 = 100
  Placement = pos=(0,0,0) rot=(1,0,0;1.5708rad)
  Profile = -> Sketch091
  Type = 0
FEATURE [Sketcher::SketchObject] Sketch092
  MapMode = 5
  Support = -> [XY_Plane104]
  expr: Constraints[0] = Pad031.Length / 2
  sketch-geometry (1):
    g0: Circle CenterX=-1 CenterY=-5 CenterZ=0 NormalX=0 NormalY=0 NormalZ=1 AngleXU=0 Radius=2.5
  constraints (3):
    c: DistanceY(g0,g-1) = 5
    c: Diameter(g0) = 5
    c: DistanceX(g0,g-1) = 1
FEATURE [PartDesign::Pocket] Pocket026
  BaseFeature = -> Pad031
  Length = 5
  Length2 = 100
  Midplane = true
  Placement = pos=(0,0,0) rot=(1,0,0;1.5708rad)
  Profile = -> Sketch092
  Type = 1
FEATURE [PartDesign::Body] Body035  label="y_idler_holder_v2"
  Group = -> [Sketch091,Pad031,Sketch092,Pocket026]
  Origin = -> Origin104
  Placement = pos=(0,-1,0) rot=(0,0,1;0rad)
  Tip = -> Pocket026
FEATURE [App::Part] Part020  label="y_axis_idler_assy"
  Group = -> [Cylinder003,Part__Feature033,Link008,Part023,M5x25_Screw_Copy,Link026,Body035]
  Origin = -> Origin027
  Placement = pos=(261,-6.89e-14,26.35) rot=(-0.57735,0.57735,0.57735;2.0944rad)
FEATURE [App::Part] Part015  label="carriage"
  Group = -> [Part__Feature001,Link007_i0,Link007_i1,Link007,Part__Feature002,Link007_i2,Group002,Part017,Part018,Part019,Part020,Part025,Document001,Endstop2,Link023,Screw,Group006,Link028,Part047,Body009]
  Origin = -> Origin022
  Placement = pos=(53.75,-7.5e-15,131.8) rot=(-0.57735,-0.57735,-0.57735;4.18879rad)
FEATURE [TechDraw::DrawSVGTemplate] Template009
  EditableTexts = Author=Alex neufeld; DWG_num=2020-010; Date=08/07/2020; Revision=1; Scale=NTS; Subtitle=1 Req.; Title=Y Axis Idler holder
  Height = 215.9
  Orientation = 1
  Width = 279.4
FEATURE [TechDraw::DrawProjGroupItem] ProjItem032  label="Front009"
  CoarseView = false
  Direction = (0.577,-0.577,0.577)
  Focus = 100
  HardHidden = false
  IsoCount = 0
  IsoHidden = false
  IsoVisible = false
  LockPosition = true
  Perspective = false
  Rotation = 0
  RotationVector = (0.707,0.707,0)
  ScaleType = 2
  SeamHidden = false
  SeamVisible = true
  SmoothHidden = false
  SmoothVisible = true
  Source = -> [Body035]
  Type = 0
  X = 0
  XDirection = (0.707,0.707,0)
  Y = 0
FEATURE [TechDraw::DrawProjGroup] ProjGroup009
  Anchor = -> ProjItem032
  AutoDistribute = true
  LockPosition = false
  ProjectionType = 0
  Rotation = 0
  ScaleType = 0
  Source = -> [Body035]
  Views = -> [ProjItem032]
  X = 33.3834
  Y = 182.193
  spacingX = 15
  spacingY = 15
FEATURE [TechDraw::DrawProjGroupItem] ProjItem033  label="Front010"
  CoarseView = false
  Direction = (0,1,0)
  Focus = 100
  HardHidden = false
  IsoCount = 0
  IsoHidden = false
  IsoVisible = false
  LockPosition = true
  Perspective = false
  Rotation = 0
  RotationVector = (-1,0,0)
  Scale = 2
  ScaleType = 2
  SeamHidden = false
  SeamVisible = true
  SmoothHidden = false
  SmoothVisible = true
  Source = -> [Body035]
  Type = 0
  X = 0
  XDirection = (-1,0,0)
  Y = 0
FEATURE [TechDraw::DrawProjGroupItem] ProjItem034  label="Bottom007"
  CoarseView = false
  Direction = (0,0,-1)
  Focus = 100
  HardHidden = false
  IsoCount = 0
  IsoHidden = false
  IsoVisible = false
  LockPosition = false
  Perspective = false
  Rotation = 0
  RotationVector = (1,0,0)
  Scale = 2
  ScaleType = 2
  SeamHidden = false
  SeamVisible = true
  SmoothHidden = false
  SmoothVisible = true
  Source = -> [Body035]
  Type = 5
  X = 0
  XDirection = (-1,0,0)
  Y = 75
FEATURE [TechDraw::DrawProjGroupItem] ProjItem035  label="Left005"
  CoarseView = false
  Direction = (1,1e-16,0)
  Focus = 100
  HardHidden = false
  IsoCount = 0
  IsoHidden = false
  IsoVisible = false
  LockPosition = false
  Perspective = false
  Rotation = 0
  RotationVector = (1,0,0)
  Scale = 2
  ScaleType = 2
  SeamHidden = false
  SeamVisible = true
  SmoothHidden = false
  SmoothVisible = true
  Source = -> [Body035]
  Type = 1
  X = 65
  XDirection = (-1e-16,1,0)
  Y = 0
FEATURE [TechDraw::DrawProjGroup] ProjGroup010
  Anchor = -> ProjItem033
  AutoDistribute = true
  LockPosition = false
  ProjectionType = 0
  Rotation = 0
  Scale = 2
  ScaleType = 2
  Source = -> [Body035]
  Views = -> [ProjItem033,ProjItem034,ProjItem035]
  X = 120.1
  Y = 98.1499
  spacingX = 15
  spacingY = 15
FEATURE [TechDraw::DrawViewDimension] Dimension167
  Arbitrary = false
  FormatSpec = %.3f
  Inverted = false
  LockPosition = false
  MeasureType = 1
  OverTolerance = 0
  References2D = -> [ProjItem034]
  Rotation = 0
  ScaleType = 0
  TheoreticalExact = false
  Type = 1
  UnderTolerance = 0
  X = -9.04591
  Y = 16.4411
FEATURE [TechDraw::DrawViewDimension] Dimension168
  Arbitrary = false
  FormatSpec = %.3f
  Inverted = false
  LockPosition = false
  MeasureType = 1
  OverTolerance = 0
  References2D = -> [ProjItem034]
  Rotation = 0
  ScaleType = 0
  TheoreticalExact = false
  Type = 2
  UnderTolerance = 0
  X = 28.9989
  Y = -3.3004
FEATURE [TechDraw::DrawViewDimension] Dimension169
  Arbitrary = false
  FormatSpec = %.3f
  Inverted = false
  LockPosition = false
  MeasureType = 1
  OverTolerance = 0
  References2D = -> [ProjItem033]
  Rotation = 0
  ScaleType = 0
  TheoreticalExact = false
  Type = 1
  UnderTolerance = 0
  X = -3.02004
  Y = -43.9785
FEATURE [TechDraw::DrawViewDimension] Dimension170
  Arbitrary = false
  FormatSpec = %.3f
  Inverted = false
  LockPosition = false
  MeasureType = 1
  OverTolerance = 0
  References2D = -> [ProjItem033]
  Rotation = 0
  ScaleType = 0
  TheoreticalExact = false
  Type = 2
  UnderTolerance = 0
  X = -43.5614
  Y = -21.914
FEATURE [TechDraw::DrawViewDimension] Dimension171
  Arbitrary = false
  FormatSpec = %.3f
  Inverted = false
  LockPosition = false
  MeasureType = 1
  OverTolerance = 0
  References2D = -> [ProjItem033]
  Rotation = 0
  ScaleType = 0
  TheoreticalExact = false
  Type = 2
  UnderTolerance = 0
  X = 25
  Y = -3.6e-15
FEATURE [TechDraw::DrawViewDimension] Dimension172
  Arbitrary = false
  FormatSpec = R%.3f
  Inverted = false
  LockPosition = false
  MeasureType = 1
  OverTolerance = 0
  References2D = -> [ProjItem033]
  Rotation = 0
  ScaleType = 0
  TheoreticalExact = false
  Type = 4
  UnderTolerance = 0
  X = -0.941315
  Y = -1.31784
FEATURE [TechDraw::DrawViewDimension] Dimension173
  Arbitrary = false
  FormatSpec = ⌀%.3f
  Inverted = false
  LockPosition = false
  MeasureType = 1
  OverTolerance = 0
  References2D = -> [ProjItem033]
  Rotation = 0
  ScaleType = 0
  TheoreticalExact = false
  Type = 5
  UnderTolerance = 0
  X = -32.5695
  Y = 38.0291
FEATURE [TechDraw::DrawViewDimExtent] DimExtent011
  Arbitrary = false
  CosmeticTags = 4f44505d-5166-429b-bd56-ebb3d7bf540a | 42bec0fc-47a3-41a0-9c52-be35370a75bc
  DirExtent = 1
  FormatSpec = %.3f
  Inverted = false
  LockPosition = false
  MeasureType = 1
  OverTolerance = 0
  References2D = -> [ProjItem035]
  Rotation = 0
  ScaleType = 0
  Source = -> [ProjItem035]
  TheoreticalExact = false
  Type = 2
  UnderTolerance = 0
  X = 14.308
  Y = 0.564789
FEATURE [TechDraw::DrawViewDimExtent] DimExtent012
  Arbitrary = false
  CosmeticTags = 225fc8d8-6159-4144-9f91-1bdc64712757 | b8afe412-8ad3-4052-9b81-7dccc0b6091b
  DirExtent = 0
  FormatSpec = %.3f
  Inverted = false
  LockPosition = false
  MeasureType = 1
  OverTolerance = 0
  References2D = -> [ProjItem035]
  Rotation = 0
  ScaleType = 0
  Source = -> [ProjItem035]
  TheoreticalExact = false
  Type = 1
  UnderTolerance = 0
  X = 2.82395
  Y = 44.6183
FEATURE [TechDraw::DrawViewDimension] Dimension174
  Arbitrary = false
  FormatSpec = %.3f
  Inverted = false
  LockPosition = false
  MeasureType = 1
  OverTolerance = 0
  References2D = -> [ProjItem033]
  Rotation = 0
  ScaleType = 0
  TheoreticalExact = false
  Type = 2
  UnderTolerance = 0
  X = -35.9053
  Y = 0.470657
FEATURE [TechDraw::DrawViewDimension] Dimension175
  Arbitrary = false
  FormatSpec = R%.3f
  Inverted = false
  LockPosition = false
  MeasureType = 1
  OverTolerance = 0
  References2D = -> [ProjItem033]
  Rotation = 0
  ScaleType = 0
  TheoreticalExact = false
  Type = 4
  UnderTolerance = 0
  X = 21.3365
  Y = 38.1233
FEATURE [TechDraw::DrawViewDimension] Dimension176
  Arbitrary = false
  FormatSpec = ⌀%.3f
  Inverted = false
  LockPosition = false
  MeasureType = 1
  OverTolerance = 0
  References2D = -> [ProjItem034]
  Rotation = 0
  ScaleType = 0
  TheoreticalExact = false
  Type = 5
  UnderTolerance = 0
  X = -14.8487
  Y = -24.2529
FEATURE [TechDraw::DrawViewDimension] Dimension177
  Arbitrary = false
  FormatSpec = %.3f
  Inverted = false
  LockPosition = false
  MeasureType = 1
  OverTolerance = 0
  References2D = -> [ProjItem033]
  Rotation = 0
  ScaleType = 0
  TheoreticalExact = false
  Type = 1
  UnderTolerance = 0
  X = 8
  Y = 9
FEATURE [TechDraw::DrawViewDimension] Dimension178
  Arbitrary = false
  FormatSpec = %.3f
  Inverted = false
  LockPosition = false
  MeasureType = 1
  OverTolerance = 0
  References2D = -> [ProjItem033]
  Rotation = 0
  ScaleType = 0
  TheoreticalExact = false
  Type = 1
  UnderTolerance = 0
  X = -20.9798
  Y = -36.221
FEATURE [TechDraw::DrawPage] Page009  label="y_tensioner"
  KeepUpdated = true
  NextBalloonIndex = 1
  ProjectionType = 0
  Template = -> Template009
  Views = -> [ProjGroup009,ProjGroup010,Dimension167,Dimension168,Dimension169,Dimension170,Dimension171,Dimension172,Dimension173,DimExtent011,DimExtent012,Dimension174,Dimension175,Dimension176,Dimension177,Dimension178]
FEATURE [Sketcher::SketchObject] Sketch093
  MapMode = 5
  Support = -> [XY_Plane105]
  expr: Constraints[43] = 60
  sketch-geometry (23):
    g0: LineSegment StartX=-34.6372 StartY=4.33805 StartZ=0 EndX=-20.1372 EndY=19.838 EndZ=0
    g1: LineSegment StartX=-15.5 StartY=21.85 StartZ=0 EndX=15.5 EndY=21.85 EndZ=0
    g2: LineSegment StartX=20.1372 StartY=19.838 StartZ=0 EndX=34.6372 EndY=4.33805 EndZ=0
    g3: LineSegment StartX=34.6372 StartY=-4.33805 StartZ=0 EndX=20.1372 EndY=-19.838 EndZ=0
    g4: LineSegment StartX=15.5 StartY=-21.85 StartZ=0 EndX=-15.5 EndY=-21.85 EndZ=0
    g5: LineSegment StartX=-20.1372 StartY=-19.838 StartZ=0 EndX=-34.6372 EndY=-4.33805 EndZ=0
    g6: ArcOfCircle CenterX=-30 CenterY=0 CenterZ=0 NormalX=0 NormalY=0 NormalZ=1 AngleXU=0 Radius=6.35 StartAngle=2.38952 EndAngle=3.89367
    g7: ArcOfCircle CenterX=-15.5 CenterY=15.5 CenterZ=0 NormalX=0 NormalY=0 NormalZ=1 AngleXU=0 Radius=6.35 StartAngle=1.5708 EndAngle=2.38952
    g8: ArcOfCircle CenterX=15.5 CenterY=15.5 CenterZ=0 NormalX=0 NormalY=0 NormalZ=1 AngleXU=0 Radius=6.35 StartAngle=0.752077 EndAngle=1.5708
    g9: ArcOfCircle CenterX=30 CenterY=0 CenterZ=0 NormalX=0 NormalY=0 NormalZ=1 AngleXU=0 Radius=6.35 StartAngle=5.53111 EndAngle=7.03526
    g10: ArcOfCircle CenterX=15.5 CenterY=-15.5 CenterZ=0 NormalX=0 NormalY=0 NormalZ=1 AngleXU=0 Radius=6.35 StartAngle=4.71239 EndAngle=5.53111
    g11: ArcOfCircle CenterX=-15.5 CenterY=-15.5 CenterZ=0 NormalX=0 NormalY=0 NormalZ=1 AngleXU=0 Radius=6.35 StartAngle=3.89367 EndAngle=4.71239
    g12: LineSegment [constr] StartX=-15.5 StartY=15.5 StartZ=0 EndX=15.5 EndY=15.5 EndZ=0
    g13: LineSegment [constr] StartX=15.5 StartY=15.5 StartZ=0 EndX=15.5 EndY=-15.5 EndZ=0
    g14: LineSegment [constr] StartX=15.5 StartY=-15.5 StartZ=0 EndX=-15.5 EndY=-15.5 EndZ=0
    g15: LineSegment [constr] StartX=-15.5 StartY=-15.5 StartZ=0 EndX=-15.5 EndY=15.5 EndZ=0
    g16: Circle CenterX=-15.5 CenterY=15.5 CenterZ=0 NormalX=0 NormalY=0 NormalZ=1 AngleXU=0 Radius=1.75
    g17: Circle CenterX=15.5 CenterY=15.5 CenterZ=0 NormalX=0 NormalY=0 NormalZ=1 AngleXU=0 Radius=1.75
    g18: Circle CenterX=15.5 CenterY=-15.5 CenterZ=0 NormalX=0 NormalY=0 NormalZ=1 AngleXU=0 Radius=1.75
    g19: Circle CenterX=-15.5 CenterY=-15.5 CenterZ=0 NormalX=0 NormalY=0 NormalZ=1 AngleXU=0 Radius=1.75
    g20: Circle CenterX=-30 CenterY=0 CenterZ=0 NormalX=0 NormalY=0 NormalZ=1 AngleXU=0 Radius=2.75
    g21: Circle CenterX=30 CenterY=0 CenterZ=0 NormalX=0 NormalY=0 NormalZ=1 AngleXU=0 Radius=2.75
    g22: Circle CenterX=0 CenterY=0 CenterZ=0 NormalX=0 NormalY=0 NormalZ=1 AngleXU=0 Radius=11.5
  constraints (49):
    c: Tangent(g0,g6) = 1.5708
    c: Tangent(g5,g6) = 1.5708
    c: Tangent(g0,g7) = 1.5708
    c: Tangent(g1,g7) = 1.5708
    c: Tangent(g1,g8) = 1.5708
    c: Tangent(g2,g8) = 1.5708
    c: Tangent(g2,g9) = 1.5708
    c: Tangent(g3,g9) = 1.5708
    c: Tangent(g3,g10) = 1.5708
    c: Tangent(g4,g10) = 1.5708
    c: Tangent(g4,g11) = 1.5708
    c: Tangent(g5,g11) = 1.5708
    c: Coincident(g12,g13)
    c: Coincident(g13,g14)
    c: Coincident(g14,g15)
    c: Coincident(g15,g12)
    c: Horizontal(g14)
    c: Vertical(g15)
    c: Coincident(g16,g12)
    c: Coincident(g17,g12)
    c: Coincident(g18,g13)
    c: Coincident(g19,g14)
    c: Equal(g16,g17)
    c: Equal(g17,g18)
    c: Equal(g18,g19)
    c: Diameter(g17) = 3.5
    c: Equal(g7,g6)
    c: Equal(g6,g11)
    c: Equal(g11,g10)
    c: Equal(g10,g8)
    c: Equal(g8,g9)
    c: Radius(g9) = 6.35
    c: Symmetric(g1,g4,g-1)
    c: Symmetric(g9,g6,g-2)
    c: Coincident(g20,g6)
    c: Coincident(g21,g9)
    c: PointOnObject(g6,g-1)
    c: Symmetric(g1,g1,g-2)
    c: Symmetric(g4,g4,g-2)
    c: Symmetric(g18,g17,g-1)
    c: Symmetric(g17,g16,g-2)
    c: Equal(g12,g13)
    c: DistanceX(g12,g12) = 31
    c: DistanceX(g6,g9) = 60
    c: Coincident(g8,g17)
    c: Coincident(g22,g-1)
    c: Diameter(g22) = 23
    c: Equal(g20,g21)
    c: Diameter(g21) = 5.5
FEATURE [PartDesign::Pad] Pad032  label="Pad033"
  Length = 6.35
  Length2 = 100
  Profile = -> Sketch093
  Type = 0
FEATURE [Sketcher::SketchObject] Sketch094
  MapMode = 5
  Support = -> [XY_Plane105]
  sketch-geometry (8):
    g0: LineSegment [constr] StartX=-15.5 StartY=15.5 StartZ=0 EndX=15.5 EndY=15.5 EndZ=0
    g1: LineSegment [constr] StartX=15.5 StartY=15.5 StartZ=0 EndX=15.5 EndY=-15.5 EndZ=0
    g2: LineSegment [constr] StartX=15.5 StartY=-15.5 StartZ=0 EndX=-15.5 EndY=-15.5 EndZ=0
    g3: LineSegment [constr] StartX=-15.5 StartY=-15.5 StartZ=0 EndX=-15.5 EndY=15.5 EndZ=0
    g4: Circle CenterX=-15.5 CenterY=15.5 CenterZ=0 NormalX=0 NormalY=0 NormalZ=1 AngleXU=0 Radius=3
    g5: Circle CenterX=15.5 CenterY=15.5 CenterZ=0 NormalX=0 NormalY=0 NormalZ=1 AngleXU=0 Radius=3
    g6: Circle CenterX=15.5 CenterY=-15.5 CenterZ=0 NormalX=0 NormalY=0 NormalZ=1 AngleXU=0 Radius=3
    g7: Circle CenterX=-15.5 CenterY=-15.5 CenterZ=0 NormalX=0 NormalY=0 NormalZ=1 AngleXU=0 Radius=3
  constraints (18):
    c: Coincident(g0,g1)
    c: Coincident(g1,g2)
    c: Coincident(g2,g3)
    c: Coincident(g3,g0)
    c: Horizontal(g2)
    c: Vertical(g3)
    c: Coincident(g4,g0)
    c: Coincident(g5,g0)
    c: Coincident(g6,g1)
    c: Coincident(g7,g2)
    c: Equal(g5,g4)
    c: Equal(g4,g7)
    c: Equal(g7,g6)
    c: Diameter(g5) = 6
    c: Symmetric(g5,g6,g-1)
    c: Symmetric(g5,g4,g-2)
    c: DistanceX(g0,g0) = 31
    c: Equal(g3,g0)
FEATURE [PartDesign::Pocket] Pocket027
  BaseFeature = -> Pad032
  Length = 3
  Length2 = 100
  Profile = -> Sketch094
  Reversed = true
  Type = 0
FEATURE [PartDesign::Body] Body036  label="z_motor_adaptor_plate"
  Group = -> [Sketch093,Pad032,Sketch094,Pocket027]
  Origin = -> Origin105
  Placement = pos=(25.4,0,500) rot=(0,0,1;1.5708rad)
  Tip = -> Pocket027
FEATURE [App::Part] Part003  label="frame_assembly"
  Group = -> [Part__Feature,Part004,Cylinder001,Link,Part__Feature073,Part044,CouplerASM,Link024,Link025,Group007,Screw006,Link030,Document,Body036]
  Origin = -> Origin003
FEATURE [Sketcher::SketchObject] Sketch095
  MapMode = 5
  Support = -> [XY_Plane021]
  sketch-geometry (3):
    g0: Circle CenterX=245 CenterY=44 CenterZ=0 NormalX=0 NormalY=0 NormalZ=1 AngleXU=0 Radius=4
    g1: Circle CenterX=335 CenterY=-24 CenterZ=0 NormalX=0 NormalY=0 NormalZ=1 AngleXU=0 Radius=4
    g2: Circle CenterX=245 CenterY=-93 CenterZ=0 NormalX=0 NormalY=0 NormalZ=1 AngleXU=0 Radius=4
  constraints (9):
    c: Equal(g2,g0)
    c: Equal(g0,g1)
    c: Diameter(g1) = 8
    c: Vertical(g2,g0)
    c: DistanceY(g-1,g0) = 44
    c: DistanceX(g-1,g0) = 245
    c: DistanceY(g2,g-1) = 93
    c: DistanceX(g-1,g1) = 335
    c: DistanceY(g1,g-1) = 24
FEATURE [PartDesign::Body] Body008
  Group = -> [Sketch018,Pad008,Sketch019,Pad009,Sketch020,Pocket010,Sketch021,Pocket009,Sketch095]
  Origin = -> Origin021
  Tip = -> Pocket009
FEATURE [App::Part] Part014  label="base_plate"
  Group = -> [Body008]
  Origin = -> Origin020
FEATURE [App::Part] Part  label="printer_assembly"
  Group = -> [Part003,Part009,Part014,Part015,Part043,Part__Feature1347,Raspberry_Pi_4_Model_B,Group005,Link031,Part__Feature1435,Part__Feature034]
  Origin = -> Origin
FEATURE [TechDraw::DrawSVGTemplate] Template010
  EditableTexts = Author=Alex Neufeld; DWG_num=2020-112; Date=11/07/2020; Revision=1; Scale=NTS; Subtitle=1 Req; Title=Z Axis Motor Bracket
  Height = 215.9
  Orientation = 1
  Width = 279.4
FEATURE [TechDraw::DrawProjGroupItem] ProjItem036  label="Front011"
  CoarseView = false
  Direction = (0,0,1)
  Focus = 100
  HardHidden = false
  IsoCount = 0
  IsoHidden = false
  IsoVisible = false
  LockPosition = true
  Perspective = false
  Rotation = 0
  RotationVector = (1,0,0)
  ScaleType = 2
  SeamHidden = false
  SeamVisible = true
  SmoothHidden = false
  SmoothVisible = true
  Source = -> [Body036]
  Type = 0
  X = 0
  XDirection = (1e-16,1,0)
  Y = 0
FEATURE [TechDraw::DrawProjGroup] ProjGroup011
  Anchor = -> ProjItem036
  AutoDistribute = true
  LockPosition = false
  ProjectionType = 0
  Rotation = 0
  ScaleType = 0
  Source = -> [Body036]
  Views = -> [ProjItem036]
  X = 139.7
  Y = 107.95
  spacingX = 15
  spacingY = 15
FEATURE [TechDraw::DrawViewDimExtent] DimExtent013
  Arbitrary = false
  CosmeticTags = b4d62288-45a0-4493-b462-dada78fb5f72 | ba20ee15-e9d9-4cfa-af9a-7a2251a67fee
  DirExtent = 0
  FormatSpec = %.3f
  Inverted = false
  LockPosition = false
  MeasureType = 1
  OverTolerance = 0
  References2D = -> [ProjItem036]
  Rotation = 0
  ScaleType = 0
  Source = -> [ProjItem036]
  TheoreticalExact = false
  Type = 1
  UnderTolerance = 0
  X = 2.15719
  Y = 33.0755
FEATURE [TechDraw::DrawViewDimExtent] DimExtent014
  Arbitrary = false
  CosmeticTags = 38caeeea-741a-4d1c-8500-c1ebbf708ce5 | 3d63ee3c-2b32-485c-9a31-cd0c80d53145
  DirExtent = 1
  FormatSpec = %.3f
  Inverted = false
  LockPosition = false
  MeasureType = 1
  OverTolerance = 0
  References2D = -> [ProjItem036]
  Rotation = 0
  ScaleType = 0
  Source = -> [ProjItem036]
  TheoreticalExact = false
  Type = 2
  UnderTolerance = 0
  X = 41.7766
  Y = -0.503435
FEATURE [TechDraw::DrawViewDimension] Dimension179
  Arbitrary = false
  FormatSpec = %.3f
  Inverted = false
  LockPosition = false
  MeasureType = 1
  OverTolerance = 0
  References2D = -> [ProjItem036]
  Rotation = 0
  ScaleType = 0
  TheoreticalExact = false
  Type = 1
  UnderTolerance = 0
  X = -0.34372
  Y = -37.8094
FEATURE [TechDraw::DrawViewDimension] Dimension180
  Arbitrary = false
  FormatSpec = ⌀%.3f
  Inverted = false
  LockPosition = false
  MeasureType = 1
  OverTolerance = 0
  References2D = -> [ProjItem036]
  Rotation = 0
  ScaleType = 0
  TheoreticalExact = false
  Type = 5
  UnderTolerance = 0
  X = -69.6032
  Y = 2.5779
FEATURE [TechDraw::DrawViewDimension] Dimension181
  Arbitrary = false
  FormatSpec = ⌀%.3f
  Inverted = false
  LockPosition = false
  MeasureType = 1
  OverTolerance = 0
  References2D = -> [ProjItem036]
  Rotation = 0
  ScaleType = 0
  TheoreticalExact = false
  Type = 5
  UnderTolerance = 0
  X = -4.2965
  Y = 0.716083
FEATURE [TechDraw::DrawViewDimension] Dimension182
  Arbitrary = false
  FormatSpec = ⌀%.3f
  Inverted = false
  LockPosition = false
  MeasureType = 1
  OverTolerance = 0
  References2D = -> [ProjItem036]
  Rotation = 0
  ScaleType = 0
  TheoreticalExact = false
  Type = 5
  UnderTolerance = 0
  X = 41.0745
  Y = 43.3087
FEATURE [TechDraw::DrawViewDimension] Dimension183
  Arbitrary = false
  FormatSpec = %.3f
  Inverted = false
  LockPosition = false
  MeasureType = 1
  OverTolerance = 0
  References2D = -> [ProjItem036]
  Rotation = 0
  ScaleType = 0
  TheoreticalExact = false
  Type = 1
  UnderTolerance = 0
  X = -2.00503
  Y = -17.5364
FEATURE [TechDraw::DrawViewDimension] Dimension184
  Arbitrary = false
  FormatSpec = %.3f
  Inverted = false
  LockPosition = false
  MeasureType = 1
  OverTolerance = 0
  References2D = -> [ProjItem036]
  Rotation = 0
  ScaleType = 0
  TheoreticalExact = false
  Type = 2
  UnderTolerance = 0
  X = -26.5951
  Y = 0.0656065
FEATURE [TechDraw::DrawPage] Page010  label="z_bracket"
  KeepUpdated = true
  NextBalloonIndex = 1
  ProjectionType = 0
  Template = -> Template010
  Views = -> [ProjGroup011,DimExtent013,DimExtent014,Dimension179,Dimension180,Dimension181,Dimension182,Dimension183,Dimension184]
FEATURE [App::DocumentObjectGroup] Group008  label="drawings"
  Group = -> [Page006,Page002,Page004,Page005,Page003,Page007,Page008,Page009,Page010]
